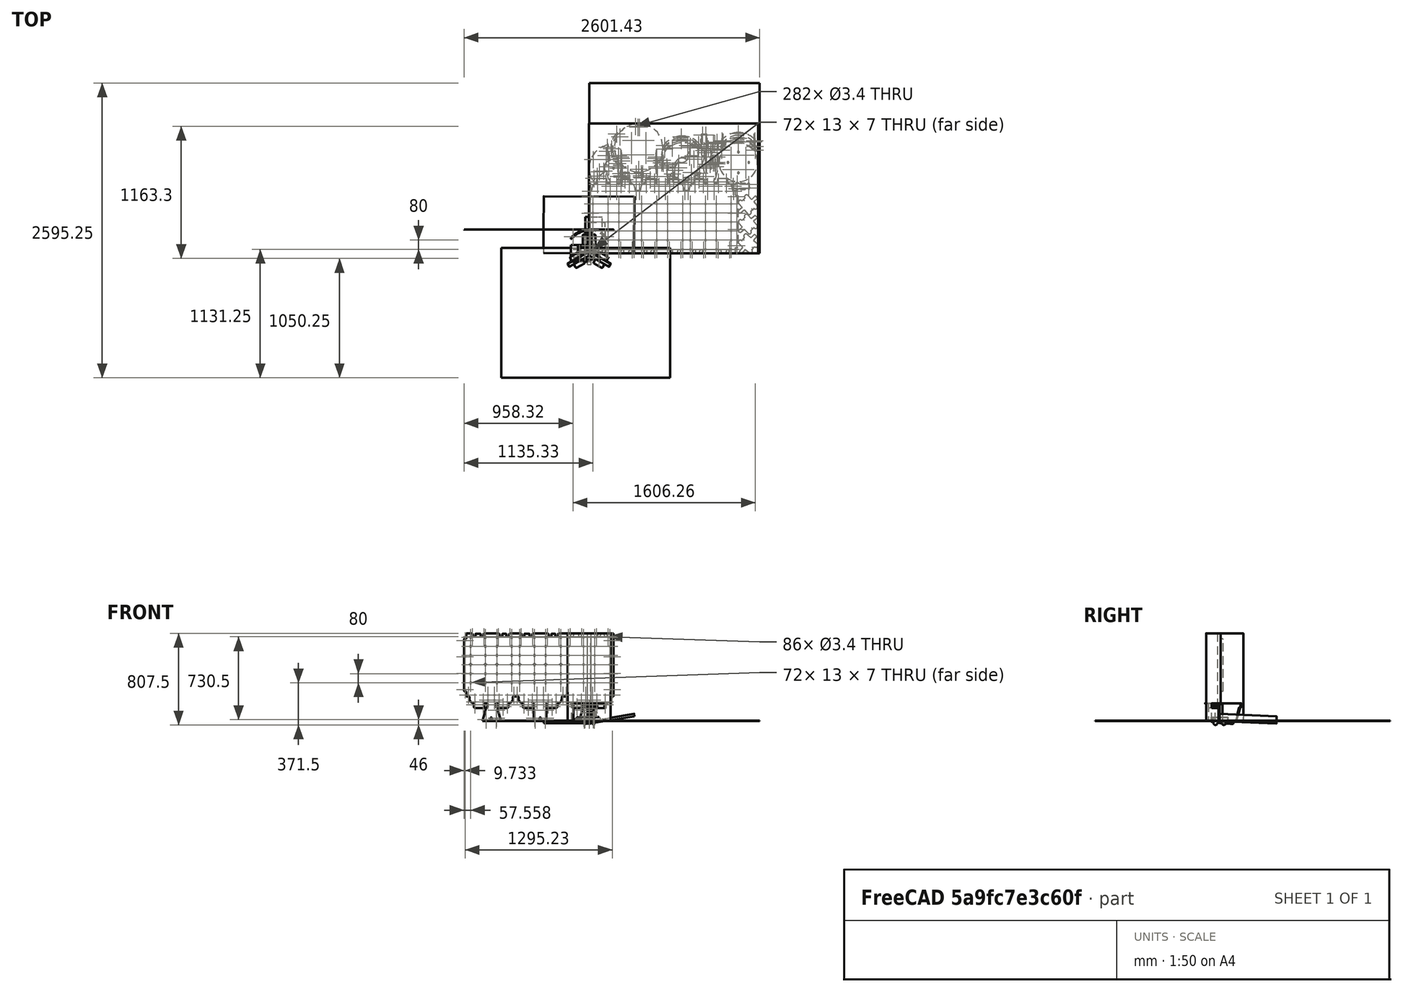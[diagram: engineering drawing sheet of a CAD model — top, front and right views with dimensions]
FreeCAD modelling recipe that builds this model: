
FCSTD DOCUMENT  (FreeCAD 0.21R31641 (Git))
Label: composit_stand_small_3_vertDroppers
License: All rights reserved
LicenseURL: http://en.wikipedia.org/wiki/All_rights_reserved
objects: Sketcher::SketchObject×99, Part::FeaturePython×74, PartDesign::Pocket×63, PartDesign::CoordinateSystem×53, PartDesign::Mirrored×27, App::DocumentObjectGroup×27, PartDesign::SubShapeBinder×27, PartDesign::Body×24, PartDesign::Plane×22, Path::FeaturePython×20, PartDesign::FeaturePython×17, PartDesign::Pad×15, Part::Part2DObjectPython×15, PartDesign::PolarPattern×13, PartDesign::MultiTransform×10, App::Link×9, Part::Feature×8, App::FeaturePython×6, Spreadsheet::Sheet×4, PartDesign::FeatureBase×3, +6 more types
note: 555 computed .brp shape members not serialized (recipe doc carries the construction recipe); baked Part::Feature solids carry a one-line shape summary decoded from their .brp

FEATURE [Spreadsheet::Sheet] Spreadsheet  label="module"
  cells = B2(module_width)==148mm; B3(module_height)==160mm; B4(module_fixture_distance_x)==132mm; C4(module_fixture_distance_y)==80mm; B5(module_hole_x)==13mm; B6(module_hole_y)==7mm
FEATURE [Spreadsheet::Sheet] Spreadsheet001  label="main"
  cells = B2(work_plane_width)==200mm; C2(top_cover_length)==108.4mm; D2(rivet_d)==3.4mm; B3(work_plane_height)==450mm; C3(work_plane_middle)==basin_height + work_plane_height / 2; D3(planes_fix_holes_distance)==130mm; B4(end_face_width)==32mm; C4(inner_width)==end_face_width - thickness * 2; D4(gutter_fix_holes_distance)==51mm; B5(basin_height)==157mm; B6(thickness)==3mm; C6(al_thickness)==0.3mm; D6(number_of_modules)=6; E6(modules_array_height)==<<module>>.module_height + (number_of_modules - 1) * <<module>>.module_fixture_distance_y; B7(total_length)==basin_height + distance_basin_cutout_modules_bottom + modules_array_height + distance_gutter_holes_modules_top + distance_gutter_holes_dropper_cutout + <<dropper>>.center_height_offset; D7(distance_basin_cutout_modules_bottom)==21mm; B8(bend_r)==0.01mm; D8(distance_gutter_holes_modules_top)==5mm; B9(cover_plane_bend)==0deg; D9(distance_gutter_holes_dropper_cutout)==12mm; B10(cover_bend_mid)==0deg
FEATURE [Sketcher::SketchObject] Sketch003  label="main_sketch"
  FullyConstrained = true
  MapMode = 5
  Support = -> [XY_Plane001]
  expr: Constraints[30] = <<main>>.end_face_width
  expr: Constraints[31] = <<main>>.work_plane_width
  expr: Constraints[44] = <<main>>.al_thickness
  sketch-geometry (17):
    g0: LineSegment StartX=-16 StartY=9.2376 StartZ=0 EndX=-16 EndY=209.238 EndZ=0
    g1: LineSegment StartX=-16 StartY=209.238 StartZ=0 EndX=16 EndY=209.238 EndZ=0
    g2: LineSegment StartX=16 StartY=209.238 StartZ=0 EndX=16 EndY=9.2376 EndZ=0
    g3: LineSegment StartX=16 StartY=9.2376 StartZ=0 EndX=189.205 EndY=-90.7624 EndZ=0
    g4: LineSegment StartX=189.205 StartY=-90.7624 StartZ=0 EndX=173.205 EndY=-118.475 EndZ=0
    g5: LineSegment StartX=173.205 StartY=-118.475 StartZ=0 EndX=0 EndY=-18.4752 EndZ=0
    g6: LineSegment StartX=0 StartY=-18.4752 StartZ=0 EndX=-173.205 EndY=-118.475 EndZ=0
    g7: LineSegment StartX=-173.205 StartY=-118.475 StartZ=0 EndX=-189.205 EndY=-90.7624 EndZ=0
    g8: LineSegment StartX=-189.205 StartY=-90.7624 StartZ=0 EndX=-16 EndY=9.2376 EndZ=0
    g9: LineSegment StartX=-16 StartY=9.2376 StartZ=0 EndX=0 EndY=0 EndZ=0
    g10: LineSegment StartX=0 StartY=0 StartZ=0 EndX=16 EndY=9.2376 EndZ=0
    g11: LineSegment StartX=0 StartY=0 StartZ=0 EndX=0 EndY=-18.4752 EndZ=0
    g12: LineSegment StartX=189.205 StartY=-90.7624 StartZ=0 EndX=13 EndY=10.9697 EndZ=0
    g13: LineSegment StartX=16 StartY=209.238 StartZ=0 EndX=16 EndY=9.42236 EndZ=0
    g14: LineSegment StartX=16 StartY=9.42236 StartZ=0 EndX=15.7 EndY=9.42236 EndZ=0
    g15: LineSegment StartX=13 StartY=10.9697 StartZ=0 EndX=13 EndY=30.9697 EndZ=0
    g16: LineSegment StartX=13 StartY=10.9697 StartZ=0 EndX=6.66667 EndY=0 EndZ=0
  constraints (56):
    c: Vertical(g0)
    c: Coincident(g0,g1)
    c: Horizontal(g1)
    c: Coincident(g1,g2)
    c: Vertical(g2)
    c: Coincident(g2,g3)
    c: Coincident(g3,g4)
    c: Coincident(g4,g5)
    c: PointOnObject(g5,g-2)
    c: Coincident(g5,g6)
    c: Coincident(g6,g7)
    c: Coincident(g8,g7)
    c: Equal(g2,g6)
    c: Equal(g6,g5)
    c: Equal(g5,g3)
    c: Equal(g4,g7)
    c: Equal(g7,g1)
    c: Perpendicular(g4,g5)
    c: Perpendicular(g4,g3)
    c: Perpendicular(g7,g6)
    c: Perpendicular(g8,g7)
    c: Angle(g6,g5) = 2.0944
    c: Angle(g3,g2) = 2.0944
    c: Coincident(g9,g0)
    c: Coincident(g9,g-1)
    c: Coincident(g10,g9)
    c: Coincident(g10,g2)
    c: Coincident(g11,g9)
    c: Coincident(g11,g5)
    c: Equal(g10,g11)
    c: DistanceX(g1,g1) = 32
    c: DistanceY(g2,g2) = 200
    c: DistanceY(g9,g2) = 9.2376  'petal_offset'
    c: DistanceY(g0) = 9.2376  'petal_conn_y'
    c: Coincident(g8,g0)
    c: DistanceX(g2) = 16  'petal_conn_x'
    c: Distance(g9,g1) = 209.848  'max_r'
    c: Distance(g10) = 18.4752  'planes_intersec_r'
    c: DistanceY(g9,g1) = 209.238  'total_petal_length'
    c: Coincident(g12,g4)
    c: Coincident(g13,g1)
    c: PointOnObject(g13,g2)
    c: Coincident(g14,g13)
    c: Horizontal(g14)
    c: DistanceX(g14,g14) = 0.3
    c: Distance(g14,g12) = 0.01
    c: PointOnObject(g2,g12)
    c: Distance(g12,g13) = 3
    c: Coincident(g15,g12)
    c: Vertical(g15)
    c: DistanceY(g15,g15) = 20
    c: DistanceY(g15) = 30.9697  'overlap_end_y'
    c: Coincident(g16,g12)
    c: Perpendicular(g16,g12)
    c: Distance(g9,g16) = 5.7735  'overlap_bend_offset'
    c: PointOnObject(g16,g-1)
FEATURE [PartDesign::FeaturePython] BaseBend001  # WARN: FeaturePython — macro-defined, semantics opaque (R4)
  BendSide = 0
  BendSketch = -> Sketch003
  MidPlane = false
  Reverse = false
  length = 774
  radius = 0.01
  thickness = 0.3
  expr: length = <<main>>.total_length
  expr: radius = <<main>>.bend_r
FEATURE [PartDesign::CoordinateSystem] Local_CS
  AttacherType = Attacher::AttachEngine3D
  AttachmentOffset = pos=(0,9.2376,0) rot=(0,0,1;0rad)
  MapMode = 5
  Placement = pos=(0,9.2376,0) rot=(0,0,1;0rad)
  Support = -> [XY_Plane001]
  expr: .AttachmentOffset.Base.y = Sketch003.Constraints.petal_offset
FEATURE [PartDesign::Plane] DatumPlane001
  AttachmentOffset = pos=(0,0,-100) rot=(0,0,1;0rad)
  Length = 488.253
  MapMode = 3
  Placement = pos=(0,109.238,-2.22e-14) rot=(1,0,0;1.5708rad)
  ResizeMode = 0
  Support = -> [Local_CS]
  Width = 908.956
  expr: .AttachmentOffset.Base.z = -<<main>>.work_plane_width / 2
FEATURE [Spreadsheet::Sheet] Spreadsheet002  label="dropper"
  cells = B2(d)==23.25mm; B3(fixture_d)=; B4(center_height_offset)==19mm; B5(distance_between_droppers1)==60mm; C5(distance_between_droppers2)==70mm
FEATURE [Sketcher::SketchObject] Sketch  label="gutter_side_sketch"
  FullyConstrained = true
  MapMode = 5
  Support = -> [XY_Plane]
  expr: .AttachmentOffset.Base.x = 0
  expr: .Constraints.little_distance = <<gutter>>.low_edge_length + (<<main>>.inner_width - <<main>>.thickness * 2) / 2 - 3mm
  expr: Constraints[12] = <<gutter>>.length
  expr: Constraints[27] = <<gutter>>.bend_angle + 90°
  sketch-geometry (15):
    g0: LineSegment StartX=0 StartY=150 StartZ=0 EndX=13.5 EndY=150 EndZ=0
    g1: LineSegment StartX=27 StartY=0 StartZ=0 EndX=0 EndY=0 EndZ=0
    g2: LineSegment StartX=15 StartY=148.5 StartZ=0 EndX=15 EndY=120 EndZ=0
    g3: LineSegment StartX=15 StartY=120 StartZ=0 EndX=31.2589 EndY=120 EndZ=0
    g4: GeomPoint X=27 Y=150 Z=0
    g5: ArcOfCircle CenterX=31.2589 CenterY=116.5 CenterZ=0 NormalX=0 NormalY=0 NormalZ=1 AngleXU=0 Radius=3.5 StartAngle=6.21662 EndAngle=7.85398
    g6: GeomPoint X=27 Y=0 Z=0
    g7: ArcOfCircle CenterX=13.5 CenterY=148.5 CenterZ=0 NormalX=0 NormalY=0 NormalZ=1 AngleXU=0 Radius=1.5 StartAngle=-3.6e-15 EndAngle=1.5708
    g8: GeomPoint X=15 Y=150 Z=0
    g9: LineSegment StartX=34.7511 StartY=116.267 StartZ=0 EndX=27.4178 EndY=6.26718 EndZ=0
    g10: LineSegment StartX=27.4178 StartY=6.26718 StartZ=0 EndX=27 EndY=0 EndZ=0
    g11: ArcOfCircle CenterX=23.9256 CenterY=6.5 CenterZ=0 NormalX=0 NormalY=0 NormalZ=1 AngleXU=0 Radius=3.5 StartAngle=4.71239 EndAngle=6.21662
    g12: LineSegment StartX=0 StartY=0 StartZ=0 EndX=0 EndY=3 EndZ=0
    g13: LineSegment StartX=0 StartY=3 StartZ=0 EndX=0 EndY=150 EndZ=0
    g14: LineSegment StartX=0 StartY=3 StartZ=0 EndX=23.9256 EndY=3 EndZ=0
  constraints (36):
    c: Coincident(g-1,g12)
    c: PointOnObject(g13,g-2)
    c: Coincident(g13,g0)
    c: Horizontal(g0)
    c: PointOnObject(g6,g-1)
    c: Coincident(g1,g12)
    c: Distance(g1,g6) = 27  'little_distance'
    c: Vertical(g2)
    c: Coincident(g3,g2)
    c: Horizontal(g3)
    c: DistanceY(g2,g8) = 30
    c: PointOnObject(g4,g0)
    c: Distance(g6,g4) = 150
    c: Distance(g0,g8) = 15
    c: Tangent(g3,g5) = 1.5708
    c: Diameter(g5) = 7
    c: PointOnObject(g8,g0)
    c: PointOnObject(g8,g2)
    c: Tangent(g0,g7) = 1.5708
    c: Tangent(g2,g7) = 1.5708
    c: Diameter(g7) = 3
    c: Tangent(g9,g5) = 1.5708
    c: Vertical(g4,g6)
    c: Coincident(g1,g6)
    c: Coincident(g10,g1)
    c: Coincident(g9,g10)
    c: Parallel(g9,g10)
    c: Angle(g10,g-1) = 1.63736
    c: Coincident(g12,g13)
    c: Vertical(g12)
    c: Coincident(g14,g12)
    c: Horizontal(g14)
    c: Tangent(g11,g9) = 1.5708
    c: Tangent(g14,g11) = -1.5708
    c: Equal(g11,g5)
    c: DistanceY(g12,g12) = 3
FEATURE [PartDesign::Pad] Pad  label="gutter_side_pad"
  Direction = (0,0,1)
  Length = 0.3
  Length2 = 10
  Profile = -> Sketch
  ReferenceAxis = -> Sketch [N_Axis]
  Type = 0
FEATURE [Sketcher::SketchObject] Sketch010
  FullyConstrained = true
  MapMode = 5
  Support = -> [XY_Plane]
  expr: Constraints[2] = -(<<main>>.inner_width / 2 - <<main>>.thickness - <<main>>.bend_r)
  expr: Constraints[3] = <<gutter>>.length
  sketch-geometry (1):
    g0: LineSegment StartX=-9.99 StartY=0 StartZ=0 EndX=-9.99 EndY=150 EndZ=0
  constraints (4):
    c: PointOnObject(g0,g-1)
    c: Vertical(g0)
    c: DistanceX(g0) = -9.99
    c: DistanceY(g0) = 150
FEATURE [PartDesign::Plane] DatumPlane002
  AttachmentOffset = pos=(0,0,407) rot=(0,0,1;0rad)
  Length = 449.761
  MapMode = 5
  Placement = pos=(0,0,407) rot=(0,0,1;0rad)
  ResizeMode = 0
  Support = -> [XY_Plane001]
  Width = 408.97
  expr: .AttachmentOffset.Base.z = <<main>>.work_plane_middle + 25mm
FEATURE [Sketcher::SketchObject] Sketch012
  FullyConstrained = true
  MapMode = 5
  Placement = pos=(0,0,0) rot=(0.57735,0.57735,0.57735;2.0944rad)
  Support = -> [YZ_Plane001]
  expr: Constraints[18] = <<main>>.total_length
  expr: Constraints[20] = <<main_sketch>>.Constraints.overlap_end_y
  sketch-geometry (10):
    g0: LineSegment StartX=0 StartY=0 StartZ=0 EndX=30.9697 EndY=0 EndZ=0
    g1: LineSegment StartX=30.9697 StartY=0 StartZ=0 EndX=30.9697 EndY=268 EndZ=0
    g2: LineSegment StartX=25.9697 StartY=263 StartZ=0 EndX=0 EndY=263 EndZ=0
    g3: LineSegment StartX=0 StartY=263 StartZ=0 EndX=0 EndY=0 EndZ=0
    g4: LineSegment StartX=0 StartY=774 StartZ=0 EndX=30.9697 EndY=774 EndZ=0
    g5: LineSegment StartX=30.9697 StartY=774 StartZ=0 EndX=30.9697 EndY=719 EndZ=0
    g6: LineSegment StartX=25.9697 StartY=724 StartZ=0 EndX=0 EndY=724 EndZ=0
    g7: LineSegment StartX=0 StartY=724 StartZ=0 EndX=0 EndY=774 EndZ=0
    g8: ArcOfCircle CenterX=25.9697 CenterY=268 CenterZ=0 NormalX=0 NormalY=0 NormalZ=1 AngleXU=0 Radius=5 StartAngle=4.71239 EndAngle=6.28319
    g9: ArcOfCircle CenterX=25.9697 CenterY=719 CenterZ=0 NormalX=0 NormalY=0 NormalZ=1 AngleXU=0 Radius=5 StartAngle=1.5481e-12 EndAngle=1.5708
  constraints (27):
    c: Coincident(g0,g1)
    c: Coincident(g2,g3)
    c: Coincident(g3,g0)
    c: Horizontal(g0)
    c: Horizontal(g2)
    c: Vertical(g1)
    c: Vertical(g3)
    c: Coincident(g0,g-1)
    c: DistanceY(g2) = 263  'bottom'
    c: Coincident(g4,g5)
    c: Coincident(g6,g7)
    c: Coincident(g7,g4)
    c: Horizontal(g4)
    c: Horizontal(g6)
    c: Vertical(g5)
    c: Vertical(g7)
    c: PointOnObject(g4,g-2)
    c: Vertical(g5,g1)
    c: DistanceY(g4) = 774
    c: DistanceY(g7,g7) = 50  'top'
    c: DistanceX(g0,g0) = 30.9697
    c: Tangent(g2,g8) = 1.5708
    c: Tangent(g1,g8) = -1.5708
    c: Tangent(g6,g9) = -1.5708
    c: Tangent(g9,g5) = 1.5708
    c: Equal(g9,g8)
    c: Diameter(g8) = 10
FEATURE [Sketcher::SketchObject] Sketch013
  AttachmentOffset = pos=(0,157,0) rot=(0,0,1;0rad)
  FullyConstrained = true
  MapMode = 5
  Placement = pos=(-3.49e-14,3.49e-14,157) rot=(0.57735,0.57735,0.57735;2.0944rad)
  Support = -> [YZ_Plane001]
  expr: .AttachmentOffset.Base.y = <<main>>.basin_height
  sketch-geometry (7):
    g0: LineSegment StartX=68 StartY=0 StartZ=0 EndX=0 EndY=0 EndZ=0
    g1: LineSegment StartX=0 StartY=0 StartZ=0 EndX=0 EndY=60 EndZ=0
    g2: LineSegment StartX=0 StartY=60 StartZ=0 EndX=31.9055 EndY=60 EndZ=0
    g3: LineSegment StartX=36.3804 StartY=57.2304 StartZ=0 EndX=63.525 EndY=2.76957 EndZ=0
    g4: ArcOfCircle CenterX=68 CenterY=5 CenterZ=0 NormalX=0 NormalY=0 NormalZ=1 AngleXU=0 Radius=5 StartAngle=3.60398 EndAngle=4.71239
    g5: ArcOfCircle CenterX=31.9055 CenterY=55 CenterZ=0 NormalX=0 NormalY=0 NormalZ=1 AngleXU=0 Radius=5 StartAngle=0.462386 EndAngle=1.5708
    g6: GeomPoint X=35 Y=60 Z=0
  constraints (17):
    c: PointOnObject(g0,g-1)
    c: Coincident(g0,g-1)
    c: Coincident(g0,g1)
    c: PointOnObject(g1,g-2)
    c: Coincident(g1,g2)
    c: Horizontal(g2)
    c: PointOnObject(g6,g2)
    c: PointOnObject(g6,g3)
    c: Tangent(g2,g5) = 1.5708
    c: Tangent(g3,g5) = 1.5708
    c: Tangent(g4,g3) = -1.5708
    c: Distance(g1) = 60
    c: Tangent(g4,g0) = 1.5708
    c: Diameter(g5) = 10
    c: Distance(g0) = 68
    c: DistanceX(g6) = 35
    c: Equal(g5,g4)
FEATURE [Spreadsheet::Sheet] Spreadsheet003  label="gutter"
  cells = B2(length)==150mm; C2(plane_middle)==60mm; B3(bend_angle)==atan((high_edge_length - low_edge_length) / length); B4(high_edge_length)==30mm; B5(low_edge_length)==20mm
FEATURE [PartDesign::Mirrored] Mirrored005
  BaseFeature = -> Pad
  MirrorPlane = -> YZ_Plane
  Originals = -> [Pad]
  Refine = true
FEATURE [PartDesign::CoordinateSystem] Local_CS001
  AttacherType = Attacher::AttachEngine3D
  AttachmentOffset = pos=(-30,0,0) rot=(0,0,1;0.066568rad)
  MapMode = 5
  Placement = pos=(-30,0,0) rot=(0,0,1;0.066568rad)
  Support = -> [XY_Plane]
  expr: .AttachmentOffset.Base.x = -(<<gutter>>.low_edge_length + (<<main>>.inner_width - <<main>>.thickness * 2) / 2)
  expr: .AttachmentOffset.Rotation.Angle = <<gutter>>.bend_angle
  expr: .AttachmentOffset.Rotation.Yaw = <<gutter>>.bend_angle
FEATURE [App::DocumentObjectGroup] Group  label="Tables"
  Group = -> [Spreadsheet,Spreadsheet001,Spreadsheet003,Spreadsheet002]
FEATURE [PartDesign::CoordinateSystem] Local_CS002
  AttacherType = Attacher::AttachEngine3D
  AttachmentOffset = pos=(30,0,0) rot=(0,0,1;-0.066568rad)
  MapMode = 5
  Placement = pos=(30,0,0) rot=(0,0,1;6.21662rad)
  Support = -> [XY_Plane]
  expr: .AttachmentOffset.Base.x = <<gutter>>.low_edge_length + (<<main>>.inner_width - <<main>>.thickness * 2) / 2
  expr: .AttachmentOffset.Rotation.Angle = -<<gutter>>.bend_angle
FEATURE [PartDesign::CoordinateSystem] Local_CS003
  AttacherType = Attacher::AttachEngine3D
  AttachmentOffset = pos=(0,60,0) rot=(0,0,1;1.5708rad)
  MapMode = 5
  Placement = pos=(33.9911,59.8671,0) rot=(0,0,1;1.50423rad)
  Support = -> [Local_CS002]
  expr: .AttachmentOffset.Base.y = <<gutter>>.plane_middle
FEATURE [PartDesign::CoordinateSystem] Local_CS004
  AttacherType = Attacher::AttachEngine3D
  AttachmentOffset = pos=(2,60,0) rot=(0,0,1;-1.5708rad)
  MapMode = 5
  Placement = pos=(-31.9956,60.0001,0) rot=(0,0,1;4.77896rad)
  Support = -> [Local_CS001]
  expr: .AttachmentOffset.Base.y = <<gutter>>.plane_middle
FEATURE [PartDesign::Plane] DatumPlane003
  Length = 91.4351
  MapMode = 4
  Placement = pos=(33.9911,59.8671,0) rot=(0.023538,0.706911,0.706911;3.09453rad)
  ResizeMode = 0
  Support = -> [Local_CS003]
  Width = 62.5599
FEATURE [PartDesign::Plane] DatumPlane004
  Length = 91.4351
  MapMode = 4
  Placement = pos=(-31.9956,60.0001,0) rot=(0.998893,0.03326,0.03326;1.5719rad)
  ResizeMode = 0
  Support = -> [Local_CS004]
  Width = 62.5599
FEATURE [PartDesign::Plane] DatumPlane005
  AttachmentOffset = pos=(0,-1,0) rot=(0,0,1;0rad)
  Length = 202.865
  MapMode = 5
  Placement = pos=(34.9889,59.8006,0) rot=(0,0,1;1.50423rad)
  ResizeMode = 0
  Support = -> [Local_CS003]
  Width = 102.646
FEATURE [PartDesign::Plane] DatumPlane006
  Length = 202.865
  MapMode = 5
  Placement = pos=(-31.9956,60.0001,0) rot=(0,0,-1;1.50423rad)
  ResizeMode = 0
  Support = -> [Local_CS004]
  Width = 102.646
FEATURE [Sketcher::SketchObject] Sketch037
  AttachmentOffset = pos=(30,2,0) rot=(0,0,1;0rad)
  FullyConstrained = true
  MapMode = 5
  Placement = pos=(33.9911,89.9337,0) rot=(0,0,1;1.50423rad)
  Support = -> [Local_CS003]
  expr: .AttachmentOffset.Base.x = <<dropper>>.distance_between_droppers1 / 2
  expr: Constraints[10] = <<dropper>>.d
  sketch-geometry (8):
    g0: LineSegment StartX=0 StartY=11.625 StartZ=0 EndX=1 EndY=11.625 EndZ=0
    g1: ArcOfCircle CenterX=1 CenterY=0 CenterZ=0 NormalX=0 NormalY=0 NormalZ=1 AngleXU=0 Radius=11.625 StartAngle=0.450911 EndAngle=1.5708
    g2: ArcOfCircle CenterX=17.127 CenterY=0 CenterZ=0 NormalX=0 NormalY=0 NormalZ=1 AngleXU=0 Radius=3 StartAngle=0.25268 EndAngle=1.29556
    g3: LineSegment StartX=12.0914 StartY=4.53943 StartZ=0 EndX=17.9423 EndY=2.88708 EndZ=0
    g4: LineSegment StartX=0 StartY=11.625 StartZ=0 EndX=0 EndY=0 EndZ=0
    g5: LineSegment StartX=0 StartY=0 StartZ=0 EndX=21 EndY=0 EndZ=0
    g6: ArcOfCircle CenterX=21 CenterY=1 CenterZ=0 NormalX=0 NormalY=0 NormalZ=1 AngleXU=0 Radius=1 StartAngle=3.39427 EndAngle=4.71239
    g7: ArcOfCircle CenterX=12.3631 CenterY=5.5018 CenterZ=0 NormalX=0 NormalY=0 NormalZ=1 AngleXU=0 Radius=1 StartAngle=3.5925 EndAngle=4.43715
  constraints (22):
    c: PointOnObject(g0,g-2)
    c: Horizontal(g0)
    c: PointOnObject(g2,g-1)
    c: Tangent(g3,g2) = 1.5708
    c: Tangent(g1,g0) = 1.5708
    c: Coincident(g4,g0)
    c: Coincident(g4,g-1)
    c: Coincident(g5,g4)
    c: Diameter(g2) = 6
    c: Angle(g3,g-1) = 0.275238
    c: Diameter(g1) = 23.25
    c: PointOnObject(g1,g-1)
    c: Distance(g0) = 1
    c: Horizontal(g5)
    c: Tangent(g6,g5) = -1.5708
    c: Tangent(g6,g2) = 1.5708
    c: Diameter(g6) = 2
    c: Distance(g5) = 21
    c: Tangent(g3,g7) = -1.5708
    c: Tangent(g1,g7) = 1.5708
    c: Diameter(g7) = 2
    c: DistanceY(g2) = 2.88708  'arc_height'
FEATURE [PartDesign::Pocket] Pocket008
  BaseFeature = -> Mirrored005
  Direction = (0,0,-1)
  Length = 5
  Length2 = 5
  Midplane = true
  Profile = -> Sketch037
  ReferenceAxis = -> Sketch037 [N_Axis]
  Type = 1
FEATURE [PartDesign::Mirrored] Mirrored006
  MirrorPlane = -> Sketch037 [V_Axis]
FEATURE [PartDesign::Mirrored] Mirrored007
  MirrorPlane = -> DatumPlane003
FEATURE [PartDesign::MultiTransform] MultiTransform002
  BaseFeature = -> Pocket008
  Originals = -> [Pocket008]
  Transformations = -> [Mirrored006,Mirrored007]
FEATURE [PartDesign::SubShapeBinder] Binder
  AttacherType = Attacher::AttachEngine3D
  AttachmentOffset = pos=(35,0,0) rot=(0,0,1;0rad)
  BindCopyOnChange = 0
  BindMode = 0
  ClaimChildren = true
  Context = -> Body [Binder.]
  Fuse = false
  MakeFace = true
  MapMode = 5
  OffsetFill = false
  OffsetIntersection = false
  OffsetJoinType = 0
  OffsetOpenResult = false
  PartialLoad = false
  Placement = pos=(-28.1674,25.0777,0) rot=(0,0,-1;1.50423rad)
  Relative = false
  _Version = 2
  expr: .AttachmentOffset.Base.x = <<dropper>>.distance_between_droppers2 / 2
FEATURE [PartDesign::Pocket] Pocket009
  BaseFeature = -> MultiTransform002
  Direction = (0,0,-1)
  Length = 5
  Length2 = 5
  Midplane = true
  Profile = -> Binder
  Type = 1
FEATURE [PartDesign::Plane] DatumPlane007
  Length = 91.4351
  MapMode = 4
  Placement = pos=(-28.1674,25.0777,0) rot=(0.998893,0.03326,0.03326;1.5719rad)
  ResizeMode = 0
  Support = -> [Binder]
  Width = 62.5599
FEATURE [PartDesign::Mirrored] Mirrored008
  MirrorPlane = -> DatumPlane007
FEATURE [PartDesign::Mirrored] Mirrored009
  MirrorPlane = -> DatumPlane004
FEATURE [PartDesign::MultiTransform] MultiTransform003
  BaseFeature = -> Pocket009
  Originals = -> [Pocket009]
  Transformations = -> [Mirrored008,Mirrored009]
FEATURE [Sketcher::SketchObject] Sketch038
  FullyConstrained = true
  MapMode = 5
  Support = -> [XY_Plane]
  expr: Constraints[2] = <<main>>.inner_width / 2 - <<main>>.thickness - <<main>>.bend_r
  expr: Constraints[3] = <<gutter>>.length
  sketch-geometry (1):
    g0: LineSegment StartX=9.99 StartY=0 StartZ=0 EndX=9.99 EndY=150 EndZ=0
  constraints (4):
    c: PointOnObject(g0,g-1)
    c: Vertical(g0)
    c: DistanceX(g0) = 9.99
    c: DistanceY(g0) = 150
FEATURE [Sketcher::SketchObject] Sketch039
  AttachmentOffset = pos=(51,14,0) rot=(0,0,1;0rad)
  FullyConstrained = true
  MapMode = 5
  Placement = pos=(24.4124,111.619,0) rot=(0,0,1;1.50423rad)
  Support = -> [DatumPlane005]
  expr: .AttachmentOffset.Base.x = <<main>>.gutter_fix_holes_distance
  expr: Constraints[1] = <<main>>.rivet_d
  sketch-geometry (1):
    g0: Circle CenterX=0 CenterY=0 CenterZ=0 NormalX=0 NormalY=0 NormalZ=1 AngleXU=0 Radius=1.7
  constraints (2):
    c: Coincident(g0,g-1)
    c: Diameter(g0) = 3.4
FEATURE [PartDesign::Pocket] Pocket010
  BaseFeature = -> MultiTransform003
  Direction = (0,0,-1)
  Length = 5
  Length2 = 5
  Midplane = true
  Profile = -> Sketch039
  ReferenceAxis = -> Sketch039 [N_Axis]
  Type = 1
FEATURE [PartDesign::Mirrored] Mirrored010
  MirrorPlane = -> DatumPlane003
FEATURE [PartDesign::Mirrored] Mirrored011
  MirrorPlane = -> YZ_Plane
FEATURE [PartDesign::MultiTransform] MultiTransform004
  BaseFeature = -> Pocket010
  Originals = -> [Pocket010]
  Transformations = -> [Mirrored010,Mirrored011]
FEATURE [PartDesign::FeaturePython] Fold  # WARN: FeaturePython — macro-defined, semantics opaque (R4)
  BaseFeature = -> MultiTransform004
  BendLine = -> Sketch038
  Position = 0
  angle = 90
  baseObject = -> MultiTransform004 [Face4]
  invert = false
  invertbend = true
  kfactor = 0.01
  radius = 0.01
  unfold = false
  expr: radius = <<main>>.bend_r
FEATURE [PartDesign::FeaturePython] Fold002  # WARN: FeaturePython — macro-defined, semantics opaque (R4)
  BaseFeature = -> Fold
  BendLine = -> Sketch010
  Position = 0
  angle = 90
  baseObject = -> Fold [Face2]
  invert = false
  invertbend = false
  kfactor = 0.01
  radius = 0.01
  unfold = false
  expr: radius = <<main>>.bend_r
FEATURE [PartDesign::CoordinateSystem] LCS_Origin
  AttacherType = Attacher::AttachEngine3D
  MapMode = 2
  Support = -> [X_Axis012]
FEATURE [App::DocumentObjectGroup] Constraints
FEATURE [App::FeaturePython] Variables  # WARN: FeaturePython — macro-defined, semantics opaque (R4)
  Type = App::PropertyContainer
FEATURE [App::DocumentObjectGroup] Configurations
FEATURE [PartDesign::CoordinateSystem] Local_CS008
  AttacherType = Attacher::AttachEngine3D
  MapMode = 5
  Support = -> [XY_Plane001]
FEATURE [App::Link] Body001001
  AssemblyType = Part::Link
  AttachedBy = #Local_CS008
  AttachedTo = Parent Assembly#LCS_Origin
  LinkedObject = -> Body001
  SolverId = Asm4EE
  expr: Placement = LCS_Origin.Placement * AttachmentOffset * Local_CS008.Placement ^ -1
FEATURE [App::Link] Body001003001
  AssemblyType = Part::Link
  AttachedBy = #Local_CS009
  AttachedTo = Body001001#Local_CS038
  AttachmentOffset = pos=(0,0,0) rot=(0.58,0.58,-0.58;2.0944rad)
  LinkPlacement = pos=(0,109.238,738) rot=(-0.707107,0,-0.707107;3.14159rad)
  LinkedObject = -> Body001003
  Placement = pos=(0,109.238,738) rot=(-0.707107,0,-0.707107;3.14159rad)
  SolverId = Asm4EE
  expr: Placement = Body001001.Placement * Local_CS038.Placement * AttachmentOffset * Local_CS009.Placement ^ -1
FEATURE [PartDesign::PolarPattern] PolarPattern002
  Angle = 240
  Axis = -> Z_Axis001
  Occurrences = 2
  Reversed = true
  expr: Angle = 120 * Occurrences
FEATURE [PartDesign::CoordinateSystem] Local_CS011
  AttacherType = Attacher::AttachEngine3D
  AttachmentOffset = pos=(0,100,0) rot=(0,0,1;0rad)
  MapMode = 5
  Placement = pos=(0,109.238,0) rot=(0,0,1;0rad)
  Support = -> [Local_CS]
  expr: .AttachmentOffset.Base.y = <<main>>.work_plane_width / 2
FEATURE [PartDesign::Plane] DatumPlane
  Length = 441.366
  MapMode = 4
  Placement = pos=(0,109.238,0) rot=(0.57735,0.57735,0.57735;2.0944rad)
  ResizeMode = 0
  Support = -> [Local_CS011]
  Width = 902.859
FEATURE [Sketcher::SketchObject] Sketch011
  AttachmentOffset = pos=(-88,277,0) rot=(0,0,1;0rad)
  FullyConstrained = true
  MapMode = 5
  Placement = pos=(0,21.2376,277) rot=(0.57735,0.57735,0.57735;2.0944rad)
  Support = -> [DatumPlane]
  expr: .AttachmentOffset.Base.x = -<<main>>.work_plane_width / 2 + 12mm
  expr: .AttachmentOffset.Base.y = <<main>>.work_plane_middle - <<main>>.planes_fix_holes_distance + 25mm
  expr: Constraints[1] = <<main>>.rivet_d
  sketch-geometry (1):
    g0: Circle CenterX=0 CenterY=0 CenterZ=0 NormalX=0 NormalY=0 NormalZ=1 AngleXU=0 Radius=1.7
  constraints (2):
    c: Coincident(g0,g-1)
    c: Diameter(g0) = 3.4
FEATURE [PartDesign::Plane] DatumPlane011
  AttachmentOffset = pos=(0,0,0) rot=(0,0,1;0.523599rad)
  Length = 594.137
  MapMode = 5
  Placement = pos=(0,0,0) rot=(0,0,1;0.523599rad)
  ResizeMode = 0
  Support = -> [XY_Plane001]
  Width = 579.207
FEATURE [PartDesign::Plane] DatumPlane013
  AttachmentOffset = pos=(0,0,0) rot=(0,-1,0;0.523599rad)
  Length = 622.32
  MapMode = 5
  Placement = pos=(0,0,0) rot=(0.935113,-0.250563,-0.250563;1.63783rad)
  ResizeMode = 0
  Support = -> [XZ_Plane001]
  Width = 924.952
FEATURE [PartDesign::Mirrored] Mirrored013
  MirrorPlane = -> DatumPlane013
FEATURE [PartDesign::Plane] DatumPlane014
  AttachmentOffset = pos=(0,0,0) rot=(0.447214,0.774597,-0.447214;1.82348rad)
  Length = 924.952
  MapMode = 5
  Placement = pos=(0,0,0) rot=(0.447214,0.774597,-0.447214;1.82348rad)
  ResizeMode = 0
  Support = -> [XY_Plane001]
  Width = 622.32
FEATURE [Sketcher::SketchObject] Sketch047
  FullyConstrained = true
  MapMode = 5
  Support = -> [XY_Plane015]
  expr: Constraints[16] = Sketch003.Constraints.max_r
  expr: Constraints[20] = <<main>>.work_plane_width
  sketch-geometry (8):
    g0: ArcOfCircle CenterX=0 CenterY=18.4752 CenterZ=0 NormalX=0 NormalY=0 NormalZ=1 AngleXU=0 Radius=60 StartAngle=0.539993 EndAngle=1.5708
    g1: ArcOfCircle CenterX=52.3205 CenterY=49.8371 CenterZ=0 NormalX=0 NormalY=0 NormalZ=1 AngleXU=0 Radius=1 StartAngle=3.68159 EndAngle=5.23599
    g2: LineSegment StartX=52.8205 StartY=48.9711 StartZ=0 EndX=172.268 EndY=117.934 EndZ=0
    g3: ArcOfCircle CenterX=171.768 CenterY=118.8 CenterZ=0 NormalX=0 NormalY=0 NormalZ=1 AngleXU=0 Radius=1 StartAngle=5.23599 EndAngle=6.88827
    g4: ArcOfCircle CenterX=0 CenterY=0 CenterZ=0 NormalX=0 NormalY=0 NormalZ=1 AngleXU=0 Radius=209.848 StartAngle=0.605088 EndAngle=1.5708
    g5: LineSegment StartX=3.7e-15 StartY=78.4752 StartZ=0 EndX=1.28e-14 EndY=209.848 EndZ=0
    g6: LineSegment StartX=52.8205 StartY=48.9711 StartZ=0 EndX=0 EndY=18.4752 EndZ=0
    g7: GeomPoint X=173.205 Y=118.475 Z=0
  constraints (22):
    c: PointOnObject(g0,g-2)
    c: PointOnObject(g4,g-2)
    c: Diameter(g1) = 2
    c: Diameter(g3) = 2
    c: Tangent(g1,g0) = 1.5708
    c: Tangent(g3,g2) = -1.5708
    c: Angle(g2,g-1) = 2.61799
    c: Coincident(g5,g0)
    c: Coincident(g5,g4)
    c: Tangent(g1,g2) = -1.5708
    c: Coincident(g6,g1)
    c: Tangent(g6,g2)
    c: Coincident(g6,g0)
    c: Diameter(g0) = 120
    c: PointOnObject(g7,g4)
    c: PointOnObject(g7,g2)
    c: DistanceY(g4) = 209.848
    c: Distance(g4,g0) = 18.4752  'major_r_offset'
    c: Coincident(g4,g-1)
    c: PointOnObject(g0,g-2)
    c: Distance(g0,g7) = 200
    c: Tangent(g3,g4) = -1.5708
FEATURE [PartDesign::Pad] Pad012
  Direction = (0,0,1)
  Length = 3
  Length2 = 10
  Profile = -> Sketch047
  ReferenceAxis = -> Sketch047 [N_Axis]
  Type = 0
FEATURE [PartDesign::CoordinateSystem] Local_CS013
  AttacherType = Attacher::AttachEngine3D
  MapMode = 5
  Support = -> [XY_Plane015]
FEATURE [PartDesign::CoordinateSystem] Local_CS015
  AttacherType = Attacher::AttachEngine3D
  AttachmentOffset = pos=(0,0,157) rot=(0,0,1;0rad)
  MapMode = 6
  Placement = pos=(189.205,-90.7624,157) rot=(0,0,1;3.14159rad)
  Support = -> [Sketch003,XY_Plane001]
  expr: .AttachmentOffset.Base.z = <<main>>.basin_height
FEATURE [App::Link] Body001003005002
  AssemblyType = Part::Link
  AttachedBy = #Local_CS013
  AttachedTo = Body001001#Local_CS025
  AttachmentOffset = pos=(0,0,0) rot=(0,0,1;3.14159rad)
  LinkPlacement = pos=(0,0,157) rot=(0,0,1;3.14159rad)
  LinkedObject = -> Body001003005
  Placement = pos=(0,0,157) rot=(0,0,1;3.14159rad)
  SolverId = Asm4EE
  expr: Placement = Body001001.Placement * Local_CS025.Placement * AttachmentOffset * Local_CS013.Placement ^ -1
FEATURE [PartDesign::CoordinateSystem] Local_CS016
  AttacherType = Attacher::AttachEngine3D
  AttachmentOffset = pos=(0,0,0) rot=(0,0,1;0.523599rad)
  MapMode = 5
  Placement = pos=(0,0,0) rot=(0,0,1;0.523599rad)
  Support = -> [XY_Plane015]
FEATURE [PartDesign::Plane] DatumPlane015
  Length = 495.835
  MapMode = 5
  Placement = pos=(0,0,0) rot=(0,0,1;0.523599rad)
  ResizeMode = 0
  Support = -> [Local_CS016]
  Width = 455.324
FEATURE [PartDesign::Plane] DatumPlane016
  Length = 79.989
  MapMode = 4
  Placement = pos=(86.82,84.1932,0) rot=(0.377964,0.654654,0.654654;2.41886rad)
  ResizeMode = 0
  Width = 61.6877
FEATURE [Sketcher::SketchObject] Sketch048
  FullyConstrained = true
  MapMode = 5
  Support = -> [XY_Plane016]
  expr: Constraints[1] = Sketch003.Constraints.max_r + 2.5mm
  sketch-geometry (1):
    g0: Circle CenterX=0 CenterY=0 CenterZ=0 NormalX=0 NormalY=0 NormalZ=1 AngleXU=0 Radius=212.348
  constraints (2):
    c: Coincident(g0,g-1)
    c: Radius(g0) = 212.348
FEATURE [PartDesign::Pad] Pad013
  Direction = (0,0,1)
  Length = 3
  Length2 = 10
  Profile = -> Sketch048
  ReferenceAxis = -> Sketch048 [N_Axis]
  Type = 0
  expr: Length = <<main>>.thickness
FEATURE [Sketcher::SketchObject] Sketch049
  AttachmentOffset = pos=(0,196.563,0) rot=(0,0,1;0rad)
  FullyConstrained = true
  MapMode = 5
  Placement = pos=(0,196.563,0) rot=(0,0,1;0rad)
  Support = -> [XY_Plane016]
  expr: .AttachmentOffset.Base.y = Sketch003.Constraints.total_petal_length - .Constraints.cut_width / 2 - 3.175mm - <<main>>.thickness
  expr: Constraints[10] = <<main>>.inner_width / 2
  expr: Constraints[14] = -<<main>>.inner_width / 2
  sketch-geometry (9):
    g0: ArcOfCircle CenterX=-13 CenterY=8.0875 CenterZ=0 NormalX=0 NormalY=0 NormalZ=1 AngleXU=0 Radius=1.5875 StartAngle=1.5708 EndAngle=4.71239
    g1: LineSegment StartX=-13 StartY=6.5 StartZ=0 EndX=9.825 EndY=6.5 EndZ=0
    g2: LineSegment StartX=9.825 StartY=6.5 StartZ=0 EndX=9.825 EndY=0 EndZ=0
    g3: LineSegment StartX=9.825 StartY=0 StartZ=0 EndX=13 EndY=0 EndZ=0
    g4: LineSegment StartX=13 StartY=0 StartZ=0 EndX=13 EndY=6.5 EndZ=0
    g5: LineSegment StartX=-13 StartY=9.675 StartZ=0 EndX=9.825 EndY=9.675 EndZ=0
    g6: ArcOfCircle CenterX=9.825 CenterY=6.5 CenterZ=0 NormalX=0 NormalY=0 NormalZ=1 AngleXU=0 Radius=3.175 StartAngle=1.117e-13 EndAngle=1.5708
    g7: GeomPoint X=9.825 Y=-6.5 Z=0
    g8: GeomPoint X=9.825 Y=-9.675 Z=0
  constraints (21):
    c: Horizontal(g1)
    c: PointOnObject(g2,g-1)
    c: Vertical(g2)
    c: Coincident(g3,g2)
    c: PointOnObject(g3,g-1)
    c: Coincident(g4,g3)
    c: Vertical(g4)
    c: Horizontal(g5)
    c: Tangent(g6,g4) = -1.5708
    c: Tangent(g6,g5) = 1.5708
    c: DistanceX(g3) = 13
    c: Tangent(g1,g0) = -1.5708
    c: Tangent(g5,g0) = 1.5708
    c: Diameter(g0) = 3.175
    c: DistanceX(g0) = -13
    c: Coincident(g6,g2)
    c: Coincident(g2,g1)
    c: Symmetric(g7,g1,g2)
    c: DistanceY(g7,g1) = 13  'cut_width'
    c: Symmetric(g8,g5,g2)
    c: DistanceY(g8,g5) = 19.35  'total_width'
FEATURE [Sketcher::SketchObject] Sketch050
  AttachmentOffset = pos=(0,196.563,0) rot=(0,0,1;0rad)
  FullyConstrained = true
  MapMode = 5
  Placement = pos=(0,196.563,0) rot=(0,0,1;0rad)
  Support = -> [XY_Plane016]
  expr: .AttachmentOffset.Base.y = Sketch049.AttachmentOffset.Base.y
  expr: .Constraints.cut_width = Sketch049.Constraints[18]
  expr: Constraints[10] = Sketch049.Constraints[10]
  expr: Constraints[13] = Sketch049.Constraints[13]
  expr: Constraints[14] = Sketch049.Constraints[14]
  expr: Constraints[29] = Sketch049.Constraints[10]
  expr: Constraints[32] = Sketch049.Constraints[13]
  expr: Constraints[33] = Sketch049.Constraints[14]
  sketch-geometry (17):
    g0: LineSegment StartX=-13 StartY=-8.0875 StartZ=0 EndX=-13 EndY=8.0875 EndZ=0
    g1: ArcOfCircle CenterX=-13 CenterY=8.0875 CenterZ=0 NormalX=0 NormalY=0 NormalZ=1 AngleXU=0 Radius=1.5875 StartAngle=1.5708 EndAngle=4.71239
    g2: LineSegment StartX=-13 StartY=6.5 StartZ=0 EndX=9.825 EndY=6.5 EndZ=0
    g3: LineSegment StartX=9.825 StartY=6.5 StartZ=0 EndX=9.825 EndY=0 EndZ=0
    g4: LineSegment StartX=9.825 StartY=0 StartZ=0 EndX=13 EndY=0 EndZ=0
    g5: LineSegment StartX=13 StartY=0 StartZ=0 EndX=13 EndY=6.5 EndZ=0
    g6: LineSegment StartX=-13 StartY=9.675 StartZ=0 EndX=9.825 EndY=9.675 EndZ=0
    g7: ArcOfCircle CenterX=9.825 CenterY=6.5 CenterZ=0 NormalX=0 NormalY=0 NormalZ=1 AngleXU=0 Radius=3.175 StartAngle=1.742e-13 EndAngle=1.5708
    g8: GeomPoint X=9.825 Y=-6.5 Z=0
    g9: ArcOfCircle CenterX=-11.5 CenterY=11.5875 CenterZ=0 NormalX=0 NormalY=0 NormalZ=1 AngleXU=0 Radius=1.5875 StartAngle=1.5708 EndAngle=4.71239
    g10: LineSegment StartX=-11.5 StartY=10 StartZ=0 EndX=9.825 EndY=10 EndZ=0
    g11: LineSegment StartX=9.825 StartY=10 StartZ=0 EndX=9.825 EndY=0 EndZ=0
    g12: LineSegment StartX=9.825 StartY=0 StartZ=0 EndX=13 EndY=0 EndZ=0
    g13: LineSegment StartX=13 StartY=0 StartZ=0 EndX=13 EndY=10 EndZ=0
    g14: LineSegment StartX=-11.5 StartY=13.175 StartZ=0 EndX=9.825 EndY=13.175 EndZ=0
    g15: ArcOfCircle CenterX=9.825 CenterY=10 CenterZ=0 NormalX=0 NormalY=0 NormalZ=1 AngleXU=0 Radius=3.175 StartAngle=1e-16 EndAngle=1.5708
    g16: GeomPoint X=9.825 Y=-10 Z=0
  constraints (40):
    c: Horizontal(g2)
    c: PointOnObject(g3,g-1)
    c: Vertical(g3)
    c: Coincident(g4,g3)
    c: PointOnObject(g4,g-1)
    c: Coincident(g5,g4)
    c: Vertical(g5)
    c: Horizontal(g6)
    c: Tangent(g7,g5) = -1.5708
    c: Tangent(g7,g6) = 1.5708
    c: DistanceX(g4) = 13
    c: Tangent(g2,g1) = -1.5708
    c: Tangent(g6,g1) = 1.5708
    c: Diameter(g1) = 3.175
    c: DistanceX(g1) = -13
    c: Coincident(g7,g3)
    c: Coincident(g3,g2)
    c: Symmetric(g8,g2,g3)
    c: DistanceY(g8,g2) = 13  'cut_width'
    c: Horizontal(g10)
    c: PointOnObject(g11,g-1)
    c: Vertical(g11)
    c: Coincident(g12,g11)
    c: PointOnObject(g12,g-1)
    c: Coincident(g13,g12)
    c: Vertical(g13)
    c: Horizontal(g14)
    c: Tangent(g15,g13) = -1.5708
    c: Tangent(g15,g14) = 1.5708
    c: DistanceX(g12) = 13
    c: Tangent(g10,g9) = -1.5708
    c: Tangent(g14,g9) = 1.5708
    c: Diameter(g9) = 3.175
    c: DistanceX(g9) = -11.5
    c: Coincident(g15,g11)
    c: Coincident(g11,g10)
    c: Symmetric(g16,g10,g11)
    c: DistanceY(g16,g10) = 20  'cut_width'
    c: Coincident(g0,g1)
    c: Symmetric(g0,g0,g-1)
FEATURE [PartDesign::CoordinateSystem] Local_CS017
  AttacherType = Attacher::AttachEngine3D
  AttachmentOffset = pos=(0,0,3) rot=(0,0,1;0rad)
  MapMode = 5
  Placement = pos=(0,0,3) rot=(0,0,1;0rad)
  Support = -> [XY_Plane016]
  expr: .AttachmentOffset.Base.z = <<main>>.thickness
FEATURE [App::Link] Body001003005003002
  AssemblyType = Part::Link
  AttachedBy = #Local_CS017
  AttachedTo = Parent Assembly#LCS_Origin
  AttachmentOffset = pos=(0,0,-3) rot=(0,1,0;3.14159rad)
  LinkPlacement = pos=(-4e-16,0,0) rot=(0,1,0;3.14159rad)
  LinkedObject = -> Body001003005003
  Placement = pos=(-4e-16,0,0) rot=(0,1,0;3.14159rad)
  SolverId = Asm4EE
  expr: Placement = LCS_Origin.Placement * AttachmentOffset * Local_CS017.Placement ^ -1
FEATURE [PartDesign::SubShapeBinder] Binder004
  AttacherType = Attacher::AttachEngine3D
  AttachmentOffset = pos=(0,196.563,0) rot=(0,0,1;3.14159rad)
  BindCopyOnChange = 0
  BindMode = 0
  ClaimChildren = false
  Context = -> Model [Body001003005003002.Binder004.]
  Fuse = false
  MakeFace = true
  MapMode = 5
  OffsetFill = false
  OffsetIntersection = false
  OffsetJoinType = 0
  OffsetOpenResult = false
  PartialLoad = false
  Placement = pos=(0,180.388,0) rot=(0,0,1;3.14159rad)
  Relative = false
  _Version = 2
  expr: .AttachmentOffset.Base.y = <<main>>.work_plane_width + Sketch003.Constraints.petal_offset - <<main>>.thickness - 3.175mm - Sketch049.Constraints.cut_width / 2
  expr: .Placement.Base.y = Sketch049.AttachmentOffset.Base.y - Sketch049.Constraints.cut_width - 3.175mm
FEATURE [PartDesign::Plane] DatumPlane017
  Length = 453.129
  MapMode = 3
  Placement = pos=(0,180.388,0) rot=(0,0.707107,0.707107;3.14159rad)
  ResizeMode = 0
  Support = -> [Binder004]
  Width = 79.1207
FEATURE [Sketcher::SketchObject] Sketch051
  AttachmentOffset = pos=(0,180.388,0) rot=(0,0,1;0rad)
  FullyConstrained = true
  MapMode = 5
  Placement = pos=(0,180.388,0) rot=(0,0,1;0rad)
  Support = -> [XY_Plane016]
  expr: .AttachmentOffset.Base.y = Binder004.Placement.Base.y
  expr: .Constraints.cut_width = Sketch049.Constraints[18]
  expr: Constraints[10] = Sketch049.Constraints[10]
  expr: Constraints[13] = Sketch049.Constraints[13]
  expr: Constraints[14] = Sketch049.Constraints[14]
  sketch-geometry (9):
    g0: ArcOfCircle CenterX=-11.5 CenterY=8.0875 CenterZ=0 NormalX=0 NormalY=0 NormalZ=1 AngleXU=0 Radius=1.5875 StartAngle=1.5708 EndAngle=4.71239
    g1: LineSegment StartX=-11.5 StartY=6.5 StartZ=0 EndX=9.825 EndY=6.5 EndZ=0
    g2: LineSegment StartX=9.825 StartY=6.5 StartZ=0 EndX=9.825 EndY=0 EndZ=0
    g3: LineSegment StartX=9.825 StartY=0 StartZ=0 EndX=13 EndY=0 EndZ=0
    g4: LineSegment StartX=13 StartY=0 StartZ=0 EndX=13 EndY=6.5 EndZ=0
    g5: LineSegment StartX=-11.5 StartY=9.675 StartZ=0 EndX=9.825 EndY=9.675 EndZ=0
    g6: ArcOfCircle CenterX=9.825 CenterY=6.5 CenterZ=0 NormalX=0 NormalY=0 NormalZ=1 AngleXU=0 Radius=3.175 StartAngle=0 EndAngle=1.5708
    g7: GeomPoint X=9.825 Y=-6.5 Z=0
    g8: LineSegment StartX=11.5 StartY=8.0875 StartZ=0 EndX=11.5 EndY=-8.0875 EndZ=0
  constraints (22):
    c: Horizontal(g1)
    c: PointOnObject(g2,g-1)
    c: Vertical(g2)
    c: Coincident(g3,g2)
    c: PointOnObject(g3,g-1)
    c: Coincident(g4,g3)
    c: Vertical(g4)
    c: Horizontal(g5)
    c: Tangent(g6,g4) = -1.5708
    c: Tangent(g6,g5) = 1.5708
    c: DistanceX(g3) = 13
    c: Tangent(g1,g0) = -1.5708
    c: Tangent(g5,g0) = 1.5708
    c: Diameter(g0) = 3.175
    c: DistanceX(g0) = -11.5
    c: Coincident(g6,g2)
    c: Coincident(g2,g1)
    c: Symmetric(g7,g1,g2)
    c: DistanceY(g7,g1) = 13  'cut_width'
    c: Vertical(g8)
    c: Symmetric(g0,g8,g-1)
    c: Horizontal(g8,g0)
FEATURE [Sketcher::SketchObject] Sketch052
  FullyConstrained = true
  MapMode = 5
  Support = -> [XY_Plane017]
  expr: .Constraints.r = Sketch003.Constraints.max_r
  expr: Constraints[13] = 15mm + <<main>>.end_face_width / 2
  sketch-geometry (6):
    g0: ArcOfCircle CenterX=0 CenterY=0 CenterZ=0 NormalX=0 NormalY=0 NormalZ=1 AngleXU=0 Radius=199.848 StartAngle=0.699923 EndAngle=1.5708
    g1: ArcOfCircle CenterX=0 CenterY=0 CenterZ=0 NormalX=0 NormalY=0 NormalZ=1 AngleXU=0 Radius=209.848 StartAngle=0.699923 EndAngle=1.5708
    g2: ArcOfCircle CenterX=156.687 CenterY=131.955 CenterZ=0 NormalX=0 NormalY=0 NormalZ=1 AngleXU=0 Radius=5 StartAngle=3.84152 EndAngle=6.98311
    g3: LineSegment StartX=1.22e-14 StartY=199.848 StartZ=0 EndX=1.28e-14 EndY=209.848 EndZ=0
    g4: ArcOfCircle CenterX=0 CenterY=0 CenterZ=0 NormalX=0 NormalY=0 NormalZ=1 AngleXU=0 Radius=204.848 StartAngle=0.675514 EndAngle=1.5708
    g5: LineSegment StartX=0 StartY=0 StartZ=0 EndX=177.404 EndY=102.424 EndZ=0
  constraints (18):
    c: Coincident(g0,g-1)
    c: PointOnObject(g0,g-2)
    c: Coincident(g1,g0)
    c: PointOnObject(g1,g-2)
    c: Coincident(g3,g1)
    c: DistanceY(g1) = 209.848  'r'
    c: DistanceY(g0,g1) = 10  'width'
    c: Tangent(g2,g0) = 1.5708
    c: Tangent(g2,g1) = -1.5708
    c: Coincident(g4,g0)
    c: PointOnObject(g4,g2)
    c: Coincident(g5,g0)
    c: Angle(g-1,g5) = 0.523599
    c: Distance(g4,g5) = 31
    c: Coincident(g3,g0)
    c: PointOnObject(g2,g4)
    c: PointOnObject(g4,g-2)
    c: PointOnObject(g5,g4)
FEATURE [PartDesign::Pad] Pad014
  Direction = (0,0,1)
  Length = 3
  Length2 = 10
  Profile = -> Sketch052
  ReferenceAxis = -> Sketch052 [N_Axis]
  Type = 0
FEATURE [PartDesign::CoordinateSystem] Local_CS018
  AttacherType = Attacher::AttachEngine3D
  MapMode = 5
  Support = -> [XY_Plane017]
FEATURE [PartDesign::CoordinateSystem] Local_CS019
  AttacherType = Attacher::AttachEngine3D
  MapMode = 5
  Support = -> [XY_Plane018]
FEATURE [Sketcher::SketchObject] Sketch055
  FullyConstrained = true
  MapMode = 5
  Support = -> [XY_Plane017]
  expr: .Constraints.r = Sketch052.Constraints[5]
  expr: .Constraints.width = Sketch052.Constraints[6]
  expr: Constraints[12] = Sketch052.Constraints[12]
  expr: Constraints[13] = Sketch052.Constraints[13]
  expr: Constraints[25] = <<main>>.rivet_d
  sketch-geometry (9):
    g0: ArcOfCircle CenterX=0 CenterY=0 CenterZ=0 NormalX=0 NormalY=0 NormalZ=1 AngleXU=0 Radius=199.848 StartAngle=0.699923 EndAngle=1.5708
    g1: ArcOfCircle CenterX=0 CenterY=0 CenterZ=0 NormalX=0 NormalY=0 NormalZ=1 AngleXU=0 Radius=209.848 StartAngle=0.699923 EndAngle=1.5708
    g2: ArcOfCircle CenterX=156.687 CenterY=131.955 CenterZ=0 NormalX=0 NormalY=0 NormalZ=1 AngleXU=0 Radius=5 StartAngle=3.84152 EndAngle=6.98311
    g3: LineSegment StartX=1.22e-14 StartY=199.848 StartZ=0 EndX=1.28e-14 EndY=209.848 EndZ=0
    g4: ArcOfCircle CenterX=0 CenterY=0 CenterZ=0 NormalX=0 NormalY=0 NormalZ=1 AngleXU=0 Radius=204.848 StartAngle=0.675514 EndAngle=1.5708
    g5: LineSegment StartX=0 StartY=0 StartZ=0 EndX=177.404 EndY=102.424 EndZ=0
    g6: LineSegment StartX=1.22e-14 StartY=203.148 StartZ=0 EndX=1.31e-14 EndY=206.548 EndZ=0
    g7: ArcOfCircle CenterX=1.25e-14 CenterY=204.848 CenterZ=0 NormalX=0 NormalY=0 NormalZ=1 AngleXU=0 Radius=1.7 StartAngle=4.71239 EndAngle=7.85398
    g8: Circle CenterX=143.11 CenterY=146.569 CenterZ=0 NormalX=0 NormalY=0 NormalZ=1 AngleXU=0 Radius=1.7
  constraints (27):
    c: Coincident(g0,g-1)
    c: PointOnObject(g0,g-2)
    c: Coincident(g1,g0)
    c: PointOnObject(g1,g-2)
    c: Coincident(g3,g1)
    c: DistanceY(g1) = 209.848  'r'
    c: DistanceY(g0,g1) = 10  'width'
    c: Tangent(g2,g0) = 1.5708
    c: Tangent(g2,g1) = -1.5708
    c: Coincident(g4,g0)
    c: PointOnObject(g4,g2)
    c: Coincident(g5,g0)
    c: Angle(g-1,g5) = 0.523599
    c: Distance(g4,g5) = 31
    c: Coincident(g3,g0)
    c: PointOnObject(g2,g4)
    c: PointOnObject(g4,g-2)
    c: PointOnObject(g5,g4)
    c: PointOnObject(g6,g3)
    c: PointOnObject(g6,g3)
    c: Coincident(g7,g4)
    c: Coincident(g7,g6)
    c: Coincident(g7,g6)
    c: PointOnObject(g8,g4)
    c: Equal(g8,g7)
    c: Diameter(g7) = 3.4
    c: DistanceX(g8) = 143.11
FEATURE [PartDesign::Pocket] Pocket019
  BaseFeature = -> Pad014
  Direction = (0,0,-1)
  Length = 5
  Length2 = 5
  Midplane = true
  Profile = -> Sketch055
  ReferenceAxis = -> Sketch055 [N_Axis]
  Type = 1
FEATURE [PartDesign::Mirrored] Mirrored019
  BaseFeature = -> Pocket019
  MirrorPlane = -> Sketch052 [V_Axis]
  Originals = -> [Pad014,Pocket019]
FEATURE [PartDesign::Body] Body001003005003003
  Group = -> [Sketch052,Pad014,Pocket019,Mirrored019,Local_CS018,Sketch055]
  Origin = -> Origin016
  Tip = -> Mirrored019
FEATURE [PartDesign::SubShapeBinder] Binder005
  AttacherType = Attacher::AttachEngine3D
  AttachmentOffset = pos=(0,0,0) rot=(0,0,1;1.0472rad)
  BindCopyOnChange = 0
  BindMode = 0
  ClaimChildren = false
  Context = -> Body001003005003 [Binder005.]
  Fuse = false
  MakeFace = true
  MapMode = 5
  OffsetFill = false
  OffsetIntersection = false
  OffsetJoinType = 0
  OffsetOpenResult = false
  PartialLoad = false
  Placement = pos=(0,0,0) rot=(0,0,1;1.0472rad)
  Relative = false
  _Version = 2
FEATURE [PartDesign::Plane] DatumPlane018
  Length = 613.419
  MapMode = 4
  Placement = pos=(0,0,0) rot=(0.186157,0.694747,0.694747;2.77349rad)
  ResizeMode = 0
  Support = -> [Binder005]
  Width = 84.0405
FEATURE [Sketcher::SketchObject] Sketch057
  AttachmentOffset = pos=(196.563,-11.5,0) rot=(0,0,1;0rad)
  FullyConstrained = true
  MapMode = 5
  Placement = pos=(4.62e-14,196.563,-11.5) rot=(0.57735,0.57735,0.57735;2.0944rad)
  Support = -> [YZ_Plane015]
  expr: .AttachmentOffset.Base.x = Sketch049.AttachmentOffset.Base.y
  expr: .AttachmentOffset.Base.y = -23mm / 2
  expr: Constraints[1] = <<main>>.rivet_d
  sketch-geometry (1):
    g0: Circle CenterX=0 CenterY=0 CenterZ=0 NormalX=0 NormalY=0 NormalZ=1 AngleXU=0 Radius=1.7
  constraints (2):
    c: Coincident(g0,g-1)
    c: Diameter(g0) = 3.4
FEATURE [Sketcher::SketchObject] Sketch058
  AttachmentOffset = pos=(180.388,-11.5,0) rot=(0,0,1;0rad)
  FullyConstrained = true
  MapMode = 5
  Placement = pos=(4.26e-14,180.388,-11.5) rot=(0.57735,0.57735,0.57735;2.0944rad)
  Support = -> [YZ_Plane015]
  expr: .AttachmentOffset.Base.x = Binder004.Placement.Base.y
  expr: .AttachmentOffset.Base.y = Sketch057.AttachmentOffset.Base.y
  expr: Constraints[1] = <<main>>.rivet_d
  sketch-geometry (1):
    g0: Circle CenterX=0 CenterY=0 CenterZ=0 NormalX=0 NormalY=0 NormalZ=1 AngleXU=0 Radius=1.7
  constraints (2):
    c: Coincident(g0,g-1)
    c: Diameter(g0) = 3.4
FEATURE [PartDesign::Pocket] Pocket027
  BaseFeature = -> Pad013
  Direction = (-1,2e-16,-3e-16)
  Length = 5
  Length2 = 5
  Midplane = true
  Profile = -> Sketch058
  ReferenceAxis = -> Sketch058 [N_Axis]
  Type = 1
FEATURE [Sketcher::SketchObject] Sketch059
  AttachmentOffset = pos=(196.563,11.5,0) rot=(0,0,1;0rad)
  FullyConstrained = true
  MapMode = 5
  Placement = pos=(4.11e-14,196.563,11.5) rot=(0.57735,0.57735,0.57735;2.0944rad)
  Support = -> [YZ_Plane001]
  expr: .AttachmentOffset.Base.x = Sketch057.AttachmentOffset.Base.x
  expr: .AttachmentOffset.Base.y = -Sketch057.AttachmentOffset.Base.y
  expr: Constraints[1] = <<main>>.rivet_d
  sketch-geometry (1):
    g0: Circle CenterX=0 CenterY=0 CenterZ=0 NormalX=0 NormalY=0 NormalZ=1 AngleXU=0 Radius=1.7
  constraints (2):
    c: Coincident(g0,g-1)
    c: Diameter(g0) = 3.4
FEATURE [Sketcher::SketchObject] Sketch060
  AttachmentOffset = pos=(180.388,11.5,0) rot=(0,0,1;0rad)
  FullyConstrained = true
  MapMode = 5
  Placement = pos=(3.75e-14,180.388,11.5) rot=(0.57735,0.57735,0.57735;2.0944rad)
  Support = -> [YZ_Plane001]
  expr: .AttachmentOffset.Base.x = Sketch058.AttachmentOffset.Base.x
  expr: .AttachmentOffset.Base.y = -Sketch058.AttachmentOffset.Base.y
  expr: Constraints[1] = <<main>>.rivet_d
  sketch-geometry (1):
    g0: Circle CenterX=0 CenterY=0 CenterZ=0 NormalX=0 NormalY=0 NormalZ=1 AngleXU=0 Radius=1.7
  constraints (2):
    c: Coincident(g0,g-1)
    c: Diameter(g0) = 3.4
FEATURE [PartDesign::CoordinateSystem] Local_CS021
  AttacherType = Attacher::AttachEngine3D
  AttachmentOffset = pos=(0,0,0) rot=(0,0,1;2.0944rad)
  MapMode = 5
  Placement = pos=(0,0,0) rot=(0,0,1;2.0944rad)
  Support = -> [XY_Plane016]
FEATURE [PartDesign::CoordinateSystem] Local_CS022
  AttacherType = Attacher::AttachEngine3D
  AttachmentOffset = pos=(0,0,0) rot=(0,0,-1;2.0944rad)
  MapMode = 5
  Placement = pos=(0,0,0) rot=(0,0,-1;2.0944rad)
  Support = -> [XY_Plane016]
FEATURE [PartDesign::Plane] DatumPlane019
  Length = 695.392
  MapMode = 5
  Placement = pos=(0,0,0) rot=(0,0,1;2.0944rad)
  ResizeMode = 0
  Support = -> [Local_CS021]
  Width = 695.266
FEATURE [PartDesign::Plane] DatumPlane020
  Length = 695.392
  MapMode = 5
  Placement = pos=(0,0,0) rot=(0,0,-1;2.0944rad)
  ResizeMode = 0
  Support = -> [Local_CS022]
  Width = 695.266
FEATURE [Sketcher::SketchObject] Sketch061
  AttachmentOffset = pos=(0,196.563,0) rot=(0,0,1;0rad)
  FullyConstrained = true
  MapMode = 5
  Placement = pos=(-170.228,-98.2813,0) rot=(0,0,1;2.0944rad)
  Support = -> [DatumPlane019]
  expr: .AttachmentOffset.Base.y = Sketch050.Placement.Base.y
  expr: .Constraints.cut_width = 13
  expr: Constraints[10] = Sketch050.Constraints[10]
  expr: Constraints[13] = Sketch050.Constraints[13]
  expr: Constraints[14] = Sketch050.Constraints[14]
  expr: Constraints[29] = Sketch050.Constraints[29]
  expr: Constraints[32] = Sketch050.Constraints[32]
  expr: Constraints[33] = Sketch050.Constraints[33]
  sketch-geometry (17):
    g0: LineSegment StartX=-13 StartY=-8.0875 StartZ=0 EndX=-13 EndY=8.0875 EndZ=0
    g1: ArcOfCircle CenterX=-13 CenterY=8.0875 CenterZ=0 NormalX=0 NormalY=0 NormalZ=1 AngleXU=0 Radius=1.5875 StartAngle=1.5708 EndAngle=4.71239
    g2: LineSegment StartX=-13 StartY=6.5 StartZ=0 EndX=9.825 EndY=6.5 EndZ=0
    g3: LineSegment StartX=9.825 StartY=6.5 StartZ=0 EndX=9.825 EndY=0 EndZ=0
    g4: LineSegment StartX=9.825 StartY=0 StartZ=0 EndX=13 EndY=0 EndZ=0
    g5: LineSegment StartX=13 StartY=0 StartZ=0 EndX=13 EndY=6.5 EndZ=0
    g6: LineSegment StartX=-13 StartY=9.675 StartZ=0 EndX=9.825 EndY=9.675 EndZ=0
    g7: ArcOfCircle CenterX=9.825 CenterY=6.5 CenterZ=0 NormalX=0 NormalY=0 NormalZ=1 AngleXU=0 Radius=3.175 StartAngle=1.743e-13 EndAngle=1.5708
    g8: GeomPoint X=9.825 Y=-6.5 Z=0
    g9: ArcOfCircle CenterX=-11.5 CenterY=11.5875 CenterZ=0 NormalX=0 NormalY=0 NormalZ=1 AngleXU=0 Radius=1.5875 StartAngle=1.5708 EndAngle=4.71239
    g10: LineSegment StartX=-11.5 StartY=10 StartZ=0 EndX=9.825 EndY=10 EndZ=0
    g11: LineSegment StartX=9.825 StartY=10 StartZ=0 EndX=9.825 EndY=0 EndZ=0
    g12: LineSegment StartX=9.825 StartY=0 StartZ=0 EndX=13 EndY=0 EndZ=0
    g13: LineSegment StartX=13 StartY=0 StartZ=0 EndX=13 EndY=10 EndZ=0
    g14: LineSegment StartX=-11.5 StartY=13.175 StartZ=0 EndX=9.825 EndY=13.175 EndZ=0
    g15: ArcOfCircle CenterX=9.825 CenterY=10 CenterZ=0 NormalX=0 NormalY=0 NormalZ=1 AngleXU=0 Radius=3.175 StartAngle=1e-16 EndAngle=1.5708
    g16: GeomPoint X=9.825 Y=-10 Z=0
  constraints (40):
    c: Horizontal(g2)
    c: PointOnObject(g3,g-1)
    c: Vertical(g3)
    c: Coincident(g4,g3)
    c: PointOnObject(g4,g-1)
    c: Coincident(g5,g4)
    c: Vertical(g5)
    c: Horizontal(g6)
    c: Tangent(g7,g5) = -1.5708
    c: Tangent(g7,g6) = 1.5708
    c: DistanceX(g4) = 13
    c: Tangent(g2,g1) = -1.5708
    c: Tangent(g6,g1) = 1.5708
    c: Diameter(g1) = 3.175
    c: DistanceX(g1) = -13
    c: Coincident(g7,g3)
    c: Coincident(g3,g2)
    c: Symmetric(g8,g2,g3)
    c: DistanceY(g8,g2) = 13  'cut_width'
    c: Horizontal(g10)
    c: PointOnObject(g11,g-1)
    c: Vertical(g11)
    c: Coincident(g12,g11)
    c: PointOnObject(g12,g-1)
    c: Coincident(g13,g12)
    c: Vertical(g13)
    c: Horizontal(g14)
    c: Tangent(g15,g13) = -1.5708
    c: Tangent(g15,g14) = 1.5708
    c: DistanceX(g12) = 13
    c: Tangent(g10,g9) = -1.5708
    c: Tangent(g14,g9) = 1.5708
    c: Diameter(g9) = 3.175
    c: DistanceX(g9) = -11.5
    c: Coincident(g15,g11)
    c: Coincident(g11,g10)
    c: Symmetric(g16,g10,g11)
    c: DistanceY(g16,g10) = 20  'cut_width'
    c: Coincident(g0,g1)
    c: Symmetric(g0,g0,g-1)
FEATURE [Sketcher::SketchObject] Sketch062
  AttachmentOffset = pos=(0,196.563,0) rot=(0,0,1;0rad)
  FullyConstrained = true
  MapMode = 5
  Placement = pos=(170.228,-98.2813,0) rot=(0,0,-1;2.0944rad)
  Support = -> [DatumPlane020]
  expr: .Constraints.cut_width = 13
  expr: AttachmentOffset = Sketch050.AttachmentOffset
  expr: Constraints[10] = Sketch050.Constraints[10]
  expr: Constraints[13] = Sketch050.Constraints[13]
  expr: Constraints[14] = Sketch050.Constraints[14]
  expr: Constraints[29] = Sketch050.Constraints[29]
  expr: Constraints[32] = Sketch050.Constraints[32]
  expr: Constraints[33] = Sketch050.Constraints[33]
  sketch-geometry (17):
    g0: LineSegment StartX=-13 StartY=-8.0875 StartZ=0 EndX=-13 EndY=8.0875 EndZ=0
    g1: ArcOfCircle CenterX=-13 CenterY=8.0875 CenterZ=0 NormalX=0 NormalY=0 NormalZ=1 AngleXU=0 Radius=1.5875 StartAngle=1.5708 EndAngle=4.71239
    g2: LineSegment StartX=-13 StartY=6.5 StartZ=0 EndX=9.825 EndY=6.5 EndZ=0
    g3: LineSegment StartX=9.825 StartY=6.5 StartZ=0 EndX=9.825 EndY=0 EndZ=0
    g4: LineSegment StartX=9.825 StartY=0 StartZ=0 EndX=13 EndY=0 EndZ=0
    g5: LineSegment StartX=13 StartY=0 StartZ=0 EndX=13 EndY=6.5 EndZ=0
    g6: LineSegment StartX=-13 StartY=9.675 StartZ=0 EndX=9.825 EndY=9.675 EndZ=0
    g7: ArcOfCircle CenterX=9.825 CenterY=6.5 CenterZ=0 NormalX=0 NormalY=0 NormalZ=1 AngleXU=0 Radius=3.175 StartAngle=1.743e-13 EndAngle=1.5708
    g8: GeomPoint X=9.825 Y=-6.5 Z=0
    g9: ArcOfCircle CenterX=-11.5 CenterY=11.5875 CenterZ=0 NormalX=0 NormalY=0 NormalZ=1 AngleXU=0 Radius=1.5875 StartAngle=1.5708 EndAngle=4.71239
    g10: LineSegment StartX=-11.5 StartY=10 StartZ=0 EndX=9.825 EndY=10 EndZ=0
    g11: LineSegment StartX=9.825 StartY=10 StartZ=0 EndX=9.825 EndY=0 EndZ=0
    g12: LineSegment StartX=9.825 StartY=0 StartZ=0 EndX=13 EndY=0 EndZ=0
    g13: LineSegment StartX=13 StartY=0 StartZ=0 EndX=13 EndY=10 EndZ=0
    g14: LineSegment StartX=-11.5 StartY=13.175 StartZ=0 EndX=9.825 EndY=13.175 EndZ=0
    g15: ArcOfCircle CenterX=9.825 CenterY=10 CenterZ=0 NormalX=0 NormalY=0 NormalZ=1 AngleXU=0 Radius=3.175 StartAngle=1e-16 EndAngle=1.5708
    g16: GeomPoint X=9.825 Y=-10 Z=0
  constraints (40):
    c: Horizontal(g2)
    c: PointOnObject(g3,g-1)
    c: Vertical(g3)
    c: Coincident(g4,g3)
    c: PointOnObject(g4,g-1)
    c: Coincident(g5,g4)
    c: Vertical(g5)
    c: Horizontal(g6)
    c: Tangent(g7,g5) = -1.5708
    c: Tangent(g7,g6) = 1.5708
    c: DistanceX(g4) = 13
    c: Tangent(g2,g1) = -1.5708
    c: Tangent(g6,g1) = 1.5708
    c: Diameter(g1) = 3.175
    c: DistanceX(g1) = -13
    c: Coincident(g7,g3)
    c: Coincident(g3,g2)
    c: Symmetric(g8,g2,g3)
    c: DistanceY(g8,g2) = 13  'cut_width'
    c: Horizontal(g10)
    c: PointOnObject(g11,g-1)
    c: Vertical(g11)
    c: Coincident(g12,g11)
    c: PointOnObject(g12,g-1)
    c: Coincident(g13,g12)
    c: Vertical(g13)
    c: Horizontal(g14)
    c: Tangent(g15,g13) = -1.5708
    c: Tangent(g15,g14) = 1.5708
    c: DistanceX(g12) = 13
    c: Tangent(g10,g9) = -1.5708
    c: Tangent(g14,g9) = 1.5708
    c: Diameter(g9) = 3.175
    c: DistanceX(g9) = -11.5
    c: Coincident(g15,g11)
    c: Coincident(g11,g10)
    c: Symmetric(g16,g10,g11)
    c: DistanceY(g16,g10) = 20  'cut_width'
    c: Coincident(g0,g1)
    c: Symmetric(g0,g0,g-1)
FEATURE [Sketcher::SketchObject] Sketch063
  AttachmentOffset = pos=(0,180.388,0) rot=(0,0,1;0rad)
  FullyConstrained = true
  MapMode = 5
  Placement = pos=(-156.22,-90.1938,0) rot=(0,0,1;2.0944rad)
  Support = -> [DatumPlane019]
  expr: .Constraints.cut_width = Sketch051.Constraints[18]
  expr: AttachmentOffset = Sketch051.AttachmentOffset
  expr: Constraints[10] = Sketch051.Constraints[10]
  expr: Constraints[13] = Sketch051.Constraints[13]
  expr: Constraints[14] = Sketch051.Constraints[14]
  sketch-geometry (9):
    g0: ArcOfCircle CenterX=-11.5 CenterY=8.0875 CenterZ=0 NormalX=0 NormalY=0 NormalZ=1 AngleXU=0 Radius=1.5875 StartAngle=1.5708 EndAngle=4.71239
    g1: LineSegment StartX=-11.5 StartY=6.5 StartZ=0 EndX=9.825 EndY=6.5 EndZ=0
    g2: LineSegment StartX=9.825 StartY=6.5 StartZ=0 EndX=9.825 EndY=0 EndZ=0
    g3: LineSegment StartX=9.825 StartY=0 StartZ=0 EndX=13 EndY=0 EndZ=0
    g4: LineSegment StartX=13 StartY=0 StartZ=0 EndX=13 EndY=6.5 EndZ=0
    g5: LineSegment StartX=-11.5 StartY=9.675 StartZ=0 EndX=9.825 EndY=9.675 EndZ=0
    g6: ArcOfCircle CenterX=9.825 CenterY=6.5 CenterZ=0 NormalX=0 NormalY=0 NormalZ=1 AngleXU=0 Radius=3.175 StartAngle=0 EndAngle=1.5708
    g7: GeomPoint X=9.825 Y=-6.5 Z=0
    g8: LineSegment StartX=11.5 StartY=8.0875 StartZ=0 EndX=11.5 EndY=-8.0875 EndZ=0
  constraints (22):
    c: Horizontal(g1)
    c: PointOnObject(g2,g-1)
    c: Vertical(g2)
    c: Coincident(g3,g2)
    c: PointOnObject(g3,g-1)
    c: Coincident(g4,g3)
    c: Vertical(g4)
    c: Horizontal(g5)
    c: Tangent(g6,g4) = -1.5708
    c: Tangent(g6,g5) = 1.5708
    c: DistanceX(g3) = 13
    c: Tangent(g1,g0) = -1.5708
    c: Tangent(g5,g0) = 1.5708
    c: Diameter(g0) = 3.175
    c: DistanceX(g0) = -11.5
    c: Coincident(g6,g2)
    c: Coincident(g2,g1)
    c: Symmetric(g7,g1,g2)
    c: DistanceY(g7,g1) = 13  'cut_width'
    c: Vertical(g8)
    c: Symmetric(g0,g8,g-1)
    c: Horizontal(g8,g0)
FEATURE [Sketcher::SketchObject] Sketch064
  AttachmentOffset = pos=(0,180.388,0) rot=(0,0,1;0rad)
  FullyConstrained = true
  MapMode = 5
  Placement = pos=(156.22,-90.1938,0) rot=(0,0,-1;2.0944rad)
  Support = -> [DatumPlane020]
  expr: .Constraints.cut_width = Sketch051.Constraints[18]
  expr: AttachmentOffset = Sketch051.AttachmentOffset
  expr: Constraints[10] = Sketch051.Constraints[10]
  expr: Constraints[13] = Sketch051.Constraints[13]
  expr: Constraints[14] = Sketch051.Constraints[14]
  sketch-geometry (9):
    g0: ArcOfCircle CenterX=-11.5 CenterY=8.0875 CenterZ=0 NormalX=0 NormalY=0 NormalZ=1 AngleXU=0 Radius=1.5875 StartAngle=1.5708 EndAngle=4.71239
    g1: LineSegment StartX=-11.5 StartY=6.5 StartZ=0 EndX=9.825 EndY=6.5 EndZ=0
    g2: LineSegment StartX=9.825 StartY=6.5 StartZ=0 EndX=9.825 EndY=0 EndZ=0
    g3: LineSegment StartX=9.825 StartY=0 StartZ=0 EndX=13 EndY=0 EndZ=0
    g4: LineSegment StartX=13 StartY=0 StartZ=0 EndX=13 EndY=6.5 EndZ=0
    g5: LineSegment StartX=-11.5 StartY=9.675 StartZ=0 EndX=9.825 EndY=9.675 EndZ=0
    g6: ArcOfCircle CenterX=9.825 CenterY=6.5 CenterZ=0 NormalX=0 NormalY=0 NormalZ=1 AngleXU=0 Radius=3.175 StartAngle=0 EndAngle=1.5708
    g7: GeomPoint X=9.825 Y=-6.5 Z=0
    g8: LineSegment StartX=11.5 StartY=8.0875 StartZ=0 EndX=11.5 EndY=-8.0875 EndZ=0
  constraints (22):
    c: Horizontal(g1)
    c: PointOnObject(g2,g-1)
    c: Vertical(g2)
    c: Coincident(g3,g2)
    c: PointOnObject(g3,g-1)
    c: Coincident(g4,g3)
    c: Vertical(g4)
    c: Horizontal(g5)
    c: Tangent(g6,g4) = -1.5708
    c: Tangent(g6,g5) = 1.5708
    c: DistanceX(g3) = 13
    c: Tangent(g1,g0) = -1.5708
    c: Tangent(g5,g0) = 1.5708
    c: Diameter(g0) = 3.175
    c: DistanceX(g0) = -11.5
    c: Coincident(g6,g2)
    c: Coincident(g2,g1)
    c: Symmetric(g7,g1,g2)
    c: DistanceY(g7,g1) = 13  'cut_width'
    c: Vertical(g8)
    c: Symmetric(g0,g8,g-1)
    c: Horizontal(g8,g0)
FEATURE [PartDesign::CoordinateSystem] Local_CS023
  AttacherType = Attacher::AttachEngine3D
  AttachmentOffset = pos=(0,0,157) rot=(0,0,1;0rad)
  MapMode = 5
  Placement = pos=(0,109.238,157) rot=(0,0,1;0rad)
  Support = -> [Local_CS011]
  expr: .AttachmentOffset.Base.z = <<main>>.basin_height
FEATURE [Sketcher::SketchObject] Sketch070
  AttachmentOffset = pos=(0,770,0) rot=(0,0,1;0rad)
  FullyConstrained = true
  MapMode = 5
  Placement = pos=(0,109.238,770) rot=(0.57735,0.57735,0.57735;2.0944rad)
  Support = -> [DatumPlane]
  expr: .AttachmentOffset.Base.y = <<main>>.total_length - Constraints[5]
  expr: Constraints[9] = <<main>>.top_cover_length
  sketch-geometry (4):
    g0: LineSegment StartX=54.2 StartY=4 StartZ=0 EndX=-54.2 EndY=4 EndZ=0
    g1: LineSegment StartX=-54.2 StartY=4 StartZ=0 EndX=-54.2 EndY=0 EndZ=0
    g2: LineSegment StartX=-54.2 StartY=0 StartZ=0 EndX=54.2 EndY=0 EndZ=0
    g3: LineSegment StartX=54.2 StartY=0 StartZ=0 EndX=54.2 EndY=4 EndZ=0
  constraints (11):
    c: Coincident(g2,g3)
    c: Coincident(g3,g0)
    c: Horizontal(g2)
    c: Vertical(g1)
    c: Vertical(g3)
    c: DistanceY(g0) = 4
    c: Coincident(g1,g2)
    c: Coincident(g1,g0)
    c: PointOnObject(g1,g-1)
    c: DistanceX(g0,g0) = 108.4
    c: Symmetric(g0,g0,g-2)
FEATURE [PartDesign::Plane] DatumPlane021
  AttachmentOffset = pos=(0,0,0) rot=(0,-1,0;1.0472rad)
  Length = 622.32
  MapMode = 5
  Placement = pos=(0,0,0) rot=(0.935113,0.250563,0.250563;1.63783rad)
  ResizeMode = 0
  Support = -> [YZ_Plane001]
  Width = 924.952
FEATURE [PartDesign::Plane] DatumPlane022
  AttachmentOffset = pos=(0,0,16) rot=(0,0,1;0rad)
  Length = 441.366
  MapMode = 4
  Placement = pos=(16,109.238,157) rot=(0.57735,0.57735,0.57735;2.0944rad)
  ResizeMode = 0
  Support = -> [Local_CS023]
  Width = 902.859
  expr: .AttachmentOffset.Base.z = <<main>>.end_face_width / 2
FEATURE [PartDesign::Mirrored] Mirrored027
  MirrorPlane = -> YZ_Plane001
FEATURE [PartDesign::CoordinateSystem] Local_CS024
  AttacherType = Attacher::AttachEngine3D
  AttachmentOffset = pos=(0,60,-10.3215) rot=(-1,0,0;0.066568rad)
  MapMode = 5
  Placement = pos=(0,60,-10.3215) rot=(-1,0,0;0.066568rad)
  Support = -> [XY_Plane]
  expr: .AttachmentOffset.Base.y = <<gutter>>.plane_middle
  expr: .AttachmentOffset.Base.z = (-6.929mm - 13.714mm) / 2
  expr: .AttachmentOffset.Rotation.Roll = -<<gutter>>.bend_angle
FEATURE [App::Link] gutter001  label="gutter002"
  AssemblyType = Part::Link
  AttachedBy = #Local_CS024
  AttachedTo = Body001001#Local_CS037
  AttachmentOffset = pos=(0,1,0) rot=(-1,0,0;3.14159rad)
  LinkPlacement = pos=(0,170.791,736.693) rot=(-1,0,0;3.07502rad)
  LinkedObject = -> Body
  Placement = pos=(0,170.791,736.693) rot=(-1,0,0;3.07502rad)
  SolverId = Asm4EE
  expr: Placement = Body001001.Placement * Local_CS037.Placement * AttachmentOffset * Local_CS024.Placement ^ -1
FEATURE [Sketcher::SketchObject] Sketch075
  AttachmentOffset = pos=(0,0,0) rot=(0,0,1;3.14159rad)
  FullyConstrained = true
  MapMode = 5
  Placement = pos=(0,0,0) rot=(0,0,1;3.14159rad)
  Support = -> [XY_Plane016]
  expr: Constraints[12] = 186.5mm - 3.175mm
  expr: Constraints[6] = <<main>>.rivet_d
  sketch-geometry (6):
    g0: Circle CenterX=64.8152 CenterY=64.8152 CenterZ=0 NormalX=0 NormalY=0 NormalZ=1 AngleXU=0 Radius=1.7
    g1: Circle CenterX=64.8152 CenterY=-64.8152 CenterZ=0 NormalX=0 NormalY=0 NormalZ=1 AngleXU=0 Radius=1.7
    g2: Circle CenterX=-64.8152 CenterY=-64.8152 CenterZ=0 NormalX=0 NormalY=0 NormalZ=1 AngleXU=0 Radius=1.7
    g3: Circle CenterX=-64.8152 CenterY=64.8152 CenterZ=0 NormalX=0 NormalY=0 NormalZ=1 AngleXU=0 Radius=1.7
    g4: LineSegment StartX=-64.8152 StartY=64.8152 StartZ=0 EndX=64.8152 EndY=64.8152 EndZ=0
    g5: LineSegment StartX=64.8152 StartY=64.8152 StartZ=0 EndX=64.8152 EndY=-64.8152 EndZ=0
  constraints (13):
    c: Symmetric(g3,g0,g-2)
    c: Symmetric(g0,g1,g-1)
    c: Symmetric(g0,g2,g-1)
    c: Equal(g0,g3)
    c: Equal(g0,g2)
    c: Equal(g0,g1)
    c: Diameter(g0) = 3.4
    c: Coincident(g4,g3)
    c: Coincident(g4,g0)
    c: Coincident(g5,g0)
    c: Coincident(g5,g1)
    c: Equal(g5,g4)
    c: Distance(g2,g0) = 183.325
FEATURE [PartDesign::Pocket] Pocket036
  BaseFeature = -> Pocket027
  Direction = (0,0,-1)
  Length = 5
  Length2 = 5
  Midplane = true
  Profile = -> Sketch075
  ReferenceAxis = -> Sketch075 [N_Axis]
  Type = 1
FEATURE [Sketcher::SketchObject] Sketch076
  FullyConstrained = true
  MapMode = 5
  Support = -> [XY_Plane025]
  expr: Constraints[1] = (180mm - 11.5mm) * 2
  sketch-geometry (1):
    g0: Circle CenterX=0 CenterY=0 CenterZ=0 NormalX=0 NormalY=0 NormalZ=1 AngleXU=0 Radius=168.5
  constraints (2):
    c: Coincident(g0,g-1)
    c: Diameter(g0) = 337
FEATURE [PartDesign::Pad] Pad020
  Direction = (0,0,1)
  Length = 3
  Length2 = 10
  Profile = -> Sketch076
  ReferenceAxis = -> Sketch076 [N_Axis]
  Type = 0
FEATURE [Sketcher::SketchObject] Sketch078
  FullyConstrained = true
  MapMode = 5
  Placement = pos=(0,0,0) rot=(1,0,0;1.5708rad)
  Support = -> [XZ_Plane025]
FEATURE [Sketcher::SketchObject] Sketch079
  FullyConstrained = true
  MapMode = 5
  Placement = pos=(0,0,0) rot=(0.57735,0.57735,0.57735;2.0944rad)
  Support = -> [YZ_Plane025]
  expr: Constraints[8] = <<main>>.basin_height
  sketch-geometry (3):
    g0: LineSegment StartX=15 StartY=0 StartZ=0 EndX=0 EndY=0 EndZ=0
    g1: LineSegment StartX=0 StartY=0 StartZ=0 EndX=0 EndY=157 EndZ=0
    g2: LineSegment StartX=0 StartY=157 StartZ=0 EndX=15 EndY=157 EndZ=0
  constraints (9):
    c: PointOnObject(g0,g-1)
    c: Coincident(g0,g-1)
    c: Coincident(g1,g0)
    c: PointOnObject(g1,g-2)
    c: Coincident(g2,g1)
    c: Horizontal(g2)
    c: DistanceX(g0,g0) = 15
    c: Vertical(g0,g2)
    c: DistanceY(g1) = 157
FEATURE [PartDesign::FeaturePython] BaseBend  # WARN: FeaturePython — macro-defined, semantics opaque (R4)
  BendSide = 0
  BendSketch = -> Sketch079
  MidPlane = true
  Reverse = false
  length = 15
  radius = 2
  thickness = 1
FEATURE [Sketcher::SketchObject] Sketch080
  AttachmentOffset = pos=(0,7.5,0) rot=(0,0,1;0rad)
  FullyConstrained = true
  MapMode = 5
  Placement = pos=(0,7.5,0) rot=(0,0,1;0rad)
  Support = -> [XY_Plane026]
  sketch-geometry (1):
    g0: Circle CenterX=0 CenterY=0 CenterZ=0 NormalX=0 NormalY=0 NormalZ=1 AngleXU=0 Radius=1.65
  constraints (3):
    c: PointOnObject(g0,g-2)
    c: Diameter(g0) = 3.3
    c: DistanceY(g0) = 0
FEATURE [PartDesign::Pocket] Pocket039
  BaseFeature = -> BaseBend
  Direction = (0,0,-1)
  Length = 5
  Length2 = 5
  Profile = -> Sketch080
  ReferenceAxis = -> Sketch080 [N_Axis]
  Reversed = true
  Type = 1
FEATURE [Sketcher::SketchObject] Sketch081
  FullyConstrained = true
  MapMode = 5
  Support = -> [XY_Plane026]
  sketch-geometry (3):
    g0: ArcOfCircle CenterX=4.5 CenterY=12 CenterZ=0 NormalX=0 NormalY=0 NormalZ=1 AngleXU=0 Radius=3 StartAngle=1e-16 EndAngle=1.57079
    g1: LineSegment StartX=4.50001 StartY=15 StartZ=0 EndX=7.5 EndY=15 EndZ=0
    g2: LineSegment StartX=7.5 StartY=12 StartZ=0 EndX=7.5 EndY=15 EndZ=0
  constraints (9):
    c: Diameter(g0) = 6
    c: Coincident(g1,g0)
    c: Tangent(g1,g0)
    c: Coincident(g2,g1)
    c: Vertical(g2)
    c: Horizontal(g1)
    c: DistanceX(g1) = 7.5
    c: DistanceY(g1) = 15
    c: Tangent(g2,g0) = -1.5708
FEATURE [PartDesign::Pocket] Pocket040
  BaseFeature = -> Pocket039
  Direction = (0,0,-1)
  Length = 5
  Length2 = 5
  Midplane = true
  Profile = -> Sketch081
  ReferenceAxis = -> Sketch081 [N_Axis]
  Type = 1
FEATURE [PartDesign::Mirrored] Mirrored028
  BaseFeature = -> Pocket040
  MirrorPlane = -> Sketch081 [V_Axis]
  Originals = -> [Pocket040]
FEATURE [PartDesign::Body] Body001003005003012
  Group = -> [Sketch078,Sketch079,BaseBend,Sketch080,Pocket039,Sketch081,Pocket040,Mirrored028]
  Origin = -> Origin025
  Tip = -> Mirrored028
FEATURE [PartDesign::SubShapeBinder] Binder018
  BindCopyOnChange = 0
  BindMode = 0
  ClaimChildren = true
  Context = -> Body001003005003 [Binder018.]
  Fuse = false
  MakeFace = true
  OffsetFill = false
  OffsetIntersection = false
  OffsetJoinType = 0
  OffsetOpenResult = false
  PartialLoad = false
  Relative = false
  Support = -> [Body001003005003012[Pocket039.Sketch080.]]
  _Version = 2
FEATURE [PartDesign::CoordinateSystem] Local_CS025
  AttacherType = Attacher::AttachEngine3D
  AttachmentOffset = pos=(0,0,157) rot=(0,0,1;0rad)
  MapMode = 5
  Placement = pos=(0,0,157) rot=(0,0,1;0rad)
  Support = -> [XY_Plane001]
  expr: .AttachmentOffset.Base.z = <<main>>.basin_height
FEATURE [PartDesign::CoordinateSystem] Local_CS026
  AttacherType = Attacher::AttachEngine3D
  AttachmentOffset = pos=(0,18.4752,0) rot=(0,0,1;0.523599rad)
  MapMode = 5
  Placement = pos=(0,18.4752,0) rot=(0,0,1;0.523599rad)
  Support = -> [XY_Plane015]
  expr: .AttachmentOffset.Base.y = Sketch047.Constraints.major_r_offset
FEATURE [Sketcher::SketchObject] Sketch082
  FullyConstrained = false
  MapMode = 5
  Support = -> [XY_Plane027]
  expr: Constraints[20] = <<main>>.end_face_width / 2 + 2mm
  expr: Constraints[2] = Sketch052.Constraints.r - Sketch052.Constraints.width - 2mm
  expr: Constraints[41] = <<main>>.end_face_width / 2
  sketch-geometry (19):
    g0: ArcOfCircle CenterX=0 CenterY=1.42e-14 CenterZ=0 NormalX=0 NormalY=0 NormalZ=1 AngleXU=0 Radius=197.848 StartAngle=0.657286 EndAngle=1.5708
    g1: LineSegment StartX=1.21e-14 StartY=197.848 StartZ=0 EndX=1.12e-14 EndY=182.848 EndZ=0
    g2: ArcOfCircle CenterX=0 CenterY=1.42e-14 CenterZ=0 NormalX=0 NormalY=0 NormalZ=1 AngleXU=0 Radius=182.848 StartAngle=0.657286 EndAngle=1.5708
    g3: ArcOfCircle CenterX=150.69 CenterY=116.297 CenterZ=0 NormalX=0 NormalY=0 NormalZ=1 AngleXU=0 Radius=7.5 StartAngle=3.79888 EndAngle=6.94047
    g4: LineSegment StartX=0 StartY=1.42e-14 StartZ=0 EndX=165.582 EndY=95.5988 EndZ=0
    g5: GeomPoint X=155.154 Y=110.271 Z=0
    g6: LineSegment StartX=165.582 StartY=95.5988 StartZ=0 EndX=155.154 EndY=110.271 EndZ=0
    g7: ArcOfCircle CenterX=0 CenterY=1.42e-14 CenterZ=0 NormalX=0 NormalY=0 NormalZ=1 AngleXU=0 Radius=190.348 StartAngle=0.617882 EndAngle=1.5708
    g8: ArcOfCircle CenterX=0 CenterY=1.42e-14 CenterZ=0 NormalX=0 NormalY=0 NormalZ=1 AngleXU=0 Radius=190.348 StartAngle=0.641212 EndAngle=1.5708
    g9: ArcOfCircle CenterX=0 CenterY=1.42e-14 CenterZ=0 NormalX=0 NormalY=0 NormalZ=1 AngleXU=0 Radius=197.848 StartAngle=0.619862 EndAngle=0.657286
    g10: LineSegment StartX=155.154 StartY=110.271 StartZ=0 EndX=160.726 EndY=113.488 EndZ=0
    g11: ArcOfCircle CenterX=160.226 CenterY=114.354 CenterZ=0 NormalX=0 NormalY=0 NormalZ=1 AngleXU=0 Radius=1 StartAngle=5.23599 EndAngle=6.90305
    g12: ArcOfCircle CenterX=0 CenterY=1.42e-14 CenterZ=0 NormalX=0 NormalY=0 NormalZ=1 AngleXU=0 Radius=182.848 StartAngle=0.626692 EndAngle=0.657286
    g13: LineSegment StartX=155.154 StartY=110.271 StartZ=0 EndX=149.412 EndY=106.955 EndZ=0
    g14: ArcOfCircle CenterX=148.912 CenterY=107.821 CenterZ=0 NormalX=0 NormalY=0 NormalZ=1 AngleXU=0 Radius=1 StartAngle=3.76829 EndAngle=5.23599
    g15: ArcOfCircle CenterX=0 CenterY=1.42e-14 CenterZ=0 NormalX=0 NormalY=0 NormalZ=1 AngleXU=0 Radius=197.848 StartAngle=0.604557 EndAngle=1.5708
    g16: LineSegment StartX=162.781 StartY=112.457 StartZ=0 EndX=0 EndY=1.42e-14 EndZ=0
    g17: LineSegment StartX=162.781 StartY=112.457 StartZ=0 EndX=0 EndY=112.457 EndZ=0
    g18: LineSegment StartX=0 StartY=1.42e-14 StartZ=0 EndX=162.781 EndY=112.457 EndZ=0
  constraints (52):
    c: Coincident(g0,g-1)
    c: PointOnObject(g0,g-2)
    c: DistanceY(g0) = 197.848
    c: Coincident(g1,g0)
    c: PointOnObject(g1,g-2)
    c: Coincident(g2,g0)
    c: Coincident(g2,g1)
    c: Tangent(g3,g0) = -1.5708
    c: Tangent(g3,g2) = 1.5708
    c: DistanceY(g1,g1) = 15
    c: Coincident(g4,g0)
    c: Angle(g-1,g4) = 0.523599
    c: PointOnObject(g5,g3)
    c: Coincident(g6,g4)
    c: Coincident(g6,g5)
    c: Coincident(g7,g0)
    c: Coincident(g7,g5)
    c: PointOnObject(g7,g1)
    c: PointOnObject(g3,g7)
    c: Tangent(g6,g7)
    c: Distance(g6) = 18
    c: Coincident(g8,g0)
    c: PointOnObject(g8,g-2)
    c: DistanceY(g8,g0) = 7.5
    c: Coincident(g9,g0)
    c: Coincident(g9,g0)
    c: Coincident(g10,g5)
    c: Parallel(g10,g4)
    c: Tangent(g9,g11) = -1.5708
    c: Tangent(g10,g11) = -1.5708
    c: Diameter(g11) = 2
    c: Coincident(g12,g0)
    c: Coincident(g12,g2)
    c: Coincident(g13,g10)
    c: Parallel(g13,g10)
    c: Tangent(g12,g14) = 1.5708
    c: Tangent(g13,g14) = 1.5708
    c: Equal(g14,g11)
    c: Coincident(g15,g0)
    c: PointOnObject(g15,g-2)
    c: Equal(g15,g9)
    c: Distance(g15,g4) = 16
    c: Coincident(g16,g15)
    c: Coincident(g16,g0)
    c: Angle(g16,g-2) = 0.966239
    c: Coincident(g17,g15)
    c: PointOnObject(g17,g-2)
    c: Horizontal(g17)
    c: DistanceX(g17,g17) = 162.781
    c: Coincident(g18,g0)
    c: Coincident(g18,g15)
    c: Angle(g16,g-2) = 0.966239
FEATURE [PartDesign::Pad] Pad021
  Direction = (0,0,1)
  Length = 3
  Length2 = 10
  Profile = -> Sketch082
  ReferenceAxis = -> Sketch082 [N_Axis]
  Type = 0
FEATURE [Sketcher::SketchObject] Sketch083
  FullyConstrained = true
  MapMode = 5
  Support = -> [XY_Plane027]
  expr: Constraints[11] = Sketch082.Constraints[11]
  expr: Constraints[20] = Sketch082.Constraints[20]
  expr: Constraints[23] = Sketch082.Constraints[23]
  expr: Constraints[25] = <<main>>.rivet_d
  expr: Constraints[2] = Sketch082.Constraints[2]
  expr: Constraints[9] = Sketch082.Constraints[9]
  sketch-geometry (11):
    g0: ArcOfCircle CenterX=0 CenterY=0 CenterZ=0 NormalX=0 NormalY=0 NormalZ=1 AngleXU=0 Radius=197.848 StartAngle=0.657286 EndAngle=1.5708
    g1: LineSegment StartX=1.21e-14 StartY=197.848 StartZ=0 EndX=1.12e-14 EndY=182.848 EndZ=0
    g2: ArcOfCircle CenterX=0 CenterY=0 CenterZ=0 NormalX=0 NormalY=0 NormalZ=1 AngleXU=0 Radius=182.848 StartAngle=0.657286 EndAngle=1.5708
    g3: ArcOfCircle CenterX=150.69 CenterY=116.297 CenterZ=0 NormalX=0 NormalY=0 NormalZ=1 AngleXU=0 Radius=7.5 StartAngle=3.79888 EndAngle=6.94047
    g4: LineSegment StartX=0 StartY=0 StartZ=0 EndX=165.582 EndY=95.5988 EndZ=0
    g5: GeomPoint X=155.154 Y=110.271 Z=0
    g6: LineSegment StartX=165.582 StartY=95.5988 StartZ=0 EndX=155.154 EndY=110.271 EndZ=0
    g7: ArcOfCircle CenterX=0 CenterY=0 CenterZ=0 NormalX=0 NormalY=0 NormalZ=1 AngleXU=0 Radius=190.348 StartAngle=0.617882 EndAngle=1.5708
    g8: ArcOfCircle CenterX=0 CenterY=0 CenterZ=0 NormalX=0 NormalY=0 NormalZ=1 AngleXU=0 Radius=190.348 StartAngle=0.670423 EndAngle=1.5708
    g9: Circle CenterX=149.149 CenterY=118.267 CenterZ=0 NormalX=0 NormalY=0 NormalZ=1 AngleXU=0 Radius=1.7
    g10: Circle CenterX=-149.149 CenterY=118.267 CenterZ=0 NormalX=0 NormalY=0 NormalZ=1 AngleXU=0 Radius=1.7
  constraints (29):
    c: Coincident(g0,g-1)
    c: PointOnObject(g0,g-2)
    c: DistanceY(g0) = 197.848
    c: Coincident(g1,g0)
    c: PointOnObject(g1,g-2)
    c: Coincident(g2,g0)
    c: Coincident(g2,g1)
    c: Tangent(g3,g0) = -1.5708
    c: Tangent(g3,g2) = 1.5708
    c: DistanceY(g1,g1) = 15
    c: Coincident(g4,g0)
    c: Angle(g-1,g4) = 0.523599
    c: PointOnObject(g5,g3)
    c: Coincident(g6,g4)
    c: Coincident(g6,g5)
    c: Coincident(g7,g0)
    c: Coincident(g7,g5)
    c: PointOnObject(g7,g1)
    c: PointOnObject(g3,g7)
    c: Tangent(g6,g7)
    c: Distance(g6) = 18
    c: Coincident(g8,g0)
    c: PointOnObject(g8,g-2)
    c: DistanceY(g8,g0) = 7.5
    c: Coincident(g9,g8)
    c: Diameter(g9) = 3.4
    c: Symmetric(g10,g9,g-2)
    c: Equal(g10,g9)
    c: Distance(g5,g9) = 10
FEATURE [PartDesign::Mirrored] Mirrored029
  BaseFeature = -> Pad021
  MirrorPlane = -> Sketch082 [V_Axis]
  Originals = -> [Pad021]
  Refine = true
FEATURE [PartDesign::Pocket] Pocket041
  BaseFeature = -> Mirrored029
  Direction = (0,0,-1)
  Length = 5
  Length2 = 5
  Midplane = true
  Profile = -> Sketch083
  ReferenceAxis = -> Sketch083 [N_Axis]
  Type = 1
FEATURE [Sketcher::SketchObject] Sketch084
  FullyConstrained = true
  MapMode = 5
  Support = -> [XY_Plane027]
  expr: Constraints[11] = Sketch082.Constraints[11]
  expr: Constraints[20] = Sketch082.Constraints[20]
  expr: Constraints[27] = Sketch082.Constraints[30]
  expr: Constraints[2] = Sketch082.Constraints[2]
  expr: Constraints[36] = <<main>>.rivet_d
  expr: Constraints[9] = Sketch082.Constraints[9]
  sketch-geometry (15):
    g0: ArcOfCircle CenterX=0 CenterY=0 CenterZ=0 NormalX=0 NormalY=0 NormalZ=1 AngleXU=0 Radius=197.848 StartAngle=0.657286 EndAngle=1.5708
    g1: LineSegment StartX=1.21e-14 StartY=197.848 StartZ=0 EndX=1.12e-14 EndY=182.848 EndZ=0
    g2: ArcOfCircle CenterX=0 CenterY=0 CenterZ=0 NormalX=0 NormalY=0 NormalZ=1 AngleXU=0 Radius=182.848 StartAngle=0.657286 EndAngle=1.5708
    g3: ArcOfCircle CenterX=150.69 CenterY=116.297 CenterZ=0 NormalX=0 NormalY=0 NormalZ=1 AngleXU=0 Radius=7.5 StartAngle=3.79888 EndAngle=6.94047
    g4: LineSegment StartX=0 StartY=0 StartZ=0 EndX=165.582 EndY=95.5988 EndZ=0
    g5: GeomPoint X=155.154 Y=110.271 Z=0
    g6: LineSegment StartX=165.582 StartY=95.5988 StartZ=0 EndX=155.154 EndY=110.271 EndZ=0
    g7: ArcOfCircle CenterX=0 CenterY=0 CenterZ=0 NormalX=0 NormalY=0 NormalZ=1 AngleXU=0 Radius=190.348 StartAngle=0.617882 EndAngle=1.5708
    g8: ArcOfCircle CenterX=0 CenterY=0 CenterZ=0 NormalX=0 NormalY=0 NormalZ=1 AngleXU=0 Radius=197.848 StartAngle=0.619862 EndAngle=0.657286
    g9: LineSegment StartX=155.154 StartY=110.271 StartZ=0 EndX=160.726 EndY=113.488 EndZ=0
    g10: ArcOfCircle CenterX=160.226 CenterY=114.354 CenterZ=0 NormalX=0 NormalY=0 NormalZ=1 AngleXU=0 Radius=1 StartAngle=5.23599 EndAngle=6.90305
    g11: ArcOfCircle CenterX=0 CenterY=0 CenterZ=0 NormalX=0 NormalY=0 NormalZ=1 AngleXU=0 Radius=182.848 StartAngle=0.626692 EndAngle=0.657286
    g12: LineSegment StartX=155.154 StartY=110.271 StartZ=0 EndX=149.412 EndY=106.955 EndZ=0
    g13: ArcOfCircle CenterX=148.912 CenterY=107.821 CenterZ=0 NormalX=0 NormalY=0 NormalZ=1 AngleXU=0 Radius=1 StartAngle=3.76829 EndAngle=5.23599
    g14: Circle CenterX=1.17e-14 CenterY=190.348 CenterZ=0 NormalX=0 NormalY=0 NormalZ=1 AngleXU=0 Radius=1.7
  constraints (37):
    c: Coincident(g0,g-1)
    c: PointOnObject(g0,g-2)
    c: DistanceY(g0) = 197.848
    c: Coincident(g1,g0)
    c: PointOnObject(g1,g-2)
    c: Coincident(g2,g0)
    c: Coincident(g2,g1)
    c: Tangent(g3,g0) = -1.5708
    c: Tangent(g3,g2) = 1.5708
    c: DistanceY(g1,g1) = 15
    c: Coincident(g4,g0)
    c: Angle(g-1,g4) = 0.523599
    c: PointOnObject(g5,g3)
    c: Coincident(g6,g4)
    c: Coincident(g6,g5)
    c: Coincident(g7,g0)
    c: Coincident(g7,g5)
    c: PointOnObject(g7,g1)
    c: PointOnObject(g3,g7)
    c: Tangent(g6,g7)
    c: Distance(g6) = 18
    c: Coincident(g8,g0)
    c: Coincident(g8,g0)
    c: Coincident(g9,g5)
    c: Parallel(g9,g4)
    c: Tangent(g8,g10) = -1.5708
    c: Tangent(g9,g10) = -1.5708
    c: Diameter(g10) = 2
    c: Coincident(g11,g0)
    c: Coincident(g11,g2)
    c: Coincident(g12,g9)
    c: Parallel(g12,g9)
    c: Tangent(g11,g13) = 1.5708
    c: Tangent(g12,g13) = 1.5708
    c: Equal(g13,g10)
    c: Coincident(g14,g7)
    c: Diameter(g14) = 3.4
FEATURE [PartDesign::Pocket] Pocket042
  BaseFeature = -> Pocket041
  Direction = (0,0,-1)
  Length = 5
  Length2 = 5
  Midplane = true
  Profile = -> Sketch084
  ReferenceAxis = -> Sketch084 [N_Axis]
  Type = 1
FEATURE [PartDesign::Body] Body001003005003013  label="plexiglass_holder_top"
  Group = -> [Sketch082,Pad021,Sketch083,Mirrored029,Pocket041,Sketch084,Pocket042]
  Origin = -> Origin026
  Placement = pos=(0,0,0) rot=(0,0,1;1.0472rad)
  Tip = -> Pocket042
FEATURE [PartDesign::SubShapeBinder] Binder020
  BindCopyOnChange = 0
  BindMode = 0
  ClaimChildren = false
  Context = -> Body001003005003014 [Binder020.]
  Fuse = false
  MakeFace = true
  OffsetFill = false
  OffsetIntersection = false
  OffsetJoinType = 0
  OffsetOpenResult = false
  PartialLoad = false
  Relative = false
  Support = -> [Body001003005003003[Pocket019.Sketch055.]]
  _Version = 2
FEATURE [PartDesign::SubShapeBinder] Binder021
  BindCopyOnChange = 0
  BindMode = 0
  ClaimChildren = false
  Context = -> Body001003005003014 [Binder021.]
  Fuse = false
  MakeFace = true
  OffsetFill = false
  OffsetIntersection = false
  OffsetJoinType = 0
  OffsetOpenResult = false
  PartialLoad = false
  Relative = false
  Support = -> [Body001003005003004[Pocket018.Sketch054.]]
  _Version = 2
FEATURE [PartDesign::CoordinateSystem] Local_CS027
  AttacherType = Attacher::AttachEngine3D
  MapMode = 5
  Support = -> [XY_Plane028]
FEATURE [PartDesign::CoordinateSystem] Local_CS028
  AttacherType = Attacher::AttachEngine3D
  AttachmentOffset = pos=(0,0,0) rot=(0,0,1;0.523599rad)
  MapMode = 5
  Placement = pos=(0,0,0) rot=(0,0,1;0.523599rad)
  Support = -> [XY_Plane028]
FEATURE [PartDesign::Plane] DatumPlane023
  Length = 495.835
  MapMode = 5
  Placement = pos=(0,0,0) rot=(0,0,1;0.523599rad)
  ResizeMode = 0
  Support = -> [Local_CS028]
  Width = 455.324
FEATURE [PartDesign::CoordinateSystem] Local_CS029
  AttacherType = Attacher::AttachEngine3D
  AttachmentOffset = pos=(0,18.4752,0) rot=(0,0,1;0.523599rad)
  MapMode = 5
  Placement = pos=(0,18.4752,0) rot=(0,0,1;0.523599rad)
  Support = -> [XY_Plane028]
  expr: .AttachmentOffset.Base.y = Sketch047.Constraints.major_r_offset
FEATURE [PartDesign::Pad] Pad022
  Direction = (0,0,1)
  Length = 3
  Length2 = 10
  Profile = -> Sketch047
  ReferenceAxis = -> Sketch047 [N_Axis]
  Type = 0
FEATURE [PartDesign::Pocket] Pocket045
  BaseFeature = -> Pad022
  Direction = (0,0,-1)
  Length = 5
  Length2 = 5
  Midplane = true
  Profile = -> Binder021
  Type = 1
FEATURE [PartDesign::SubShapeBinder] Binder023
  BindCopyOnChange = 0
  BindMode = 0
  ClaimChildren = false
  Context = -> Body001003005003 [Binder023.]
  Fuse = false
  MakeFace = true
  OffsetFill = false
  OffsetIntersection = false
  OffsetJoinType = 0
  OffsetOpenResult = false
  PartialLoad = false
  Relative = true
  Support = -> [Body001003005003013[Pocket042.Sketch084.,Pocket041.Sketch083.]]
  _Version = 2
FEATURE [Part::Feature] Part__Feature  label="module002"
  shape: bbox 170 x 148 x 41.12 mm, 715 faces (baked)
FEATURE [PartDesign::FeatureBase] BaseFeature
  BaseFeature = -> Part__Feature
FEATURE [PartDesign::CoordinateSystem] Local_CS009
  AttacherType = Attacher::AttachEngine3D
  MapMode = 45
  Placement = pos=(0,0,0) rot=(0,0.707107,0.707107;3.14159rad)
  Support = -> [BaseFeature]
FEATURE [PartDesign::Body] Body001003  label="module001"
  BaseFeature = -> Part__Feature
  Group = -> [BaseFeature,Local_CS009]
  Origin = -> Origin013
  Tip = -> BaseFeature
FEATURE [Sketcher::SketchObject] Sketch085
  FullyConstrained = true
  MapMode = 5
  Placement = pos=(0,0,0) rot=(0.57735,0.57735,0.57735;2.0944rad)
  Support = -> [YZ_Plane028]
  sketch-geometry (2):
    g0: LineSegment StartX=0 StartY=23 StartZ=0 EndX=0 EndY=0 EndZ=0
    g1: LineSegment StartX=0 StartY=0 StartZ=0 EndX=23 EndY=0 EndZ=0
  constraints (6):
    c: PointOnObject(g0,g-2)
    c: Coincident(g0,g-1)
    c: Coincident(g1,g0)
    c: PointOnObject(g1,g-1)
    c: Equal(g1,g0)
    c: DistanceX(g1,g1) = 23  'length'
FEATURE [PartDesign::FeaturePython] BaseBend002  # WARN: FeaturePython — macro-defined, semantics opaque (R4)
  BendSide = 0
  BendSketch = -> Sketch085
  MidPlane = true
  Reverse = false
  length = 86
  radius = 2
  thickness = 0.5
FEATURE [Sketcher::SketchObject] Sketch086
  AttachmentOffset = pos=(43,23,0) rot=(0,0,1;0rad)
  FullyConstrained = true
  MapMode = 5
  Placement = pos=(43,23,0) rot=(0,0,1;0rad)
  Support = -> [XY_Plane029]
  expr: .AttachmentOffset.Base.x = BaseBend002.length / 2
  expr: .AttachmentOffset.Base.y = Sketch085.Constraints.length
  sketch-geometry (3):
    g0: ArcOfCircle CenterX=-7.5 CenterY=-7.5 CenterZ=0 NormalX=0 NormalY=0 NormalZ=1 AngleXU=0 Radius=7.5 StartAngle=0 EndAngle=1.5708
    g1: LineSegment StartX=0 StartY=-7.5 StartZ=0 EndX=0 EndY=0 EndZ=0
    g2: LineSegment StartX=0 StartY=0 StartZ=0 EndX=-7.50003 EndY=-6.21876e-11 EndZ=0
  constraints (8):
    c: PointOnObject(g0,g-2)
    c: PointOnObject(g0,g-1)
    c: Coincident(g1,g-1)
    c: Coincident(g2,g1)
    c: Coincident(g2,g0)
    c: Tangent(g2,g0)
    c: Tangent(g1,g0) = -1.5708
    c: Diameter(g0) = 15
FEATURE [PartDesign::Pocket] Pocket047
  BaseFeature = -> BaseBend002
  Direction = (0,0,-1)
  Length = 5
  Length2 = 5
  Midplane = true
  Profile = -> Sketch086
  ReferenceAxis = -> Sketch086 [N_Axis]
  Type = 1
FEATURE [PartDesign::Mirrored] Mirrored032
  MirrorPlane = -> YZ_Plane028
FEATURE [PartDesign::PolarPattern] PolarPattern010
  Angle = 90
  Axis = -> X_Axis028
  Occurrences = 2
FEATURE [PartDesign::MultiTransform] MultiTransform011
  BaseFeature = -> Pocket047
  Originals = -> [Pocket047]
  Transformations = -> [Mirrored032,PolarPattern010]
FEATURE [Sketcher::SketchObject] Sketch087
  AttachmentOffset = pos=(0,14.5,0) rot=(0,0,1;0rad)
  FullyConstrained = true
  MapMode = 5
  Placement = pos=(0,14.5,0) rot=(0,0,1;0rad)
  Support = -> [XY_Plane029]
  expr: .AttachmentOffset.Base.y = 14.5mm
  expr: Constraints[3] = <<main>>.rivet_d
  sketch-geometry (2):
    g0: Circle CenterX=36 CenterY=0 CenterZ=0 NormalX=0 NormalY=0 NormalZ=1 AngleXU=0 Radius=1.7
    g1: Circle CenterX=-36 CenterY=0 CenterZ=0 NormalX=0 NormalY=0 NormalZ=1 AngleXU=0 Radius=1.7
  constraints (5):
    c: PointOnObject(g0,g-1)
    c: Symmetric(g1,g0,g-1)
    c: Equal(g0,g1)
    c: Diameter(g0) = 3.4
    c: DistanceX(g1,g0) = 72
FEATURE [PartDesign::Pocket] Pocket048
  BaseFeature = -> MultiTransform011
  Direction = (0,0,-1)
  Length = 5
  Length2 = 5
  Midplane = true
  Profile = -> Sketch087
  ReferenceAxis = -> Sketch087 [N_Axis]
  Type = 1
FEATURE [PartDesign::PolarPattern] PolarPattern011
  Angle = 90
  Axis = -> X_Axis028
  BaseFeature = -> Pocket048
  Occurrences = 2
  Originals = -> [Pocket048]
FEATURE [Sketcher::SketchObject] Sketch088
  AttachmentOffset = pos=(178.2,61.7,0) rot=(0,0,1;0rad)
  FullyConstrained = true
  MapMode = 5
  Placement = pos=(2.59e-14,178.2,61.7) rot=(0.57735,0.57735,0.57735;2.0944rad)
  Support = -> [YZ_Plane001]
  expr: Constraints[9] = <<main>>.rivet_d
  sketch-geometry (4):
    g0: Circle CenterX=0 CenterY=-36 CenterZ=0 NormalX=0 NormalY=0 NormalZ=1 AngleXU=0 Radius=1.7
    g1: Circle CenterX=0 CenterY=36 CenterZ=0 NormalX=0 NormalY=0 NormalZ=1 AngleXU=0 Radius=1.7
    g2: LineSegment StartX=0 StartY=0 StartZ=0 EndX=0 EndY=-36 EndZ=0
    g3: LineSegment StartX=0 StartY=0 StartZ=0 EndX=0 EndY=36 EndZ=0
  constraints (10):
    c: PointOnObject(g0,g-2)
    c: PointOnObject(g1,g-2)
    c: Equal(g0,g1)
    c: Coincident(g2,g-1)
    c: Coincident(g2,g0)
    c: Coincident(g3,g2)
    c: Coincident(g3,g1)
    c: Equal(g2,g3)
    c: DistanceY(g0,g1) = 72
    c: Diameter(g1) = 3.4
FEATURE [PartDesign::PolarPattern] PolarPattern012
  Angle = 120
  Axis = -> Z_Axis001
  Occurrences = 2
FEATURE [PartDesign::Mirrored] Mirrored033
  MirrorPlane = -> DatumPlane021
FEATURE [App::Link] Body001003005003004001
  AssemblyType = Part::Link
  AttachedBy = #Local_CS019
  AttachedTo = Body001001#Local_CS025
  AttachmentOffset = pos=(0,0,-3) rot=(0,0,1;3.14159rad)
  LinkPlacement = pos=(0,0,154) rot=(0,0,1;3.14159rad)
  LinkedObject = -> Body001003005003004
  Placement = pos=(0,0,154) rot=(0,0,1;3.14159rad)
  SolverId = Asm4EE
  expr: Placement = Body001001.Placement * Local_CS025.Placement * AttachmentOffset * Local_CS019.Placement ^ -1
FEATURE [PartDesign::CoordinateSystem] Local_CS030
  AttacherType = Attacher::AttachEngine3D
  AttachmentOffset = pos=(0,0,-16) rot=(0,1,0;3.14159rad)
  MapMode = 2
  Placement = pos=(-16,178.2,61.7) rot=(-0.57735,0.57735,0.57735;4.18879rad)
  Support = -> [Sketch088]
  expr: .AttachmentOffset.Base.z = -<<main>>.end_face_width / 2
FEATURE [PartDesign::CoordinateSystem] Local_CS031
  AttacherType = Attacher::AttachEngine3D
  MapMode = 2
  Placement = pos=(0,14.5,0) rot=(0,0,1;0rad)
  Support = -> [Sketch087]
FEATURE [PartDesign::Body] Body001003005003015  label="corner_72x15_material_0.30ansi"
  Group = -> [Sketch085,BaseBend002,Sketch086,Pocket047,MultiTransform011,Mirrored032,PolarPattern010,Sketch087,Pocket048,PolarPattern011,Local_CS031]
  Origin = -> Origin028
  Tip = -> PolarPattern011
FEATURE [App::Link] Body001003005003015001
  AssemblyType = Part::Link
  AttachedBy = #Local_CS031
  AttachedTo = Body001001#Local_CS030
  AttachmentOffset = pos=(0,0,0.5) rot=(0,0,1;4.71239rad)
  LinkPlacement = pos=(-16.5,192.7,61.7) rot=(0.707107,0,-0.707107;3.14159rad)
  LinkedObject = -> Body001003005003015
  Placement = pos=(-16.5,192.7,61.7) rot=(0.707107,0,-0.707107;3.14159rad)
  SolverId = Asm4EE
  expr: Placement = Body001001.Placement * Local_CS030.Placement * AttachmentOffset * Local_CS031.Placement ^ -1
FEATURE [Part::FeaturePython] Circular_Body001003005002  # Draft array (typed FeaturePython)
  ArrayType = Circular Array
  Axis = -> Z_Axis012
  AxisXYZ = 0
  Count = 2
  ElementPlacement = pos=(0,0,0) rot=(0,0,1;4.18879rad)
  Index = 1
  IntervalAngle = 240
  PlacementList = 2 placements: [(1.26218e-29,-1.26218e-29,157),(-1.37995e-13,6.82312e-14,157)]
  ScaleList = (2) [(1,1,1),(1,1,1)]
  ShowElement = false
  SourceObject = -> Body001003005002
  expr: .ElementPlacement.Rotation.Angle = IntervalAngle * Index
  expr: IntervalAngle = 240
FEATURE [PartDesign::CoordinateSystem] LCS_0
  AttacherType = Attacher::AttachEngine3D
  MapMode = 2
  Support = -> [X_Axis029]
FEATURE [Sketcher::SketchObject] Sketch089
  FullyConstrained = true
  MapMode = 5
  Placement = pos=(0,0,0) rot=(1,0,0;1.5708rad)
  Support = -> [XZ_Plane029]
  sketch-geometry (5):
    g0: LineSegment StartX=-41.5 StartY=-36.5 StartZ=0 EndX=-41.5 EndY=0 EndZ=0
    g1: LineSegment StartX=-41.5 StartY=0 StartZ=0 EndX=41.5 EndY=0 EndZ=0
    g2: LineSegment StartX=41.5 StartY=0 StartZ=0 EndX=41.5 EndY=-36.5 EndZ=0
    g3: LineSegment StartX=41.5 StartY=-36.5 StartZ=0 EndX=-41.5 EndY=-36.5 EndZ=0
    g4: GeomPoint X=0 Y=-18.25 Z=0
  constraints (13):
    c: Coincident(g0,g1)
    c: Coincident(g1,g2)
    c: Coincident(g2,g3)
    c: Coincident(g3,g0)
    c: Horizontal(g1)
    c: Horizontal(g3)
    c: Vertical(g0)
    c: Vertical(g2)
    c: Symmetric(g1,g0,g4)
    c: PointOnObject(g4,g-2)
    c: PointOnObject(g1,g-1)
    c: DistanceX(g1,g1) = 83  'width'
    c: DistanceY(g2,g2) = 36.5
FEATURE [PartDesign::FeaturePython] BaseBend003  # WARN: FeaturePython — macro-defined, semantics opaque (R4)
  BendSide = 0
  BendSketch = -> Sketch089
  MidPlane = true
  Reverse = false
  length = 108.4
  radius = 0.01
  thickness = 0.3
  expr: radius = <<main>>.bend_r
FEATURE [Sketcher::SketchObject] Sketch090
  FullyConstrained = true
  MapMode = 5
  Support = -> [XY_Plane030]
  expr: Constraints[6] = <<main>>.end_face_width / 2
  sketch-geometry (6):
    g0: LineSegment StartX=0 StartY=-100 StartZ=0 EndX=14.5 EndY=-100 EndZ=0
    g1: LineSegment StartX=16 StartY=-98.5 StartZ=0 EndX=16 EndY=100 EndZ=0
    g2: LineSegment StartX=16 StartY=100 StartZ=0 EndX=0 EndY=109.238 EndZ=0
    g3: LineSegment StartX=0 StartY=109.238 StartZ=0 EndX=0 EndY=-100 EndZ=0
    g4: ArcOfCircle CenterX=14.5 CenterY=-98.5 CenterZ=0 NormalX=0 NormalY=0 NormalZ=1 AngleXU=0 Radius=1.5 StartAngle=4.71239 EndAngle=6.28319
    g5: GeomPoint X=16 Y=-100 Z=0
  constraints (15):
    c: Coincident(g1,g2)
    c: Coincident(g2,g3)
    c: Coincident(g3,g0)
    c: Horizontal(g0)
    c: Vertical(g3)
    c: PointOnObject(g0,g-2)
    c: DistanceX(g5) = 16
    c: Angle(g-2,g2) = 1.0472
    c: Symmetric(g1,g5,g-1)
    c: DistanceY(g5,g1) = 200
    c: PointOnObject(g5,g0)
    c: PointOnObject(g5,g1)
    c: Tangent(g0,g4) = -1.5708
    c: Tangent(g1,g4) = -1.5708
    c: Diameter(g4) = 3
FEATURE [PartDesign::Pad] Pad023
  BaseFeature = -> BaseBend003
  Direction = (0,0,1)
  Length = 0.3
  Length2 = 10
  Profile = -> Sketch090
  ReferenceAxis = -> Sketch090 [N_Axis]
  Reversed = true
  Type = 0
FEATURE [PartDesign::Mirrored] Mirrored034
  BaseFeature = -> Pad023
  MirrorPlane = -> Sketch090 [V_Axis]
  Originals = -> [Pad023]
  Refine = true
FEATURE [Sketcher::SketchObject] Sketch091
  FullyConstrained = true
  MapMode = 5
  Placement = pos=(0,0,0) rot=(0.57735,0.57735,0.57735;2.0944rad)
  Support = -> [YZ_Plane029]
  sketch-geometry (8):
    g0: LineSegment StartX=0 StartY=-36.5 StartZ=0 EndX=0 EndY=-18.63 EndZ=0
    g1: LineSegment StartX=0 StartY=-18.63 StartZ=0 EndX=17.4865 EndY=-18.63 EndZ=0
    g2: LineSegment StartX=54.2 StartY=-36.5 StartZ=0 EndX=54.2 EndY=-18.63 EndZ=0
    g3: ArcOfCircle CenterX=36.33 CenterY=-18.63 CenterZ=0 NormalX=0 NormalY=0 NormalZ=1 AngleXU=0 Radius=17.87 StartAngle=4.71239 EndAngle=6.28319
    g4: LineSegment StartX=54.2 StartY=-36.5 StartZ=0 EndX=36.33 EndY=-36.5 EndZ=0
    g5: ArcOfCircle CenterX=36.33 CenterY=-18.63 CenterZ=0 NormalX=0 NormalY=0 NormalZ=1 AngleXU=0 Radius=17.87 StartAngle=3.19461 EndAngle=4.71239
    g6: ArcOfCircle CenterX=17.4865 CenterY=-19.63 CenterZ=0 NormalX=0 NormalY=0 NormalZ=1 AngleXU=0 Radius=1 StartAngle=0.053019 EndAngle=1.5708
    g7: LineSegment StartX=0 StartY=-36.5 StartZ=0 EndX=36.33 EndY=-36.5 EndZ=0
  constraints (22):
    c: PointOnObject(g0,g-2)
    c: PointOnObject(g0,g-2)
    c: Coincident(g0,g1)
    c: Horizontal(g1)
    c: Vertical(g2)
    c: Coincident(g4,g2)
    c: Horizontal(g4)
    c: Tangent(g3,g2) = -1.5708
    c: Coincident(g5,g3)
    c: Coincident(g5,g3)
    c: Tangent(g1,g6) = 1.5708
    c: Tangent(g6,g5) = 1.5708
    c: Coincident(g7,g0)
    c: Coincident(g7,g3)
    c: Horizontal(g7)
    c: Coincident(g3,g4)
    c: Tangent(g5,g7)
    c: DistanceY(g0) = -36.5
    c: DistanceX(g2) = 54.2
    c: Diameter(g6) = 2
    c: Diameter(g5) = 35.74
    c: Horizontal(g0,g2)
FEATURE [PartDesign::Pocket] Pocket050
  BaseFeature = -> Mirrored034
  Direction = (-1,2e-16,-3e-16)
  Length = 5
  Length2 = 5
  Midplane = true
  Profile = -> Sketch091
  ReferenceAxis = -> Sketch091 [N_Axis]
  Refine = true
  Type = 1
FEATURE [PartDesign::Mirrored] Mirrored035
  BaseFeature = -> Pocket050
  MirrorPlane = -> Sketch091 [V_Axis]
  Originals = -> [Pocket050]
FEATURE [Sketcher::SketchObject] Sketch092
  FullyConstrained = true
  MapMode = 5
  Placement = pos=(0,0,0) rot=(0.57735,0.57735,0.57735;2.0944rad)
  Support = -> [YZ_Plane029]
  sketch-geometry (1):
    g0: Circle CenterX=0 CenterY=-9.63 CenterZ=0 NormalX=0 NormalY=0 NormalZ=1 AngleXU=0 Radius=1.65
  constraints (3):
    c: PointOnObject(g0,g-2)
    c: Diameter(g0) = 3.3
    c: DistanceY(g0) = -9.63
FEATURE [PartDesign::Pocket] Pocket051
  BaseFeature = -> Mirrored035
  Direction = (-1,2e-16,-3e-16)
  Length = 5
  Length2 = 5
  Midplane = true
  Profile = -> Sketch092
  ReferenceAxis = -> Sketch092 [N_Axis]
  Type = 1
FEATURE [PartDesign::Body] Body_2  label="top_material_0.50ansi"
  Group = -> [LCS_0,Sketch089,BaseBend003,Sketch090,Pad023,Mirrored034,Sketch091,Pocket050,Mirrored035,Sketch092,Pocket051]
  Origin = -> Origin029
  Placement = pos=(0,0,3) rot=(0,0,1;0rad)
  Tip = -> Pocket051
FEATURE [PartDesign::CoordinateSystem] LCS_0001
  AttacherType = Attacher::AttachEngine3D
  MapMode = 2
  Support = -> [X_Axis030]
FEATURE [Sketcher::SketchObject] Sketch093  label="Stainless_top_Sketch"
  FullyConstrained = true
  MapMode = 5
  Placement = pos=(0,0,0) rot=(1,0,0;1.5708rad)
  Support = -> [XZ_Plane030]
  sketch-geometry (5):
    g0: LineSegment StartX=-38 StartY=-33.5 StartZ=0 EndX=-38 EndY=0 EndZ=0
    g1: LineSegment StartX=-38 StartY=0 StartZ=0 EndX=38 EndY=0 EndZ=0
    g2: LineSegment StartX=38 StartY=0 StartZ=0 EndX=38 EndY=-33.5 EndZ=0
    g3: LineSegment StartX=38 StartY=-33.5 StartZ=0 EndX=-38 EndY=-33.5 EndZ=0
    g4: GeomPoint X=0 Y=-16.75 Z=0
  constraints (13):
    c: Coincident(g0,g1)
    c: Coincident(g1,g2)
    c: Coincident(g2,g3)
    c: Coincident(g3,g0)
    c: Horizontal(g1)
    c: Horizontal(g3)
    c: Vertical(g0)
    c: Vertical(g2)
    c: Symmetric(g1,g0,g4)
    c: PointOnObject(g4,g-2)
    c: PointOnObject(g1,g-1)
    c: DistanceX(g1,g1) = 76  'width'
    c: DistanceY(g2,g1) = 33.5  'height'
FEATURE [PartDesign::FeaturePython] BaseBend004  # WARN: FeaturePython — macro-defined, semantics opaque (R4)
  BendSide = 0
  BendSketch = -> Sketch093
  MidPlane = true
  Reverse = false
  length = 108.4
  radius = 2
  thickness = 0.5
  expr: length = BaseBend003.length
FEATURE [PartDesign::SubShapeBinder] Binder024
  BindCopyOnChange = 0
  BindMode = 0
  ClaimChildren = false
  Context = -> Body_3 [Binder024.]
  Fuse = false
  MakeFace = true
  OffsetFill = true
  OffsetIntersection = false
  OffsetJoinType = 0
  OffsetOpenResult = true
  PartialLoad = false
  Relative = true
  Support = -> [Body_2[Pocket050.Sketch091.]]
  _Version = 2
FEATURE [PartDesign::Pocket] Pocket052
  BaseFeature = -> BaseBend004
  Direction = (-1,2e-16,-2e-16)
  Length = 5
  Length2 = 5
  Midplane = true
  Profile = -> Binder024 [Face1]
  Type = 1
FEATURE [PartDesign::Mirrored] Mirrored036
  BaseFeature = -> Pocket052
  MirrorPlane = -> XZ_Plane030
  Originals = -> [Pocket052]
FEATURE [PartDesign::SubShapeBinder] Binder025
  BindCopyOnChange = 0
  BindMode = 0
  ClaimChildren = false
  Context = -> Body_3 [Binder025.]
  Fuse = false
  MakeFace = true
  OffsetFill = false
  OffsetIntersection = false
  OffsetJoinType = 0
  OffsetOpenResult = false
  PartialLoad = false
  Relative = true
  Support = -> [Body_2[Pocket051.Sketch092.]]
  _Version = 2
FEATURE [PartDesign::Pocket] Pocket053
  BaseFeature = -> Mirrored036
  Direction = (-1,2e-16,-2e-16)
  Length = 5
  Length2 = 5
  Midplane = true
  Profile = -> Binder025
  Type = 1
FEATURE [PartDesign::CoordinateSystem] LCS_0002
  AttacherType = Attacher::AttachEngine3D
  MapMode = 2
  Support = -> [X_Axis032]
FEATURE [Sketcher::SketchObject] Sketch094
  FullyConstrained = true
  MapMode = 5
  Support = -> [XY_Plane033]
  expr: Constraints[5] = <<main>>.rivet_d
  expr: Constraints[6] = <<module>>.module_width + 24mm
  sketch-geometry (3):
    g0: Circle CenterX=-86 CenterY=2e-16 CenterZ=0 NormalX=0 NormalY=0 NormalZ=1 AngleXU=0 Radius=1.7
    g1: Circle CenterX=86 CenterY=0 CenterZ=0 NormalX=0 NormalY=0 NormalZ=1 AngleXU=0 Radius=1.7
    g2: Circle CenterX=86 CenterY=-45 CenterZ=0 NormalX=0 NormalY=0 NormalZ=1 AngleXU=0 Radius=1.7
  constraints (8):
    c: PointOnObject(g1,g-1)
    c: Vertical(g2,g1)
    c: Symmetric(g0,g1,g-2)
    c: Equal(g0,g1)
    c: Equal(g1,g2)
    c: Diameter(g1) = 3.4
    c: DistanceX(g0,g1) = 172
    c: DistanceY(g2,g1) = 45
FEATURE [Sketcher::SketchObject] Sketch095
  FullyConstrained = true
  MapMode = 5
  Support = -> [XY_Plane033]
  expr: Constraints[31] = 10
  expr: Constraints[43] = <<module>>.module_width + 24mm
  expr: Constraints[44] = <<module>>.module_width
  sketch-geometry (31):
    g0: LineSegment StartX=96 StartY=-87.0059 StartZ=0 EndX=96 EndY=5 EndZ=0
    g1: LineSegment StartX=91 StartY=10 StartZ=0 EndX=-91 EndY=10 EndZ=0
    g2: LineSegment StartX=-96 StartY=5 StartZ=0 EndX=-96 EndY=-5 EndZ=0
    g3: LineSegment StartX=-91 StartY=-10 StartZ=0 EndX=-77 EndY=-10 EndZ=0
    g4: LineSegment StartX=-72 StartY=-15 StartZ=0 EndX=-72 EndY=-59.848 EndZ=0
    g5: LineSegment StartX=-48.163 StartY=-99.1271 StartZ=0 EndX=88.7532 EndY=-94.5016 EndZ=0
    g6: ArcOfCircle CenterX=91 CenterY=5 CenterZ=0 NormalX=0 NormalY=0 NormalZ=1 AngleXU=0 Radius=5 StartAngle=0 EndAngle=1.5708
    g7: GeomPoint X=96 Y=10 Z=0
    g8: ArcOfCircle CenterX=-91 CenterY=-5 CenterZ=0 NormalX=0 NormalY=0 NormalZ=1 AngleXU=0 Radius=5 StartAngle=3.14159 EndAngle=4.71239
    g9: GeomPoint X=-96 Y=-10 Z=0
    g10: ArcOfCircle CenterX=-91 CenterY=5 CenterZ=0 NormalX=0 NormalY=0 NormalZ=1 AngleXU=0 Radius=5 StartAngle=1.5708 EndAngle=3.14159
    g11: GeomPoint X=-96 Y=10 Z=0
    g12: ArcOfCircle CenterX=-77 CenterY=-15 CenterZ=0 NormalX=0 NormalY=0 NormalZ=1 AngleXU=0 Radius=5 StartAngle=0 EndAngle=1.5708
    g13: GeomPoint X=-72 Y=-10 Z=0
    g14: GeomPoint X=-72 Y=-99.9324 Z=0
    g15: ArcOfCircle CenterX=88.5 CenterY=-87.0059 CenterZ=0 NormalX=0 NormalY=0 NormalZ=1 AngleXU=0 Radius=7.5 StartAngle=4.74616 EndAngle=6.28319
    g16: GeomPoint X=96 Y=-94.2568 Z=0
    g17: LineSegment StartX=-72 StartY=-59.9324 StartZ=0 EndX=96 EndY=-54.2568 EndZ=0
    g18: LineSegment StartX=-91 StartY=5 StartZ=0 EndX=-91 EndY=0 EndZ=0
    g19: LineSegment StartX=-91 StartY=0 StartZ=0 EndX=-91 EndY=-5 EndZ=0
    g20: GeomPoint X=86 Y=0 Z=0
    g21: GeomPoint X=-86 Y=0 Z=0
    g22: GeomPoint X=74 Y=0 Z=0
    g23: GeomPoint X=-74 Y=0 Z=0
    g24: LineSegment StartX=-91 StartY=-5 StartZ=0 EndX=-86 EndY=0 EndZ=0
    g25: GeomPoint X=-74 Y=-60 Z=0
    g26: GeomPoint X=74 Y=-55 Z=0
    g27: LineSegment StartX=-71.9971 StartY=-60.0168 StartZ=0 EndX=-71.4099 EndY=-77.3997 EndZ=0
    g28: ArcOfCircle CenterX=-48.9227 CenterY=-76.64 CenterZ=0 NormalX=0 NormalY=0 NormalZ=1 AngleXU=0 Radius=22.5 StartAngle=3.17536 EndAngle=4.74616
    g29: ArcOfCircle CenterX=-67 CenterY=-59.848 CenterZ=0 NormalX=0 NormalY=0 NormalZ=1 AngleXU=0 Radius=5 StartAngle=3.14159 EndAngle=3.17536
    g30: GeomPoint X=-72 Y=-59.9324 Z=0
  constraints (70):
    c: Vertical(g0)
    c: Horizontal(g1)
    c: Vertical(g2)
    c: Horizontal(g3)
    c: Vertical(g4)
    c: PointOnObject(g7,g1)
    c: PointOnObject(g7,g0)
    c: Tangent(g1,g6) = -1.5708
    c: Tangent(g0,g6) = -1.5708
    c: PointOnObject(g9,g3)
    c: PointOnObject(g9,g2)
    c: Tangent(g3,g8) = -1.5708
    c: Tangent(g2,g8) = -1.5708
    c: PointOnObject(g11,g2)
    c: PointOnObject(g11,g1)
    c: Tangent(g2,g10) = -1.5708
    c: Tangent(g1,g10) = -1.5708
    c: PointOnObject(g13,g3)
    c: PointOnObject(g13,g4)
    c: Tangent(g3,g12) = 1.5708
    c: Tangent(g4,g12) = 1.5708
    c: PointOnObject(g14,g4)
    c: PointOnObject(g14,g5)
    c: PointOnObject(g16,g5)
    c: PointOnObject(g16,g0)
    c: Tangent(g5,g15) = -1.5708
    c: Tangent(g0,g15) = -1.5708
    c: Parallel(g17,g5)
    c: Equal(g12,g8)
    c: Equal(g8,g10)
    c: Equal(g10,g6)
    c: Diameter(g10) = 10
    c: Diameter(g15) = 15
    c: Coincident(g18,g10)
    c: PointOnObject(g18,g-1)
    c: Vertical(g18)
    c: Coincident(g18,g19)
    c: Coincident(g19,g8)
    c: Equal(g19,g18)
    c: PointOnObject(g20,g-1)
    c: PointOnObject(g22,g-1)
    c: Symmetric(g21,g20,g-2)
    c: Symmetric(g23,g22,g-2)
    c: DistanceX(g21,g20) = 172
    c: DistanceX(g23,g22) = 148
    c: DistanceY(g9,g11) = 20
    c: Coincident(g24,g8)
    c: Coincident(g24,g21)
    c: Angle(g24,g-1) = 2.35619
    c: DistanceY(g16,g17) = 40
    c: DistanceX(g22,g0) = 22
    c: Vertical(g22,g26)
    c: Vertical(g25,g23)
    c: DistanceY(g25,g26) = 5
    c: PointOnObject(g26,g17)
    c: PointOnObject(g25,g17)
    c: DistanceY(g26,g22) = 55
    c: Coincident(g30,g17)
    c: Perpendicular(g27,g17)
    c: Tangent(g28,g5) = -1.5708
    c: Tangent(g28,g27) = -1.5708
    c: PointOnObject(g17,g0)
    c: Diameter(g28) = 45
    c: DistanceX(g23,g13) = 2
    c: PointOnObject(g30,g27)
    c: PointOnObject(g30,g4)
    c: Tangent(g27,g29) = -1.5708
    c: Tangent(g4,g29) = -1.5708
    c: Diameter(g29) = 10
    c: Angle(g-1,g17) = 0.0337709
FEATURE [PartDesign::Pad] Pad025
  Direction = (0,0,1)
  Length = 0.5
  Length2 = 10
  Profile = -> Sketch095
  ReferenceAxis = -> Sketch095 [N_Axis]
  Type = 0
FEATURE [Sketcher::SketchObject] Sketch096
  AttachmentOffset = pos=(0,0,0.5) rot=(0,0,1;0rad)
  FullyConstrained = false
  MapMode = 5
  Placement = pos=(0,0,0.5) rot=(0,0,1;0rad)
  Support = -> [XY_Plane033]
  expr: .AttachmentOffset.Base.z = Pad025.Length
  expr: Constraints[4] = <<module>>.module_width
  sketch-geometry (5):
    g0: GeomPoint X=-74 Y=0 Z=0
    g1: GeomPoint X=74 Y=0 Z=0
    g2: GeomPoint X=74 Y=-58 Z=0
    g3: GeomPoint X=-74 Y=-63 Z=0
    g4: LineSegment StartX=-105.813 StartY=-64.0748 StartZ=0 EndX=129.863 EndY=-56.1127 EndZ=0
  constraints (9):
    c: PointOnObject(g1,g-1)
    c: DistanceY(g3,g2) = 5
    c: DistanceY(g2,g1) = 58
    c: Symmetric(g0,g1,g-1)
    c: DistanceX(g0,g1) = 148
    c: Vertical(g2,g1)
    c: Vertical(g3,g0)
    c: PointOnObject(g2,g4)
    c: PointOnObject(g3,g4)
FEATURE [Sketcher::SketchObject] Sketch097
  FullyConstrained = false
  MapMode = 5
  Support = -> [XY_Plane033]
  sketch-geometry (1):
    g0: Circle CenterX=-66 CenterY=-66.2266 CenterZ=0 NormalX=0 NormalY=0 NormalZ=1 AngleXU=0 Radius=2.5
  constraints (2):
    c: Diameter(g0) = 5
    c: DistanceX(g0) = -66
FEATURE [PartDesign::Pocket] Pocket054
  BaseFeature = -> Pad025
  Direction = (0,0,-1)
  Length = 5
  Length2 = 5
  Midplane = true
  Profile = -> Sketch097
  ReferenceAxis = -> Sketch097 [N_Axis]
  Type = 1
FEATURE [PartDesign::Pocket] Pocket055
  BaseFeature = -> Pocket054
  Direction = (0,0,-1)
  Length = 5
  Length2 = 5
  Midplane = true
  Profile = -> Sketch094
  ReferenceAxis = -> Sketch094 [N_Axis]
  Type = 1
FEATURE [PartDesign::FeaturePython] Fold009  # WARN: FeaturePython — macro-defined, semantics opaque (R4)
  BaseFeature = -> Pocket055
  BendLine = -> Sketch096
  Position = 0
  angle = 105
  baseObject = -> Pocket055 [Face5]
  invert = false
  invertbend = false
  kfactor = 0.5
  radius = 2
  unfold = false
FEATURE [PartDesign::Body] Body_4  label="vodostok_s_material_0.30ansi"
  Group = -> [LCS_0002,Sketch094,Sketch095,Pad025,Sketch096,Sketch097,Pocket054,Pocket055,Fold009]
  Origin = -> Origin032
  Tip = -> Fold009
FEATURE [PartDesign::CoordinateSystem] Local_CS032
  AttacherType = Attacher::AttachEngine3D
  AttachmentOffset = pos=(0,0,72) rot=(0.58,0.58,0.58;2.0944rad)
  MapMode = 5
  Placement = pos=(0,109.238,229) rot=(0.57735,0.57735,0.57735;2.0944rad)
  Support = -> [Local_CS023]
FEATURE [PartDesign::CoordinateSystem] LCS_0004
  AttacherType = Attacher::AttachEngine3D
  MapMode = 2
  Support = -> [X_Axis034]
FEATURE [Part::FeaturePython] Linear_Body001003001  # Draft array (typed FeaturePython)
  ArrayType = Linear Array
  Axis = -> Z_Axis012
  AxisXYZ = 0
  Count = 6
  ElementPlacement = pos=(0,0,-80) rot=(0,0,1;0rad)
  Index = 1
  LinearStep = -80
  Placement = pos=(14.5,0,0) rot=(0,0,1;0rad)
  PlacementList = 6 placements: arithmetic series from (1e-17,109.238,738) step (2.51215e-14,-4.26326e-14,-80) to (1.25617e-13,109.238,338)
  ScaleList = (6) [(1,1,1),(1,1,1),(1,1,1),(1,1,1),(1,1,1),(1,1,1)]
  ShowElement = false
  SourceObject = -> Body001003001
  expr: .ElementPlacement.Base.z = LinearStep * Index
  expr: Count = <<main>>.number_of_modules
FEATURE [PartDesign::SubShapeBinder] Binder027
  BindCopyOnChange = 0
  BindMode = 0
  ClaimChildren = false
  Context = -> Model [Body001001.Binder027.Edge3]
  Fuse = false
  MakeFace = true
  OffsetFill = false
  OffsetIntersection = false
  OffsetJoinType = 0
  OffsetOpenResult = false
  PartialLoad = false
  Placement = pos=(0,109.238,229) rot=(0.57735,0.57735,0.57735;2.0944rad)
  Relative = true
  Support = -> [Body_4[Pocket055.Sketch094.]]
  _Version = 2
  expr: Placement = Local_CS032.Placement
FEATURE [App::Link] Body_007
  AssemblyType = Part::Link
  AttachedBy = #LCS_0002
  AttachedTo = Body001001#Local_CS032
  AttachmentOffset = pos=(0,0,15.5) rot=(0,0,1;0rad)
  LinkPlacement = pos=(15.5,109.238,229) rot=(0.57735,0.57735,0.57735;2.0944rad)
  LinkedObject = -> Body_4
  Placement = pos=(15.5,109.238,229) rot=(0.57735,0.57735,0.57735;2.0944rad)
  SolverId = Asm4EE
  expr: Placement = Body001001.Placement * Local_CS032.Placement * AttachmentOffset * LCS_0002.Placement ^ -1
FEATURE [PartDesign::SubShapeBinder] Binder031
  BindCopyOnChange = 0
  BindMode = 0
  ClaimChildren = false
  Context = -> Body_3 [Binder031.]
  Fuse = false
  MakeFace = true
  OffsetFill = false
  OffsetIntersection = false
  OffsetJoinType = 0
  OffsetOpenResult = false
  PartialLoad = false
  Relative = true
  _Version = 2
FEATURE [PartDesign::Pocket] Pocket060
  BaseFeature = -> Pocket053
  Direction = (0,0,-1)
  Length = 5
  Length2 = 5
  Midplane = true
  Profile = -> Binder031
  Type = 1
FEATURE [PartDesign::Body] Body_3  label="top_small_material_0.50ansi"
  Group = -> [LCS_0001,Sketch093,BaseBend004,Binder024,Pocket052,Mirrored036,Binder025,Pocket053,Pocket060,Binder031]
  Origin = -> Origin030
  Tip = -> Pocket060
FEATURE [PartDesign::CoordinateSystem] LCS_0005
  AttacherType = Attacher::AttachEngine3D
  MapMode = 2
  Support = -> [X_Axis035]
FEATURE [Sketcher::SketchObject] Sketch104
  FullyConstrained = false
  MapMode = 5
  Placement = pos=(0,0,0) rot=(0.57735,0.57735,0.57735;2.0944rad)
  Support = -> [YZ_Plane035]
  expr: Constraints[6] = 2mm + 0.5mm + 3.4mm + 2mm + 3mm
  sketch-geometry (3):
    g0: LineSegment StartX=10.9 StartY=0 StartZ=0 EndX=0 EndY=0 EndZ=0
    g1: LineSegment StartX=0 StartY=0 StartZ=0 EndX=0 EndY=17.2 EndZ=0
    g2: GeomPoint X=12.5 Y=0 Z=0
  constraints (7):
    c: PointOnObject(g0,g-1)
    c: Coincident(g0,g-1)
    c: Coincident(g0,g1)
    c: PointOnObject(g1,g-2)
    c: PointOnObject(g2,g-1)
    c: DistanceY(g1) = 17.2
    c: DistanceX(g0,g0) = 10.9
FEATURE [PartDesign::FeaturePython] BaseBend006  # WARN: FeaturePython — macro-defined, semantics opaque (R4)
  BendSide = 0
  BendSketch = -> Sketch104
  MidPlane = true
  Reverse = false
  length = 9.4
  radius = 2
  thickness = 0.5
  expr: length = <<main>>.rivet_d + 6mm
FEATURE [Sketcher::SketchObject] Sketch105
  AttachmentOffset = pos=(0,5.9,0) rot=(0,0,1;0rad)
  FullyConstrained = true
  MapMode = 5
  Placement = pos=(0,5.9,0) rot=(0,0,1;0rad)
  Support = -> [XY_Plane036]
  expr: .AttachmentOffset.Base.y = 2mm + 0.5mm + 2mm + 1.4mm
  expr: Constraints[1] = <<main>>.rivet_d
  sketch-geometry (1):
    g0: Circle CenterX=0 CenterY=0 CenterZ=0 NormalX=0 NormalY=0 NormalZ=1 AngleXU=0 Radius=1.7
  constraints (2):
    c: Coincident(g0,g-1)
    c: Diameter(g0) = 3.4
FEATURE [PartDesign::Plane] DatumPlane024
  AttachmentOffset = pos=(0,0,0) rot=(1,0,0;0.785398rad)
  Length = 61.8921
  MapMode = 5
  Placement = pos=(0,0,0) rot=(1,0,0;0.785398rad)
  ResizeMode = 0
  Support = -> [XY_Plane036]
  Width = 82.6027
FEATURE [PartDesign::Fillet] Fillet002
  Base = -> BaseBend006 [Edge25,Edge8]
  BaseFeature = -> BaseBend006
  Radius = 2
  SupportTransform = false
  UseAllEdges = false
FEATURE [PartDesign::Mirrored] Mirrored038
  BaseFeature = -> Fillet002
  MirrorPlane = -> YZ_Plane035
  Originals = -> [Fillet002]
FEATURE [PartDesign::Pocket] Pocket061
  BaseFeature = -> Mirrored038
  Direction = (0,0,-1)
  Length = 5
  Length2 = 5
  Midplane = true
  Profile = -> Sketch105
  ReferenceAxis = -> Sketch105 [N_Axis]
  Type = 1
FEATURE [Sketcher::SketchObject] Sketch106
  AttachmentOffset = pos=(0,12.5,0) rot=(0,0,1;0rad)
  FullyConstrained = true
  MapMode = 5
  Placement = pos=(0,-2.8e-15,12.5) rot=(1,0,0;1.5708rad)
  Support = -> [XZ_Plane035]
  expr: .AttachmentOffset.Base.y = 12.5mm
  expr: Constraints[1] = <<main>>.rivet_d
  sketch-geometry (1):
    g0: Circle CenterX=0 CenterY=0 CenterZ=0 NormalX=0 NormalY=0 NormalZ=1 AngleXU=0 Radius=1.7
  constraints (2):
    c: Coincident(g0,g-1)
    c: Diameter(g0) = 3.4
FEATURE [PartDesign::Pocket] Pocket062
  BaseFeature = -> Pocket061
  Direction = (0,1,2e-16)
  Length = 5
  Length2 = 5
  Midplane = true
  Profile = -> Sketch106
  ReferenceAxis = -> Sketch106 [N_Axis]
  Type = 1
FEATURE [PartDesign::Body] Body_7  label="ugol_mini_material_0.30ansi"
  Group = -> [LCS_0005,Sketch104,BaseBend006,Sketch105,DatumPlane024,Fillet002,Mirrored038,Pocket061,Sketch106,Pocket062]
  Origin = -> Origin035
  Tip = -> Pocket062
FEATURE [PartDesign::Mirrored] Mirrored039
  MirrorPlane = -> YZ_Plane036
FEATURE [PartDesign::PolarPattern] PolarPattern014
  Angle = 90
  Axis = -> X_Axis036
  Occurrences = 2
FEATURE [Sketcher::SketchObject] Sketch108
  FullyConstrained = true
  MapMode = 5
  Placement = pos=(0,0,0) rot=(0.57735,0.57735,0.57735;2.0944rad)
  Support = -> [YZ_Plane036]
  sketch-geometry (2):
    g0: LineSegment StartX=0 StartY=23 StartZ=0 EndX=0 EndY=0 EndZ=0
    g1: LineSegment StartX=0 StartY=0 StartZ=0 EndX=23 EndY=0 EndZ=0
  constraints (6):
    c: PointOnObject(g0,g-2)
    c: Coincident(g0,g-1)
    c: Coincident(g1,g0)
    c: PointOnObject(g1,g-1)
    c: Equal(g1,g0)
    c: DistanceX(g1,g1) = 23  'length'
FEATURE [PartDesign::FeaturePython] BaseBend007  # WARN: FeaturePython — macro-defined, semantics opaque (R4)
  BendSide = 0
  BendSketch = -> Sketch108
  MidPlane = true
  Reverse = false
  length = 86
  radius = 2
  thickness = 0.5
FEATURE [Sketcher::SketchObject] Sketch109
  AttachmentOffset = pos=(43,23,0) rot=(0,0,1;0rad)
  FullyConstrained = true
  MapMode = 5
  Placement = pos=(43,23,0) rot=(0,0,1;0rad)
  Support = -> [XY_Plane037]
  expr: .AttachmentOffset.Base.x = BaseBend007.length / 2
  expr: .AttachmentOffset.Base.y = Sketch108.Constraints.length
  sketch-geometry (3):
    g0: ArcOfCircle CenterX=-7.5 CenterY=-7.5 CenterZ=0 NormalX=0 NormalY=0 NormalZ=1 AngleXU=0 Radius=7.5 StartAngle=0 EndAngle=1.5708
    g1: LineSegment StartX=0 StartY=-7.5 StartZ=0 EndX=0 EndY=0 EndZ=0
    g2: LineSegment StartX=0 StartY=0 StartZ=0 EndX=-7.50003 EndY=-6.21876e-11 EndZ=0
  constraints (8):
    c: PointOnObject(g0,g-2)
    c: PointOnObject(g0,g-1)
    c: Coincident(g1,g-1)
    c: Coincident(g2,g1)
    c: Coincident(g2,g0)
    c: Tangent(g2,g0)
    c: Tangent(g1,g0) = -1.5708
    c: Diameter(g0) = 15
FEATURE [PartDesign::Pocket] Pocket063
  BaseFeature = -> BaseBend007
  Direction = (0,0,-1)
  Length = 5
  Length2 = 5
  Midplane = true
  Profile = -> Sketch109
  ReferenceAxis = -> Sketch109 [N_Axis]
  Type = 1
FEATURE [PartDesign::MultiTransform] MultiTransform013
  BaseFeature = -> Pocket063
  Originals = -> [Pocket063]
  Transformations = -> [Mirrored039,PolarPattern014]
FEATURE [Sketcher::SketchObject] Sketch110
  AttachmentOffset = pos=(0,14.5,0) rot=(0,0,1;0rad)
  FullyConstrained = true
  MapMode = 5
  Placement = pos=(0,-3.2e-15,14.5) rot=(1,0,0;1.5708rad)
  Support = -> [XZ_Plane036]
  expr: .AttachmentOffset.Base.y = 14.5mm
  expr: Constraints[3] = <<main>>.rivet_d
  sketch-geometry (2):
    g0: Circle CenterX=36 CenterY=0 CenterZ=0 NormalX=0 NormalY=0 NormalZ=1 AngleXU=0 Radius=1.7
    g1: Circle CenterX=-36 CenterY=0 CenterZ=0 NormalX=0 NormalY=0 NormalZ=1 AngleXU=0 Radius=1.7
  constraints (5):
    c: PointOnObject(g0,g-1)
    c: Symmetric(g1,g0,g-1)
    c: Equal(g0,g1)
    c: Diameter(g0) = 3.4
    c: DistanceX(g1,g0) = 72
FEATURE [PartDesign::CoordinateSystem] Local_CS034
  AttacherType = Attacher::AttachEngine3D
  MapMode = 2
  Placement = pos=(0,-3.2e-15,14.5) rot=(1,0,0;1.5708rad)
  Support = -> [Sketch110]
FEATURE [PartDesign::Pocket] Pocket064
  BaseFeature = -> MultiTransform013
  Direction = (0,1,2e-16)
  Length = 5
  Length2 = 5
  Midplane = true
  Profile = -> Sketch110
  ReferenceAxis = -> Sketch110 [N_Axis]
  Type = 1
FEATURE [Sketcher::SketchObject] Sketch111
  AttachmentOffset = pos=(0,14.5,0) rot=(0,0,1;0rad)
  FullyConstrained = true
  MapMode = 5
  Placement = pos=(0,14.5,0) rot=(0,0,1;0rad)
  Support = -> [XY_Plane037]
  expr: .AttachmentOffset.Base.y = Sketch110.AttachmentOffset.Base.y
  expr: Constraints[3] = 5.5
  expr: Constraints[4] = Sketch110.Constraints[4]
  sketch-geometry (2):
    g0: Circle CenterX=36 CenterY=0 CenterZ=0 NormalX=0 NormalY=0 NormalZ=1 AngleXU=0 Radius=2.75
    g1: Circle CenterX=-36 CenterY=0 CenterZ=0 NormalX=0 NormalY=0 NormalZ=1 AngleXU=0 Radius=2.75
  constraints (5):
    c: PointOnObject(g0,g-1)
    c: Symmetric(g1,g0,g-1)
    c: Equal(g0,g1)
    c: Diameter(g0) = 5.5
    c: DistanceX(g1,g0) = 72
FEATURE [PartDesign::Pocket] Pocket065
  BaseFeature = -> Pocket064
  Direction = (0,0,-1)
  Length = 5
  Length2 = 5
  Midplane = true
  Profile = -> Sketch111
  ReferenceAxis = -> Sketch111 [N_Axis]
  Type = 1
FEATURE [PartDesign::Body] Body001003005003015002  label="corner_5.5_material_0.30ansi"
  Group = -> [Sketch108,BaseBend007,Sketch109,Pocket063,MultiTransform013,Mirrored039,PolarPattern014,Sketch110,Pocket064,Local_CS034,Sketch111,Pocket065]
  Origin = -> Origin036
  Tip = -> Pocket065
FEATURE [PartDesign::CoordinateSystem] Local_CS035
  AttacherType = Attacher::AttachEngine3D
  AttachmentOffset = pos=(0,0,774) rot=(0,0,1;0rad)
  MapMode = 5
  Placement = pos=(0,109.238,774) rot=(0,0,1;0rad)
  Support = -> [Local_CS011]
  expr: .AttachmentOffset.Base.z = <<main>>.total_length
FEATURE [PartDesign::CoordinateSystem] Local_CS036  label="droppers_center"
  AttacherType = Attacher::AttachEngine3D
  AttachmentOffset = pos=(0,0,-19) rot=(0,0,1;0rad)
  MapMode = 5
  Placement = pos=(0,109.238,755) rot=(0,0,1;0rad)
  Support = -> [Local_CS035]
FEATURE [PartDesign::CoordinateSystem] Local_CS037  label="gutter_fixture_center"
  AttacherType = Attacher::AttachEngine3D
  AttachmentOffset = pos=(0,0,-12) rot=(0,0,1;0rad)
  MapMode = 5
  Placement = pos=(0,109.238,743) rot=(0,0,1;0rad)
  Support = -> [Local_CS036]
FEATURE [PartDesign::CoordinateSystem] Local_CS038  label="modules_top_center"
  AttacherType = Attacher::AttachEngine3D
  AttachmentOffset = pos=(0,0,-5) rot=(0,0,1;0rad)
  MapMode = 5
  Placement = pos=(0,109.238,738) rot=(0,0,1;0rad)
  Support = -> [Local_CS037]
FEATURE [Sketcher::SketchObject] Sketch112
  FullyConstrained = true
  MapMode = 5
  Placement = pos=(0,0,0) rot=(0.57735,0.57735,0.57735;2.0944rad)
  Support = -> [YZ_Plane001]
  expr: Constraints[10] = <<module>>.module_hole_x
  expr: Constraints[11] = <<module>>.module_hole_y
  sketch-geometry (5):
    g0: LineSegment StartX=-6.5 StartY=-3.5 StartZ=0 EndX=-6.5 EndY=3.5 EndZ=0
    g1: LineSegment StartX=-6.5 StartY=3.5 StartZ=0 EndX=6.5 EndY=3.5 EndZ=0
    g2: LineSegment StartX=6.5 StartY=3.5 StartZ=0 EndX=6.5 EndY=-3.5 EndZ=0
    g3: LineSegment StartX=6.5 StartY=-3.5 StartZ=0 EndX=-6.5 EndY=-3.5 EndZ=0
    g4: GeomPoint X=0 Y=0 Z=0
  constraints (12):
    c: Coincident(g0,g1)
    c: Coincident(g1,g2)
    c: Coincident(g2,g3)
    c: Coincident(g3,g0)
    c: Horizontal(g1)
    c: Horizontal(g3)
    c: Vertical(g0)
    c: Vertical(g2)
    c: Symmetric(g1,g0,g4)
    c: Coincident(g4,g-1)
    c: DistanceX(g1,g1) = 13
    c: DistanceY(g2,g2) = 7
FEATURE [Part::FeaturePython] Array  # Draft array (typed FeaturePython)
  AlwaysSyncPlacement = false
  Angle = 360
  ArrayType = 0
  Axis = (0,0,1)
  Base = -> Sketch112
  Center = (0,0,0)
  Count = 12
  ExpandArray = false
  Fuse = false
  IntervalAxis = (0,0,0)
  IntervalX = (100,0,0)
  IntervalY = (0,132,0)
  IntervalZ = (0,0,-80)
  NumberCircles = 3
  NumberPolar = 5
  NumberX = 1
  NumberY = 2
  NumberZ = 6
  Placement = pos=(0,-66,0) rot=(0,0,1;0rad)
  PlacementList = 12 placements: [(0,0,0),(0,0,-80),(0,0,-160),(0,0,-240),(0,0,-320),(0,0,-400),(0,132,0),(0,132,-80),(0,132,-160),(0,132,-240),(0,132,-320),(0,132,-400)]
  RadialDistance = 50
  ScaleList = (12) [(1,1,1),(1,1,1),(1,1,1),(1,1,1),(1,1,1),(1,1,1),(1,1,1),(1,1,1),(1,1,1),(1,1,1),(1,1,1),(1,1,1)]
  Symmetry = 1
  TangentialDistance = 25
  expr: .IntervalY.y = <<module>>.module_fixture_distance_x
  expr: .IntervalZ.z = -<<module>>.module_fixture_distance_y
  expr: .Placement.Base.y = -<<module>>.module_fixture_distance_x / 2
  expr: NumberZ = <<main>>.number_of_modules
FEATURE [Sketcher::SketchObject] Sketch113
  FullyConstrained = true
  MapMode = 5
  Placement = pos=(0,0,0) rot=(0.57735,0.57735,0.57735;2.0944rad)
  Support = -> [YZ_Plane001]
  expr: Constraints[18] = <<dropper>>.d + 2mm
  expr: Constraints[19] = <<dropper>>.center_height_offset
  sketch-geometry (8):
    g0: ArcOfCircle CenterX=0 CenterY=0 CenterZ=0 NormalX=0 NormalY=0 NormalZ=1 AngleXU=0 Radius=12.625 StartAngle=3.14159 EndAngle=6.28319
    g1: LineSegment StartX=12.625 StartY=-3.1e-15 StartZ=0 EndX=12.625 EndY=12.5 EndZ=0
    g2: LineSegment StartX=-12.625 StartY=1.5e-15 StartZ=0 EndX=-12.625 EndY=12.5 EndZ=0
    g3: ArcOfCircle CenterX=15.125 CenterY=12.5 CenterZ=0 NormalX=0 NormalY=0 NormalZ=1 AngleXU=0 Radius=2.5 StartAngle=1.5708 EndAngle=3.14159
    g4: ArcOfCircle CenterX=-15.125 CenterY=12.5 CenterZ=0 NormalX=0 NormalY=0 NormalZ=1 AngleXU=0 Radius=2.5 StartAngle=0 EndAngle=1.5708
    g5: LineSegment StartX=-15.125 StartY=15 StartZ=0 EndX=-15.125 EndY=19 EndZ=0
    g6: LineSegment StartX=-15.125 StartY=19 StartZ=0 EndX=15.125 EndY=19 EndZ=0
    g7: LineSegment StartX=15.125 StartY=19 StartZ=0 EndX=15.125 EndY=15 EndZ=0
  constraints (24):
    c: Coincident(g0,g-1)
    c: PointOnObject(g0,g-1)
    c: PointOnObject(g0,g-1)
    c: Coincident(g1,g0)
    c: Vertical(g1)
    c: Coincident(g2,g0)
    c: Vertical(g2)
    c: Coincident(g5,g4)
    c: Vertical(g5)
    c: Coincident(g6,g5)
    c: Horizontal(g6)
    c: Coincident(g7,g6)
    c: Coincident(g7,g3)
    c: Vertical(g7)
    c: Perpendicular(g3,g7)
    c: Tangent(g3,g1) = 1.5708
    c: Tangent(g4,g2) = -1.5708
    c: Perpendicular(g4,g5)
    c: Diameter(g0) = 25.25
    c: Distance(g0,g6) = 19
    c: Equal(g4,g3)
    c: Diameter(g4) = 5
    c: DistanceY(g7,g7) = 4
    c: Equal(g5,g7)
FEATURE [Part::FeaturePython] Array001  # Draft array (typed FeaturePython)
  AlwaysSyncPlacement = false
  Angle = 360
  ArrayType = 0
  Axis = (0,0,1)
  Base = -> Sketch113
  Center = (0,0,0)
  Count = 2
  ExpandArray = false
  Fuse = false
  IntervalAxis = (0,0,0)
  IntervalX = (100,0,0)
  IntervalY = (0,60,0)
  IntervalZ = (0,0,100)
  NumberCircles = 3
  NumberPolar = 5
  NumberX = 1
  NumberY = 2
  NumberZ = 1
  Placement = pos=(0,-30,0) rot=(0,0,1;0rad)
  PlacementList = 2 placements: [(0,0,0),(0,60,0)]
  RadialDistance = 50
  ScaleList = (2) [(1,1,1),(1,1,1)]
  Symmetry = 1
  TangentialDistance = 25
  expr: .IntervalY.y = <<dropper>>.distance_between_droppers1
  expr: .Placement.Base.y = -<<dropper>>.distance_between_droppers1 / 2
FEATURE [Part::FeaturePython] Array002  # Draft array (typed FeaturePython)
  AlwaysSyncPlacement = false
  Angle = 360
  ArrayType = 0
  Axis = (0,0,1)
  Base = -> Sketch113
  Center = (0,0,0)
  Count = 2
  ExpandArray = false
  Fuse = false
  IntervalAxis = (0,0,0)
  IntervalX = (100,0,0)
  IntervalY = (0,70,0)
  IntervalZ = (0,0,100)
  NumberCircles = 3
  NumberPolar = 5
  NumberX = 1
  NumberY = 2
  NumberZ = 1
  Placement = pos=(0,-35,0) rot=(0,0,1;0rad)
  PlacementList = 2 placements: [(0,0,0),(0,70,0)]
  RadialDistance = 50
  ScaleList = (2) [(1,1,1),(1,1,1)]
  Symmetry = 1
  TangentialDistance = 25
  expr: .IntervalY.y = <<dropper>>.distance_between_droppers2
  expr: .Placement.Base.y = -<<dropper>>.distance_between_droppers2 / 2
FEATURE [PartDesign::SubShapeBinder] Binder032
  BindCopyOnChange = 0
  BindMode = 0
  ClaimChildren = false
  Context = -> Body001 [Binder032.]
  Fuse = false
  MakeFace = true
  OffsetFill = false
  OffsetIntersection = false
  OffsetJoinType = 0
  OffsetOpenResult = false
  PartialLoad = false
  Placement = pos=(0,109.238,755) rot=(0,0,1;0rad)
  Relative = true
  Support = -> [Array001]
  _Version = 2
  expr: Placement = <<droppers_center>>.Placement
FEATURE [PartDesign::SubShapeBinder] Binder033
  BindCopyOnChange = 0
  BindMode = 0
  ClaimChildren = false
  Context = -> Body001 [Binder033.]
  Fuse = false
  MakeFace = true
  OffsetFill = false
  OffsetIntersection = false
  OffsetJoinType = 0
  OffsetOpenResult = false
  PartialLoad = false
  Placement = pos=(0,109.238,755) rot=(0,0,1;0rad)
  Relative = true
  Support = -> [Array002]
  _Version = 2
  expr: Placement = <<droppers_center>>.Placement
FEATURE [PartDesign::SubShapeBinder] Binder034
  BindCopyOnChange = 0
  BindMode = 0
  ClaimChildren = false
  Context = -> Body001 [Binder034.]
  Fuse = false
  MakeFace = true
  OffsetFill = false
  OffsetIntersection = false
  OffsetJoinType = 0
  OffsetOpenResult = false
  PartialLoad = false
  Placement = pos=(0,109.238,738) rot=(0,0,1;0rad)
  Relative = true
  Support = -> [Array]
  _Version = 2
  expr: Placement = <<modules_top_center>>.Placement
FEATURE [Sketcher::SketchObject] Sketch114
  FullyConstrained = true
  MapMode = 5
  Placement = pos=(0,0,0) rot=(0.57735,0.57735,0.57735;2.0944rad)
  Support = -> [YZ_Plane001]
  expr: Constraints[1] = <<main>>.rivet_d
  sketch-geometry (1):
    g0: Circle CenterX=0 CenterY=0 CenterZ=0 NormalX=0 NormalY=0 NormalZ=1 AngleXU=0 Radius=1.7
  constraints (2):
    c: Coincident(g0,g-1)
    c: Diameter(g0) = 3.4
FEATURE [Part::FeaturePython] Array003  # Draft array (typed FeaturePython)
  AlwaysSyncPlacement = false
  Angle = 360
  ArrayType = 0
  Axis = (0,0,1)
  Base = -> Sketch114
  Center = (0,0,0)
  Count = 2
  ExpandArray = false
  Fuse = false
  IntervalAxis = (0,0,0)
  IntervalX = (100,0,0)
  IntervalY = (0,102,0)
  IntervalZ = (0,0,100)
  NumberCircles = 3
  NumberPolar = 5
  NumberX = 1
  NumberY = 2
  NumberZ = 1
  Placement = pos=(0,-51,0) rot=(0,0,1;0rad)
  PlacementList = 2 placements: [(0,0,0),(0,102,0)]
  RadialDistance = 50
  ScaleList = (2) [(1,1,1),(1,1,1)]
  Symmetry = 1
  TangentialDistance = 25
  expr: .IntervalY.y = <<main>>.gutter_fix_holes_distance * 2
  expr: .Placement.Base.y = -.IntervalY.y / 2
FEATURE [PartDesign::SubShapeBinder] Binder035
  BindCopyOnChange = 0
  BindMode = 0
  ClaimChildren = false
  Context = -> Body001 [Binder035.]
  Fuse = false
  MakeFace = true
  OffsetFill = false
  OffsetIntersection = false
  OffsetJoinType = 0
  OffsetOpenResult = false
  PartialLoad = false
  Placement = pos=(0,109.238,743) rot=(0,0,1;0rad)
  Relative = true
  Support = -> [Array003]
  _Version = 2
  expr: Placement = <<gutter_fixture_center>>.Placement
FEATURE [Sketcher::SketchObject] Sketch115
  FullyConstrained = true
  MapMode = 5
  Support = -> [XY_Plane]
  expr: Constraints[1] = <<main>>.rivet_d
  sketch-geometry (1):
    g0: Circle CenterX=0 CenterY=145 CenterZ=0 NormalX=0 NormalY=0 NormalZ=1 AngleXU=0 Radius=1.7
  constraints (3):
    c: PointOnObject(g0,g-2)
    c: Diameter(g0) = 3.4
    c: DistanceY(g0) = 145
FEATURE [PartDesign::Pocket] Pocket070
  BaseFeature = -> Fold002
  Direction = (0,0,-1)
  Length = 5
  Length2 = 5
  Midplane = true
  Profile = -> Sketch115
  ReferenceAxis = -> Sketch115 [N_Axis]
  Type = 1
FEATURE [PartDesign::Body] Body  label="gutter001_material_0.50ansi"
  Group = -> [Sketch,Pad,Mirrored005,Local_CS001,Local_CS002,Local_CS003,Local_CS004,DatumPlane003,DatumPlane004,DatumPlane005,DatumPlane006,Sketch037,Pocket008,MultiTransform002,Mirrored006,Mirrored007,Binder,Pocket009,MultiTransform003,Mirrored008,DatumPlane007,Mirrored009,Sketch010,Sketch038,Sketch039,Pocket010,MultiTransform004,Mirrored010,Mirrored011,Fold,Fold002,Local_CS024,Sketch115,Pocket070]
  Origin = -> Origin
  Tip = -> Pocket070
FEATURE [PartDesign::CoordinateSystem] LCS_0006
  AttacherType = Attacher::AttachEngine3D
  MapMode = 2
  Support = -> [X_Axis037]
FEATURE [Sketcher::SketchObject] Sketch116
  FullyConstrained = true
  MapMode = 5
  Placement = pos=(0,0,0) rot=(0.57735,0.57735,0.57735;2.0944rad)
  Support = -> [YZ_Plane037]
  expr: .Constraints.height = <<main>>.basin_height - <<main>>.thickness
  sketch-geometry (4):
    g0: LineSegment StartX=0 StartY=0 StartZ=0 EndX=25 EndY=0 EndZ=0
    g1: LineSegment StartX=25 StartY=0 StartZ=0 EndX=25 EndY=154 EndZ=0
    g2: LineSegment StartX=25 StartY=154 StartZ=0 EndX=0 EndY=154 EndZ=0
    g3: LineSegment StartX=0 StartY=154 StartZ=0 EndX=0 EndY=0 EndZ=0
  constraints (11):
    c: Coincident(g0,g1)
    c: Coincident(g1,g2)
    c: Coincident(g2,g3)
    c: Coincident(g3,g0)
    c: Horizontal(g0)
    c: Horizontal(g2)
    c: Vertical(g1)
    c: Vertical(g3)
    c: Coincident(g0,g-1)
    c: Distance(g3) = 154  'height'
    c: DistanceX(g0) = 25  'length'
FEATURE [PartDesign::FeaturePython] BaseBend008  # WARN: FeaturePython — macro-defined, semantics opaque (R4)
  BendSide = 1
  BendSketch = -> Sketch116
  MidPlane = true
  Reverse = false
  length = 25
  radius = 0.01
  thickness = 0.3
  expr: radius = <<main>>.bend_r
FEATURE [PartDesign::FeaturePython] Bend015  # WARN: FeaturePython — macro-defined, semantics opaque (R4)
  AutoMiter = true
  BaseFeature = -> BaseBend008
  BendType = 0
  LengthList = [25]
  LengthSpec = 1
  ReliefFactor = 0.7
  UseReliefFactor = false
  angle = 90
  baseObject = -> BaseBend008 [Edge26]
  bendAList = [90]
  extend1 = 0
  extend2 = 0
  gap1 = 3
  gap2 = 3
  invert = false
  kfactor = 0.5
  length = 25
  maxExtendDist = 5
  minGap = 0.1
  minReliefGap = 1
  miterangle1 = 0
  miterangle2 = 0
  offset = 0
  radius = 0.01
  reliefType = 0
  reliefd = 0.1
  reliefw = 0.1
  sketchflip = false
  sketchinvert = false
  unfold = false
  expr: length = Sketch116.Constraints.length
  expr: radius = <<main>>.bend_r
FEATURE [PartDesign::FeaturePython] Bend016  # WARN: FeaturePython — macro-defined, semantics opaque (R4)
  AutoMiter = true
  BaseFeature = -> Bend015
  BendType = 0
  LengthList = [25]
  LengthSpec = 0
  ReliefFactor = 0.7
  UseReliefFactor = false
  angle = 90
  baseObject = -> Bend015 [Edge3]
  bendAList = [90]
  extend1 = 0
  extend2 = 0
  gap1 = 3
  gap2 = 0
  invert = false
  kfactor = 0.5
  length = 25
  maxExtendDist = 5
  minGap = 0.1
  minReliefGap = 1
  miterangle1 = 0
  miterangle2 = 0
  offset = 0
  radius = 0.01
  reliefType = 0
  reliefd = 0.1
  reliefw = 0.1
  sketchflip = false
  sketchinvert = false
  unfold = false
  expr: length = BaseBend008.length
  expr: radius = <<main>>.bend_r
FEATURE [PartDesign::FeaturePython] Bend017  # WARN: FeaturePython — macro-defined, semantics opaque (R4)
  AutoMiter = true
  BaseFeature = -> Bend016
  BendType = 0
  LengthList = [25]
  LengthSpec = 0
  ReliefFactor = 0.7
  UseReliefFactor = false
  angle = 90
  baseObject = -> Bend016 [Edge24]
  bendAList = [90]
  extend1 = 0
  extend2 = 0
  gap1 = 0
  gap2 = 3
  invert = false
  kfactor = 0.5
  length = 25
  maxExtendDist = 5
  minGap = 0.1
  minReliefGap = 1
  miterangle1 = 0
  miterangle2 = 0
  offset = 0
  radius = 0.01
  reliefType = 0
  reliefd = 0.1
  reliefw = 0.1
  sketchflip = false
  sketchinvert = false
  unfold = false
  expr: length = BaseBend008.length
  expr: radius = <<main>>.bend_r
FEATURE [Sketcher::SketchObject] Sketch117
  FullyConstrained = true
  MapMode = 5
  Support = -> [XY_Plane038]
  expr: Constraints[12] = <<main>>.rivet_d
  expr: Constraints[8] = Sketch116.Constraints.length
  sketch-geometry (5):
    g0: Circle CenterX=0 CenterY=6 CenterZ=0 NormalX=0 NormalY=0 NormalZ=1 AngleXU=0 Radius=1.7
    g1: Circle CenterX=0 CenterY=19 CenterZ=0 NormalX=0 NormalY=0 NormalZ=1 AngleXU=0 Radius=1.7
    g2: LineSegment StartX=0 StartY=0 StartZ=0 EndX=0 EndY=6 EndZ=0
    g3: LineSegment StartX=0 StartY=6 StartZ=0 EndX=0 EndY=19 EndZ=0
    g4: LineSegment StartX=0 StartY=19 StartZ=0 EndX=0 EndY=25 EndZ=0
  constraints (13):
    c: PointOnObject(g0,g-2)
    c: PointOnObject(g1,g-2)
    c: Coincident(g2,g-1)
    c: Coincident(g2,g0)
    c: Coincident(g3,g0)
    c: Coincident(g3,g1)
    c: Coincident(g4,g1)
    c: PointOnObject(g4,g-2)
    c: DistanceY(g4) = 25
    c: Equal(g2,g4)
    c: Distance(g2) = 6
    c: Equal(g0,g1)
    c: Diameter(g0) = 3.4
FEATURE [PartDesign::Pocket] Pocket071
  BaseFeature = -> Bend017
  Direction = (0,0,-1)
  Length = 5
  Length2 = 5
  Midplane = true
  Profile = -> Sketch117
  ReferenceAxis = -> Sketch117 [N_Axis]
  Type = 1
FEATURE [Sketcher::SketchObject] Sketch118
  FullyConstrained = true
  MapMode = 5
  Placement = pos=(0,0,0) rot=(0.57735,0.57735,0.57735;2.0944rad)
  Support = -> [YZ_Plane037]
  sketch-geometry (4):
    g0: LineSegment StartX=60 StartY=130 StartZ=0 EndX=160 EndY=130 EndZ=0
    g1: LineSegment StartX=160 StartY=130 StartZ=0 EndX=160 EndY=180 EndZ=0
    g2: LineSegment StartX=160 StartY=180 StartZ=0 EndX=60 EndY=180 EndZ=0
    g3: LineSegment StartX=60 StartY=180 StartZ=0 EndX=60 EndY=130 EndZ=0
  constraints (12):
    c: Coincident(g0,g1)
    c: Coincident(g1,g2)
    c: Coincident(g2,g3)
    c: Coincident(g3,g0)
    c: Horizontal(g0)
    c: Horizontal(g2)
    c: Vertical(g1)
    c: Vertical(g3)
    c: DistanceY(g3,g3) = 50  'height'
    c: DistanceX(g0,g0) = 100  'length'
    c: DistanceX(g0) = 60
    c: DistanceY(g0) = 130
FEATURE [Sketcher::SketchObject] Sketch119
  AttachmentOffset = pos=(180,12.5,0) rot=(0,0,1;0rad)
  FullyConstrained = true
  MapMode = 5
  Placement = pos=(3.72e-14,180,12.5) rot=(0.57735,0.57735,0.57735;2.0944rad)
  Support = -> [YZ_Plane001]
  expr: .AttachmentOffset.Base.y = Sketch106.AttachmentOffset.Base.y
  expr: Constraints[1] = <<main>>.rivet_d
  sketch-geometry (1):
    g0: Circle CenterX=0 CenterY=0 CenterZ=0 NormalX=0 NormalY=0 NormalZ=1 AngleXU=0 Radius=1.7
  constraints (2):
    c: Coincident(g0,g-1)
    c: Diameter(g0) = 3.4
FEATURE [PartDesign::SubShapeBinder] Binder036
  BindCopyOnChange = 0
  BindMode = 0
  ClaimChildren = false
  Context = -> Body001003005003 [Binder036.]
  Fuse = false
  MakeFace = true
  OffsetFill = false
  OffsetIntersection = false
  OffsetJoinType = 0
  OffsetOpenResult = false
  PartialLoad = false
  Placement = pos=(13,180,0) rot=(0,0,1;1.5708rad)
  Relative = true
  Support = -> [Body_7[Pocket061.Sketch105.]]
  _Version = 2
  expr: .Placement.Base.x = <<main>>.end_face_width / 2 - <<main>>.thickness
  expr: .Placement.Base.y = Sketch119.AttachmentOffset.Base.x
FEATURE [PartDesign::Pocket] Pocket074
  BaseFeature = -> Pocket036
  Direction = (0,0,-1)
  Length = 5
  Length2 = 5
  Midplane = true
  Profile = -> Binder036
  Type = 1
FEATURE [PartDesign::Mirrored] Mirrored
  MirrorPlane = -> YZ_Plane015
FEATURE [PartDesign::PolarPattern] PolarPattern015
  Angle = 360
  Axis = -> Z_Axis015
  Occurrences = 3
FEATURE [PartDesign::MultiTransform] MultiTransform
  BaseFeature = -> Pocket074
  Originals = -> [Pocket074]
  Transformations = -> [Mirrored,PolarPattern015]
FEATURE [Sketcher::SketchObject] Sketch120
  AttachmentOffset = pos=(0,-70,0) rot=(0,0,1;0rad)
  FullyConstrained = true
  MapMode = 5
  Placement = pos=(0,-70,0) rot=(0,0,1;0rad)
  Support = -> [XY_Plane016]
  sketch-geometry (1):
    g0: Circle CenterX=0 CenterY=0 CenterZ=0 NormalX=0 NormalY=0 NormalZ=1 AngleXU=0 Radius=4.25
  constraints (2):
    c: Coincident(g0,g-1)
    c: Diameter(g0) = 8.5
FEATURE [Sketcher::SketchObject] Sketch121
  FullyConstrained = true
  MapMode = 5
  Support = -> [XY_Plane018]
  expr: Constraints[14] = <<main>>.end_face_width / 2 + 2mm
  expr: Constraints[7] = Sketch052.Constraints.r - 12mm
  sketch-geometry (7):
    g0: ArcOfCircle CenterX=0 CenterY=0 CenterZ=0 NormalX=0 NormalY=0 NormalZ=1 AngleXU=0 Radius=196.875 StartAngle=0.771863 EndAngle=1.5708
    g1: LineSegment StartX=141.083 StartY=137.315 StartZ=0 EndX=149.802 EndY=128.357 EndZ=0
    g2: LineSegment StartX=149.802 StartY=128.357 StartZ=0 EndX=158.52 EndY=119.4 EndZ=0
    g3: LineSegment StartX=158.52 StartY=119.4 StartZ=0 EndX=140.605 EndY=101.963 EndZ=0
    g4: LineSegment StartX=0 StartY=0 StartZ=0 EndX=175.892 EndY=101.551 EndZ=0
    g5: LineSegment StartX=140.605 StartY=101.963 StartZ=0 EndX=123.168 EndY=119.878 EndZ=0
    g6: LineSegment StartX=123.168 StartY=119.878 StartZ=0 EndX=141.083 EndY=137.315 EndZ=0
  constraints (21):
    c: Coincident(g0,g-1)
    c: PointOnObject(g0,g-2)
    c: Coincident(g2,g1)
    c: Parallel(g1,g2)
    c: Equal(g2,g1)
    c: Distance(g2,g0) = 25
    c: Tangent(g1,g0) = 1.5708
    c: DistanceY(g0) = 196.875
    c: Coincident(g3,g2)
    c: Distance(g3) = 25
    c: Coincident(g4,g0)
    c: PointOnObject(g4,g2)
    c: Perpendicular(g2,g3)
    c: Angle(g-1,g4) = 0.523599
    c: Distance(g3,g4) = 18
    c: Distance(g2,g4) = 24.143
    c: Coincident(g5,g3)
    c: Perpendicular(g5,g3)
    c: Coincident(g6,g5)
    c: Coincident(g6,g0)
    c: Perpendicular(g5,g6)
FEATURE [Sketcher::SketchObject] Sketch053
  ExternalGeometry = -> [Sketch121]
  FullyConstrained = true
  MapMode = 5
  Support = -> [XY_Plane018]
  expr: Constraints[2] = Sketch052.Constraints.r - Sketch052.Constraints.width - 2mm
  sketch-geometry (7):
    g0: LineSegment StartX=1.12e-14 StartY=182.848 StartZ=0 EndX=1.21e-14 EndY=197.848 EndZ=0
    g1: ArcOfCircle CenterX=0 CenterY=0 CenterZ=0 NormalX=0 NormalY=0 NormalZ=1 AngleXU=0 Radius=182.848 StartAngle=0.777302 EndAngle=1.5708
    g2: ArcOfCircle CenterX=0 CenterY=0 CenterZ=0 NormalX=0 NormalY=0 NormalZ=1 AngleXU=0 Radius=197.848 StartAngle=0.776943 EndAngle=1.5708
    g3: LineSegment StartX=131.746 StartY=128.227 StartZ=0 EndX=141.062 EndY=137.294 EndZ=0
    g4: ArcOfCircle CenterX=140.365 CenterY=138.011 CenterZ=0 NormalX=0 NormalY=0 NormalZ=1 AngleXU=0 Radius=1 StartAngle=5.48425 EndAngle=7.06013
    g5: ArcOfCircle CenterX=131.049 CenterY=128.944 CenterZ=0 NormalX=0 NormalY=0 NormalZ=1 AngleXU=0 Radius=1 StartAngle=3.91889 EndAngle=5.48425
    g6: GeomPoint X=131.032 Y=127.532 Z=0
  constraints (18):
    c: PointOnObject(g0,g-2)
    c: PointOnObject(g0,g-2)
    c: DistanceY(g0) = 197.848
    c: Tangent(g3,g4) = -1.5708
    c: Tangent(g2,g4) = -1.5708
    c: Tangent(g3,g5) = -1.5708
    c: Tangent(g1,g5) = 1.5708
    c: Equal(g5,g4)
    c: Diameter(g5) = 2
    c: Perpendicular(g-3,g3)
    c: PointOnObject(g-3,g3)
    c: Coincident(g2,g0)
    c: Coincident(g1,g0)
    c: PointOnObject(g6,g3)
    c: PointOnObject(g6,g1)
    c: Coincident(g1,g2)
    c: DistanceY(g0,g0) = 15
    c: Coincident(g1,g-1)
FEATURE [PartDesign::Pad] Pad015
  Direction = (0,0,1)
  Length = 3
  Length2 = 10
  Profile = -> Sketch053
  ReferenceAxis = -> Sketch053 [N_Axis]
  Type = 0
FEATURE [PartDesign::Mirrored] Mirrored020
  BaseFeature = -> Pad015
  MirrorPlane = -> Sketch053 [V_Axis]
  Originals = -> [Pad015]
  Refine = true
FEATURE [Sketcher::SketchObject] Sketch054
  ExternalGeometry = -> [Sketch053]
  FullyConstrained = true
  MapMode = 5
  Support = -> [XY_Plane018]
  expr: Constraints[1] = <<main>>.rivet_d
  sketch-geometry (6):
    g0: ArcOfCircle CenterX=0 CenterY=0 CenterZ=0 NormalX=0 NormalY=0 NormalZ=1 AngleXU=0 Radius=190.346 StartAngle=0.771863 EndAngle=1.5708
    g1: Circle CenterX=129.244 CenterY=139.741 CenterZ=0 NormalX=0 NormalY=0 NormalZ=1 AngleXU=0 Radius=1.7
    g2: Circle CenterX=1.17e-14 CenterY=190.346 CenterZ=0 NormalX=0 NormalY=0 NormalZ=1 AngleXU=0 Radius=1.7
    g3: Circle CenterX=-129.244 CenterY=139.741 CenterZ=0 NormalX=0 NormalY=0 NormalZ=1 AngleXU=0 Radius=1.7
    g4: LineSegment StartX=131.746 StartY=128.227 StartZ=0 EndX=136.404 EndY=132.761 EndZ=0
    g5: LineSegment StartX=136.404 StartY=132.761 StartZ=0 EndX=141.062 EndY=137.294 EndZ=0
  constraints (15):
    c: PointOnObject(g1,g0)
    c: Diameter(g1) = 3.4
    c: Coincident(g2,g0)
    c: Equal(g2,g1)
    c: Equal(g3,g1)
    c: Symmetric(g1,g3,g-2)
    c: Coincident(g5,g4)
    c: Equal(g4,g5)
    c: Parallel(g4,g5)
    c: Coincident(g0,g4)
    c: Coincident(g0,g-1)
    c: Distance(g1,g0) = 10
    c: PointOnObject(g2,g-2)
    c: Coincident(g4,g-3)
    c: Coincident(g5,g-3)
FEATURE [PartDesign::Pocket] Pocket018
  BaseFeature = -> Mirrored020
  Direction = (0,0,-1)
  Length = 5
  Length2 = 5
  Midplane = true
  Profile = -> Sketch054
  ReferenceAxis = -> Sketch054 [N_Axis]
  Type = 1
FEATURE [PartDesign::Body] Body001003005003004  label="plexiglass_holder_tech_top"
  Group = -> [Sketch053,Pad015,Mirrored020,Pocket018,Local_CS019,Sketch054,Sketch121]
  Origin = -> Origin017
  Placement = pos=(0,0,0) rot=(0,0,1;1.0472rad)
  Tip = -> Pocket018
FEATURE [PartDesign::SubShapeBinder] Binder037
  BindCopyOnChange = 0
  BindMode = 0
  ClaimChildren = false
  Context = -> Body001003005003014 [Binder037.]
  Fuse = false
  MakeFace = true
  OffsetFill = false
  OffsetIntersection = false
  OffsetJoinType = 0
  OffsetOpenResult = false
  PartialLoad = false
  Relative = false
  Support = -> [Body001003005003004[Sketch121.Edge2]]
  _Version = 2
FEATURE [PartDesign::CoordinateSystem] Local_CS040
  AttacherType = Attacher::AttachEngine3D
  AttachmentOffset = pos=(0,0,0) rot=(-0.57735,-0.57735,-0.57735;2.0944rad)
  MapMode = 7
  Placement = pos=(149.802,128.357,0) rot=(0,0,1;2.34266rad)
  Support = -> [Binder037]
FEATURE [PartDesign::SubShapeBinder] Binder038
  BindCopyOnChange = 0
  BindMode = 0
  ClaimChildren = false
  Context = -> tech_sector [Body001003005003014.Binder038.]
  Fuse = false
  MakeFace = true
  OffsetFill = false
  OffsetIntersection = false
  OffsetJoinType = 0
  OffsetOpenResult = false
  PartialLoad = false
  Placement = pos=(149.802,128.357,0) rot=(0,0,1;2.34266rad)
  Relative = true
  Support = -> [tech_pillar[Pocket071.Sketch117.]]
  _Version = 2
  expr: Placement = Local_CS040.Placement
FEATURE [PartDesign::Pocket] Pocket059
  BaseFeature = -> Pocket045
  Direction = (-4e-16,0,-1)
  Length = 5
  Length2 = 5
  Midplane = true
  Profile = -> Binder038
  Type = 1
FEATURE [PartDesign::CoordinateSystem] LCS_0007
  AttacherType = Attacher::AttachEngine3D
  MapMode = 2
  Support = -> [X_Axis038]
FEATURE [Sketcher::SketchObject] Sketch122
  FullyConstrained = true
  MapMode = 5
  Placement = pos=(0,0,0) rot=(0.57735,0.57735,0.57735;2.0944rad)
  Support = -> [YZ_Plane038]
  expr: .Constraints.height = <<main>>.basin_height - <<main>>.thickness * 2
  sketch-geometry (4):
    g0: LineSegment StartX=0 StartY=0 StartZ=0 EndX=15 EndY=0 EndZ=0
    g1: LineSegment StartX=15 StartY=0 StartZ=0 EndX=15 EndY=151 EndZ=0
    g2: LineSegment StartX=15 StartY=151 StartZ=0 EndX=0 EndY=151 EndZ=0
    g3: LineSegment StartX=0 StartY=151 StartZ=0 EndX=0 EndY=0 EndZ=0
  constraints (11):
    c: Coincident(g0,g1)
    c: Coincident(g1,g2)
    c: Coincident(g2,g3)
    c: Coincident(g3,g0)
    c: Horizontal(g0)
    c: Horizontal(g2)
    c: Vertical(g1)
    c: Vertical(g3)
    c: Coincident(g0,g-1)
    c: DistanceY(g2) = 151  'height'
    c: DistanceX(g0,g0) = 15  'length'
FEATURE [PartDesign::FeaturePython] BaseBend009  # WARN: FeaturePython — macro-defined, semantics opaque (R4)
  BendSide = 1
  BendSketch = -> Sketch122
  MidPlane = true
  Reverse = false
  length = 10
  radius = 0.1
  thickness = 0.3
FEATURE [Sketcher::SketchObject] Sketch123
  FullyConstrained = true
  MapMode = 5
  Support = -> [XY_Plane039]
  expr: Constraints[1] = <<main>>.rivet_d
  expr: Constraints[7] = Sketch122.Constraints.length
  sketch-geometry (3):
    g0: Circle CenterX=0 CenterY=7.5 CenterZ=0 NormalX=0 NormalY=0 NormalZ=1 AngleXU=0 Radius=1.7
    g1: LineSegment StartX=0 StartY=0 StartZ=0 EndX=0 EndY=7.5 EndZ=0
    g2: LineSegment StartX=0 StartY=7.5 StartZ=0 EndX=0 EndY=15 EndZ=0
  constraints (8):
    c: PointOnObject(g0,g-2)
    c: Diameter(g0) = 3.4
    c: Coincident(g1,g-1)
    c: Coincident(g1,g0)
    c: Coincident(g2,g0)
    c: PointOnObject(g2,g-2)
    c: Equal(g2,g1)
    c: DistanceY(g2) = 15
FEATURE [PartDesign::Pocket] Pocket076
  BaseFeature = -> BaseBend009
  Direction = (0,0,-1)
  Length = 5
  Length2 = 5
  Midplane = true
  Profile = -> Sketch123
  ReferenceAxis = -> Sketch123 [N_Axis]
  Type = 1
FEATURE [Sketcher::SketchObject] Sketch124
  FullyConstrained = true
  MapMode = 5
  Placement = pos=(0,0,0) rot=(1,0,0;1.5708rad)
  Support = -> [XZ_Plane038]
  expr: Constraints[1] = Sketch122.Constraints.height
  expr: Constraints[3] = <<main>>.rivet_d
  sketch-geometry (2):
    g0: Circle CenterX=0 CenterY=75.5 CenterZ=0 NormalX=0 NormalY=0 NormalZ=1 AngleXU=0 Radius=1.7
    g1: GeomPoint X=0 Y=151 Z=0
  constraints (4):
    c: PointOnObject(g0,g-2)
    c: DistanceY(g1) = 151
    c: Symmetric(g1,g-1,g0)
    c: Diameter(g0) = 3.4
FEATURE [PartDesign::Pocket] Pocket077
  BaseFeature = -> Pocket076
  Direction = (0,1,2e-16)
  Length = 5
  Length2 = 5
  Midplane = true
  Profile = -> Sketch124
  ReferenceAxis = -> Sketch124 [N_Axis]
  Type = 1
FEATURE [PartDesign::Body] tech_mid  label="tech_mid_material_0.50ansi"
  Group = -> [LCS_0007,Sketch122,BaseBend009,Sketch123,Pocket076,Sketch124,Pocket077]
  Origin = -> Origin038
  Tip = -> Pocket077
FEATURE [PartDesign::SubShapeBinder] Binder039
  BindCopyOnChange = 0
  BindMode = 0
  ClaimChildren = false
  Context = -> tech_sector [Body_6.Binder039.]
  Fuse = false
  MakeFace = true
  OffsetFill = false
  OffsetIntersection = false
  OffsetJoinType = 0
  OffsetOpenResult = false
  PartialLoad = false
  Relative = true
  Support = -> [Body001003005003014[Binder038.]]
  _Version = 2
FEATURE [Sketcher::SketchObject] Sketch101
  ExternalGeometry = -> [Binder039]
  FullyConstrained = false
  MapMode = 5
  Support = -> [XY_Plane035]
  expr: .Constraints.r = Sketch052.Constraints.r - Sketch052.Constraints.width - 2mm
  sketch-geometry (12):
    g0: LineSegment StartX=0 StartY=174.647 StartZ=0 EndX=0 EndY=197.848 EndZ=0
    g1: LineSegment StartX=0 StartY=0 StartZ=0 EndX=170.499 EndY=98.4377 EndZ=0
    g2: ArcOfCircle CenterX=0 CenterY=0 CenterZ=0 NormalX=0 NormalY=0 NormalZ=1 AngleXU=0 Radius=174.647 StartAngle=0.634796 EndAngle=1.5708
    g3: ArcOfCircle CenterX=0 CenterY=0 CenterZ=0 NormalX=0 NormalY=0 NormalZ=1 AngleXU=0 Radius=197.848 StartAngle=0.771863 EndAngle=1.5708
    g4: LineSegment StartX=141.781 StartY=137.994 StartZ=0 EndX=150.499 EndY=129.036 EndZ=0
    g5: LineSegment StartX=150.499 StartY=129.036 StartZ=0 EndX=159.217 EndY=120.078 EndZ=0
    g6: LineSegment StartX=145.502 StartY=124.173 StartZ=0 EndX=150.499 EndY=129.036 EndZ=0
    g7: LineSegment StartX=150.499 StartY=129.036 StartZ=0 EndX=158.52 EndY=120.795 EndZ=0
    g8: ArcOfCircle CenterX=157.803 CenterY=120.097 CenterZ=0 NormalX=0 NormalY=0 NormalZ=1 AngleXU=0 Radius=1 StartAngle=5.48425 EndAngle=7.05505
    g9: LineSegment StartX=158.501 StartY=119.381 StartZ=0 EndX=142.127 EndY=103.444 EndZ=0
    g10: ArcOfCircle CenterX=141.43 CenterY=104.161 CenterZ=0 NormalX=0 NormalY=0 NormalZ=1 AngleXU=0 Radius=1 StartAngle=3.77639 EndAngle=5.48425
    g11: GeomPoint X=141.302 Y=102.642 Z=0
  constraints (32):
    c: PointOnObject(g0,g-2)
    c: PointOnObject(g0,g-2)
    c: Coincident(g2,g0)
    c: Coincident(g3,g0)
    c: Angle(g-1,g1) = 0.523599
    c: DistanceY(g0) = 197.848  'r'
    c: Coincident(g2,g-1)
    c: Coincident(g2,g1)
    c: Coincident(g5,g4)
    c: Parallel(g4,g5)
    c: Equal(g4,g5)
    c: Tangent(g4,g3) = 1.5708
    c: Coincident(g6,g-3)
    c: Coincident(g6,g4)
    c: Perpendicular(g6,g4)
    c: Distance(g5,g3) = 25
    c: Coincident(g3,g2)
    c: Coincident(g7,g4)
    c: PointOnObject(g7,g5)
    c: PointOnObject(g5,g9)
    c: Tangent(g9,g8) = 1.5708
    c: Perpendicular(g5,g9)
    c: Tangent(g10,g9) = 1.5708
    c: Tangent(g10,g2) = 1.5708
    c: Equal(g10,g8)
    c: Diameter(g10) = 2
    c: Tangent(g8,g7) = 1.5708
    c: PointOnObject(g11,g9)
    c: PointOnObject(g11,g2)
    c: Distance(g11,g5) = 25
    c: DistanceY(g0,g0) = 23.2014
    c: Distance(g6) = 6.97298
FEATURE [PartDesign::Pad] Pad026
  Direction = (0,0,1)
  Length = 3
  Length2 = 10
  Profile = -> Sketch101
  ReferenceAxis = -> Sketch101 [N_Axis]
  Type = 0
FEATURE [PartDesign::Pocket] Pocket058
  BaseFeature = -> Pad026
  Direction = (-4e-16,0,-1)
  Length = 5
  Length2 = 5
  Midplane = true
  Profile = -> Binder039
  Type = 1
FEATURE [PartDesign::Mirrored] Mirrored037
  BaseFeature = -> Pocket058
  MirrorPlane = -> Sketch101 [V_Axis]
  Originals = -> [Pad026,Pocket058]
  Refine = true
FEATURE [PartDesign::SubShapeBinder] Binder040
  BindCopyOnChange = 0
  BindMode = 0
  ClaimChildren = false
  Context = -> tech_sector [Body_6.Binder040.]
  Fuse = false
  MakeFace = true
  OffsetFill = false
  OffsetIntersection = false
  OffsetJoinType = 0
  OffsetOpenResult = false
  PartialLoad = false
  Placement = pos=(0,197.848,0) rot=(0,0,1;3.14159rad)
  Relative = true
  Support = -> [tech_mid[Pocket076.Sketch123.]]
  _Version = 2
  expr: .Placement.Base.y = Sketch101.Constraints.r
FEATURE [PartDesign::Pocket] Pocket078
  BaseFeature = -> Mirrored037
  Direction = (0,0,-1)
  Length = 5
  Length2 = 5
  Midplane = true
  Profile = -> Binder040
  Type = 1
FEATURE [PartDesign::Body] Body_6  label="plexiglass_holder_bottom_tech"
  Group = -> [LCS_0004,Sketch101,Pad026,Pocket058,Mirrored037,Binder039,Binder040,Pocket078]
  Origin = -> Origin034
  Tip = -> Pocket078
FEATURE [Sketcher::SketchObject] Sketch125
  AttachmentOffset = pos=(0,25,0) rot=(0,0,1;0rad)
  FullyConstrained = true
  MapMode = 5
  Placement = pos=(0,-5.6e-15,25) rot=(1,0,0;1.5708rad)
  Support = -> [XZ_Plane001]
  sketch-geometry (1):
    g0: Circle CenterX=0 CenterY=0 CenterZ=0 NormalX=0 NormalY=0 NormalZ=1 AngleXU=0 Radius=7
  constraints (2):
    c: Coincident(g0,g-1)
    c: Diameter(g0) = 14
FEATURE [Sketcher::SketchObject] Sketch126
  FullyConstrained = true
  MapMode = 5
  Support = -> [XY_Plane038]
  sketch-geometry (3):
    g0: LineSegment StartX=12.5 StartY=25 StartZ=0 EndX=12.5 EndY=17.5 EndZ=0
    g1: LineSegment StartX=12.5 StartY=25 StartZ=0 EndX=5 EndY=25 EndZ=0
    g2: ArcOfCircle CenterX=5 CenterY=17.5 CenterZ=0 NormalX=0 NormalY=0 NormalZ=1 AngleXU=0 Radius=7.5 StartAngle=0 EndAngle=1.5708
  constraints (8):
    c: Vertical(g0)
    c: DistanceX(g0) = 12.5
    c: DistanceY(g0) = 25
    c: Coincident(g1,g0)
    c: Horizontal(g1)
    c: Tangent(g2,g0) = 1.5708
    c: Tangent(g2,g1) = -1.5708
    c: Diameter(g2) = 15
FEATURE [PartDesign::Pocket] Pocket080
  BaseFeature = -> Pocket071
  Direction = (0,0,-1)
  Length = 5
  Length2 = 5
  Midplane = true
  Profile = -> Sketch126
  ReferenceAxis = -> Sketch126 [N_Axis]
  Type = 1
FEATURE [Sketcher::SketchObject] Sketch127
  FullyConstrained = true
  MapMode = 5
  Placement = pos=(0,0,0) rot=(0.57735,0.57735,0.57735;2.0944rad)
  Support = -> [YZ_Plane037]
  sketch-geometry (4):
    g0: LineSegment StartX=71.78 StartY=114.36 StartZ=0 EndX=143.27 EndY=114.36 EndZ=0
    g1: LineSegment StartX=143.27 StartY=114.36 StartZ=0 EndX=143.27 EndY=159.55 EndZ=0
    g2: LineSegment StartX=143.27 StartY=159.55 StartZ=0 EndX=71.78 EndY=159.55 EndZ=0
    g3: LineSegment StartX=71.78 StartY=159.55 StartZ=0 EndX=71.78 EndY=114.36 EndZ=0
  constraints (12):
    c: Coincident(g0,g1)
    c: Coincident(g1,g2)
    c: Coincident(g2,g3)
    c: Coincident(g3,g0)
    c: Horizontal(g0)
    c: Horizontal(g2)
    c: Vertical(g1)
    c: Vertical(g3)
    c: DistanceX(g0) = 71.78  'offset_x'
    c: DistanceY(g0) = 114.36  'offset_y'
    c: DistanceY(g3,g3) = 45.19  'height'
    c: DistanceX(g0,g0) = 71.49  'width'
FEATURE [Sketcher::SketchObject] Sketch128
  FullyConstrained = true
  MapMode = 5
  Placement = pos=(0,0,0) rot=(0.57735,0.57735,0.57735;2.0944rad)
  Support = -> [YZ_Plane001]
  expr: Constraints[5] = <<main>>.basin_height
  sketch-geometry (5):
    g0: LineSegment StartX=73 StartY=116.5 StartZ=0 EndX=166 EndY=116.5 EndZ=0
    g1: LineSegment StartX=166 StartY=116.5 StartZ=0 EndX=166 EndY=157 EndZ=0
    g2: LineSegment StartX=166 StartY=157 StartZ=0 EndX=73 EndY=157 EndZ=0
    g3: LineSegment StartX=73 StartY=157 StartZ=0 EndX=73 EndY=116.5 EndZ=0
    g4: GeomPoint X=119.5 Y=157 Z=0
  constraints (15):
    c: Coincident(g0,g1)
    c: Coincident(g1,g2)
    c: Coincident(g2,g3)
    c: Coincident(g3,g0)
    c: DistanceX(g0) = 73  'offset_x'
    c: DistanceY(g2) = 157
    c: Distance(g3) = 40.5  'height'
    c: Distance(g0) = 93  'length'
    c: Parallel(g1,g3)
    c: Parallel(g0,g2)
    c: Perpendicular(g0,g3)
    c: Angle(g-1,g0) = 0
    c: Symmetric(g2,g1,g4)
    c: DistanceX(g4) = 119.5  'top_center_x'
    c: DistanceY(g4) = 157  'top_center_y'
FEATURE [PartDesign::Pocket] Pocket081
  BaseFeature = -> BaseBend001
  Direction = (-1,2e-16,-3e-16)
  Length = 5
  Length2 = 5
  Midplane = true
  Profile = -> Sketch128
  ReferenceAxis = -> Sketch128 [N_Axis]
  Type = 1
FEATURE [PartDesign::PolarPattern] PolarPattern016
  Angle = 360
  Axis = -> Z_Axis001
  BaseFeature = -> Pocket081
  Occurrences = 3
  Originals = -> [Pocket081]
FEATURE [PartDesign::FeaturePython] Bend  # WARN: FeaturePython — macro-defined, semantics opaque (R4)
  AutoMiter = true
  BaseFeature = -> PolarPattern016
  BendType = 0
  LengthList = [40]
  LengthSpec = 2
  ReliefFactor = 0.7
  UseReliefFactor = false
  angle = 90
  baseObject = -> PolarPattern016 [Edge67,Edge25,Edge211,Edge168,Edge96,Edge140]
  bendAList = [90]
  extend1 = 0
  extend2 = 0
  gap1 = 0.1
  gap2 = 0.1
  invert = false
  kfactor = 0.5
  length = 40
  maxExtendDist = 5
  minGap = 0.1
  minReliefGap = 1
  miterangle1 = 0
  miterangle2 = 0
  offset = 0
  radius = 0.1
  reliefType = 0
  reliefd = 1
  reliefw = 0.8
  sketchflip = false
  sketchinvert = false
  unfold = false
  expr: angle = 90deg - <<main>>.cover_bend_mid
FEATURE [PartDesign::Pocket] Pocket007
  BaseFeature = -> Bend
  Direction = (-1,2e-16,-3e-16)
  Length = 13.01
  Length2 = 5
  Profile = -> Sketch012
  ReferenceAxis = -> Sketch012 [N_Axis]
  Reversed = true
  Type = 0
  expr: Length = <<main>>.end_face_width / 2 - <<main>>.thickness + <<main>>.bend_r
FEATURE [Sketcher::SketchObject] Sketch129
  AttachmentOffset = pos=(0,0,0) rot=(0,1,0;3.66519rad)
  FullyConstrained = true
  MapMode = 5
  Placement = pos=(0,0,0) rot=(-0.186157,0.694747,0.694747;3.50969rad)
  Support = -> [XZ_Plane001]
  expr: .Constraints.height = Sketch128.Constraints.height
  expr: .Constraints.length = Sketch128.Constraints.length
  expr: Constraints[20] = <<main>>.cover_plane_bend
  expr: Constraints[24] = Sketch128.Constraints.top_center_x
  expr: Constraints[25] = Sketch128.Constraints.top_center_y
  expr: Constraints[8] = <<main>>.basin_height
  sketch-geometry (10):
    g0: LineSegment StartX=0 StartY=0 StartZ=0 EndX=169.18 EndY=0 EndZ=0
    g1: LineSegment StartX=169.18 StartY=0 StartZ=0 EndX=169.18 EndY=157 EndZ=0
    g2: LineSegment StartX=0 StartY=157 StartZ=0 EndX=0 EndY=0 EndZ=0
    g3: LineSegment StartX=73 StartY=116.5 StartZ=0 EndX=166 EndY=116.5 EndZ=0
    g4: LineSegment StartX=166 StartY=116.5 StartZ=0 EndX=166 EndY=157 EndZ=0
    g5: LineSegment StartX=166 StartY=157 StartZ=0 EndX=73 EndY=157 EndZ=0
    g6: LineSegment StartX=73 StartY=157 StartZ=0 EndX=73 EndY=116.5 EndZ=0
    g7: LineSegment StartX=169.18 StartY=157 StartZ=0 EndX=166 EndY=157 EndZ=0
    g8: LineSegment StartX=73 StartY=157 StartZ=0 EndX=0 EndY=157 EndZ=0
    g9: GeomPoint X=119.5 Y=157 Z=0
  constraints (26):
    c: Coincident(g0,g1)
    c: Coincident(g1,g7)
    c: Coincident(g8,g2)
    c: Coincident(g2,g0)
    c: Horizontal(g0)
    c: Vertical(g1)
    c: Vertical(g2)
    c: Coincident(g0,g-1)
    c: DistanceY(g8) = 157
    c: Coincident(g3,g4)
    c: Coincident(g4,g5)
    c: Coincident(g5,g6)
    c: Coincident(g6,g3)
    c: Horizontal(g7)
    c: Coincident(g8,g5)
    c: Coincident(g7,g4)
    c: Perpendicular(g4,g3)
    c: Perpendicular(g5,g4)
    c: Perpendicular(g5,g6)
    c: Distance(g3,g1) = 3.18
    c: Angle(g-1,g5) = 0
    c: Distance(g6) = 40.5  'height'
    c: Distance(g3) = 93  'length'
    c: Symmetric(g6,g4,g9)
    c: DistanceX(g9) = 119.5
    c: DistanceY(g9) = 157
FEATURE [PartDesign::CoordinateSystem] Local_CS041
  AttacherType = Attacher::AttachEngine3D
  AttachmentOffset = pos=(119.5,157,16) rot=(0,-0.707107,-0.707107;3.14159rad)
  MapMode = 5
  Placement = pos=(16,119.5,157) rot=(0,0,-1;1.5708rad)
  Support = -> [YZ_Plane001]
  expr: .AttachmentOffset.Base.x = Sketch128.Constraints.top_center_x
  expr: .AttachmentOffset.Base.y = Sketch128.Constraints.top_center_y
  expr: .AttachmentOffset.Base.z = <<main>>.end_face_width / 2
FEATURE [PartDesign::CoordinateSystem] Local_CS039
  AttacherType = Attacher::AttachEngine3D
  AttachmentOffset = pos=(0,-3,-3) rot=(0,1,0.71;0rad)
  MapMode = 5
  Placement = pos=(13,119.5,154) rot=(0,0,-1;1.5708rad)
  Support = -> [Local_CS041]
  expr: .AttachmentOffset.Base.y = -<<main>>.thickness
  expr: .AttachmentOffset.Base.z = -<<main>>.thickness
FEATURE [Sketcher::SketchObject] Sketch073
  FullyConstrained = true
  MapMode = 5
  Placement = pos=(13,119.5,154) rot=(0,0,-1;1.5708rad)
  Support = -> [Local_CS039]
  expr: Constraints[0] = <<main>>.rivet_d
  sketch-geometry (2):
    g0: Circle CenterX=36 CenterY=14.5 CenterZ=0 NormalX=0 NormalY=0 NormalZ=1 AngleXU=0 Radius=1.7
    g1: Circle CenterX=-36 CenterY=14.5 CenterZ=0 NormalX=0 NormalY=0 NormalZ=1 AngleXU=0 Radius=1.7
  constraints (5):
    c: Diameter(g0) = 3.4
    c: DistanceY(g0) = 14.5
    c: Equal(g0,g1)
    c: Symmetric(g1,g0,g-2)
    c: DistanceX(g1,g0) = 72
FEATURE [PartDesign::PolarPattern] PolarPattern009
  Angle = 95
  Axis = -> Sketch073 [H_Axis]
  Occurrences = 2
FEATURE [Sketcher::SketchObject] Sketch130
  AttachmentOffset = pos=(0,40.5,0) rot=(0,0,1;0rad)
  FullyConstrained = true
  MapMode = 5
  Placement = pos=(56.5,119.5,157) rot=(0,0,-1;1.5708rad)
  Support = -> [Local_CS041]
  expr: .AttachmentOffset.Base.y = Bend.length + 0.5mm
  expr: Constraints[14] = Sketch128.Constraints.length
  sketch-geometry (6):
    g0: ArcOfCircle CenterX=36.5 CenterY=-10 CenterZ=0 NormalX=0 NormalY=0 NormalZ=1 AngleXU=0 Radius=10 StartAngle=6.28318 EndAngle=7.85398
    g1: ArcOfCircle CenterX=-36.5 CenterY=-10 CenterZ=0 NormalX=0 NormalY=0 NormalZ=1 AngleXU=0 Radius=10 StartAngle=1.5708 EndAngle=3.14159
    g2: LineSegment StartX=-46.5 StartY=-10 StartZ=0 EndX=-46.5 EndY=0 EndZ=0
    g3: LineSegment StartX=-36.5 StartY=0 StartZ=0 EndX=-46.5 EndY=0 EndZ=0
    g4: LineSegment StartX=46.5 StartY=-10 StartZ=0 EndX=46.5 EndY=0 EndZ=0
    g5: LineSegment StartX=36.5 StartY=0 StartZ=0 EndX=46.5 EndY=0 EndZ=0
  constraints (17):
    c: PointOnObject(g0,g-1)
    c: PointOnObject(g1,g-1)
    c: Coincident(g2,g1)
    c: PointOnObject(g2,g-1)
    c: Vertical(g2)
    c: Tangent(g2,g1)
    c: Coincident(g3,g2)
    c: Coincident(g4,g0)
    c: PointOnObject(g4,g-1)
    c: Vertical(g4)
    c: Tangent(g4,g0)
    c: Coincident(g5,g4)
    c: Tangent(g5,g0) = 1.5708
    c: Tangent(g3,g1) = -1.5708
    c: DistanceX(g2,g4) = 93
    c: Symmetric(g1,g0,g-2)
    c: Diameter(g0) = 20
FEATURE [PartDesign::Mirrored] Mirrored040
  MirrorPlane = -> YZ_Plane001
FEATURE [PartDesign::PolarPattern] PolarPattern017
  Angle = 360
  Axis = -> Z_Axis001
  Occurrences = 3
FEATURE [PartDesign::CoordinateSystem] Local_CS042
  AttacherType = Attacher::AttachEngine3D
  AttachmentOffset = pos=(0,0,0) rot=(0,0,1;2.0944rad)
  MapMode = 5
  Placement = pos=(0,0,0) rot=(0,0,1;2.0944rad)
  Support = -> [XY_Plane001]
FEATURE [Sketcher::SketchObject] Sketch009
  AttachmentOffset = pos=(0,-18.4752,0) rot=(0.935113,-0.250563,-0.250563;1.63783rad)
  ExternalGeometry = -> [Sketch128]
  FullyConstrained = true
  MapMode = 5
  Placement = pos=(16,9.2376,0) rot=(0.57735,0.57735,0.57735;2.0944rad)
  Support = -> [Local_CS042]
  expr: .AttachmentOffset.Base.y = -<<main>>.end_face_width / 2 / cos(30)
  expr: Constraints[7] = <<main>>.basin_height
  sketch-geometry (18):
    g0: LineSegment StartX=0 StartY=0 StartZ=0 EndX=0 EndY=157 EndZ=0
    g1: LineSegment StartX=184 StartY=152 StartZ=0 EndX=184 EndY=127 EndZ=0
    g2: LineSegment StartX=179 StartY=122 StartZ=0 EndX=174.888 EndY=122 EndZ=0
    g3: LineSegment StartX=170.042 StartY=118.231 StartZ=0 EndX=140 EndY=0 EndZ=0
    g4: LineSegment StartX=140 StartY=0 StartZ=0 EndX=0 EndY=0 EndZ=0
    g5: ArcOfCircle CenterX=179 CenterY=152 CenterZ=0 NormalX=0 NormalY=0 NormalZ=1 AngleXU=0 Radius=5 StartAngle=-1.8e-15 EndAngle=1.5708
    g6: GeomPoint X=184 Y=157 Z=0
    g7: ArcOfCircle CenterX=179 CenterY=127 CenterZ=0 NormalX=0 NormalY=0 NormalZ=1 AngleXU=0 Radius=5 StartAngle=4.71239 EndAngle=6.28319
    g8: GeomPoint X=184 Y=122 Z=0
    g9: ArcOfCircle CenterX=174.888 CenterY=117 CenterZ=0 NormalX=0 NormalY=0 NormalZ=1 AngleXU=0 Radius=5 StartAngle=1.5708 EndAngle=2.89276
    g10: GeomPoint X=171 Y=122 Z=0
    g11: LineSegment StartX=63.7624 StartY=116.5 StartZ=0 EndX=156.762 EndY=116.5 EndZ=0
    g12: LineSegment StartX=156.762 StartY=116.5 StartZ=0 EndX=156.762 EndY=157 EndZ=0
    g13: LineSegment StartX=156.762 StartY=157 StartZ=0 EndX=63.7624 EndY=157 EndZ=0
    g14: LineSegment StartX=63.7624 StartY=157 StartZ=0 EndX=63.7624 EndY=116.5 EndZ=0
    g15: LineSegment StartX=0 StartY=157 StartZ=0 EndX=63.7624 EndY=157 EndZ=0
    g16: LineSegment StartX=156.762 StartY=157 StartZ=0 EndX=179 EndY=157 EndZ=0
    g17: LineSegment StartX=208.395 StartY=149.752 StartZ=0 EndX=184 EndY=149.752 EndZ=0
  constraints (44):
    c: Coincident(g-1,g0)
    c: Vertical(g0)
    c: Vertical(g1)
    c: Horizontal(g2)
    c: PointOnObject(g3,g-1)
    c: Coincident(g3,g4)
    c: Coincident(g4,g0)
    c: DistanceY(g0,g0) = 157
    c: PointOnObject(g6,g1)
    c: Tangent(g1,g5) = 1.5708
    c: PointOnObject(g8,g2)
    c: PointOnObject(g8,g1)
    c: Tangent(g2,g7) = 1.5708
    c: Tangent(g1,g7) = 1.5708
    c: PointOnObject(g10,g3)
    c: PointOnObject(g10,g2)
    c: Tangent(g3,g9) = -1.5708
    c: Tangent(g2,g9) = -1.5708
    c: Equal(g9,g7)
    c: Equal(g7,g5)
    c: Diameter(g7) = 10
    c: Distance(g8,g10) = 13
    c: Coincident(g11,g12)
    c: Coincident(g12,g13)
    c: Coincident(g13,g14)
    c: Coincident(g14,g11)
    c: Coincident(g15,g0)
    c: Coincident(g15,g13)
    c: Coincident(g16,g12)
    c: Horizontal(g16)
    c: Tangent(g16,g5) = 1.5708
    c: PointOnObject(g6,g16)
    c: PointOnObject(g17,g1)
    c: Horizontal(g17)
    c: DistanceX(g17) = 208.395
    c: DistanceY(g17) = 149.752
    c: Coincident(g11,g-3)
    c: DistanceX(g8) = 184
    c: DistanceX(g3) = 140
    c: Coincident(g11,g-4)
    c: Perpendicular(g11,g14)
    c: Perpendicular(g12,g13)
    c: Coincident(g12,g-5)
    c: DistanceY(g8,g14) = 35
FEATURE [PartDesign::CoordinateSystem] Local_CS012
  AttacherType = Attacher::AttachEngine3D
  AttachmentOffset = pos=(16,119.5,157) rot=(0,0,-1;1.5708rad)
  MapMode = 5
  Placement = pos=(-111.49,-45.8936,157) rot=(0,0,1;0.523599rad)
  Support = -> [Local_CS042]
  expr: AttachmentOffset = Local_CS041.Placement
FEATURE [Sketcher::SketchObject] Sketch043
  AttachmentOffset = pos=(0,14,0) rot=(0,0,1;0rad)
  FullyConstrained = true
  MapMode = 5
  Placement = pos=(-118.49,-33.7692,157) rot=(0,0,1;0.523599rad)
  Support = -> [Local_CS012]
  expr: Constraints[0] = <<main>>.rivet_d
  sketch-geometry (1):
    g0: Circle CenterX=0 CenterY=16 CenterZ=0 NormalX=0 NormalY=0 NormalZ=1 AngleXU=0 Radius=1.7
  constraints (3):
    c: Diameter(g0) = 3.4
    c: DistanceY(g0) = 16
    c: PointOnObject(g0,g-2)
FEATURE [PartDesign::Plane] DatumPlane012
  Length = 594.137
  MapMode = 5
  Placement = pos=(-111.49,-45.8936,157) rot=(0,0,1;0.523599rad)
  ResizeMode = 0
  Support = -> [Local_CS012]
  Width = 579.207
FEATURE [PartDesign::SubShapeBinder] Binder041
  BindCopyOnChange = 0
  BindMode = 0
  ClaimChildren = false
  Context = -> Model [Body001003005002.Binder041.]
  Fuse = false
  MakeFace = true
  OffsetFill = false
  OffsetIntersection = false
  OffsetJoinType = 0
  OffsetOpenResult = false
  PartialLoad = false
  Relative = false
  Support = -> [Body001003005003013[Pocket041.Sketch083.]]
  _Version = 2
FEATURE [PartDesign::SubShapeBinder] Binder042
  BindCopyOnChange = 0
  BindMode = 0
  ClaimChildren = false
  Context = -> Model [Body001003005002.Binder042.]
  Fuse = false
  MakeFace = true
  OffsetFill = false
  OffsetIntersection = false
  OffsetJoinType = 0
  OffsetOpenResult = false
  PartialLoad = false
  Relative = false
  Support = -> [Body001003005003013[Pocket042.Sketch084.]]
  _Version = 2
FEATURE [PartDesign::SubShapeBinder] Binder043
  BindCopyOnChange = 0
  BindMode = 0
  ClaimChildren = false
  Context = -> Model [Body001003005002.Binder043.]
  Fuse = false
  MakeFace = true
  OffsetFill = false
  OffsetIntersection = false
  OffsetJoinType = 0
  OffsetOpenResult = false
  PartialLoad = false
  Placement = pos=(88.49,85.7308,0) rot=(0,0,1;0.523599rad)
  Relative = false
  Support = -> [Body001[Sketch043.]]
  _Version = 2
  expr: Placement = Local_CS043.Placement
FEATURE [PartDesign::CoordinateSystem] Local_CS043
  AttacherType = Attacher::AttachEngine3D
  AttachmentOffset = pos=(119.5,30,0) rot=(0,0,1;0rad)
  MapMode = 5
  Placement = pos=(88.49,85.7308,0) rot=(0,0,1;0.523599rad)
  Support = -> [Local_CS016]
  expr: .AttachmentOffset.Base.x = Local_CS012.AttachmentOffset.Base.y
FEATURE [PartDesign::Pocket] Pocket086
  BaseFeature = -> Pad012
  Direction = (0,0,-1)
  Length = 5
  Length2 = 5
  Midplane = true
  Profile = -> Binder043
  Type = 1
FEATURE [PartDesign::Pocket] Pocket087
  BaseFeature = -> MultiTransform
  Direction = (0,0,-1)
  Length = 5
  Length2 = 5
  Midplane = true
  Profile = -> Binder023
  Type = 1
FEATURE [PartDesign::PolarPattern] PolarPattern018
  Angle = 120
  Axis = -> Z_Axis015
  BaseFeature = -> Pocket087
  Occurrences = 2
  Originals = -> [Pocket087]
FEATURE [PartDesign::SubShapeBinder] Binder044
  BindCopyOnChange = 0
  BindMode = 0
  ClaimChildren = false
  Context = -> Body001003005003011 [Binder044.]
  Fuse = false
  MakeFace = true
  OffsetFill = false
  OffsetIntersection = false
  OffsetJoinType = 0
  OffsetOpenResult = false
  PartialLoad = false
  Relative = true
  Support = -> [Body001003005003[Pocket036.Sketch075.]]
  _Version = 2
FEATURE [PartDesign::SubShapeBinder] Binder045
  BindCopyOnChange = 0
  BindMode = 0
  ClaimChildren = false
  Context = -> Body001003005003011 [Binder045.]
  Fuse = false
  MakeFace = true
  OffsetFill = false
  OffsetIntersection = false
  OffsetJoinType = 0
  OffsetOpenResult = false
  PartialLoad = false
  Placement = pos=(0,0,0) rot=(0,0,1;0.785398rad)
  Relative = true
  Support = -> [Body001003005003[Pocket036.Sketch075.]]
  _Version = 2
FEATURE [PartDesign::Pocket] Pocket088
  BaseFeature = -> Pad020
  Direction = (0,0,-1)
  Length = 5
  Length2 = 5
  Midplane = true
  Profile = -> Binder044
  Type = 1
FEATURE [PartDesign::Hole] Hole
  BaseFeature = -> Pocket088
  CustomThreadClearance = 0
  Depth = 25
  DepthType = 0
  Diameter = 15.5
  DrillForDepth = false
  DrillPoint = 1
  DrillPointAngle = 118
  HoleCutCountersinkAngle = 90
  HoleCutCustomValues = false
  HoleCutDepth = 0
  HoleCutDiameter = 6.1
  HoleCutType = 0
  ModelThread = false
  Profile = -> Binder045
  Reversed = true
  Tapered = false
  TaperedAngle = 90
  ThreadClass = 0
  ThreadDepth = 25
  ThreadDepthType = 0
  ThreadDirection = 0
  ThreadFit = 0
  ThreadSize = 0
  ThreadType = 0
  Threaded = false
  UseCustomThreadClearance = false
FEATURE [PartDesign::Body] Body001003005003011  label="basement2"
  Group = -> [Sketch076,Pad020,Binder044,Binder045,Pocket088,Hole]
  Origin = -> Origin024
  Tip = -> Hole
FEATURE [PartDesign::CoordinateSystem] Local_CS044
  AttacherType = Attacher::AttachEngine3D
  AttachmentOffset = pos=(119.5,13,0) rot=(0,0,1;0rad)
  MapMode = 5
  Placement = pos=(96.99,71.0083,0) rot=(0,0,1;0.523599rad)
  Support = -> [Local_CS016]
  expr: .AttachmentOffset.Base.x = Local_CS043.AttachmentOffset.Base.x
  expr: .AttachmentOffset.Base.y = <<main>>.end_face_width / 2 - <<main>>.thickness
FEATURE [PartDesign::SubShapeBinder] Binder046
  BindCopyOnChange = 0
  BindMode = 0
  ClaimChildren = false
  Context = -> Model [Body001003005002.Binder046.]
  Fuse = false
  MakeFace = true
  OffsetFill = false
  OffsetIntersection = false
  OffsetJoinType = 0
  OffsetOpenResult = false
  PartialLoad = false
  Placement = pos=(96.99,71.0083,0) rot=(0,0,1;0.523599rad)
  Relative = false
  Support = -> [Body001[Pocket073.Sketch073.]]
  _Version = 2
  expr: Placement = Local_CS044.Placement
FEATURE [PartDesign::Pocket] Pocket089
  BaseFeature = -> Pocket086
  Direction = (0,0,-1)
  Length = 5
  Length2 = 5
  Midplane = true
  Profile = -> Binder046
  Type = 1
FEATURE [PartDesign::Mirrored] Mirrored014
  BaseFeature = -> Pocket089
  MirrorPlane = -> Sketch047 [V_Axis]
  Originals = -> [Pad012,Pocket086,Pocket089]
  Refine = true
FEATURE [PartDesign::Pocket] Pocket084
  BaseFeature = -> Mirrored014
  Direction = (0,0,-1)
  Length = 5
  Length2 = 5
  Midplane = true
  Profile = -> Binder041
  Type = 1
FEATURE [PartDesign::Pocket] Pocket085
  BaseFeature = -> Pocket084
  Direction = (0,0,-1)
  Length = 5
  Length2 = 5
  Midplane = true
  Profile = -> Binder042
  Type = 1
FEATURE [PartDesign::Body] Body001003005  label="basin_cover"
  Group = -> [Sketch047,Pad012,Pocket086,Pocket089,Mirrored014,Local_CS013,Local_CS016,DatumPlane015,DatumPlane016,Local_CS026,Binder041,Binder042,Pocket084,Pocket085,Binder043,Local_CS043,Local_CS044,Binder046]
  Origin = -> Origin014
  Placement = pos=(0,0,0) rot=(0,0,1;1.0472rad)
  Tip = -> Pocket085
FEATURE [PartDesign::PolarPattern] PolarPattern019
  Angle = 360
  Axis = -> Z_Axis001
  Occurrences = 3
FEATURE [Part::FeaturePython] Circular_Body001003005003015001  # Draft array (typed FeaturePython)
  ArrayType = Circular Array
  Axis = -> Z_Axis012
  AxisXYZ = 0
  Count = 3
  ElementPlacement = pos=(0,0,0) rot=(0,0,1;2.0944rad)
  Index = 1
  IntervalAngle = 120
  PlacementList = 3 placements: [(-16.5,192.7,61.7),(-158.633,-110.639,61.7),(175.133,-82.0606,61.7)]
  ScaleList = (3) [(1,1,1),(1,1,1),(1,1,1)]
  ShowElement = false
  SourceObject = -> Body001003005003015001
  expr: .ElementPlacement.Rotation.Angle = IntervalAngle * Index
  expr: IntervalAngle = 360 / Count
FEATURE [Sketcher::SketchObject] Sketch131
  FullyConstrained = true
  MapMode = 5
  Support = -> [XY_Plane042]
  sketch-geometry (5):
    g0: LineSegment StartX=-20 StartY=20 StartZ=0 EndX=-20 EndY=0 EndZ=0
    g1: LineSegment StartX=-20 StartY=0 StartZ=0 EndX=20 EndY=0 EndZ=0
    g2: LineSegment StartX=20 StartY=0 StartZ=0 EndX=20 EndY=20 EndZ=0
    g3: LineSegment StartX=20 StartY=20 StartZ=0 EndX=-20 EndY=20 EndZ=0
    g4: GeomPoint X=0 Y=10 Z=0
  constraints (13):
    c: Coincident(g0,g1)
    c: Coincident(g1,g2)
    c: Coincident(g2,g3)
    c: Coincident(g3,g0)
    c: Horizontal(g1)
    c: Horizontal(g3)
    c: Vertical(g0)
    c: Vertical(g2)
    c: Symmetric(g1,g0,g4)
    c: PointOnObject(g4,g-2)
    c: PointOnObject(g1,g-1)
    c: DistanceX(g1,g1) = 40
    c: DistanceY(g2) = 20
FEATURE [PartDesign::Pad] Pad029
  Direction = (0,0,1)
  Length = 1.5
  Length2 = 10
  Profile = -> Sketch131
  ReferenceAxis = -> Sketch131 [N_Axis]
  Type = 0
FEATURE [PartDesign::Body] Body001003005003015005
  Group = -> [Sketch131,Pad029]
  Origin = -> Origin041
  Tip = -> Pad029
FEATURE [Part::FeaturePython] Array004  # Draft array (typed FeaturePython)
  AlwaysSyncPlacement = false
  Angle = 360
  ArrayType = 0
  Axis = (0,0,1)
  Base = -> Body001003005003015005
  Center = (0,0,0)
  Count = 2
  ExpandArray = false
  Fuse = false
  IntervalAxis = (0,0,0)
  IntervalX = (70,0,0)
  IntervalY = (0,100,0)
  IntervalZ = (0,0,100)
  NumberCircles = 3
  NumberPolar = 5
  NumberX = 2
  NumberY = 1
  NumberZ = 1
  Placement = pos=(293,0,0) rot=(0,0,1;0rad)
  PlacementList = 2 placements: [(0,0,0),(70,0,0)]
  RadialDistance = 50
  ScaleList = (2) [(1,1,1),(1,1,1)]
  Symmetry = 1
  TangentialDistance = 25
FEATURE [Part::FeaturePython] Array005  # Draft array (typed FeaturePython)
  AlwaysSyncPlacement = false
  Angle = 360
  ArrayType = 0
  Axis = (0,0,1)
  Base = -> Body001003005003015005
  Center = (0,0,0)
  Count = 2
  ExpandArray = false
  Fuse = false
  IntervalAxis = (0,0,0)
  IntervalX = (60,0,0)
  IntervalY = (0,100,0)
  IntervalZ = (0,0,100)
  NumberCircles = 3
  NumberPolar = 5
  NumberX = 2
  NumberY = 1
  NumberZ = 1
  Placement = pos=(70,0,0) rot=(0,0,1;0rad)
  PlacementList = 2 placements: [(0,0,0),(60,0,0)]
  RadialDistance = 50
  ScaleList = (2) [(1,1,1),(1,1,1)]
  Symmetry = 1
  TangentialDistance = 25
FEATURE [Part::FeaturePython] Array006  # Draft array (typed FeaturePython)
  AlwaysSyncPlacement = false
  Angle = 360
  ArrayType = 0
  Axis = (0,0,1)
  Base = -> Array004
  Center = (0,0,0)
  Count = 3
  ExpandArray = false
  Fuse = false
  IntervalAxis = (0,0,0)
  IntervalX = (428.17,0,0)
  IntervalY = (0,100,0)
  IntervalZ = (0,0,100)
  NumberCircles = 3
  NumberPolar = 5
  NumberX = 3
  NumberY = 1
  NumberZ = 1
  PlacementList = 3 placements: arithmetic series from (293,0,0) step (428.17,0,0) to (1149.34,0,0)
  RadialDistance = 50
  ScaleList = (3) [(1,1,1),(1,1,1),(1,1,1)]
  Symmetry = 1
  TangentialDistance = 25
FEATURE [Part::FeaturePython] Array007  # Draft array (typed FeaturePython)
  AlwaysSyncPlacement = false
  Angle = 360
  ArrayType = 0
  Axis = (0,0,1)
  Base = -> Array005
  Center = (0,0,0)
  Count = 3
  ExpandArray = false
  Fuse = false
  IntervalAxis = (0,0,0)
  IntervalX = (428.17,0,0)
  IntervalY = (0,100,0)
  IntervalZ = (0,0,100)
  NumberCircles = 3
  NumberPolar = 5
  NumberX = 3
  NumberY = 1
  NumberZ = 1
  PlacementList = 3 placements: arithmetic series from (70,0,0) step (428.17,0,0) to (926.34,0,0)
  RadialDistance = 50
  ScaleList = (3) [(1,1,1),(1,1,1),(1,1,1)]
  Symmetry = 1
  TangentialDistance = 25
FEATURE [Sketcher::SketchObject] Sketch132
  FullyConstrained = true
  MapMode = 5
  Support = -> [XY_Plane016]
  expr: Constraints[1] = Sketch048.Constraints[1]
  sketch-geometry (3):
    g0: Circle CenterX=0 CenterY=0 CenterZ=0 NormalX=0 NormalY=0 NormalZ=1 AngleXU=0 Radius=212.348
    g1: Circle CenterX=0 CenterY=0 CenterZ=0 NormalX=0 NormalY=0 NormalZ=1 AngleXU=0 Radius=202.348
    g2: LineSegment StartX=202.348 StartY=0 StartZ=0 EndX=212.348 EndY=0 EndZ=0
  constraints (8):
    c: Coincident(g0,g-1)
    c: Radius(g0) = 212.348
    c: Coincident(g1,g0)
    c: PointOnObject(g2,g1)
    c: PointOnObject(g2,g0)
    c: Horizontal(g2)
    c: PointOnObject(g0,g2)
    c: DistanceX(g2,g2) = 10
FEATURE [PartDesign::Pad] Pad030
  BaseFeature = -> PolarPattern018
  Direction = (0,0,1)
  Length = 3
  Length2 = 10
  Profile = -> Sketch132
  ReferenceAxis = -> Sketch132 [N_Axis]
  Type = 0
  expr: Length = Pad013.Length
FEATURE [PartDesign::Body] Body001003005003  label="basement"
  Group = -> [Sketch048,Pad013,Sketch049,Binder004,DatumPlane017,Sketch050,Local_CS017,Sketch051,Binder005,DatumPlane018,Sketch057,Sketch058,Pocket027,Local_CS021,Local_CS022,DatumPlane019,DatumPlane020,Sketch061,Sketch062,Sketch063,Sketch064,Sketch075,Pocket036,Binder018,Binder023,Binder036,Pocket074,MultiTransform,Mirrored,PolarPattern015,Sketch120,Pocket087,PolarPattern018,Sketch132,Pad030]
  Origin = -> Origin015
  Tip = -> Pad030
FEATURE [Sketcher::SketchObject] Sketch133
  FullyConstrained = true
  MapMode = 5
  Placement = pos=(0,0,0) rot=(1,0,0;1.5708rad)
  Support = -> [XZ_Plane037]
  expr: Constraints[2] = Sketch116.Constraints.height
  expr: Constraints[7] = <<main>>.rivet_d
  sketch-geometry (4):
    g0: Circle CenterX=0 CenterY=41 CenterZ=0 NormalX=0 NormalY=0 NormalZ=1 AngleXU=0 Radius=1.7
    g1: Circle CenterX=0 CenterY=113 CenterZ=0 NormalX=0 NormalY=0 NormalZ=1 AngleXU=0 Radius=1.7
    g2: GeomPoint X=0 Y=77 Z=0
    g3: GeomPoint X=0 Y=154 Z=0
  constraints (8):
    c: PointOnObject(g0,g-2)
    c: PointOnObject(g1,g-2)
    c: DistanceY(g3) = 154
    c: Symmetric(g3,g-1,g2)
    c: Symmetric(g0,g1,g2)
    c: DistanceY(g0,g1) = 72
    c: Equal(g0,g1)
    c: Diameter(g0) = 3.4
FEATURE [PartDesign::Pocket] Pocket090
  BaseFeature = -> Pocket080
  Direction = (0,1,2e-16)
  Length = 5
  Length2 = 5
  Midplane = true
  Profile = -> Sketch133
  ReferenceAxis = -> Sketch133 [N_Axis]
  Type = 1
FEATURE [PartDesign::Body] tech_pillar  label="tech_pillar_material_0.50ansi"
  Group = -> [LCS_0006,Sketch116,BaseBend008,Bend015,Bend016,Bend017,Sketch117,Pocket071,Sketch118,Sketch126,Pocket080,Sketch127,Sketch133,Pocket090]
  Origin = -> Origin037
  Tip = -> Pocket090
FEATURE [PartDesign::SubShapeBinder] Binder047
  BindCopyOnChange = 0
  BindMode = 0
  ClaimChildren = false
  Context = -> Body001003005003014 [Binder047.]
  Fuse = false
  MakeFace = true
  OffsetFill = false
  OffsetIntersection = false
  OffsetJoinType = 0
  OffsetOpenResult = false
  PartialLoad = false
  Placement = pos=(104.99,75.6271,1.5) rot=(0,0,1;0.523599rad)
  Relative = false
  Support = -> [Body001[Sketch073.]]
  _Version = 2
  expr: Placement = Local_CS045.Placement
FEATURE [PartDesign::CoordinateSystem] Local_CS045
  AttacherType = Attacher::AttachEngine3D
  AttachmentOffset = pos=(119.5,-3,1.5) rot=(0,0,1;0rad)
  MapMode = 5
  Placement = pos=(104.99,75.6271,1.5) rot=(0,0,1;0.523599rad)
  Support = -> [Local_CS029]
  expr: .AttachmentOffset.Base.x = Local_CS041.Placement.Base.y
FEATURE [PartDesign::Hole] Hole001
  BaseFeature = -> Pocket059
  CustomThreadClearance = 0
  Depth = 25
  DepthType = 0
  Diameter = 6.5
  DrillForDepth = false
  DrillPoint = 1
  DrillPointAngle = 118
  HoleCutCountersinkAngle = 90
  HoleCutCustomValues = false
  HoleCutDepth = 0
  HoleCutDiameter = 6.1
  HoleCutType = 0
  ModelThread = false
  Profile = -> Binder047
  Reversed = true
  Tapered = false
  TaperedAngle = 90
  ThreadClass = 0
  ThreadDepth = 25
  ThreadDepthType = 0
  ThreadDirection = 0
  ThreadFit = 0
  ThreadSize = 0
  ThreadType = 0
  Threaded = false
  UseCustomThreadClearance = false
FEATURE [PartDesign::Mirrored] Mirrored031
  BaseFeature = -> Hole001
  MirrorPlane = -> Sketch047 [V_Axis]
  Originals = -> [Pad022,Pocket045,Pocket059,Hole001]
  Refine = true
FEATURE [PartDesign::Body] Body001003005003014  label="basin_cover_back"
  Group = -> [Pad022,Binder021,Binder020,Pocket045,Pocket059,Hole001,Mirrored031,Local_CS027,Local_CS028,DatumPlane023,Local_CS029,Binder037,Local_CS040,Binder038,Binder047,Local_CS045]
  Origin = -> Origin027
  Tip = -> Mirrored031
FEATURE [Part::Feature] Unfold011  label="Unfold"
  Placement = pos=(0,0,208.372) rot=(0.57735,0.57735,-0.57735;4.18879rad)
  shape: bbox 774 x 1308 x 0.302 mm, 572 faces (baked)
FEATURE [Sketcher::SketchObject] Unfold_Sketch_bends012  label="Bend_main"
  FullyConstrained = false
  sketch-geometry (15):
    g0: LineSegment StartX=-156.851 StartY=-56.5087 StartZ=0 EndX=-156.851 EndY=-149.309 EndZ=0
    g1: LineSegment StartX=-156.851 StartY=-484.676 StartZ=0 EndX=-156.851 EndY=-577.476 EndZ=0
    g2: LineSegment StartX=-263 StartY=-1074.2 StartZ=0 EndX=-724 EndY=-1074.2 EndZ=0
    g3: LineSegment StartX=-156.851 StartY=-912.843 StartZ=0 EndX=-156.851 EndY=-1005.64 EndZ=0
    g4: LineSegment StartX=0 StartY=-870.603 StartZ=0 EndX=-774 EndY=-870.603 EndZ=0
    g5: LineSegment StartX=-774 StartY=-842.066 StartZ=0 EndX=0 EndY=-842.066 EndZ=0
    g6: LineSegment StartX=-156.851 StartY=-707.026 StartZ=0 EndX=-156.851 EndY=-799.826 EndZ=0
    g7: LineSegment StartX=-774 StartY=-642.251 StartZ=0 EndX=-217 EndY=-642.251 EndZ=0
    g8: LineSegment StartX=-774 StartY=-442.436 StartZ=0 EndX=0 EndY=-442.436 EndZ=0
    g9: LineSegment StartX=-774 StartY=-413.899 StartZ=0 EndX=0 EndY=-413.899 EndZ=0
    g10: LineSegment StartX=-156.851 StartY=-278.859 StartZ=0 EndX=-156.851 EndY=-371.659 EndZ=0
    g11: LineSegment StartX=-774 StartY=-214.084 StartZ=0 EndX=-217 EndY=-214.084 EndZ=0
    g12: LineSegment StartX=-774 StartY=-14.2685 StartZ=0 EndX=0 EndY=-14.2685 EndZ=0
    g13: LineSegment StartX=-156.851 StartY=149.309 StartZ=0 EndX=-156.851 EndY=56.5087 EndZ=0
    g14: LineSegment StartX=-774 StartY=14.2685 StartZ=0 EndX=0 EndY=14.2685 EndZ=0
FEATURE [Part::Fuse] Fusion
  Base = -> Array006
  Tool = -> Array007
FEATURE [App::DocumentObjectGroup] Group001  label="Arrays"
  Group = -> [Array,Array001,Array002,Array003]
FEATURE [PartDesign::FeatureBase] BaseFeature001
  BaseFeature = -> Unfold011
  Placement = pos=(0,0,208.372) rot=(0.57735,0.57735,-0.57735;4.18879rad)
  expr: Placement = <<Unfold>>.Placement
FEATURE [PartDesign::Pad] Pad031
  BaseFeature = -> BaseFeature001
  Direction = (-3e-16,5e-16,1)
  Length = 2.7
  Length2 = 10
  Placement = pos=(0,0,208.372) rot=(0.57735,0.57735,-0.57735;4.18879rad)
  Profile = -> BaseFeature001 [Face543]
  Type = 0
FEATURE [PartDesign::Body] Body001003005003015006  label="Unfold_main"
  BaseFeature = -> Unfold011
  Group = -> [BaseFeature001,Pad031]
  Origin = -> Origin042
  Tip = -> Pad031
FEATURE [App::DocumentObjectGroup] Group003  label="main001"
  Group = -> [Unfold_Sketch_bends012,Body001003005003015006,Unfold011]
FEATURE [Part::Feature] Unfold  label="Unfold_tech_mid"
  shape: bbox 10 x 180.2 x 0.3 mm, 9 faces (baked)
FEATURE [Sketcher::SketchObject] Unfold_Sketch_bends  label="bends_tech_mid"
  FullyConstrained = false
  sketch-geometry (2):
    g0: LineSegment StartX=5 StartY=-150.389 StartZ=0 EndX=-5 EndY=-150.389 EndZ=0
    g1: LineSegment StartX=5 StartY=0.20365 StartZ=0 EndX=-5 EndY=0.20365 EndZ=0
FEATURE [App::DocumentObjectGroup] Group004  label="tech_mid"
  Group = -> [Unfold,Unfold_Sketch_bends]
FEATURE [Part::Feature] Unfold012  label="Unfold_tech_pillar"
  shape: bbox 49.94 x 203.3 x 0.302 mm, 36 faces (baked)
FEATURE [Sketcher::SketchObject] Unfold_Sketch_bends013  label="bends_tech_pillar"
  FullyConstrained = false
  sketch-geometry (5):
    g0: LineSegment StartX=12.5 StartY=-153.447 StartZ=0 EndX=-12.5 EndY=-153.447 EndZ=0
    g1: LineSegment StartX=-37.4413 StartY=-2.81566 StartZ=0 EndX=-15.7513 EndY=-2.81566 EndZ=0
    g2: LineSegment StartX=-15.7513 StartY=-150.447 StartZ=0 EndX=-37.4413 EndY=-150.447 EndZ=0
    g3: LineSegment StartX=-12.6257 StartY=-150.321 StartZ=0 EndX=-12.6257 EndY=-2.94133 EndZ=0
    g4: LineSegment StartX=12.5 StartY=0.184336 StartZ=0 EndX=-12.5 EndY=0.184336 EndZ=0
FEATURE [App::DocumentObjectGroup] Group005  label="tech_pillar"
  Group = -> [Unfold012,Unfold_Sketch_bends013]
FEATURE [Part::Feature] Unfold013  label="Unfold_gutter"
  shape: bbox 66.98 x 147 x 0.3 mm, 53 faces (baked)
FEATURE [Sketcher::SketchObject] Unfold_Sketch_bends014  label="bends_gutter"
  FullyConstrained = false
  sketch-geometry (2):
    g0: LineSegment StartX=8.61566 StartY=3 StartZ=0 EndX=8.61566 EndY=150 EndZ=0
    g1: LineSegment StartX=-8.61566 StartY=150 StartZ=0 EndX=-8.61566 EndY=3 EndZ=0
FEATURE [App::DocumentObjectGroup] Group006  label="gutter003"
  Group = -> [Unfold013,Unfold_Sketch_bends014]
FEATURE [Part::Feature] Unfold014
  Placement = pos=(0,0,0) rot=(0.707107,0.707107,0;3.14159rad)
  shape: bbox 208.4 x 155.3 x 0.302 mm, 27 faces (baked)
FEATURE [Sketcher::SketchObject] Unfold_Sketch_bends015  label="Unfold_Sketch_bends"
  FullyConstrained = false
  sketch-geometry (2):
    g0: LineSegment StartX=-54.2 StartY=-41.3157 StartZ=0 EndX=54.2 EndY=-41.3157 EndZ=0
    g1: LineSegment StartX=-54.2 StartY=41.3157 StartZ=0 EndX=54.2 EndY=41.3157 EndZ=0
FEATURE [PartDesign::FeatureBase] BaseFeature002
  BaseFeature = -> Unfold014
  Placement = pos=(0,0,0) rot=(0.707107,0.707107,0;3.14159rad)
  expr: Placement = Unfold014.Placement
FEATURE [PartDesign::Pad] Pad032
  BaseFeature = -> BaseFeature002
  Direction = (0,2e-16,1)
  Length = 2.7
  Length2 = 10
  Placement = pos=(0,0,0) rot=(0.707107,0.707107,0;3.14159rad)
  Profile = -> BaseFeature002 [Face2]
  Type = 0
FEATURE [PartDesign::Body] Body001003005003015007  label="Unfold_top"
  BaseFeature = -> Unfold014
  Group = -> [BaseFeature002,Pad032]
  Origin = -> Origin043
  Tip = -> Pad032
FEATURE [App::DocumentObjectGroup] Group007  label="top"
  Group = -> [Unfold014,Unfold_Sketch_bends015,Body001003005003015007]
FEATURE [App::FeaturePython] SetupSheet  # Path/CAM operation (typed FeaturePython)
  ClearanceHeightExpression = OpStockZMax+SetupSheet.ClearanceHeightOffset
  ClearanceHeightOffset = 5
  CoolantMode = 0
  CoolantModes = None | Flood | Mist
  FinalDepthExpression = -0.1 mm
  HorizRapid = 0
  ProfileDirection = 1
  ProfileSide = 0
  ProfileUseComp = true
  ProfileprocessCircles = true
  ProfileprocessHoles = true
  ProfileprocessPerimeter = true
  SafeHeightExpression = OpStockZMax+SetupSheet.SafeHeightOffset
  SafeHeightOffset = 3
  StartDepthExpression = 3 mm
  StepDownExpression = 4 mm
  VertRapid = 0
FEATURE [Part::FeaturePython] Clone  label="Model-Unfold_gutter"  # Draft clone (typed FeaturePython)
  AttacherType = Attacher::AttachEngine3D
  Fuse = false
  Objects = -> [Unfold013]
  PathResource = Model
  Placement = pos=(1049,775,0) rot=(0,0,1;0rad)
  Scale = (1,1,1)
FEATURE [Part::FeaturePython] Clone001  label="Model-Unfold_gutter001"  # Draft clone (typed FeaturePython)
  AttacherType = Attacher::AttachEngine3D
  Fuse = false
  Objects = -> [Unfold013]
  PathResource = Model
  Placement = pos=(1012,1050,0) rot=(0,0,1;3.14159rad)
  Scale = (1,1,1)
FEATURE [Part::FeaturePython] Clone002  label="Model-Unfold_gutter002"  # Draft clone (typed FeaturePython)
  AttacherType = Attacher::AttachEngine3D
  Fuse = false
  Objects = -> [Unfold013]
  PathResource = Model
  Placement = pos=(1414,591,0) rot=(0,0,1;1.5708rad)
  Scale = (1,1,1)
FEATURE [Part::FeaturePython] Clone004  label="Model-Unfold_tech_mid"  # Draft clone (typed FeaturePython)
  AttacherType = Attacher::AttachEngine3D
  Fuse = false
  Objects = -> [Unfold]
  PathResource = Model
  Placement = pos=(966,700,0) rot=(0,0,-1;1.06465rad)
  Scale = (1,1,1)
FEATURE [Part::FeaturePython] Clone005  label="Model-Unfold_tech_pillar"  # Draft clone (typed FeaturePython)
  AttacherType = Attacher::AttachEngine3D
  Fuse = false
  Objects = -> [Unfold012]
  PathResource = Model
  Placement = pos=(300,700,0) rot=(0,0,1;1.5708rad)
  Scale = (1,1,1)
FEATURE [Part::FeaturePython] Clone006  label="Model-Unfold_tech_pillar001"  # Draft clone (typed FeaturePython)
  AttacherType = Attacher::AttachEngine3D
  Fuse = false
  Objects = -> [Unfold012]
  PathResource = Model
  Placement = pos=(1126,959,0) rot=(0,0,1;0rad)
  Scale = (1,1,1)
FEATURE [Part::FeaturePython] Clone007  label="Model-Unfold_top"  # Draft clone (typed FeaturePython)
  AttacherType = Attacher::AttachEngine3D
  Fuse = false
  Objects = -> [Body001003005003015007]
  PathResource = Model
  Placement = pos=(1399,85,0) rot=(0,0,1;3.97935rad)
  Scale = (1,1,1)
FEATURE [Part::FeaturePython] Clone008  label="Model-Unfold_top001"  # Draft clone (typed FeaturePython)
  AttacherType = Attacher::AttachEngine3D
  Fuse = false
  Objects = -> [Body001003005003015007]
  PathResource = Model
  Placement = pos=(1397,257,0) rot=(0,0,1;3.87463rad)
  Scale = (1,1,1)
FEATURE [Part::FeaturePython] Clone009  label="Model-Unfold_top002"  # Draft clone (typed FeaturePython)
  AttacherType = Attacher::AttachEngine3D
  Fuse = false
  Objects = -> [Body001003005003015007]
  PathResource = Model
  Placement = pos=(1397,428,0) rot=(0,0,1;3.85718rad)
  Scale = (1,1,1)
FEATURE [Part::FeaturePython] Clone010  label="Model-basement"  # Draft clone (typed FeaturePython)
  AttacherType = Attacher::AttachEngine3D
  Fuse = false
  Objects = -> [Body001003005003]
  PathResource = Model
  Placement = pos=(436,930,0) rot=(0,0,1;0rad)
  Scale = (1,1,1)
FEATURE [Part::FeaturePython] Clone011  label="Model-basement2"  # Draft clone (typed FeaturePython)
  AttacherType = Attacher::AttachEngine3D
  Fuse = false
  Objects = -> [Body001003005003011]
  PathResource = Model
  Placement = pos=(1313,800,0) rot=(0,0,1;0rad)
  Scale = (1,1,1)
FEATURE [Part::FeaturePython] Clone012  label="Model-basin_cover"  # Draft clone (typed FeaturePython)
  AttacherType = Attacher::AttachEngine3D
  Fuse = false
  Objects = -> [Body001003005]
  PathResource = Model
  Placement = pos=(210,750,0) rot=(0,0,1;1.16937rad)
  Scale = (1,1,1)
FEATURE [Part::FeaturePython] Clone013  label="Model-basin_cover001"  # Draft clone (typed FeaturePython)
  AttacherType = Attacher::AttachEngine3D
  Fuse = false
  Objects = -> [Body001003005]
  PathResource = Model
  Placement = pos=(805,876,0) rot=(0,0,1;3.66519rad)
  Scale = (1,1,1)
FEATURE [Part::FeaturePython] Clone014  label="Model-basin_cover_back"  # Draft clone (typed FeaturePython)
  AttacherType = Attacher::AttachEngine3D
  Fuse = false
  Objects = -> [Body001003005003014]
  PathResource = Model
  Placement = pos=(826,763,0) rot=(0,0,1;0.523599rad)
  Scale = (1,1,1)
FEATURE [Part::FeaturePython] ToolBit  label="3.175mm Endmill"  # Path/CAM toolbit (typed FeaturePython)
  BitPropertyNames = Chipload | CuttingEdgeHeight | Diameter | Flutes | Length | Material | ShankDiameter | SpindleDirection
  BitShape = <path>
  Chipload = 0
  CuttingEdgeHeight = 30
  Diameter = 3.17
  Flutes = 0
  Length = 10
  Material = 0
  ShankDiameter = 3
  ShapeName = endmill
  SpindleDirection = 0
FEATURE [Path::FeaturePython] __175mm_Endmill  label="3.175mm Endmill001"  # Path/CAM operation (typed FeaturePython)
  HorizFeed = 33.3333
  HorizRapid = 0
  SpindleDir = 0
  SpindleSpeed = 18000
  Tool = -> ToolBit
  ToolNumber = 1
  VertFeed = 8.33333
  VertRapid = 0
  expr: HorizRapid = SetupSheet.HorizRapid
  expr: VertRapid = SetupSheet.VertRapid
FEATURE [App::DocumentObjectGroup] Tools
  Group = -> [__175mm_Endmill]
FEATURE [Part::FeaturePython] Clone016  label="Model-Unfold_main"  # Draft clone (typed FeaturePython)
  AttacherType = Attacher::AttachEngine3D
  Fuse = false
  Objects = -> [Body001003005003015006]
  PathResource = Model
  Placement = pos=(213.937,774,7.67e-13) rot=(0,0,1;1.5708rad)
  Scale = (1,1,1)
FEATURE [Part::FeaturePython] Stock  # WARN: FeaturePython — macro-defined, semantics opaque (R4)
  Height = 3
  Length = 1500
  StockType = CreateBox
  Width = 1500
FEATURE [Part::FeaturePython] Clone017  label="Model-plexiglass_holder_top"  # Draft clone (typed FeaturePython)
  AttacherType = Attacher::AttachEngine3D
  Fuse = false
  Objects = -> [Body001003005003013]
  PathResource = Model
  Placement = pos=(817,805,0) rot=(0,0,1;0.034907rad)
  Scale = (1,1,1)
FEATURE [Part::FeaturePython] Clone018  label="Model-plexiglass_holder_top001"  # Draft clone (typed FeaturePython)
  AttacherType = Attacher::AttachEngine3D
  Fuse = false
  Objects = -> [Body001003005003013]
  PathResource = Model
  Placement = pos=(817,835,0) rot=(0,0,1;0.034907rad)
  Scale = (1,1,1)
FEATURE [Part::FeaturePython] Clone019  label="Model-plexiglass_holder_top002"  # Draft clone (typed FeaturePython)
  AttacherType = Attacher::AttachEngine3D
  Fuse = false
  Objects = -> [Body001003005003013]
  PathResource = Model
  Placement = pos=(1314,791,0) rot=(0,0,1;0rad)
  Scale = (1,1,1)
FEATURE [Part::FeaturePython] Clone020  label="Model-plexiglass_holder_top003"  # Draft clone (typed FeaturePython)
  AttacherType = Attacher::AttachEngine3D
  Fuse = false
  Objects = -> [Body001003005003013]
  PathResource = Model
  Placement = pos=(1314,822,0) rot=(0,0,1;0rad)
  Scale = (1,1,1)
FEATURE [Part::FeaturePython] Clone021  label="Model-plexiglass_holder_bottom_tech"  # Draft clone (typed FeaturePython)
  AttacherType = Attacher::AttachEngine3D
  Fuse = false
  Objects = -> [Body_6]
  PathResource = Model
  Placement = pos=(1314,865,0) rot=(0,0,1;0rad)
  Scale = (1,1,1)
FEATURE [Part::FeaturePython] Clone022  label="Model-plexiglass_holder_tech_top"  # Draft clone (typed FeaturePython)
  AttacherType = Attacher::AttachEngine3D
  Fuse = false
  Objects = -> [Body001003005003004]
  PathResource = Model
  Placement = pos=(388,926,0) rot=(0,0,1;1.6057rad)
  Scale = (1,1,1)
FEATURE [Path::FeaturePython] Profile  # Path/CAM operation (typed FeaturePython)
  Active = true
  AreaParams:
    Tolerance = 1e-07
    FitArcs = True
    Simplify = False
    CleanDistance = 0.0
    Accuracy = 0.01
    Unit = 1.0
    MinArcPoints = 4
    MaxArcPoints = 100
    ClipperScale = 10000000.0
    Fill = 0
    Coplanar = 0
    Reorient = True
    Outline = False
    Explode = False
    OpenMode = 0
    Deflection = 0.01
    SubjectFill = 0
    ClipFill = 0
    Offset = -1.585
    ExtraPass = 0
    Stepover = 0.0
    LastStepover = 0.0
    JoinType = 0
    EndType = 0
    MiterLimit = 2.0
    RoundPrecision = 0.0
    PocketMode = 0
    ToolRadius = 1.0
    PocketExtraOffset = 0.0
    PocketStepover = 0.0
    PocketLastStepover = 0.0
    FromCenter = False
    Angle = 45.0
    AngleShift = 0.0
    Shift = 0.0
    Thicken = False
    SectionCount = -1
    Stepdown = 1.0
    SectionOffset = 0.0
    SectionTolerance = 1e-07
    SectionMode = 2
    Project = False
  Base = -> [Clone016,Clone007,Clone008,Clone009,Clone011,Clone002,Clone021,Clone006,Clone,Clone001,Clone014,Clone013,Clone004,Clone010,Clone005,Clone022,Clone012,Clone018,Clone017,Clone020,Clone019]
  ClearanceHeight = 8
  CoolantMode = 0
  CycleTime = 00:18:13
  Direction = 1
  FinalDepth = -0.1
  HandleMultipleFeatures = 0
  JoinType = 0
  MiterLimit = 0.1
  OffsetExtra = 0
  OpFinalDepth = 3
  OpStartDepth = 7
  OpStockZMax = 3
  OpStockZMin = 0
  OpToolDiameter = 3.17
  PathParams = {'orientation': 1, 'feedrate': 33.333333333333336, 'feedrate_v': 8.333333333333334, 'verbose': True, 'resume_height': 6.0, 'retraction': 8.0, 'return_end': True, 'preamble': False, 'start': Vector (1314.0003638412036, 1012.2421887313131, 8.0)}
  SafeHeight = 6
  Side = 0
  SplitArcs = false
  StartDepth = 3
  StartPoint = (0,0,0)
  StepDown = 4
  ToolController = -> __175mm_Endmill
  UseComp = true
  UseStartPoint = false
  processCircles = true
  processHoles = true
  processPerimeter = false
  expr: ClearanceHeight = OpStockZMax + SetupSheet.ClearanceHeightOffset
  expr: FinalDepth = -0.1mm
  expr: SafeHeight = OpStockZMax + SetupSheet.SafeHeightOffset
  expr: StartDepth = 3mm
  expr: StepDown = 4mm
FEATURE [App::FeaturePython] SetupSheet001  # Path/CAM operation (typed FeaturePython)
  ClearanceHeightExpression = OpStockZMax+SetupSheet001.ClearanceHeightOffset
  ClearanceHeightOffset = 5
  CoolantMode = 0
  CoolantModes = None | Flood | Mist
  DeburrExtraDepth = 0
  DeburrWidth = 2.7
  FinalDepthExpression = 0.6 mm
  HorizRapid = 0
  ProfileDirection = 1
  ProfileprocessCircles = true
  ProfileprocessHoles = true
  ProfileprocessPerimeter = true
  SafeHeightExpression = OpStockZMax+SetupSheet001.SafeHeightOffset
  SafeHeightOffset = 3
  StartDepthExpression = 3 mm
  StepDownExpression = OpToolDiameter
  VertRapid = 0
FEATURE [Part::FeaturePython] Clone023  label="Model-Unfold_main001"  # Draft clone (typed FeaturePython)
  AttacherType = Attacher::AttachEngine3D
  Fuse = false
  Objects = -> [Body001003005003015006]
  PathResource = Model
  Placement = pos=(213.937,774,7.67e-13) rot=(0,0,1;1.5708rad)
  Scale = (1,1,1)
  expr: Placement = <<Model-Unfold_main>>.Placement
FEATURE [Part::FeaturePython] Clone024  label="Model-Unfold_top003"  # Draft clone (typed FeaturePython)
  AttacherType = Attacher::AttachEngine3D
  Fuse = false
  Objects = -> [Body001003005003015007]
  PathResource = Model
  Placement = pos=(1399,85,0) rot=(0,0,1;3.97935rad)
  Scale = (1,1,1)
  expr: Placement = <<Model-Unfold_top>>.Placement
FEATURE [Part::FeaturePython] Clone025  label="Model-Unfold_top004"  # Draft clone (typed FeaturePython)
  AttacherType = Attacher::AttachEngine3D
  Fuse = false
  Objects = -> [Body001003005003015007]
  PathResource = Model
  Placement = pos=(1397,257,0) rot=(0,0,1;3.87463rad)
  Scale = (1,1,1)
  expr: Placement = <<Model-Unfold_top001>>.Placement
FEATURE [Part::FeaturePython] Clone026  label="Model-Unfold_top005"  # Draft clone (typed FeaturePython)
  AttacherType = Attacher::AttachEngine3D
  Fuse = false
  Objects = -> [Body001003005003015007]
  PathResource = Model
  Placement = pos=(1397,428,0) rot=(0,0,1;3.85718rad)
  Scale = (1,1,1)
  expr: Placement = <<Model-Unfold_top002>>.Placement
FEATURE [Part::Part2DObjectPython] Clone2D  label="Model-Bend_main"  # Draft 2D object (typed FeaturePython)
  Fuse = false
  Objects = -> [Unfold_Sketch_bends012]
  PathResource = Model
  Placement = pos=(213.937,774,7.67e-13) rot=(0,0,1;1.5708rad)
  Scale = (1,1,1)
  expr: Placement = <<Model-Unfold_main001>>.Placement
FEATURE [Part::Part2DObjectPython] Clone2D001  label="Model-Unfold_Sketch_bends"  # Draft 2D object (typed FeaturePython)
  Fuse = false
  Objects = -> [Unfold_Sketch_bends015]
  PathResource = Model
  Placement = pos=(1399,85,0) rot=(0,0,1;3.97935rad)
  Scale = (1,1,1)
  expr: Placement = <<Model-Unfold_top003>>.Placement
FEATURE [Part::Part2DObjectPython] Clone2D002  label="Model-Unfold_Sketch_bends001"  # Draft 2D object (typed FeaturePython)
  Fuse = false
  Objects = -> [Unfold_Sketch_bends015]
  PathResource = Model
  Placement = pos=(1397,257,0) rot=(0,0,1;3.87463rad)
  Scale = (1,1,1)
  expr: Placement = <<Model-Unfold_top004>>.Placement
FEATURE [Part::Part2DObjectPython] Clone2D003  label="Model-Unfold_Sketch_bends002"  # Draft 2D object (typed FeaturePython)
  Fuse = false
  Objects = -> [Unfold_Sketch_bends015]
  PathResource = Model
  Placement = pos=(1397,428,0) rot=(0,0,1;3.85718rad)
  Scale = (1,1,1)
  expr: Placement = <<Model-Unfold_top005>>.Placement
FEATURE [Part::Part2DObjectPython] Clone2D004  label="Model-bends_gutter"  # Draft 2D object (typed FeaturePython)
  Fuse = false
  Objects = -> [Unfold_Sketch_bends014]
  PathResource = Model
  Placement = pos=(1049,775,0) rot=(0,0,1;0rad)
  Scale = (1,1,1)
  expr: Placement = <<Model-Unfold_gutter>>.Placement
FEATURE [Part::Part2DObjectPython] Clone2D005  label="Model-bends_gutter001"  # Draft 2D object (typed FeaturePython)
  Fuse = false
  Objects = -> [Unfold_Sketch_bends014]
  PathResource = Model
  Placement = pos=(1012,1050,0) rot=(0,0,1;3.14159rad)
  Scale = (1,1,1)
  expr: Placement = <<Model-Unfold_gutter001>>.Placement
FEATURE [Part::Part2DObjectPython] Clone2D006  label="Model-bends_gutter002"  # Draft 2D object (typed FeaturePython)
  Fuse = false
  Objects = -> [Unfold_Sketch_bends014]
  PathResource = Model
  Placement = pos=(1414,591,0) rot=(0,0,1;1.5708rad)
  Scale = (1,1,1)
  expr: Placement = <<Model-Unfold_gutter002>>.Placement
FEATURE [Part::Part2DObjectPython] Clone2D007  label="Model-bends_tech_mid"  # Draft 2D object (typed FeaturePython)
  Fuse = false
  Objects = -> [Unfold_Sketch_bends]
  PathResource = Model
  Placement = pos=(966,700,0) rot=(0,0,-1;1.06465rad)
  Scale = (1,1,1)
  expr: Placement = <<Model-Unfold_tech_mid>>.Placement
FEATURE [Part::Part2DObjectPython] Clone2D008  label="Model-bends_tech_pillar"  # Draft 2D object (typed FeaturePython)
  Fuse = false
  Objects = -> [Unfold_Sketch_bends013]
  PathResource = Model
  Placement = pos=(300,700,0) rot=(0,0,1;1.5708rad)
  Scale = (1,1,1)
  expr: Placement = <<Model-Unfold_tech_pillar>>.Placement
FEATURE [Part::FeaturePython] ToolBit001  label="NZV6109015"  # Path/CAM toolbit (typed FeaturePython)
  BitPropertyNames = Chipload | CuttingEdgeAngle | CuttingEdgeHeight | Diameter | Flutes | Length | Material | ShankDiameter | TipDiameter
  BitShape = <path>
  Chipload = 0
  CuttingEdgeAngle = 90
  CuttingEdgeHeight = 4
  Diameter = 10
  Flutes = 0
  Length = 50
  Material = 0
  ShankDiameter = 6
  ShapeName = chamfer
  TipDiameter = 1
FEATURE [Path::FeaturePython] NZV6109015  label="NZV6109016"  # Path/CAM operation (typed FeaturePython)
  HorizFeed = 51.6667
  HorizRapid = 0
  SpindleDir = 0
  SpindleSpeed = 18000
  Tool = -> ToolBit001
  ToolNumber = 2
  VertFeed = 16.6667
  VertRapid = 0
  expr: HorizRapid = SetupSheet001.HorizRapid
  expr: VertRapid = SetupSheet001.VertRapid
FEATURE [App::DocumentObjectGroup] Tools001
  Group = -> [NZV6109015]
FEATURE [Part::Part2DObjectPython] Clone2D009  label="Model-bends_tech_pillar001"  # Draft 2D object (typed FeaturePython)
  Fuse = false
  Objects = -> [Unfold_Sketch_bends013]
  PathResource = Model
  Placement = pos=(1126,959,0) rot=(0,0,1;0rad)
  Scale = (1,1,1)
  expr: Placement = <<Model-Unfold_tech_pillar001>>.Placement
FEATURE [Path::FeaturePython] Engrave  # Path/CAM operation (typed FeaturePython)
  Active = true
  ClearanceHeight = 9
  CoolantMode = 0
  CycleTime = 00:07:50
  FinalDepth = 0.6
  OpFinalDepth = -7
  OpStartDepth = 3
  OpStockZMax = 4
  OpStockZMin = -7.674e-13
  OpToolDiameter = 10
  SafeHeight = 7
  StartDepth = 3
  StartVertex = 0
  StepDown = 10
  ToolController = -> NZV6109015
  expr: ClearanceHeight = OpStockZMax + SetupSheet001.ClearanceHeightOffset
  expr: FinalDepth = 0.6mm
  expr: SafeHeight = OpStockZMax + SetupSheet001.SafeHeightOffset
  expr: StartDepth = 3mm
  expr: StepDown = OpToolDiameter
FEATURE [Path::FeaturePython] Deburr  # Path/CAM operation (typed FeaturePython)
  Active = true
  Base = -> [Clone023,Clone024,Clone025,Clone026]
  ClearanceHeight = 9
  CoolantMode = 0
  CycleTime = 00:03:04
  Direction = 0
  EntryPoint = 0
  ExtraDepth = 0
  Join = 0
  OpStockZMax = 4
  OpStockZMin = -7.674e-13
  OpToolDiameter = 10
  SafeHeight = 7
  Side = 0
  StartDepth = 4
  StepDown = 0
  ToolController = -> NZV6109015
  Width = 2.7
  expr: ClearanceHeight = OpStockZMax + SetupSheet001.ClearanceHeightOffset
  expr: SafeHeight = OpStockZMax + SetupSheet001.SafeHeightOffset
  expr: StepDown = 0mm
FEATURE [Part::FeaturePython] Clone027  label="Model-basement003"  # Draft clone (typed FeaturePython)
  AttacherType = Attacher::AttachEngine3D
  Fuse = false
  Objects = -> [Body001003005003]
  PathResource = Model
  Placement = pos=(436,930,0) rot=(0,0,1;0rad)
  Scale = (1,1,1)
  expr: Placement = <<Model-basement>>.Placement
FEATURE [App::DocumentObjectGroup] Model002
  Group = -> [Clone023,Clone024,Clone025,Clone026,Clone2D,Clone2D001,Clone2D002,Clone2D003,Clone2D004,Clone2D005,Clone2D006,Clone2D007,Clone2D008,Clone2D009,Clone027]
FEATURE [Part::FeaturePython] Stock001  # WARN: FeaturePython — macro-defined, semantics opaque (R4)
  Base = -> Model002
  ExtXneg = 1
  ExtXpos = 1
  ExtYneg = 1
  ExtYpos = 1
  ExtZneg = 0
  ExtZpos = 1
  Placement = pos=(-774,-1094.25,-7.67e-13) rot=(0,0,1;0rad)
  StockType = FromBase
FEATURE [Path::FeaturePython] Engrave001  # Path/CAM operation (typed FeaturePython)
  Active = true
  Base = -> [Clone027]
  ClearanceHeight = 9
  CoolantMode = 0
  CycleTime = 00:00:23
  FinalDepth = 2
  OpFinalDepth = -7
  OpStartDepth = 3
  OpStockZMax = 4
  OpStockZMin = -7.67e-13
  OpToolDiameter = 10
  SafeHeight = 7
  StartDepth = 3
  StartVertex = 0
  StepDown = 10
  ToolController = -> NZV6109015
  expr: ClearanceHeight = OpStockZMax + SetupSheet001.ClearanceHeightOffset
  expr: FinalDepth = 2
  expr: SafeHeight = OpStockZMax + SetupSheet001.SafeHeightOffset
  expr: StartDepth = 3mm
  expr: StepDown = OpToolDiameter
FEATURE [App::DocumentObjectGroup] Operations001
  Group = -> [Engrave,Deburr,Engrave001]
FEATURE [Path::FeaturePython] Job001  # Path/CAM operation (typed FeaturePython)
  CycleTime = 00:11:17
  Fixtures = G54
  GeometryTolerance = 0.01
  JobType = 0
  LastPostProcessDate = 2023-02-01 09:50:10.298629
  LastPostProcessOutput = <userpath>/2411-26D9/Job1.tap
  Model = -> Model002
  Operations = -> Operations001
  OrderOutputBy = 0
  PostProcessor = 1
  PostProcessorOutputFile = %d.%j.tap
  SetupSheet = -> SetupSheet001
  SplitOutput = false
  Stock = -> Stock001
  Tools = -> Tools001
FEATURE [App::FeaturePython] SetupSheet002  # Path/CAM operation (typed FeaturePython)
  ClearanceHeightExpression = OpStockZMax+SetupSheet002.ClearanceHeightOffset
  ClearanceHeightOffset = 5
  CoolantMode = 0
  CoolantModes = None | Flood | Mist
  FinalDepthExpression = -0.1 mm
  HorizRapid = 0
  ProfileDirection = 1
  ProfileSide = 0
  ProfileUseComp = true
  ProfileprocessCircles = true
  ProfileprocessHoles = true
  ProfileprocessPerimeter = true
  SafeHeightExpression = OpStockZMax+SetupSheet002.SafeHeightOffset
  SafeHeightOffset = 3
  StartDepthExpression = 3 mm
  StepDownExpression = 4 mm
  VertRapid = 0
FEATURE [Part::FeaturePython] Clone028  label="Model-Model-Unfold_gutter"  # Draft clone (typed FeaturePython)
  AttacherType = Attacher::AttachEngine3D
  Fuse = false
  Objects = -> [Clone]
  PathResource = Model
  Placement = pos=(1049,775,0) rot=(0,0,1;0rad)
  Scale = (1,1,1)
FEATURE [Part::FeaturePython] Clone029  label="Model-Model-Unfold_gutter001"  # Draft clone (typed FeaturePython)
  AttacherType = Attacher::AttachEngine3D
  Fuse = false
  Objects = -> [Clone001]
  PathResource = Model
  Placement = pos=(1012,1050,0) rot=(0,0,1;3.14159rad)
  Scale = (1,1,1)
FEATURE [Part::FeaturePython] Clone030  label="Model-Model-Unfold_gutter002"  # Draft clone (typed FeaturePython)
  AttacherType = Attacher::AttachEngine3D
  Fuse = false
  Objects = -> [Clone002]
  PathResource = Model
  Placement = pos=(1414,591,0) rot=(0,0,1;1.5708rad)
  Scale = (1,1,1)
FEATURE [Part::FeaturePython] Clone031  label="Model-Model-Unfold_tech_mid"  # Draft clone (typed FeaturePython)
  AttacherType = Attacher::AttachEngine3D
  Fuse = false
  Objects = -> [Clone004]
  PathResource = Model
  Placement = pos=(966,700,0) rot=(0,0,-1;1.06465rad)
  Scale = (1,1,1)
FEATURE [Part::FeaturePython] Clone032  label="Model-Model-Unfold_tech_pillar"  # Draft clone (typed FeaturePython)
  AttacherType = Attacher::AttachEngine3D
  Fuse = false
  Objects = -> [Clone005]
  PathResource = Model
  Placement = pos=(300,700,0) rot=(0,0,1;1.5708rad)
  Scale = (1,1,1)
FEATURE [Part::FeaturePython] Clone033  label="Model-Model-Unfold_tech_pillar001"  # Draft clone (typed FeaturePython)
  AttacherType = Attacher::AttachEngine3D
  Fuse = false
  Objects = -> [Clone006]
  PathResource = Model
  Placement = pos=(1126,959,0) rot=(0,0,1;0rad)
  Scale = (1,1,1)
FEATURE [Part::FeaturePython] Clone034  label="Model-Model-Unfold_top"  # Draft clone (typed FeaturePython)
  AttacherType = Attacher::AttachEngine3D
  Fuse = false
  Objects = -> [Clone007]
  PathResource = Model
  Placement = pos=(1399,85,0) rot=(0,0,1;3.97935rad)
  Scale = (1,1,1)
FEATURE [Part::FeaturePython] Clone035  label="Model-Model-Unfold_top001"  # Draft clone (typed FeaturePython)
  AttacherType = Attacher::AttachEngine3D
  Fuse = false
  Objects = -> [Clone008]
  PathResource = Model
  Placement = pos=(1397,257,0) rot=(0,0,1;3.87463rad)
  Scale = (1,1,1)
FEATURE [Part::FeaturePython] Clone036  label="Model-Model-Unfold_top002"  # Draft clone (typed FeaturePython)
  AttacherType = Attacher::AttachEngine3D
  Fuse = false
  Objects = -> [Clone009]
  PathResource = Model
  Placement = pos=(1397,428,0) rot=(0,0,1;3.85718rad)
  Scale = (1,1,1)
FEATURE [Part::FeaturePython] Clone037  label="Model-Model-basement"  # Draft clone (typed FeaturePython)
  AttacherType = Attacher::AttachEngine3D
  Fuse = false
  Objects = -> [Clone010]
  PathResource = Model
  Placement = pos=(436,930,0) rot=(0,0,1;0rad)
  Scale = (1,1,1)
FEATURE [Part::FeaturePython] Clone038  label="Model-Model-basement2"  # Draft clone (typed FeaturePython)
  AttacherType = Attacher::AttachEngine3D
  Fuse = false
  Objects = -> [Clone011]
  PathResource = Model
  Placement = pos=(1313,800,0) rot=(0,0,1;0rad)
  Scale = (1,1,1)
FEATURE [Part::FeaturePython] Clone039  label="Model-Model-basin_cover"  # Draft clone (typed FeaturePython)
  AttacherType = Attacher::AttachEngine3D
  Fuse = false
  Objects = -> [Clone012]
  PathResource = Model
  Placement = pos=(210,750,0) rot=(0,0,1;1.16937rad)
  Scale = (1,1,1)
FEATURE [Part::FeaturePython] Clone040  label="Model-Model-basin_cover001"  # Draft clone (typed FeaturePython)
  AttacherType = Attacher::AttachEngine3D
  Fuse = false
  Objects = -> [Clone013]
  PathResource = Model
  Placement = pos=(805,876,0) rot=(0,0,1;3.66519rad)
  Scale = (1,1,1)
FEATURE [Part::FeaturePython] Clone041  label="Model-Model-basin_cover_back"  # Draft clone (typed FeaturePython)
  AttacherType = Attacher::AttachEngine3D
  Fuse = false
  Objects = -> [Clone014]
  PathResource = Model
  Placement = pos=(826,763,0) rot=(0,0,1;0.523599rad)
  Scale = (1,1,1)
FEATURE [Part::FeaturePython] Clone042  label="Model-Model-Unfold_main"  # Draft clone (typed FeaturePython)
  AttacherType = Attacher::AttachEngine3D
  Fuse = false
  Objects = -> [Clone016]
  PathResource = Model
  Placement = pos=(213.937,774,7.67e-13) rot=(0,0,1;1.5708rad)
  Scale = (1,1,1)
FEATURE [Part::FeaturePython] Clone043  label="Model-Model-plexiglass_holder_top"  # Draft clone (typed FeaturePython)
  AttacherType = Attacher::AttachEngine3D
  Fuse = false
  Objects = -> [Clone017]
  PathResource = Model
  Placement = pos=(817,805,0) rot=(0,0,1;0.034907rad)
  Scale = (1,1,1)
FEATURE [Part::FeaturePython] Clone044  label="Model-Model-plexiglass_holder_top001"  # Draft clone (typed FeaturePython)
  AttacherType = Attacher::AttachEngine3D
  Fuse = false
  Objects = -> [Clone018]
  PathResource = Model
  Placement = pos=(817,835,0) rot=(0,0,1;0.034907rad)
  Scale = (1,1,1)
FEATURE [Part::FeaturePython] Clone045  label="Model-Model-plexiglass_holder_top002"  # Draft clone (typed FeaturePython)
  AttacherType = Attacher::AttachEngine3D
  Fuse = false
  Objects = -> [Clone019]
  PathResource = Model
  Placement = pos=(1314,791,0) rot=(0,0,1;0rad)
  Scale = (1,1,1)
FEATURE [Part::FeaturePython] Clone046  label="Model-Model-plexiglass_holder_top003"  # Draft clone (typed FeaturePython)
  AttacherType = Attacher::AttachEngine3D
  Fuse = false
  Objects = -> [Clone020]
  PathResource = Model
  Placement = pos=(1314,822,0) rot=(0,0,1;0rad)
  Scale = (1,1,1)
FEATURE [Part::FeaturePython] Clone047  label="Model-Model-plexiglass_holder_bottom_tech"  # Draft clone (typed FeaturePython)
  AttacherType = Attacher::AttachEngine3D
  Fuse = false
  Objects = -> [Clone021]
  PathResource = Model
  Placement = pos=(1314,865,0) rot=(0,0,1;0rad)
  Scale = (1,1,1)
FEATURE [Part::FeaturePython] Clone048  label="Model-Model-plexiglass_holder_tech_top"  # Draft clone (typed FeaturePython)
  AttacherType = Attacher::AttachEngine3D
  Fuse = false
  Objects = -> [Clone022]
  PathResource = Model
  Placement = pos=(388,926,0) rot=(0,0,1;1.6057rad)
  Scale = (1,1,1)
FEATURE [App::DocumentObjectGroup] Model003
  Group = -> [Clone028,Clone029,Clone030,Clone031,Clone032,Clone033,Clone034,Clone035,Clone036,Clone037,Clone038,Clone039,Clone040,Clone041,Clone042,Clone043,Clone044,Clone045,Clone046,Clone047,Clone048]
FEATURE [Part::FeaturePython] ToolBit002  label="3.175mm Endmill003"  # Path/CAM toolbit (typed FeaturePython)
  BitPropertyNames = Chipload | CuttingEdgeHeight | Diameter | Flutes | Length | Material | ShankDiameter | SpindleDirection
  BitShape = <path>
  Chipload = 0
  CuttingEdgeHeight = 30
  Diameter = 3.17
  Flutes = 0
  Length = 10
  Material = 0
  ShankDiameter = 3
  ShapeName = endmill
  SpindleDirection = 0
FEATURE [Path::FeaturePython] __175mm_Endmill001  label="3.175mm Endmill002"  # Path/CAM operation (typed FeaturePython)
  HorizFeed = 33.3333
  HorizRapid = 0
  SpindleDir = 0
  SpindleSpeed = 18000
  Tool = -> ToolBit002
  ToolNumber = 1
  VertFeed = 8.33333
  VertRapid = 0
  expr: HorizRapid = SetupSheet002.HorizRapid
  expr: VertRapid = SetupSheet002.VertRapid
FEATURE [App::DocumentObjectGroup] Tools002
  Group = -> [__175mm_Endmill001]
FEATURE [Part::FeaturePython] Stock002  # WARN: FeaturePython — macro-defined, semantics opaque (R4)
  Base = -> Model003
  ExtXneg = 1
  ExtXpos = 1
  ExtYneg = 1
  ExtYpos = 1
  ExtZneg = 0
  ExtZpos = 1
  Placement = pos=(-1.14e-13,0,-3.6e-14) rot=(0,0,1;0rad)
  StockType = FromBase
FEATURE [Path::FeaturePython] Profile001  # Path/CAM operation (typed FeaturePython)
  Active = true
  AreaParams:
    Tolerance = 1e-07
    FitArcs = True
    Simplify = False
    CleanDistance = 0.0
    Accuracy = 0.01
    Unit = 1.0
    MinArcPoints = 4
    MaxArcPoints = 100
    ClipperScale = 10000000.0
    Fill = 0
    Coplanar = 0
    Reorient = True
    Outline = False
    Explode = False
    OpenMode = 0
    Deflection = 0.01
    SubjectFill = 0
    ClipFill = 0
    Offset = 1.585
    ExtraPass = 0
    Stepover = 0.0
    LastStepover = 0.0
    JoinType = 0
    EndType = 0
    MiterLimit = 2.0
    RoundPrecision = 0.0
    PocketMode = 0
    ToolRadius = 1.0
    PocketExtraOffset = 0.0
    PocketStepover = 0.0
    PocketLastStepover = 0.0
    FromCenter = False
    Angle = 45.0
    AngleShift = 0.0
    Shift = 0.0
    Thicken = False
    SectionCount = -1
    Stepdown = 1.0
    SectionOffset = 0.0
    SectionTolerance = 1e-07
    SectionMode = 2
    Project = False
  ClearanceHeight = 9
  CoolantMode = 0
  CycleTime = 00:10:24
  Direction = 1
  FinalDepth = -0.1
  HandleMultipleFeatures = 0
  JoinType = 0
  MiterLimit = 0.1
  OffsetExtra = 0
  OpFinalDepth = -3.6e-14
  OpStartDepth = 4
  OpStockZMax = 4
  OpStockZMin = -3.6e-14
  OpToolDiameter = 3.17
  PathParams = {'orientation': 0, 'feedrate': 33.333333333333336, 'feedrate_v': 8.333333333333334, 'verbose': True, 'resume_height': 7.000000000001101, 'retraction': 9.000000000001101, 'return_end': True, 'preamble': False, 'start': Vector (1462.8455949284446, 925.5437755750755, 9.000000000001101)}
  SafeHeight = 7
  Side = 0
  SplitArcs = false
  StartDepth = 3
  StartPoint = (0,0,0)
  StepDown = 4
  ToolController = -> __175mm_Endmill001
  UseComp = true
  UseStartPoint = false
  processCircles = true
  processHoles = true
  processPerimeter = true
  expr: ClearanceHeight = OpStockZMax + SetupSheet002.ClearanceHeightOffset
  expr: FinalDepth = -0.1mm
  expr: SafeHeight = OpStockZMax + SetupSheet002.SafeHeightOffset
  expr: StartDepth = 3mm
  expr: StepDown = 4mm
FEATURE [App::DocumentObjectGroup] Operations002
  Group = -> [Profile001]
FEATURE [Path::FeaturePython] Job002  # Path/CAM operation (typed FeaturePython)
  CycleTime = 00:10:24
  Fixtures = G54
  GeometryTolerance = 0.01
  JobType = 0
  LastPostProcessDate = 2023-02-01 09:50:30.562625
  LastPostProcessOutput = <userpath>/2411-26D9/Job2.tap
  Model = -> Model003
  Operations = -> Operations002
  OrderOutputBy = 0
  PostProcessor = 1
  PostProcessorOutputFile = %d.%j.tap
  SetupSheet = -> SetupSheet002
  SplitOutput = false
  Stock = -> Stock002
  Tools = -> Tools002
FEATURE [Part::FeaturePython] Clone049  label="Model-Fusion"  # Draft clone (typed FeaturePython)
  AttacherType = Attacher::AttachEngine3D
  Fuse = false
  Objects = -> [Fusion]
  PathResource = Model
  Scale = (1,1,1)
FEATURE [App::DocumentObjectGroup] Model001
  Group = -> [Clone,Clone001,Clone002,Clone004,Clone005,Clone006,Clone007,Clone008,Clone009,Clone010,Clone011,Clone012,Clone013,Clone014,Clone016,Clone017,Clone018,Clone019,Clone020,Clone021,Clone022,Clone049]
FEATURE [Path::FeaturePython] MillFace  # Path/CAM operation (typed FeaturePython)
  Active = true
  AreaParams:
    Tolerance = 1e-07
    FitArcs = True
    Simplify = False
    CleanDistance = 0.0
    Accuracy = 0.01
    Unit = 1.0
    MinArcPoints = 4
    MaxArcPoints = 100
    ClipperScale = 10000000.0
    Fill = 0
    Coplanar = 0
    Reorient = True
    Outline = False
    Explode = False
    OpenMode = 0
    Deflection = 0.01
    SubjectFill = 0
    ClipFill = 0
    Offset = 0.0
    ExtraPass = 0
    Stepover = 0.0
    LastStepover = 0.0
    JoinType = 0
    EndType = 0
    MiterLimit = 2.0
    RoundPrecision = 0.0
    PocketMode = 2
    ToolRadius = 1.585
    PocketExtraOffset = 0.0
    PocketStepover = 1.585
    PocketLastStepover = 0.0
    FromCenter = True
    Angle = 45.0
    AngleShift = 0.0
    Shift = 0.0
    Thicken = False
    SectionCount = -1
    Stepdown = 1.0
    SectionOffset = 0.0
    SectionTolerance = 1e-07
    SectionMode = 2
    Project = False
  Base = -> [Clone049]
  BoundaryShape = 1
  ClearEdges = false
  ClearanceHeight = 8
  CoolantMode = 0
  CutMode = 0
  CycleTime = 00:03:39
  ExcludeRaisedAreas = false
  ExtraOffset = 0
  FinalDepth = 1.5
  FinishDepth = 0
  KeepToolDown = false
  MinTravel = true
  OffsetPattern = 1
  OpFinalDepth = 1.5
  OpStartDepth = 3
  OpStockZMax = 3
  OpStockZMin = 0
  OpToolDiameter = 3.17
  PathParams = {'orientation': 1, 'sort_mode': 3, 'threshold': 3.17, 'feedrate': 33.333333333333336, 'feedrate_v': 8.333333333333334, 'verbose': True, 'resume_height': 6.0, 'retraction': 8.0, 'return_end': True, 'preamble': False, 'start': Vector (0.0, 0.0, 0.0)}
  PocketLastStepOver = 0
  SafeHeight = 6
  SplitArcs = false
  StartAt = 0
  StartDepth = 3
  StartPoint = (0,0,0)
  StepDown = 4
  StepOver = 50
  ToolController = -> __175mm_Endmill
  UseStartPoint = true
  ZigZagAngle = 45
  expr: ClearanceHeight = OpStockZMax + SetupSheet.ClearanceHeightOffset
  expr: FinalDepth = 1.5
  expr: SafeHeight = OpStockZMax + SetupSheet.SafeHeightOffset
  expr: StartDepth = 3mm
  expr: StepDown = 4mm
FEATURE [Path::FeaturePython] Pocket_Shape  # Path/CAM operation (typed FeaturePython)
  Active = true
  AreaParams:
    Tolerance = 1e-07
    FitArcs = True
    Simplify = False
    CleanDistance = 0.0
    Accuracy = 0.01
    Unit = 1.0
    MinArcPoints = 4
    MaxArcPoints = 100
    ClipperScale = 10000000.0
    Fill = 0
    Coplanar = 0
    Reorient = True
    Outline = False
    Explode = False
    OpenMode = 0
    Deflection = 0.01
    SubjectFill = 0
    ClipFill = 0
    Offset = 0.0
    ExtraPass = 0
    Stepover = 0.0
    LastStepover = 0.0
    JoinType = 0
    EndType = 0
    MiterLimit = 2.0
    RoundPrecision = 0.0
    PocketMode = 2
    ToolRadius = 1.585
    PocketExtraOffset = 0.0
    PocketStepover = 3.17
    PocketLastStepover = 0.0
    FromCenter = True
    Angle = 45.0
    AngleShift = 0.0
    Shift = 0.0
    Thicken = False
    SectionCount = -1
    Stepdown = 1.0
    SectionOffset = 0.0
    SectionTolerance = 1e-07
    SectionMode = 2
    Project = False
  Base = -> [Clone014]
  ClearanceHeight = 8
  CoolantMode = 0
  CutMode = 0
  CycleTime = 00:00:46
  ExtensionCorners = true
  ExtensionLengthDefault = 1.585
  ExtraOffset = 0
  FinalDepth = 2
  FinishDepth = 0
  KeepToolDown = false
  MinTravel = true
  OffsetPattern = 1
  OpFinalDepth = 1.5
  OpStartDepth = 3
  OpStockZMax = 3
  OpStockZMin = 0
  OpToolDiameter = 3.17
  PathParams = {'orientation': 1, 'sort_mode': 3, 'threshold': 3.17, 'feedrate': 33.333333333333336, 'feedrate_v': 8.333333333333334, 'verbose': True, 'resume_height': 6.0, 'retraction': 8.0, 'return_end': True, 'preamble': False, 'start': Vector (846.6381325149291, 853.8174396719498, 8.0)}
  PocketLastStepOver = 0
  SafeHeight = 6
  SplitArcs = false
  StartAt = 0
  StartDepth = 3
  StartPoint = (0,0,0)
  StepDown = 4
  StepOver = 100
  ToolController = -> __175mm_Endmill
  UseOutline = false
  UseStartPoint = true
  ZigZagAngle = 45
  expr: ClearanceHeight = OpStockZMax + SetupSheet.ClearanceHeightOffset
  expr: ExtensionLengthDefault = OpToolDiameter / 2
  expr: FinalDepth = 2
  expr: SafeHeight = OpStockZMax + SetupSheet.SafeHeightOffset
  expr: StartDepth = 3mm
  expr: StepDown = 4mm
FEATURE [App::DocumentObjectGroup] Operations
  Group = -> [Profile,MillFace,Pocket_Shape]
FEATURE [Path::FeaturePython] Job  # Path/CAM operation (typed FeaturePython)
  CycleTime = 00:22:38
  Fixtures = G54
  GeometryTolerance = 0.01
  JobType = 0
  LastPostProcessDate = 2023-02-01 09:58:23.222482
  LastPostProcessOutput = <userpath>/2411-26D9/Job.tap
  Model = -> Model001
  Operations = -> Operations
  OrderOutputBy = 0
  PostProcessor = 1
  PostProcessorOutputFile = %d.%j.tap
  SetupSheet = -> SetupSheet
  SplitOutput = false
  Stock = -> Stock
  Tools = -> Tools
FEATURE [Part::Feature] Unfold015
  shape: bbox 66.98 x 147 x 0.3 mm, 60 faces (baked)
FEATURE [Sketcher::SketchObject] Unfold_Sketch_bends016
  FullyConstrained = false
  sketch-geometry (2):
    g0: LineSegment StartX=8.61566 StartY=3 StartZ=0 EndX=8.61566 EndY=150 EndZ=0
    g1: LineSegment StartX=-8.61566 StartY=150 StartZ=0 EndX=-8.61566 EndY=3 EndZ=0
FEATURE [App::FeaturePython] SetupSheet003  # Path/CAM operation (typed FeaturePython)
  ClearanceHeightExpression = OpStockZMax+SetupSheet003.ClearanceHeightOffset
  ClearanceHeightOffset = 5
  CoolantMode = 0
  CoolantModes = None | Flood | Mist
  FinalDepthExpression = -0.1 mm
  HorizRapid = 0
  ProfileDirection = 1
  ProfileSide = 0
  ProfileUseComp = true
  ProfileprocessCircles = true
  ProfileprocessHoles = true
  ProfileprocessPerimeter = true
  SafeHeightExpression = OpStockZMax+SetupSheet003.SafeHeightOffset
  SafeHeightOffset = 3
  StartDepthExpression = 3 mm
  StepDownExpression = 4 mm
  VertRapid = 0
FEATURE [Part::FeaturePython] Clone050  label="Model-Unfold015"  # Draft clone (typed FeaturePython)
  AttacherType = Attacher::AttachEngine3D
  Fuse = false
  Objects = -> [Unfold015]
  PathResource = Model
  Placement = pos=(-3,159,0) rot=(0,0,-1;1.5708rad)
  Scale = (1,1,1)
FEATURE [Part::FeaturePython] ToolBit003  label="3.175mm Endmill005"  # Path/CAM toolbit (typed FeaturePython)
  BitPropertyNames = Chipload | CuttingEdgeHeight | Diameter | Flutes | Length | Material | ShankDiameter | SpindleDirection
  BitShape = <path>
  Chipload = 0
  CuttingEdgeHeight = 30
  Diameter = 3.17
  Flutes = 0
  Length = 10
  Material = 0
  ShankDiameter = 3
  ShapeName = endmill
  SpindleDirection = 0
FEATURE [Path::FeaturePython] __175mm_Endmill002  label="3.175mm Endmill004"  # Path/CAM operation (typed FeaturePython)
  HorizFeed = 33.3333
  HorizRapid = 0
  SpindleDir = 0
  SpindleSpeed = 18000
  Tool = -> ToolBit003
  ToolNumber = 1
  VertFeed = 8.33333
  VertRapid = 0
  expr: HorizRapid = SetupSheet003.HorizRapid
  expr: VertRapid = SetupSheet003.VertRapid
FEATURE [App::DocumentObjectGroup] Tools003
  Group = -> [__175mm_Endmill002]
FEATURE [App::FeaturePython] SetupSheet004  # Path/CAM operation (typed FeaturePython)
  ClearanceHeightExpression = OpStockZMax+SetupSheet004.ClearanceHeightOffset
  ClearanceHeightOffset = 5
  CoolantMode = 0
  CoolantModes = None | Flood | Mist
  DeburrExtraDepth = 0
  DeburrWidth = 2.7
  FinalDepthExpression = 0.6 mm
  HorizRapid = 0
  ProfileDirection = 1
  ProfileprocessCircles = true
  ProfileprocessHoles = true
  ProfileprocessPerimeter = true
  SafeHeightExpression = OpStockZMax+SetupSheet004.SafeHeightOffset
  SafeHeightOffset = 3
  StartDepthExpression = 3 mm
  StepDownExpression = OpToolDiameter
  VertRapid = 0
FEATURE [Part::Part2DObjectPython] Clone2D010  label="Model-Unfold_Sketch_bends016"  # Draft 2D object (typed FeaturePython)
  Fuse = false
  Objects = -> [Unfold_Sketch_bends016]
  PathResource = Model
  Placement = pos=(-3,159,0) rot=(0,0,-1;1.5708rad)
  Scale = (1,1,1)
  expr: Placement = <<Model-Unfold015>>.Placement
FEATURE [Part::FeaturePython] ToolBit004  label="NZV6109018"  # Path/CAM toolbit (typed FeaturePython)
  BitPropertyNames = Chipload | CuttingEdgeAngle | CuttingEdgeHeight | Diameter | Flutes | Length | Material | ShankDiameter | TipDiameter
  BitShape = <path>
  Chipload = 0
  CuttingEdgeAngle = 90
  CuttingEdgeHeight = 4
  Diameter = 10
  Flutes = 0
  Length = 50
  Material = 0
  ShankDiameter = 6
  ShapeName = chamfer
  TipDiameter = 1
FEATURE [Path::FeaturePython] NZV6109016  label="NZV6109017"  # Path/CAM operation (typed FeaturePython)
  HorizFeed = 51.6667
  HorizRapid = 0
  SpindleDir = 0
  SpindleSpeed = 18000
  Tool = -> ToolBit004
  ToolNumber = 2
  VertFeed = 16.6667
  VertRapid = 0
  expr: HorizRapid = SetupSheet004.HorizRapid
  expr: VertRapid = SetupSheet004.VertRapid
FEATURE [App::DocumentObjectGroup] Tools004
  Group = -> [NZV6109016]
FEATURE [Path::FeaturePython] Profile003  # Path/CAM operation (typed FeaturePython)
  Active = true
  AreaParams:
    Tolerance = 1e-07
    FitArcs = True
    Simplify = False
    CleanDistance = 0.0
    Accuracy = 0.01
    Unit = 1.0
    MinArcPoints = 4
    MaxArcPoints = 100
    ClipperScale = 10000000.0
    Fill = 0
    Coplanar = 0
    Reorient = True
    Outline = False
    Explode = False
    OpenMode = 0
    Deflection = 0.01
    SubjectFill = 0
    ClipFill = 0
    Offset = 1.585
    ExtraPass = 0
    Stepover = 0.0
    LastStepover = 0.0
    JoinType = 0
    EndType = 0
    MiterLimit = 2.0
    RoundPrecision = 0.0
    PocketMode = 0
    ToolRadius = 1.0
    PocketExtraOffset = 0.0
    PocketStepover = 0.0
    PocketLastStepover = 0.0
    FromCenter = False
    Angle = 45.0
    AngleShift = 0.0
    Shift = 0.0
    Thicken = False
    SectionCount = -1
    Stepdown = 1.0
    SectionOffset = 0.0
    SectionTolerance = 1e-07
    SectionMode = 2
    Project = False
  ClearanceHeight = 6.3
  CoolantMode = 0
  CycleTime = 00:01:16
  Direction = 1
  FinalDepth = -0.1
  HandleMultipleFeatures = 0
  JoinType = 0
  MiterLimit = 0.1
  OffsetExtra = 0
  OpFinalDepth = -7.1e-15
  OpStartDepth = 1.3
  OpStockZMax = 1.3
  OpStockZMin = -7.1e-15
  OpToolDiameter = 3.17
  PathParams = {'orientation': 0, 'feedrate': 33.333333333333336, 'feedrate_v': 8.333333333333334, 'verbose': True, 'resume_height': 4.300000000000017, 'retraction': 6.300000000000017, 'return_end': True, 'preamble': False, 'start': Vector (105.19136020688296, 191.69990215656196, 6.300000000000017)}
  SafeHeight = 4.3
  Side = 0
  SplitArcs = false
  StartDepth = 3
  StartPoint = (0,0,0)
  StepDown = 4
  ToolController = -> __175mm_Endmill002
  UseComp = true
  UseStartPoint = false
  processCircles = true
  processHoles = true
  processPerimeter = true
  expr: ClearanceHeight = OpStockZMax + SetupSheet003.ClearanceHeightOffset
  expr: FinalDepth = -0.1mm
  expr: SafeHeight = OpStockZMax + SetupSheet003.SafeHeightOffset
  expr: StartDepth = 3mm
  expr: StepDown = 4mm
FEATURE [Path::FeaturePython] Engrave002  # Path/CAM operation (typed FeaturePython)
  Active = true
  ClearanceHeight = 6
  CoolantMode = 0
  CycleTime = 00:00:53
  FinalDepth = 0.6
  OpFinalDepth = -10
  OpStartDepth = 0
  OpStockZMax = 1
  OpStockZMin = 0
  OpToolDiameter = 10
  SafeHeight = 4
  StartDepth = 3
  StartVertex = 0
  StepDown = 10
  ToolController = -> NZV6109016
  expr: ClearanceHeight = OpStockZMax + SetupSheet004.ClearanceHeightOffset
  expr: FinalDepth = 0.6mm
  expr: SafeHeight = OpStockZMax + SetupSheet004.SafeHeightOffset
  expr: StartDepth = 3mm
  expr: StepDown = OpToolDiameter
FEATURE [App::DocumentObjectGroup] Operations004
  Group = -> [Engrave002]
FEATURE [Part::FeaturePython] Clone051  label="Model-Unfold016"  # Draft clone (typed FeaturePython)
  AttacherType = Attacher::AttachEngine3D
  Fuse = false
  Objects = -> [Unfold015]
  PathResource = Model
  Placement = pos=(150,97,0) rot=(0,0,1;1.5708rad)
  Scale = (1,1,1)
FEATURE [Part::FeaturePython] Clone052  label="Model-Unfold017"  # Draft clone (typed FeaturePython)
  AttacherType = Attacher::AttachEngine3D
  Fuse = false
  Objects = -> [Unfold015]
  PathResource = Model
  Placement = pos=(150,222,0) rot=(0,0,1;1.5708rad)
  Scale = (1,1,1)
FEATURE [Part::FeaturePython] Clone053  label="Model-Unfold018"  # Draft clone (typed FeaturePython)
  AttacherType = Attacher::AttachEngine3D
  Fuse = false
  Objects = -> [Unfold015]
  PathResource = Model
  Placement = pos=(-3,284,0) rot=(0,0,-1;1.5708rad)
  Scale = (1,1,1)
FEATURE [Part::FeaturePython] Clone054  label="Model-Unfold019"  # Draft clone (typed FeaturePython)
  AttacherType = Attacher::AttachEngine3D
  Fuse = false
  Objects = -> [Unfold015]
  PathResource = Model
  Placement = pos=(-3,33.4821,0) rot=(0,0,-1;1.5708rad)
  Scale = (1,1,1)
FEATURE [App::DocumentObjectGroup] Model004
  Group = -> [Clone050,Clone051,Clone052,Clone053,Clone054]
FEATURE [Part::FeaturePython] Stock003  # WARN: FeaturePython — macro-defined, semantics opaque (R4)
  Base = -> Model004
  ExtXneg = 1
  ExtXpos = 1
  ExtYneg = 1
  ExtYpos = 0
  ExtZneg = 0
  ExtZpos = 1
  Placement = pos=(-33.4821,3,-7.1e-15) rot=(0,0,1;0rad)
  StockType = FromBase
FEATURE [Path::FeaturePython] Profile002  # Path/CAM operation (typed FeaturePython)
  Active = true
  AreaParams:
    Tolerance = 1e-07
    FitArcs = True
    Simplify = False
    CleanDistance = 0.0
    Accuracy = 0.01
    Unit = 1.0
    MinArcPoints = 4
    MaxArcPoints = 100
    ClipperScale = 10000000.0
    Fill = 0
    Coplanar = 0
    Reorient = True
    Outline = False
    Explode = False
    OpenMode = 0
    Deflection = 0.01
    SubjectFill = 0
    ClipFill = 0
    Offset = -1.585
    ExtraPass = 0
    Stepover = 0.0
    LastStepover = 0.0
    JoinType = 0
    EndType = 0
    MiterLimit = 2.0
    RoundPrecision = 0.0
    PocketMode = 0
    ToolRadius = 1.0
    PocketExtraOffset = 0.0
    PocketStepover = 0.0
    PocketLastStepover = 0.0
    FromCenter = False
    Angle = 45.0
    AngleShift = 0.0
    Shift = 0.0
    Thicken = False
    SectionCount = -1
    Stepdown = 1.0
    SectionOffset = 0.0
    SectionTolerance = 1e-07
    SectionMode = 2
    Project = False
  Base = -> [Clone054,Clone051,Clone050,Clone052,Clone053]
  ClearanceHeight = 6.3
  CoolantMode = 0
  CycleTime = 00:01:09
  Direction = 1
  FinalDepth = -0.1
  HandleMultipleFeatures = 0
  JoinType = 0
  MiterLimit = 0.1
  OffsetExtra = 0
  OpFinalDepth = -7.1e-15
  OpStartDepth = 1.3
  OpStockZMax = 1.3
  OpStockZMin = -7.1e-15
  OpToolDiameter = 3.17
  PathParams = {'orientation': 1, 'feedrate': 33.333333333333336, 'feedrate_v': 8.333333333333334, 'verbose': True, 'resume_height': 4.300000000000017, 'retraction': 6.300000000000017, 'return_end': True, 'preamble': False, 'start': Vector (141.91281824339632, 33.54281853869163, 6.300000000000017)}
  SafeHeight = 4.3
  Side = 0
  SplitArcs = false
  StartDepth = 3
  StartPoint = (0,0,0)
  StepDown = 4
  ToolController = -> __175mm_Endmill002
  UseComp = true
  UseStartPoint = false
  processCircles = true
  processHoles = true
  processPerimeter = false
  expr: ClearanceHeight = OpStockZMax + SetupSheet003.ClearanceHeightOffset
  expr: FinalDepth = -0.1mm
  expr: SafeHeight = OpStockZMax + SetupSheet003.SafeHeightOffset
  expr: StartDepth = 3mm
  expr: StepDown = 4mm
FEATURE [App::DocumentObjectGroup] Operations003
  Group = -> [Profile002,Profile003]
FEATURE [Path::FeaturePython] Job003  # Path/CAM operation (typed FeaturePython)
  CycleTime = 00:02:25
  Fixtures = G54
  GeometryTolerance = 0.01
  JobType = 0
  LastPostProcessDate = 2023-02-01 13:39:08.442867
  LastPostProcessOutput = <userpath>/2411-26D9/Job003-0.tap \n<userpath>/2411-26D9/Job003-1.tap
  Model = -> Model004
  Operations = -> Operations003
  OrderOutputBy = 2
  PostProcessor = 1
  PostProcessorOutputFile = %d.%j.tap
  SetupSheet = -> SetupSheet003
  SplitOutput = true
  Stock = -> Stock003
  Tools = -> Tools003
FEATURE [Part::Part2DObjectPython] Clone2D011  label="Model-Unfold_Sketch_bends017"  # Draft 2D object (typed FeaturePython)
  Fuse = false
  Objects = -> [Unfold_Sketch_bends016]
  PathResource = Model
  Placement = pos=(150,97,0) rot=(0,0,1;1.5708rad)
  Scale = (1,1,1)
  expr: Placement = <<Model-Unfold016>>.Placement
FEATURE [Part::Part2DObjectPython] Clone2D012  label="Model-Unfold_Sketch_bends018"  # Draft 2D object (typed FeaturePython)
  Fuse = false
  Objects = -> [Unfold_Sketch_bends016]
  PathResource = Model
  Placement = pos=(150,222,0) rot=(0,0,1;1.5708rad)
  Scale = (1,1,1)
  expr: Placement = <<Model-Unfold017>>.Placement
FEATURE [Part::Part2DObjectPython] Clone2D013  label="Model-Unfold_Sketch_bends019"  # Draft 2D object (typed FeaturePython)
  Fuse = false
  Objects = -> [Unfold_Sketch_bends016]
  PathResource = Model
  Placement = pos=(-3,284,0) rot=(0,0,-1;1.5708rad)
  Scale = (1,1,1)
  expr: Placement = <<Model-Unfold018>>.Placement
FEATURE [Part::Part2DObjectPython] Clone2D014  label="Model-Unfold_Sketch_bends020"  # Draft 2D object (typed FeaturePython)
  Fuse = false
  Objects = -> [Unfold_Sketch_bends016]
  PathResource = Model
  Placement = pos=(-3,33.4821,0) rot=(0,0,-1;1.5708rad)
  Scale = (1,1,1)
  expr: Placement = <<Model-Unfold019>>.Placement
FEATURE [App::DocumentObjectGroup] Model005
  Group = -> [Clone2D010,Clone2D011,Clone2D012,Clone2D013,Clone2D014]
FEATURE [Part::FeaturePython] Stock004  # WARN: FeaturePython — macro-defined, semantics opaque (R4)
  Base = -> Model005
  ExtXneg = 1
  ExtXpos = 1
  ExtYneg = 1
  ExtYpos = 1
  ExtZneg = 0
  ExtZpos = 1
  Placement = pos=(-8.61566,3,0) rot=(0,0,1;0rad)
  StockType = FromBase
FEATURE [Path::FeaturePython] Job004  # Path/CAM operation (typed FeaturePython)
  CycleTime = 00:00:53
  Fixtures = G54
  GeometryTolerance = 0.01
  JobType = 0
  LastPostProcessDate = 2023-02-01 13:39:18.134572
  LastPostProcessOutput = <userpath>/2411-26D9/Job004.tap
  Model = -> Model005
  Operations = -> Operations004
  OrderOutputBy = 0
  PostProcessor = 1
  PostProcessorOutputFile = %d.%j.tap
  SetupSheet = -> SetupSheet004
  SplitOutput = false
  Stock = -> Stock004
  Tools = -> Tools004
FEATURE [Sketcher::SketchObject] Sketch134
  AttachmentOffset = pos=(0,0,0) rot=(0,1,0;1.0472rad)
  FullyConstrained = true
  MapMode = 5
  Placement = pos=(0,0,0) rot=(0.186157,0.694747,0.694747;2.77349rad)
  Support = -> [YZ_Plane001]
  expr: Constraints[18] = <<main>>.total_length
  expr: Constraints[19] = Sketch012.Constraints.top
  expr: Constraints[20] = Sketch012.Constraints.bottom
  expr: Constraints[21] = <<main_sketch>>.Constraints.overlap_bend_offset + 1mm
  sketch-geometry (8):
    g0: LineSegment StartX=0 StartY=0 StartZ=0 EndX=-6.7735 EndY=0 EndZ=0
    g1: LineSegment StartX=-6.7735 StartY=0 StartZ=0 EndX=-6.7735 EndY=263 EndZ=0
    g2: LineSegment StartX=-6.7735 StartY=263 StartZ=0 EndX=0 EndY=263 EndZ=0
    g3: LineSegment StartX=0 StartY=263 StartZ=0 EndX=0 EndY=0 EndZ=0
    g4: LineSegment StartX=0 StartY=774 StartZ=0 EndX=-6.7735 EndY=774 EndZ=0
    g5: LineSegment StartX=-6.7735 StartY=774 StartZ=0 EndX=-6.7735 EndY=724 EndZ=0
    g6: LineSegment StartX=-6.7735 StartY=724 StartZ=0 EndX=0 EndY=724 EndZ=0
    g7: LineSegment StartX=0 StartY=724 StartZ=0 EndX=0 EndY=774 EndZ=0
  constraints (23):
    c: Coincident(g0,g1)
    c: Coincident(g1,g2)
    c: Coincident(g2,g3)
    c: Coincident(g3,g0)
    c: Horizontal(g0)
    c: Horizontal(g2)
    c: Vertical(g1)
    c: Vertical(g3)
    c: Coincident(g0,g-1)
    c: Coincident(g4,g5)
    c: Coincident(g5,g6)
    c: Coincident(g6,g7)
    c: Coincident(g7,g4)
    c: Horizontal(g4)
    c: Horizontal(g6)
    c: Vertical(g5)
    c: Vertical(g7)
    c: PointOnObject(g4,g-2)
    c: DistanceY(g4) = 774
    c: DistanceY(g5,g5) = 50
    c: DistanceY(g1) = 263
    c: DistanceX(g0,g0) = 6.7735
    c: Vertical(g5,g1)
FEATURE [PartDesign::Pocket] Pocket091
  BaseFeature = -> Pocket007
  Direction = (-0.5,-0.866025,-1e-16)
  Length = 16
  Length2 = 5
  Profile = -> Sketch134
  ReferenceAxis = -> Sketch134 [N_Axis]
  Refine = true
  Reversed = true
  Type = 0
  expr: Length = <<main>>.end_face_width / 2
FEATURE [PartDesign::CoordinateSystem] Local_CS046
  AttacherType = Attacher::AttachEngine3D
  AttachmentOffset = pos=(0,0,0) rot=(0,0,1;1.0472rad)
  MapMode = 5
  Placement = pos=(0,0,0) rot=(0,0,1;1.0472rad)
  Support = -> [XY_Plane001]
FEATURE [Sketcher::SketchObject] Sketch135
  AttachmentOffset = pos=(0,-5.7735,774) rot=(0,1,0;-1.5708rad)
  FullyConstrained = true
  MapMode = 5
  Placement = pos=(5,-2.88675,774) rot=(-0.447214,0.774597,-0.447214;4.45971rad)
  Support = -> [Local_CS046]
  expr: .AttachmentOffset.Base.y = -<<main_sketch>>.Constraints.overlap_bend_offset
  expr: .AttachmentOffset.Base.z = <<main>>.total_length
  expr: Constraints[7] = <<main>>.thickness
  sketch-geometry (3):
    g0: LineSegment StartX=-3 StartY=0 StartZ=0 EndX=0 EndY=-3 EndZ=0
    g1: LineSegment StartX=0 StartY=-3 StartZ=0 EndX=0 EndY=0 EndZ=0
    g2: LineSegment StartX=0 StartY=0 StartZ=0 EndX=-3 EndY=0 EndZ=0
  constraints (8):
    c: PointOnObject(g0,g-1)
    c: PointOnObject(g0,g-2)
    c: Coincident(g0,g1)
    c: Coincident(g1,g-1)
    c: Coincident(g1,g2)
    c: Coincident(g2,g0)
    c: Equal(g2,g1)
    c: DistanceY(g1,g1) = 3
FEATURE [Sketcher::SketchObject] Sketch136
  FullyConstrained = true
  MapMode = 5
  Support = -> [XY_Plane001]
  sketch-geometry (6):
    g0: LineSegment StartX=0 StartY=-100 StartZ=0 EndX=-86.6025 EndY=50 EndZ=0
    g1: LineSegment StartX=-86.6025 StartY=50 StartZ=0 EndX=86.6025 EndY=50 EndZ=0
    g2: LineSegment StartX=86.6025 StartY=50 StartZ=0 EndX=0 EndY=-100 EndZ=0
    g3: LineSegment StartX=-86.6025 StartY=50 StartZ=0 EndX=0 EndY=7.1e-15 EndZ=0
    g4: LineSegment StartX=0 StartY=7.1e-15 StartZ=0 EndX=86.6025 EndY=50 EndZ=0
    g5: LineSegment StartX=0 StartY=7.1e-15 StartZ=0 EndX=0 EndY=-100 EndZ=0
  constraints (15):
    c: PointOnObject(g0,g-2)
    c: Coincident(g1,g0)
    c: Horizontal(g1)
    c: Coincident(g2,g1)
    c: Coincident(g2,g0)
    c: Coincident(g3,g0)
    c: Coincident(g3,g-1)
    c: Coincident(g4,g3)
    c: Coincident(g4,g1)
    c: Coincident(g5,g3)
    c: Coincident(g5,g0)
    c: Equal(g3,g4)
    c: Equal(g4,g5)
    c: Equal(g0,g1)
    c: DistanceY(g1) = 50
FEATURE [PartDesign::Pocket] Pocket093
  BaseFeature = -> Pocket091
  Direction = (0,0,-1)
  Length = 157
  Length2 = 5
  Profile = -> Sketch136
  ReferenceAxis = -> Sketch136 [N_Axis]
  Reversed = true
  Type = 0
  expr: Length = <<main>>.basin_height
FEATURE [PartDesign::Pocket] Pocket083
  BaseFeature = -> Pocket093
  Direction = (0,0,-1)
  Length = 5
  Length2 = 5
  Midplane = true
  Profile = -> Sketch130
  ReferenceAxis = -> Sketch130 [N_Axis]
  Type = 1
FEATURE [PartDesign::MultiTransform] MultiTransform014
  BaseFeature = -> Pocket083
  Originals = -> [Pocket083]
  Transformations = -> [Mirrored040,PolarPattern017]
FEATURE [PartDesign::Pocket] Pocket082
  BaseFeature = -> MultiTransform014
  Direction = (0.5,-0.866025,-1e-16)
  Length = 33
  Length2 = 5
  Midplane = true
  Profile = -> Sketch129
  ReferenceAxis = -> Sketch129 [N_Axis]
  Type = 0
  expr: Length = <<main>>.end_face_width + 1mm
FEATURE [PartDesign::Pocket] Pocket006
  BaseFeature = -> Pocket082
  Direction = (-1,2e-16,-2e-16)
  Length = 33
  Length2 = 160
  Midplane = true
  Profile = -> Sketch009
  ReferenceAxis = -> Sketch009 [N_Axis]
  Type = 0
  expr: Length = <<main>>.end_face_width + 1mm
FEATURE [Sketcher::SketchObject] Sketch137
  AttachmentOffset = pos=(0,18.4752,0) rot=(0.935113,-0.250563,-0.250563;1.63783rad)
  ExternalGeometry = -> [Sketch128]
  FullyConstrained = true
  MapMode = 5
  Placement = pos=(-16,-9.2376,0) rot=(0.57735,0.57735,0.57735;2.0944rad)
  Support = -> [Local_CS042]
  expr: .AttachmentOffset.Base.y = -Sketch009.AttachmentOffset.Base.y
  expr: .AttachmentOffset.Rotation.Angle = Sketch009.AttachmentOffset.Rotation.Angle
  expr: .AttachmentOffset.Rotation.Axis = Sketch009.AttachmentOffset.Rotation.Axis
  expr: Constraints[20] = Sketch009.Constraints[20]
  expr: Constraints[21] = Sketch009.Constraints[21]
  expr: Constraints[34] = Sketch009.Constraints[34]
  expr: Constraints[35] = Sketch009.Constraints[35]
  expr: Constraints[7] = Sketch009.Constraints[7]
  sketch-geometry (18):
    g0: LineSegment StartX=0 StartY=0 StartZ=0 EndX=0 EndY=157 EndZ=0
    g1: LineSegment StartX=192.937 StartY=152 StartZ=0 EndX=192.937 EndY=127 EndZ=0
    g2: LineSegment StartX=187.937 StartY=122 StartZ=0 EndX=183.825 EndY=122 EndZ=0
    g3: LineSegment StartX=178.979 StartY=118.232 StartZ=0 EndX=148.93 EndY=0 EndZ=0
    g4: LineSegment StartX=148.93 StartY=0 StartZ=0 EndX=0 EndY=0 EndZ=0
    g5: ArcOfCircle CenterX=187.937 CenterY=152 CenterZ=0 NormalX=0 NormalY=0 NormalZ=1 AngleXU=0 Radius=5 StartAngle=2.5e-15 EndAngle=1.5708
    g6: GeomPoint X=192.937 Y=157 Z=0
    g7: ArcOfCircle CenterX=187.937 CenterY=127 CenterZ=0 NormalX=0 NormalY=0 NormalZ=1 AngleXU=0 Radius=5 StartAngle=4.71239 EndAngle=6.28319
    g8: GeomPoint X=192.937 Y=122 Z=0
    g9: ArcOfCircle CenterX=183.825 CenterY=117 CenterZ=0 NormalX=0 NormalY=0 NormalZ=1 AngleXU=0 Radius=5 StartAngle=1.5708 EndAngle=2.89271
    g10: GeomPoint X=179.937 Y=122 Z=0
    g11: LineSegment StartX=82.2376 StartY=116.5 StartZ=0 EndX=175.238 EndY=116.5 EndZ=0
    g12: LineSegment StartX=175.238 StartY=116.5 StartZ=0 EndX=175.238 EndY=157 EndZ=0
    g13: LineSegment StartX=175.238 StartY=157 StartZ=0 EndX=82.2376 EndY=157 EndZ=0
    g14: LineSegment StartX=82.2376 StartY=157 StartZ=0 EndX=82.2376 EndY=116.5 EndZ=0
    g15: LineSegment StartX=0 StartY=157 StartZ=0 EndX=82.2376 EndY=157 EndZ=0
    g16: LineSegment StartX=175.238 StartY=157 StartZ=0 EndX=187.937 EndY=157 EndZ=0
    g17: LineSegment StartX=208.395 StartY=149.752 StartZ=0 EndX=192.937 EndY=149.752 EndZ=0
  constraints (44):
    c: Coincident(g-1,g0)
    c: Vertical(g0)
    c: Vertical(g1)
    c: Horizontal(g2)
    c: PointOnObject(g3,g-1)
    c: Coincident(g3,g4)
    c: Coincident(g4,g0)
    c: DistanceY(g0,g0) = 157
    c: PointOnObject(g6,g1)
    c: Tangent(g1,g5) = 1.5708
    c: PointOnObject(g8,g2)
    c: PointOnObject(g8,g1)
    c: Tangent(g2,g7) = 1.5708
    c: Tangent(g1,g7) = 1.5708
    c: PointOnObject(g10,g3)
    c: PointOnObject(g10,g2)
    c: Tangent(g3,g9) = -1.5708
    c: Tangent(g2,g9) = -1.5708
    c: Equal(g9,g7)
    c: Equal(g7,g5)
    c: Diameter(g7) = 10
    c: Distance(g8,g10) = 13
    c: Coincident(g11,g12)
    c: Coincident(g12,g13)
    c: Coincident(g13,g14)
    c: Coincident(g14,g11)
    c: Coincident(g15,g0)
    c: Coincident(g15,g13)
    c: Coincident(g16,g12)
    c: Horizontal(g16)
    c: Tangent(g16,g5) = 1.5708
    c: PointOnObject(g6,g16)
    c: PointOnObject(g17,g1)
    c: Horizontal(g17)
    c: DistanceX(g17) = 208.395
    c: DistanceY(g17) = 149.752
    c: Coincident(g11,g-3)
    c: Angle(g3,g-1) = 1.81968
    c: Distance(g11,g3) = 3.2
    c: DistanceY(g8,g14) = 35
    c: Coincident(g11,g-4)
    c: Perpendicular(g12,g13)
    c: Perpendicular(g14,g11)
    c: Coincident(g12,g-5)
FEATURE [PartDesign::Pocket] Pocket094
  BaseFeature = -> Pocket006
  Direction = (-1,1e-16,-4e-16)
  Length = 5
  Length2 = 5
  Profile = -> Sketch137
  ReferenceAxis = -> Sketch137 [N_Axis]
  Reversed = true
  Type = 0
FEATURE [PartDesign::Mirrored] Mirrored002
  BaseFeature = -> Pocket094
  MirrorPlane = -> DatumPlane014
  Originals = -> [Pocket006,Pocket094]
FEATURE [PartDesign::Pocket] Pocket014
  BaseFeature = -> Mirrored002
  Direction = (-1,2e-16,-3e-16)
  Length = 34
  Length2 = 5
  Midplane = true
  Profile = -> Sketch013
  ReferenceAxis = -> Sketch013 [N_Axis]
  Type = 0
  expr: Length = <<main>>.end_face_width + 2mm
FEATURE [PartDesign::PolarPattern] PolarPattern003
  Angle = 360
  Axis = -> Z_Axis001
  BaseFeature = -> Pocket014
  Occurrences = 3
  Originals = -> [Pocket014]
  Refine = true
FEATURE [PartDesign::Pocket] Pocket092
  BaseFeature = -> PolarPattern003
  Direction = (0.5,0.866025,1e-16)
  Length = 16
  Length2 = 5
  Profile = -> Sketch135
  ReferenceAxis = -> Sketch135 [N_Axis]
  Type = 0
  expr: Length = <<main>>.end_face_width / 2
FEATURE [PartDesign::Pocket] Pocket013
  BaseFeature = -> Pocket092
  Direction = (0,0,-1)
  Length = 5
  Length2 = 5
  Midplane = true
  Profile = -> Sketch043
  ReferenceAxis = -> Sketch043 [N_Axis]
  Type = 1
FEATURE [PartDesign::MultiTransform] MultiTransform005
  BaseFeature = -> Pocket013
  Originals = -> [Pocket013]
  Transformations = -> [Mirrored013,PolarPattern002]
FEATURE [PartDesign::Pocket] Pocket068
  BaseFeature = -> MultiTransform005
  Direction = (-1,0,0)
  Length = 5
  Length2 = 5
  Midplane = true
  Profile = -> Binder034
  Type = 1
FEATURE [PartDesign::Pocket] Pocket069
  BaseFeature = -> Pocket068
  Direction = (-1,0,-4e-16)
  Length = 5
  Length2 = 5
  Midplane = true
  Profile = -> Binder035
  Type = 1
FEATURE [PartDesign::Pocket] Pocket025
  BaseFeature = -> Pocket069
  Direction = (-1,0,-2e-16)
  Length = 5
  Length2 = 5
  Midplane = true
  Profile = -> Binder027
  Type = 1
FEATURE [PartDesign::Pocket] Pocket072
  BaseFeature = -> Pocket025
  Direction = (-1,2e-16,-3e-16)
  Length = 5
  Length2 = 5
  Midplane = true
  Profile = -> Sketch119
  ReferenceAxis = -> Sketch119 [N_Axis]
  Type = 1
FEATURE [PartDesign::Pocket] Pocket079
  BaseFeature = -> Pocket072
  Direction = (0,1,2e-16)
  Length = 5
  Length2 = 5
  Profile = -> Sketch125
  ReferenceAxis = -> Sketch125 [N_Axis]
  Type = 1
FEATURE [PartDesign::PolarPattern] PolarPattern
  Angle = 360
  Axis = -> Z_Axis001
  BaseFeature = -> Pocket079
  Occurrences = 3
  Originals = -> [Pocket068,Pocket069,Pocket025,Pocket072,Pocket079]
FEATURE [PartDesign::Pocket] Pocket
  BaseFeature = -> PolarPattern
  Direction = (-1,0,0)
  Length = 5
  Length2 = 5
  Profile = -> Sketch011
  ReferenceAxis = -> Sketch011 [N_Axis]
  Reversed = true
  Type = 1
FEATURE [PartDesign::LinearPattern] LinearPattern001
  BaseFeature = -> Pocket
  Direction = -> Sketch011 [V_Axis]
  Length = 576
  Occurrences = 5
  Originals = -> [Pocket]
  expr: Length = 144mm * (Occurrences - 1)
FEATURE [PartDesign::Pocket] Pocket073
  BaseFeature = -> LinearPattern001
  Direction = (0,0,-1)
  Length = 7
  Length2 = 5
  Midplane = true
  Profile = -> Sketch073
  ReferenceAxis = -> Sketch073 [N_Axis]
  Type = 0
FEATURE [PartDesign::MultiTransform] MultiTransform010
  BaseFeature = -> Pocket073
  Originals = -> [Pocket073]
  Transformations = -> [PolarPattern009,Mirrored027,PolarPattern019]
FEATURE [PartDesign::Pocket] Pocket049
  BaseFeature = -> MultiTransform010
  Direction = (-1,2e-16,-3e-16)
  Length = 5
  Length2 = 5
  Profile = -> Sketch088
  ReferenceAxis = -> Sketch088 [N_Axis]
  Type = 1
FEATURE [PartDesign::MultiTransform] MultiTransform012
  BaseFeature = -> Pocket049
  Originals = -> [Pocket049]
  Transformations = -> [PolarPattern012,Mirrored033]
FEATURE [PartDesign::Body] Body001  label="Body001_material_0.30ansi"
  Group = -> [Local_CS,Local_CS011,Sketch003,BaseBend001,Local_CS012,DatumPlane011,DatumPlane012,Local_CS035,Local_CS036,Local_CS037,Local_CS038,Sketch112,Sketch113,Sketch128,Pocket081,Local_CS039,PolarPattern016,Bend,Pocket007,Pocket091,Sketch129,Local_CS041,Sketch130,Sketch136,Pocket093,Pocket083,MultiTransform014,Mirrored040,PolarPattern017,Local_CS042,Pocket082,Pocket006,Sketch137,Pocket094,Mirrored002,+58 more]
  Origin = -> Origin001
  Tip = -> Pocket094
FEATURE [Part::Feature] Unfold016
  shape: bbox 1317 x 0.302 x 774 mm, 572 faces (baked)
FEATURE [Sketcher::SketchObject] Unfold_Sketch
  FullyConstrained = false
  sketch-geometry (570):
    g0: LineSegment StartX=-157 StartY=-151.675 StartZ=0 EndX=-157 EndY=-149.775 EndZ=0
    g1: ArcOfCircle CenterX=-197 CenterY=-149.775 CenterZ=0 NormalX=0 NormalY=0 NormalZ=1 AngleXU=1.5708 Radius=40 StartAngle=3.14159 EndAngle=4.71239
    g2: LineSegment StartX=-197 StartY=-189.775 StartZ=0 EndX=-212 EndY=-189.775 EndZ=0
    g3: ArcOfCircle CenterX=-212 CenterY=-194.775 CenterZ=0 NormalX=0 NormalY=0 NormalZ=1 AngleXU=1.5708 Radius=5 StartAngle=2e-16 EndAngle=1.5708
    g4: LineSegment StartX=-157 StartY=-281.393 StartZ=0 EndX=-157 EndY=-279.493 EndZ=0
    g5: ArcOfCircle CenterX=-197 CenterY=-281.393 CenterZ=0 NormalX=0 NormalY=0 NormalZ=1 AngleXU=-1.5708 Radius=40 StartAngle=1.5708 EndAngle=3.14159
    g6: LineSegment StartX=-212 StartY=-241.393 StartZ=0 EndX=-197 EndY=-241.393 EndZ=0
    g7: ArcOfCircle CenterX=-212 CenterY=-236.393 CenterZ=0 NormalX=0 NormalY=0 NormalZ=1 AngleXU=-1.5708 Radius=5 StartAngle=4.71239 EndAngle=6.28319
    g8: ArcOfCircle CenterX=-126.802 CenterY=-289.393 CenterZ=0 NormalX=0 NormalY=0 NormalZ=1 AngleXU=1.5708 Radius=10 StartAngle=4.71239 EndAngle=6.14165
    g9: LineSegment StartX=-116.802 StartY=-362.393 StartZ=0 EndX=-116.802 EndY=-289.393 EndZ=0
    g10: ArcOfCircle CenterX=-126.802 CenterY=-362.393 CenterZ=0 NormalX=0 NormalY=0 NormalZ=1 AngleXU=1.5708 Radius=10 StartAngle=3.28313 EndAngle=4.71239
    g11: LineSegment StartX=0 StartY=-375.573 StartZ=0 EndX=-157 EndY=-375.573 EndZ=0
    g12: LineSegment StartX=-157 StartY=-375.573 StartZ=0 EndX=-157 EndY=-372.293 EndZ=0
    g13: LineSegment StartX=-157 StartY=-490.042 StartZ=0 EndX=-157 EndY=-486.762 EndZ=0
    g14: LineSegment StartX=-157 StartY=-486.762 StartZ=0 EndX=0 EndY=-486.762 EndZ=0
    g15: ArcOfCircle CenterX=-126.802 CenterY=-499.942 CenterZ=0 NormalX=0 NormalY=0 NormalZ=1 AngleXU=-1.5708 Radius=10 StartAngle=1.5708 EndAngle=3.00005
    g16: LineSegment StartX=-116.802 StartY=-572.942 StartZ=0 EndX=-116.802 EndY=-499.942 EndZ=0
    g17: ArcOfCircle CenterX=-126.802 CenterY=-572.942 CenterZ=0 NormalX=0 NormalY=0 NormalZ=1 AngleXU=-1.5708 Radius=10 StartAngle=0.141539 EndAngle=1.5708
    g18: LineSegment StartX=-197 StartY=-620.942 StartZ=0 EndX=-212 EndY=-620.942 EndZ=0
    g19: ArcOfCircle CenterX=-197 CenterY=-580.942 CenterZ=0 NormalX=0 NormalY=0 NormalZ=1 AngleXU=1.5708 Radius=40 StartAngle=3.14159 EndAngle=4.71239
    g20: LineSegment StartX=-157 StartY=-582.842 StartZ=0 EndX=-157 EndY=-580.942 EndZ=0
    g21: ArcOfCircle CenterX=-212 CenterY=-625.942 CenterZ=0 NormalX=0 NormalY=0 NormalZ=1 AngleXU=1.5708 Radius=5 StartAngle=0 EndAngle=1.5708
    g22: LineSegment StartX=-157 StartY=-712.56 StartZ=0 EndX=-157 EndY=-710.66 EndZ=0
    g23: ArcOfCircle CenterX=-197 CenterY=-712.56 CenterZ=0 NormalX=0 NormalY=0 NormalZ=1 AngleXU=-1.5708 Radius=40 StartAngle=1.5708 EndAngle=3.14159
    g24: LineSegment StartX=-212 StartY=-672.56 StartZ=0 EndX=-197 EndY=-672.56 EndZ=0
    g25: ArcOfCircle CenterX=-212 CenterY=-667.56 CenterZ=0 NormalX=0 NormalY=0 NormalZ=1 AngleXU=-1.5708 Radius=5 StartAngle=4.71239 EndAngle=6.28319
    g26: ArcOfCircle CenterX=-126.802 CenterY=-720.56 CenterZ=0 NormalX=0 NormalY=0 NormalZ=1 AngleXU=1.5708 Radius=10 StartAngle=4.71239 EndAngle=6.14165
    g27: LineSegment StartX=-116.802 StartY=-793.56 StartZ=0 EndX=-116.802 EndY=-720.56 EndZ=0
    g28: ArcOfCircle CenterX=-126.802 CenterY=-793.56 CenterZ=0 NormalX=0 NormalY=0 NormalZ=1 AngleXU=1.5708 Radius=10 StartAngle=3.28313 EndAngle=4.71239
    g29: LineSegment StartX=-118.232 StartY=-807.302 StartZ=0 EndX=-4.26e-14 EndY=-777.253 EndZ=0
    g30: ArcOfCircle CenterX=-117 CenterY=-812.148 CenterZ=0 NormalX=0 NormalY=0 NormalZ=1 AngleXU=-1.5708 Radius=5 StartAngle=3.39048 EndAngle=4.71239
    g31: LineSegment StartX=-122 StartY=-816.26 StartZ=0 EndX=-122 EndY=-812.148 EndZ=0
    g32: ArcOfCircle CenterX=-127 CenterY=-816.26 CenterZ=0 NormalX=0 NormalY=0 NormalZ=1 AngleXU=-1.5708 Radius=5 StartAngle=0 EndAngle=1.5708
    g33: LineSegment StartX=-152 StartY=-821.26 StartZ=0 EndX=-127 EndY=-821.26 EndZ=0
    g34: ArcOfCircle CenterX=-152 CenterY=-816.26 CenterZ=0 NormalX=0 NormalY=0 NormalZ=1 AngleXU=-1.5708 Radius=5 StartAngle=4.71239 EndAngle=6.28319
    g35: LineSegment StartX=-157 StartY=-803.46 StartZ=0 EndX=-157 EndY=-816.26 EndZ=0
    g36: LineSegment StartX=-2.84e-14 StartY=-937.872 StartZ=0 EndX=-118.231 EndY=-907.829 EndZ=0
    g37: ArcOfCircle CenterX=-117 CenterY=-902.983 CenterZ=0 NormalX=0 NormalY=0 NormalZ=1 AngleXU=1.5708 Radius=5 StartAngle=1.5708 EndAngle=2.89276
    g38: LineSegment StartX=-122 StartY=-902.983 StartZ=0 EndX=-122 EndY=-898.872 EndZ=0
    g39: ArcOfCircle CenterX=-127 CenterY=-898.872 CenterZ=0 NormalX=0 NormalY=0 NormalZ=1 AngleXU=1.5708 Radius=5 StartAngle=4.71239 EndAngle=6.28319
    g40: LineSegment StartX=-127 StartY=-893.872 StartZ=0 EndX=-152 EndY=-893.872 EndZ=0
    g41: ArcOfCircle CenterX=-152 CenterY=-898.872 CenterZ=0 NormalX=0 NormalY=0 NormalZ=1 AngleXU=1.5708 Radius=5 StartAngle=0 EndAngle=1.5708
    g42: LineSegment StartX=-157 StartY=-898.872 StartZ=0 EndX=-157 EndY=-921.209 EndZ=0
    g43: ArcOfCircle CenterX=-126.802 CenterY=-1004.11 CenterZ=0 NormalX=0 NormalY=0 NormalZ=1 AngleXU=-1.5708 Radius=10 StartAngle=0.141539 EndAngle=1.5708
    g44: LineSegment StartX=-116.802 StartY=-931.109 StartZ=0 EndX=-116.802 EndY=-1004.11 EndZ=0
    g45: ArcOfCircle CenterX=-126.802 CenterY=-931.109 CenterZ=0 NormalX=0 NormalY=0 NormalZ=1 AngleXU=-1.5708 Radius=10 StartAngle=1.5708 EndAngle=3.00005
    g46: LineSegment StartX=-157 StartY=-1012.11 StartZ=0 EndX=-157 EndY=-1014.01 EndZ=0
    g47: ArcOfCircle CenterX=-197 CenterY=-1012.11 CenterZ=0 NormalX=0 NormalY=0 NormalZ=1 AngleXU=1.5708 Radius=40 StartAngle=3.14159 EndAngle=4.71239
    g48: LineSegment StartX=-212 StartY=-1052.11 StartZ=0 EndX=-197 EndY=-1052.11 EndZ=0
    g49: ArcOfCircle CenterX=-212 CenterY=-1057.11 CenterZ=0 NormalX=0 NormalY=0 NormalZ=1 AngleXU=1.5708 Radius=5 StartAngle=-9e-16 EndAngle=1.5708
    g50: LineSegment StartX=-217 StartY=-1080.34 StartZ=0 EndX=-217 EndY=-1057.11 EndZ=0
    g51: LineSegment StartX=-217 StartY=-1080.34 StartZ=0 EndX=-263 EndY=-1080.34 EndZ=0
    g52: ArcOfCircle CenterX=-268 CenterY=-1096.43 CenterZ=0 NormalX=0 NormalY=0 NormalZ=1 AngleXU=-1.5708 Radius=5 StartAngle=1.5459e-12 EndAngle=1.5708
    g53: LineSegment StartX=-268 StartY=-1101.43 StartZ=0 EndX=-719 EndY=-1101.43 EndZ=0
    g54: ArcOfCircle CenterX=-719 CenterY=-1096.43 CenterZ=0 NormalX=0 NormalY=0 NormalZ=1 AngleXU=-1.5708 Radius=5 StartAngle=4.71239 EndAngle=6.28319
    g55: LineSegment StartX=-772 StartY=-1080.34 StartZ=0 EndX=-724 EndY=-1080.34 EndZ=0
    g56: LineSegment StartX=-772 StartY=-1080.34 StartZ=0 EndX=-774 EndY=-1078.34 EndZ=0
    g57: LineSegment StartX=-770 StartY=-923.672 StartZ=0 EndX=-774 EndY=-923.672 EndZ=0
    g58: LineSegment StartX=-770 StartY=-927.747 StartZ=0 EndX=-770 EndY=-923.672 EndZ=0
    g59: ArcOfCircle CenterX=-767.5 CenterY=-927.747 CenterZ=0 NormalX=0 NormalY=0 NormalZ=1 AngleXU=1.5708 Radius=2.5 StartAngle=1.5708 EndAngle=3.14159
    g60: LineSegment StartX=-755 StartY=-930.247 StartZ=0 EndX=-767.5 EndY=-930.247 EndZ=0
    g61: ArcOfCircle CenterX=-755 CenterY=-942.872 CenterZ=0 NormalX=0 NormalY=0 NormalZ=1 AngleXU=1.5708 Radius=12.625 StartAngle=3.14159 EndAngle=6.28319
    g62: LineSegment StartX=-755 StartY=-955.497 StartZ=0 EndX=-767.5 EndY=-955.497 EndZ=0
    g63: ArcOfCircle CenterX=-767.5 CenterY=-957.997 CenterZ=0 NormalX=0 NormalY=0 NormalZ=1 AngleXU=1.5708 Radius=2.5 StartAngle=-9e-16 EndAngle=1.5708
    g64: LineSegment StartX=-770 StartY=-997.747 StartZ=0 EndX=-770 EndY=-957.997 EndZ=0
    g65: ArcOfCircle CenterX=-767.5 CenterY=-997.747 CenterZ=0 NormalX=0 NormalY=0 NormalZ=1 AngleXU=1.5708 Radius=2.5 StartAngle=1.5708 EndAngle=3.14159
    g66: LineSegment StartX=-755 StartY=-1000.25 StartZ=0 EndX=-767.5 EndY=-1000.25 EndZ=0
    g67: ArcOfCircle CenterX=-755 CenterY=-1012.87 CenterZ=0 NormalX=0 NormalY=0 NormalZ=1 AngleXU=1.5708 Radius=12.625 StartAngle=3.14159 EndAngle=6.28319
    g68: LineSegment StartX=-755 StartY=-1025.5 StartZ=0 EndX=-767.5 EndY=-1025.5 EndZ=0
    g69: ArcOfCircle CenterX=-767.5 CenterY=-1028 CenterZ=0 NormalX=0 NormalY=0 NormalZ=1 AngleXU=1.5708 Radius=2.5 StartAngle=-9e-16 EndAngle=1.5708
    g70: LineSegment StartX=-770 StartY=-1032.07 StartZ=0 EndX=-770 EndY=-1028 EndZ=0
    g71: LineSegment StartX=-774 StartY=-1032.07 StartZ=0 EndX=-770 EndY=-1032.07 EndZ=0
    g72: LineSegment StartX=-774 StartY=-1032.07 StartZ=0 EndX=-774 EndY=-1078.34 EndZ=0
    g73: LineSegment StartX=-770 StartY=-800.998 StartZ=0 EndX=-774 EndY=-800.998 EndZ=0
    g74: LineSegment StartX=-770 StartY=-791.923 StartZ=0 EndX=-770 EndY=-800.998 EndZ=0
    g75: ArcOfCircle CenterX=-767.5 CenterY=-791.923 CenterZ=0 NormalX=0 NormalY=0 NormalZ=1 AngleXU=-1.5708 Radius=2.5 StartAngle=3.14159 EndAngle=4.71239
    g76: LineSegment StartX=-767.5 StartY=-789.423 StartZ=0 EndX=-755 EndY=-789.423 EndZ=0
    g77: ArcOfCircle CenterX=-755 CenterY=-776.798 CenterZ=0 NormalX=0 NormalY=0 NormalZ=1 AngleXU=-1.5708 Radius=12.625 StartAngle=4e-16 EndAngle=3.14159
    g78: LineSegment StartX=-767.5 StartY=-764.173 StartZ=0 EndX=-755 EndY=-764.173 EndZ=0
    g79: ArcOfCircle CenterX=-767.5 CenterY=-761.673 CenterZ=0 NormalX=0 NormalY=0 NormalZ=1 AngleXU=-1.5708 Radius=2.5 StartAngle=4.71239 EndAngle=6.28319
    g80: LineSegment StartX=-770 StartY=-731.923 StartZ=0 EndX=-770 EndY=-761.673 EndZ=0
    g81: ArcOfCircle CenterX=-767.5 CenterY=-731.923 CenterZ=0 NormalX=0 NormalY=0 NormalZ=1 AngleXU=-1.5708 Radius=2.5 StartAngle=3.14159 EndAngle=4.71239
    g82: LineSegment StartX=-767.5 StartY=-729.423 StartZ=0 EndX=-755 EndY=-729.423 EndZ=0
    g83: ArcOfCircle CenterX=-755 CenterY=-716.798 CenterZ=0 NormalX=0 NormalY=0 NormalZ=1 AngleXU=-1.5708 Radius=12.625 StartAngle=4e-16 EndAngle=3.14159
    g84: LineSegment StartX=-767.5 StartY=-704.173 StartZ=0 EndX=-755 EndY=-704.173 EndZ=0
    g85: ArcOfCircle CenterX=-767.5 CenterY=-701.673 CenterZ=0 NormalX=0 NormalY=0 NormalZ=1 AngleXU=-1.5708 Radius=2.5 StartAngle=4.71239 EndAngle=6.28319
    g86: LineSegment StartX=-770 StartY=-692.598 StartZ=0 EndX=-770 EndY=-701.673 EndZ=0
    g87: LineSegment StartX=-774 StartY=-692.598 StartZ=0 EndX=-770 EndY=-692.598 EndZ=0
    g88: LineSegment StartX=-770 StartY=-600.904 StartZ=0 EndX=-774 EndY=-600.904 EndZ=0
    g89: LineSegment StartX=-770 StartY=-596.829 StartZ=0 EndX=-770 EndY=-600.904 EndZ=0
    g90: ArcOfCircle CenterX=-767.5 CenterY=-596.829 CenterZ=0 NormalX=0 NormalY=0 NormalZ=1 AngleXU=1.5708 Radius=2.5 StartAngle=2e-16 EndAngle=1.5708
    g91: LineSegment StartX=-767.5 StartY=-594.329 StartZ=0 EndX=-755 EndY=-594.329 EndZ=0
    g92: ArcOfCircle CenterX=-755 CenterY=-581.704 CenterZ=0 NormalX=0 NormalY=0 NormalZ=1 AngleXU=1.5708 Radius=12.625 StartAngle=3.14159 EndAngle=6.28319
    g93: LineSegment StartX=-767.5 StartY=-569.079 StartZ=0 EndX=-755 EndY=-569.079 EndZ=0
    g94: ArcOfCircle CenterX=-767.5 CenterY=-566.579 CenterZ=0 NormalX=0 NormalY=0 NormalZ=1 AngleXU=1.5708 Radius=2.5 StartAngle=1.5708 EndAngle=3.14159
    g95: LineSegment StartX=-770 StartY=-526.829 StartZ=0 EndX=-770 EndY=-566.579 EndZ=0
    g96: ArcOfCircle CenterX=-767.5 CenterY=-526.829 CenterZ=0 NormalX=0 NormalY=0 NormalZ=1 AngleXU=1.5708 Radius=2.5 StartAngle=2e-16 EndAngle=1.5708
    g97: LineSegment StartX=-774 StartY=-492.504 StartZ=0 EndX=-770 EndY=-492.504 EndZ=0
    g98: LineSegment StartX=-770 StartY=-492.504 StartZ=0 EndX=-770 EndY=-496.579 EndZ=0
    g99: ArcOfCircle CenterX=-767.5 CenterY=-496.579 CenterZ=0 NormalX=0 NormalY=0 NormalZ=1 AngleXU=1.5708 Radius=2.5 StartAngle=1.5708 EndAngle=3.14159
    g100: LineSegment StartX=-767.5 StartY=-499.079 StartZ=0 EndX=-755 EndY=-499.079 EndZ=0
    g101: ArcOfCircle CenterX=-755 CenterY=-511.704 CenterZ=0 NormalX=0 NormalY=0 NormalZ=1 AngleXU=1.5708 Radius=12.625 StartAngle=3.14159 EndAngle=6.28319
    g102: LineSegment StartX=-767.5 StartY=-524.329 StartZ=0 EndX=-755 EndY=-524.329 EndZ=0
    g103: LineSegment StartX=-774 StartY=-261.43 StartZ=0 EndX=-770 EndY=-261.43 EndZ=0
    g104: LineSegment StartX=-770 StartY=-261.43 StartZ=0 EndX=-770 EndY=-270.505 EndZ=0
    g105: ArcOfCircle CenterX=-767.5 CenterY=-270.505 CenterZ=0 NormalX=0 NormalY=0 NormalZ=1 AngleXU=-1.5708 Radius=2.5 StartAngle=4.71239 EndAngle=6.28319
    g106: LineSegment StartX=-767.5 StartY=-273.005 StartZ=0 EndX=-755 EndY=-273.005 EndZ=0
    g107: LineSegment StartX=-770 StartY=-369.83 StartZ=0 EndX=-774 EndY=-369.83 EndZ=0
    g108: LineSegment StartX=-770 StartY=-360.755 StartZ=0 EndX=-770 EndY=-369.83 EndZ=0
    g109: ArcOfCircle CenterX=-767.5 CenterY=-360.755 CenterZ=0 NormalX=0 NormalY=0 NormalZ=1 AngleXU=-1.5708 Radius=2.5 StartAngle=3.14159 EndAngle=4.71239
    g110: LineSegment StartX=-767.5 StartY=-358.255 StartZ=0 EndX=-755 EndY=-358.255 EndZ=0
    g111: ArcOfCircle CenterX=-755 CenterY=-345.63 CenterZ=0 NormalX=0 NormalY=0 NormalZ=1 AngleXU=-1.5708 Radius=12.625 StartAngle=0 EndAngle=3.14159
    g112: LineSegment StartX=-767.5 StartY=-333.005 StartZ=0 EndX=-755 EndY=-333.005 EndZ=0
    g113: ArcOfCircle CenterX=-767.5 CenterY=-330.505 CenterZ=0 NormalX=0 NormalY=0 NormalZ=1 AngleXU=-1.5708 Radius=2.5 StartAngle=4.71239 EndAngle=6.28319
    g114: LineSegment StartX=-770 StartY=-300.755 StartZ=0 EndX=-770 EndY=-330.505 EndZ=0
    g115: ArcOfCircle CenterX=-767.5 CenterY=-300.755 CenterZ=0 NormalX=0 NormalY=0 NormalZ=1 AngleXU=-1.5708 Radius=2.5 StartAngle=3.14159 EndAngle=4.71239
    g116: LineSegment StartX=-767.5 StartY=-298.255 StartZ=0 EndX=-755 EndY=-298.255 EndZ=0
    g117: ArcOfCircle CenterX=-755 CenterY=-285.63 CenterZ=0 NormalX=0 NormalY=0 NormalZ=1 AngleXU=-1.5708 Radius=12.625 StartAngle=0 EndAngle=3.14159
    g118: LineSegment StartX=-774 StartY=-61.3371 StartZ=0 EndX=-770 EndY=-61.3371 EndZ=0
    g119: LineSegment StartX=-770 StartY=-61.3371 StartZ=0 EndX=-770 EndY=-65.4121 EndZ=0
    g120: ArcOfCircle CenterX=-767.5 CenterY=-65.4121 CenterZ=0 NormalX=0 NormalY=0 NormalZ=1 AngleXU=1.5708 Radius=2.5 StartAngle=1.5708 EndAngle=3.14159
    g121: LineSegment StartX=-767.5 StartY=-67.9121 StartZ=0 EndX=-755 EndY=-67.9121 EndZ=0
    g122: LineSegment StartX=-770 StartY=-169.737 StartZ=0 EndX=-774 EndY=-169.737 EndZ=0
    g123: LineSegment StartX=-770 StartY=-165.662 StartZ=0 EndX=-770 EndY=-169.737 EndZ=0
    g124: ArcOfCircle CenterX=-767.5 CenterY=-165.662 CenterZ=0 NormalX=0 NormalY=0 NormalZ=1 AngleXU=1.5708 Radius=2.5 StartAngle=4e-16 EndAngle=1.5708
    g125: LineSegment StartX=-767.5 StartY=-163.162 StartZ=0 EndX=-755 EndY=-163.162 EndZ=0
    g126: ArcOfCircle CenterX=-755 CenterY=-150.537 CenterZ=0 NormalX=0 NormalY=0 NormalZ=1 AngleXU=1.5708 Radius=12.625 StartAngle=3.14159 EndAngle=6.28319
    g127: LineSegment StartX=-767.5 StartY=-137.912 StartZ=0 EndX=-755 EndY=-137.912 EndZ=0
    g128: ArcOfCircle CenterX=-767.5 CenterY=-135.412 CenterZ=0 NormalX=0 NormalY=0 NormalZ=1 AngleXU=1.5708 Radius=2.5 StartAngle=1.5708 EndAngle=3.14159
    g129: LineSegment StartX=-770 StartY=-95.6621 StartZ=0 EndX=-770 EndY=-135.412 EndZ=0
    g130: ArcOfCircle CenterX=-767.5 CenterY=-95.6621 CenterZ=0 NormalX=0 NormalY=0 NormalZ=1 AngleXU=1.5708 Radius=2.5 StartAngle=4e-16 EndAngle=1.5708
    g131: LineSegment StartX=-767.5 StartY=-93.1621 StartZ=0 EndX=-755 EndY=-93.1621 EndZ=0
    g132: ArcOfCircle CenterX=-755 CenterY=-80.5371 CenterZ=0 NormalX=0 NormalY=0 NormalZ=1 AngleXU=1.5708 Radius=12.625 StartAngle=3.14159 EndAngle=6.28319
    g133: LineSegment StartX=-770 StartY=61.3371 StartZ=0 EndX=-774 EndY=61.3371 EndZ=0
    g134: LineSegment StartX=-770 StartY=70.4121 StartZ=0 EndX=-770 EndY=61.3371 EndZ=0
    g135: ArcOfCircle CenterX=-767.5 CenterY=70.4121 CenterZ=0 NormalX=0 NormalY=0 NormalZ=1 AngleXU=-1.5708 Radius=2.5 StartAngle=3.14159 EndAngle=4.71239
    g136: LineSegment StartX=-767.5 StartY=72.9121 StartZ=0 EndX=-755 EndY=72.9121 EndZ=0
    g137: ArcOfCircle CenterX=-755 CenterY=85.5371 CenterZ=0 NormalX=0 NormalY=0 NormalZ=1 AngleXU=-1.5708 Radius=12.625 StartAngle=0 EndAngle=3.14159
    g138: LineSegment StartX=-767.5 StartY=98.1621 StartZ=0 EndX=-755 EndY=98.1621 EndZ=0
    g139: ArcOfCircle CenterX=-767.5 CenterY=100.662 CenterZ=0 NormalX=0 NormalY=0 NormalZ=1 AngleXU=-1.5708 Radius=2.5 StartAngle=4.71239 EndAngle=6.28319
    g140: LineSegment StartX=-770 StartY=130.412 StartZ=0 EndX=-770 EndY=100.662 EndZ=0
    g141: ArcOfCircle CenterX=-767.5 CenterY=130.412 CenterZ=0 NormalX=0 NormalY=0 NormalZ=1 AngleXU=-1.5708 Radius=2.5 StartAngle=3.14159 EndAngle=4.71239
    g142: LineSegment StartX=-767.5 StartY=132.912 StartZ=0 EndX=-755 EndY=132.912 EndZ=0
    g143: ArcOfCircle CenterX=-755 CenterY=145.537 CenterZ=0 NormalX=0 NormalY=0 NormalZ=1 AngleXU=-1.5708 Radius=12.625 StartAngle=0 EndAngle=3.14159
    g144: LineSegment StartX=-767.5 StartY=158.162 StartZ=0 EndX=-755 EndY=158.162 EndZ=0
    g145: ArcOfCircle CenterX=-767.5 CenterY=160.662 CenterZ=0 NormalX=0 NormalY=0 NormalZ=1 AngleXU=-1.5708 Radius=2.5 StartAngle=4.71239 EndAngle=6.28319
    g146: LineSegment StartX=-770 StartY=169.737 StartZ=0 EndX=-770 EndY=160.662 EndZ=0
    g147: LineSegment StartX=-157 StartY=149.775 StartZ=0 EndX=-157 EndY=151.675 EndZ=0
    g148: ArcOfCircle CenterX=-197 CenterY=149.775 CenterZ=0 NormalX=0 NormalY=0 NormalZ=1 AngleXU=-1.5708 Radius=40 StartAngle=1.5708 EndAngle=3.14159
    g149: LineSegment StartX=-212 StartY=189.775 StartZ=0 EndX=-197 EndY=189.775 EndZ=0
    g150: ArcOfCircle CenterX=-212 CenterY=194.775 CenterZ=0 NormalX=0 NormalY=0 NormalZ=1 AngleXU=-1.5708 Radius=5 StartAngle=4.71239 EndAngle=6.28319
    g151: LineSegment StartX=-217 StartY=215.352 StartZ=0 EndX=-217 EndY=194.775 EndZ=0
    g152: LineSegment StartX=-217 StartY=215.352 StartZ=0 EndX=-774 EndY=215.352 EndZ=0
    g153: LineSegment StartX=-774 StartY=169.737 StartZ=0 EndX=-774 EndY=215.352 EndZ=0
    g154: LineSegment StartX=-774 StartY=169.737 StartZ=0 EndX=-770 EndY=169.737 EndZ=0
    g155: ArcOfCircle CenterX=-126.802 CenterY=141.775 CenterZ=0 NormalX=0 NormalY=0 NormalZ=1 AngleXU=1.5708 Radius=10 StartAngle=4.71239 EndAngle=6.14165
    g156: LineSegment StartX=-116.802 StartY=68.7747 StartZ=0 EndX=-116.802 EndY=141.775 EndZ=0
    g157: ArcOfCircle CenterX=-126.802 CenterY=68.7747 CenterZ=0 NormalX=0 NormalY=0 NormalZ=1 AngleXU=1.5708 Radius=10 StartAngle=3.28313 EndAngle=4.71239
    g158: LineSegment StartX=-118.231 StartY=45.4947 StartZ=0 EndX=-1.42e-14 EndY=75.5371 EndZ=0
    g159: ArcOfCircle CenterX=-117 CenterY=40.6487 CenterZ=0 NormalX=0 NormalY=0 NormalZ=1 AngleXU=-1.5708 Radius=5 StartAngle=3.39042 EndAngle=4.71239
    g160: LineSegment StartX=-122 StartY=36.5371 StartZ=0 EndX=-122 EndY=40.6487 EndZ=0
    g161: ArcOfCircle CenterX=-127 CenterY=36.5371 CenterZ=0 NormalX=0 NormalY=0 NormalZ=1 AngleXU=-1.5708 Radius=5 StartAngle=0 EndAngle=1.5708
    g162: LineSegment StartX=-152 StartY=31.5371 StartZ=0 EndX=-127 EndY=31.5371 EndZ=0
    g163: ArcOfCircle CenterX=-152 CenterY=36.5371 CenterZ=0 NormalX=0 NormalY=0 NormalZ=1 AngleXU=-1.5708 Radius=5 StartAngle=4.71239 EndAngle=6.28319
    g164: LineSegment StartX=-157 StartY=58.8747 StartZ=0 EndX=-157 EndY=36.5371 EndZ=0
    g165: LineSegment StartX=-157 StartY=-58.8747 StartZ=0 EndX=-157 EndY=-46.0751 EndZ=0
    g166: ArcOfCircle CenterX=-152 CenterY=-46.0751 CenterZ=0 NormalX=0 NormalY=0 NormalZ=1 AngleXU=1.5708 Radius=5 StartAngle=0 EndAngle=1.5708
    g167: LineSegment StartX=-152 StartY=-41.0751 StartZ=0 EndX=-127 EndY=-41.0751 EndZ=0
    g168: ArcOfCircle CenterX=-127 CenterY=-46.0751 CenterZ=0 NormalX=0 NormalY=0 NormalZ=1 AngleXU=1.5708 Radius=5 StartAngle=4.71239 EndAngle=6.28319
    g169: LineSegment StartX=-122 StartY=-46.0751 StartZ=0 EndX=-122 EndY=-50.1869 EndZ=0
    g170: ArcOfCircle CenterX=-117 CenterY=-50.1869 CenterZ=0 NormalX=0 NormalY=0 NormalZ=1 AngleXU=1.5708 Radius=5 StartAngle=1.5708 EndAngle=2.89271
    g171: LineSegment StartX=-118.232 StartY=-55.0329 StartZ=0 EndX=0 EndY=-85.0818 EndZ=0
    g172: ArcOfCircle CenterX=-126.802 CenterY=-68.7747 CenterZ=0 NormalX=0 NormalY=0 NormalZ=1 AngleXU=-1.5708 Radius=10 StartAngle=1.5708 EndAngle=3.00005
    g173: LineSegment StartX=-116.802 StartY=-141.775 StartZ=0 EndX=-116.802 EndY=-68.7747 EndZ=0
    g174: ArcOfCircle CenterX=-126.802 CenterY=-141.775 CenterZ=0 NormalX=0 NormalY=0 NormalZ=1 AngleXU=-1.5708 Radius=10 StartAngle=0.141539 EndAngle=1.5708
    g175: Circle CenterX=-25 CenterY=-862.335 CenterZ=0 NormalX=0 NormalY=0 NormalZ=1 AngleXU=1.5708 Radius=7
    g176: Circle CenterX=-25 CenterY=-431.167 CenterZ=0 NormalX=0 NormalY=0 NormalZ=1 AngleXU=1.5708 Radius=7
    g177: Circle CenterX=-25 CenterY=0 CenterZ=0 NormalX=0 NormalY=0 NormalZ=1 AngleXU=1.5708 Radius=7
    g178: LineSegment StartX=-334.5 StartY=-687.298 StartZ=0 EndX=-334.5 EndY=-674.298 EndZ=0
    g179: LineSegment StartX=-341.5 StartY=-687.298 StartZ=0 EndX=-334.5 EndY=-687.298 EndZ=0
    g180: LineSegment StartX=-334.5 StartY=-674.298 StartZ=0 EndX=-341.5 EndY=-674.298 EndZ=0
    g181: LineSegment StartX=-341.5 StartY=-674.298 StartZ=0 EndX=-341.5 EndY=-687.298 EndZ=0
    g182: LineSegment StartX=-574.5 StartY=-819.298 StartZ=0 EndX=-574.5 EndY=-806.298 EndZ=0
    g183: LineSegment StartX=-581.5 StartY=-819.298 StartZ=0 EndX=-574.5 EndY=-819.298 EndZ=0
    g184: LineSegment StartX=-574.5 StartY=-806.298 StartZ=0 EndX=-581.5 EndY=-806.298 EndZ=0
    g185: LineSegment StartX=-581.5 StartY=-806.298 StartZ=0 EndX=-581.5 EndY=-819.298 EndZ=0
    g186: LineSegment StartX=-574.5 StartY=-905.372 StartZ=0 EndX=-574.5 EndY=-918.372 EndZ=0
    g187: LineSegment StartX=-581.5 StartY=-905.372 StartZ=0 EndX=-574.5 EndY=-905.372 EndZ=0
    g188: LineSegment StartX=-574.5 StartY=-918.372 StartZ=0 EndX=-581.5 EndY=-918.372 EndZ=0
    g189: LineSegment StartX=-581.5 StartY=-918.372 StartZ=0 EndX=-581.5 EndY=-905.372 EndZ=0
    g190: LineSegment StartX=-654.5 StartY=-905.372 StartZ=0 EndX=-654.5 EndY=-918.372 EndZ=0
    g191: LineSegment StartX=-661.5 StartY=-905.372 StartZ=0 EndX=-654.5 EndY=-905.372 EndZ=0
    g192: LineSegment StartX=-654.5 StartY=-918.372 StartZ=0 EndX=-661.5 EndY=-918.372 EndZ=0
    g193: LineSegment StartX=-661.5 StartY=-918.372 StartZ=0 EndX=-661.5 EndY=-905.372 EndZ=0
    g194: LineSegment StartX=-414.5 StartY=-1037.37 StartZ=0 EndX=-414.5 EndY=-1050.37 EndZ=0
    g195: LineSegment StartX=-421.5 StartY=-1037.37 StartZ=0 EndX=-414.5 EndY=-1037.37 EndZ=0
    g196: LineSegment StartX=-414.5 StartY=-1050.37 StartZ=0 EndX=-421.5 EndY=-1050.37 EndZ=0
    g197: LineSegment StartX=-421.5 StartY=-1050.37 StartZ=0 EndX=-421.5 EndY=-1037.37 EndZ=0
    g198: LineSegment StartX=-414.5 StartY=-687.298 StartZ=0 EndX=-414.5 EndY=-674.298 EndZ=0
    g199: LineSegment StartX=-421.5 StartY=-687.298 StartZ=0 EndX=-414.5 EndY=-687.298 EndZ=0
    g200: LineSegment StartX=-414.5 StartY=-674.298 StartZ=0 EndX=-421.5 EndY=-674.298 EndZ=0
    g201: LineSegment StartX=-421.5 StartY=-674.298 StartZ=0 EndX=-421.5 EndY=-687.298 EndZ=0
    g202: LineSegment StartX=-494.5 StartY=-1037.37 StartZ=0 EndX=-494.5 EndY=-1050.37 EndZ=0
    g203: LineSegment StartX=-501.5 StartY=-1037.37 StartZ=0 EndX=-494.5 EndY=-1037.37 EndZ=0
    g204: LineSegment StartX=-494.5 StartY=-1050.37 StartZ=0 EndX=-501.5 EndY=-1050.37 EndZ=0
    g205: LineSegment StartX=-501.5 StartY=-1050.37 StartZ=0 EndX=-501.5 EndY=-1037.37 EndZ=0
    g206: LineSegment StartX=-414.5 StartY=-905.372 StartZ=0 EndX=-414.5 EndY=-918.372 EndZ=0
    g207: LineSegment StartX=-421.5 StartY=-905.372 StartZ=0 EndX=-414.5 EndY=-905.372 EndZ=0
    g208: LineSegment StartX=-414.5 StartY=-918.372 StartZ=0 EndX=-421.5 EndY=-918.372 EndZ=0
    g209: LineSegment StartX=-421.5 StartY=-918.372 StartZ=0 EndX=-421.5 EndY=-905.372 EndZ=0
    g210: LineSegment StartX=-501.5 StartY=-606.204 StartZ=0 EndX=-501.5 EndY=-619.204 EndZ=0
    g211: LineSegment StartX=-494.5 StartY=-606.204 StartZ=0 EndX=-501.5 EndY=-606.204 EndZ=0
    g212: LineSegment StartX=-501.5 StartY=-619.204 StartZ=0 EndX=-494.5 EndY=-619.204 EndZ=0
    g213: LineSegment StartX=-494.5 StartY=-619.204 StartZ=0 EndX=-494.5 EndY=-606.204 EndZ=0
    g214: LineSegment StartX=-421.5 StartY=-606.204 StartZ=0 EndX=-421.5 EndY=-619.204 EndZ=0
    g215: LineSegment StartX=-414.5 StartY=-606.204 StartZ=0 EndX=-421.5 EndY=-606.204 EndZ=0
    g216: LineSegment StartX=-421.5 StartY=-619.204 StartZ=0 EndX=-414.5 EndY=-619.204 EndZ=0
    g217: LineSegment StartX=-414.5 StartY=-619.204 StartZ=0 EndX=-414.5 EndY=-606.204 EndZ=0
    g218: LineSegment StartX=-341.5 StartY=-606.204 StartZ=0 EndX=-341.5 EndY=-619.204 EndZ=0
    g219: LineSegment StartX=-334.5 StartY=-606.204 StartZ=0 EndX=-341.5 EndY=-606.204 EndZ=0
    g220: LineSegment StartX=-341.5 StartY=-619.204 StartZ=0 EndX=-334.5 EndY=-619.204 EndZ=0
    g221: LineSegment StartX=-334.5 StartY=-619.204 StartZ=0 EndX=-334.5 EndY=-606.204 EndZ=0
    g222: LineSegment StartX=-334.5 StartY=-819.298 StartZ=0 EndX=-334.5 EndY=-806.298 EndZ=0
    g223: LineSegment StartX=-341.5 StartY=-819.298 StartZ=0 EndX=-334.5 EndY=-819.298 EndZ=0
    g224: LineSegment StartX=-334.5 StartY=-806.298 StartZ=0 EndX=-341.5 EndY=-806.298 EndZ=0
    g225: LineSegment StartX=-341.5 StartY=-806.298 StartZ=0 EndX=-341.5 EndY=-819.298 EndZ=0
    g226: LineSegment StartX=-494.5 StartY=-819.298 StartZ=0 EndX=-494.5 EndY=-806.298 EndZ=0
    g227: LineSegment StartX=-501.5 StartY=-819.298 StartZ=0 EndX=-494.5 EndY=-819.298 EndZ=0
    g228: LineSegment StartX=-494.5 StartY=-806.298 StartZ=0 EndX=-501.5 EndY=-806.298 EndZ=0
    g229: LineSegment StartX=-501.5 StartY=-806.298 StartZ=0 EndX=-501.5 EndY=-819.298 EndZ=0
    g230: LineSegment StartX=-414.5 StartY=-819.298 StartZ=0 EndX=-414.5 EndY=-806.298 EndZ=0
    g231: LineSegment StartX=-421.5 StartY=-819.298 StartZ=0 EndX=-414.5 EndY=-819.298 EndZ=0
    g232: LineSegment StartX=-414.5 StartY=-806.298 StartZ=0 EndX=-421.5 EndY=-806.298 EndZ=0
    g233: LineSegment StartX=-421.5 StartY=-806.298 StartZ=0 EndX=-421.5 EndY=-819.298 EndZ=0
    g234: LineSegment StartX=-494.5 StartY=-687.298 StartZ=0 EndX=-494.5 EndY=-674.298 EndZ=0
    g235: LineSegment StartX=-501.5 StartY=-687.298 StartZ=0 EndX=-494.5 EndY=-687.298 EndZ=0
    g236: LineSegment StartX=-494.5 StartY=-674.298 StartZ=0 EndX=-501.5 EndY=-674.298 EndZ=0
    g237: LineSegment StartX=-501.5 StartY=-674.298 StartZ=0 EndX=-501.5 EndY=-687.298 EndZ=0
    g238: LineSegment StartX=-334.5 StartY=-905.372 StartZ=0 EndX=-334.5 EndY=-918.372 EndZ=0
    g239: LineSegment StartX=-341.5 StartY=-905.372 StartZ=0 EndX=-334.5 EndY=-905.372 EndZ=0
    g240: LineSegment StartX=-334.5 StartY=-918.372 StartZ=0 EndX=-341.5 EndY=-918.372 EndZ=0
    g241: LineSegment StartX=-341.5 StartY=-918.372 StartZ=0 EndX=-341.5 EndY=-905.372 EndZ=0
    g242: LineSegment StartX=-334.5 StartY=-1037.37 StartZ=0 EndX=-334.5 EndY=-1050.37 EndZ=0
    g243: LineSegment StartX=-341.5 StartY=-1037.37 StartZ=0 EndX=-334.5 EndY=-1037.37 EndZ=0
    g244: LineSegment StartX=-334.5 StartY=-1050.37 StartZ=0 EndX=-341.5 EndY=-1050.37 EndZ=0
    g245: LineSegment StartX=-341.5 StartY=-1050.37 StartZ=0 EndX=-341.5 EndY=-1037.37 EndZ=0
    g246: LineSegment StartX=-654.5 StartY=-819.298 StartZ=0 EndX=-654.5 EndY=-806.298 EndZ=0
    g247: LineSegment StartX=-661.5 StartY=-819.298 StartZ=0 EndX=-654.5 EndY=-819.298 EndZ=0
    g248: LineSegment StartX=-654.5 StartY=-806.298 StartZ=0 EndX=-661.5 EndY=-806.298 EndZ=0
    g249: LineSegment StartX=-661.5 StartY=-806.298 StartZ=0 EndX=-661.5 EndY=-819.298 EndZ=0
    g250: LineSegment StartX=-734.5 StartY=-819.298 StartZ=0 EndX=-734.5 EndY=-806.298 EndZ=0
    g251: LineSegment StartX=-741.5 StartY=-819.298 StartZ=0 EndX=-734.5 EndY=-819.298 EndZ=0
    g252: LineSegment StartX=-734.5 StartY=-806.298 StartZ=0 EndX=-741.5 EndY=-806.298 EndZ=0
    g253: LineSegment StartX=-741.5 StartY=-806.298 StartZ=0 EndX=-741.5 EndY=-819.298 EndZ=0
    g254: LineSegment StartX=-734.5 StartY=-905.372 StartZ=0 EndX=-734.5 EndY=-918.372 EndZ=0
    g255: LineSegment StartX=-741.5 StartY=-905.372 StartZ=0 EndX=-734.5 EndY=-905.372 EndZ=0
    g256: LineSegment StartX=-734.5 StartY=-918.372 StartZ=0 EndX=-741.5 EndY=-918.372 EndZ=0
    g257: LineSegment StartX=-741.5 StartY=-918.372 StartZ=0 EndX=-741.5 EndY=-905.372 EndZ=0
    g258: LineSegment StartX=-581.5 StartY=-43.0371 StartZ=0 EndX=-581.5 EndY=-56.0371 EndZ=0
    g259: LineSegment StartX=-574.5 StartY=-43.0371 StartZ=0 EndX=-581.5 EndY=-43.0371 EndZ=0
    g260: LineSegment StartX=-581.5 StartY=-56.0371 StartZ=0 EndX=-574.5 EndY=-56.0371 EndZ=0
    g261: LineSegment StartX=-574.5 StartY=-56.0371 StartZ=0 EndX=-574.5 EndY=-43.0371 EndZ=0
    g262: LineSegment StartX=-741.5 StartY=-175.037 StartZ=0 EndX=-741.5 EndY=-188.037 EndZ=0
    g263: LineSegment StartX=-734.5 StartY=-175.037 StartZ=0 EndX=-741.5 EndY=-175.037 EndZ=0
    g264: LineSegment StartX=-741.5 StartY=-188.037 StartZ=0 EndX=-734.5 EndY=-188.037 EndZ=0
    g265: LineSegment StartX=-734.5 StartY=-188.037 StartZ=0 EndX=-734.5 EndY=-175.037 EndZ=0
    g266: LineSegment StartX=-581.5 StartY=-175.037 StartZ=0 EndX=-581.5 EndY=-188.037 EndZ=0
    g267: LineSegment StartX=-574.5 StartY=-175.037 StartZ=0 EndX=-581.5 EndY=-175.037 EndZ=0
    g268: LineSegment StartX=-581.5 StartY=-188.037 StartZ=0 EndX=-574.5 EndY=-188.037 EndZ=0
    g269: LineSegment StartX=-574.5 StartY=-188.037 StartZ=0 EndX=-574.5 EndY=-175.037 EndZ=0
    g270: LineSegment StartX=-741.5 StartY=-43.0371 StartZ=0 EndX=-741.5 EndY=-56.0371 EndZ=0
    g271: LineSegment StartX=-734.5 StartY=-43.0371 StartZ=0 EndX=-741.5 EndY=-43.0371 EndZ=0
    g272: LineSegment StartX=-741.5 StartY=-56.0371 StartZ=0 EndX=-734.5 EndY=-56.0371 EndZ=0
    g273: LineSegment StartX=-734.5 StartY=-56.0371 StartZ=0 EndX=-734.5 EndY=-43.0371 EndZ=0
    g274: LineSegment StartX=-661.5 StartY=-43.0371 StartZ=0 EndX=-661.5 EndY=-56.0371 EndZ=0
    g275: LineSegment StartX=-654.5 StartY=-43.0371 StartZ=0 EndX=-661.5 EndY=-43.0371 EndZ=0
    g276: LineSegment StartX=-661.5 StartY=-56.0371 StartZ=0 EndX=-654.5 EndY=-56.0371 EndZ=0
    g277: LineSegment StartX=-654.5 StartY=-56.0371 StartZ=0 EndX=-654.5 EndY=-43.0371 EndZ=0
    g278: LineSegment StartX=-734.5 StartY=175.037 StartZ=0 EndX=-734.5 EndY=188.037 EndZ=0
    g279: LineSegment StartX=-741.5 StartY=175.037 StartZ=0 EndX=-734.5 EndY=175.037 EndZ=0
    g280: LineSegment StartX=-734.5 StartY=188.037 StartZ=0 EndX=-741.5 EndY=188.037 EndZ=0
    g281: LineSegment StartX=-741.5 StartY=188.037 StartZ=0 EndX=-741.5 EndY=175.037 EndZ=0
    g282: LineSegment StartX=-654.5 StartY=175.037 StartZ=0 EndX=-654.5 EndY=188.037 EndZ=0
    g283: LineSegment StartX=-661.5 StartY=175.037 StartZ=0 EndX=-654.5 EndY=175.037 EndZ=0
    g284: LineSegment StartX=-654.5 StartY=188.037 StartZ=0 EndX=-661.5 EndY=188.037 EndZ=0
    g285: LineSegment StartX=-661.5 StartY=188.037 StartZ=0 EndX=-661.5 EndY=175.037 EndZ=0
    g286: LineSegment StartX=-574.5 StartY=175.037 StartZ=0 EndX=-574.5 EndY=188.037 EndZ=0
    g287: LineSegment StartX=-581.5 StartY=175.037 StartZ=0 EndX=-574.5 EndY=175.037 EndZ=0
    g288: LineSegment StartX=-574.5 StartY=188.037 StartZ=0 EndX=-581.5 EndY=188.037 EndZ=0
    g289: LineSegment StartX=-581.5 StartY=188.037 StartZ=0 EndX=-581.5 EndY=175.037 EndZ=0
    g290: LineSegment StartX=-734.5 StartY=-256.13 StartZ=0 EndX=-734.5 EndY=-243.13 EndZ=0
    g291: LineSegment StartX=-741.5 StartY=-256.13 StartZ=0 EndX=-734.5 EndY=-256.13 EndZ=0
    g292: LineSegment StartX=-734.5 StartY=-243.13 StartZ=0 EndX=-741.5 EndY=-243.13 EndZ=0
    g293: LineSegment StartX=-741.5 StartY=-243.13 StartZ=0 EndX=-741.5 EndY=-256.13 EndZ=0
    g294: LineSegment StartX=-341.5 StartY=-474.204 StartZ=0 EndX=-341.5 EndY=-487.204 EndZ=0
    g295: LineSegment StartX=-334.5 StartY=-474.204 StartZ=0 EndX=-341.5 EndY=-474.204 EndZ=0
    g296: LineSegment StartX=-341.5 StartY=-487.204 StartZ=0 EndX=-334.5 EndY=-487.204 EndZ=0
    g297: LineSegment StartX=-334.5 StartY=-487.204 StartZ=0 EndX=-334.5 EndY=-474.204 EndZ=0
    g298: LineSegment StartX=-654.5 StartY=-388.13 StartZ=0 EndX=-654.5 EndY=-375.13 EndZ=0
    g299: LineSegment StartX=-661.5 StartY=-388.13 StartZ=0 EndX=-654.5 EndY=-388.13 EndZ=0
    g300: LineSegment StartX=-654.5 StartY=-375.13 StartZ=0 EndX=-661.5 EndY=-375.13 EndZ=0
    g301: LineSegment StartX=-661.5 StartY=-375.13 StartZ=0 EndX=-661.5 EndY=-388.13 EndZ=0
    g302: LineSegment StartX=-421.5 StartY=-474.204 StartZ=0 EndX=-421.5 EndY=-487.204 EndZ=0
    g303: LineSegment StartX=-414.5 StartY=-474.204 StartZ=0 EndX=-421.5 EndY=-474.204 EndZ=0
    g304: LineSegment StartX=-421.5 StartY=-487.204 StartZ=0 EndX=-414.5 EndY=-487.204 EndZ=0
    g305: LineSegment StartX=-414.5 StartY=-487.204 StartZ=0 EndX=-414.5 EndY=-474.204 EndZ=0
    g306: LineSegment StartX=-581.5 StartY=-474.204 StartZ=0 EndX=-581.5 EndY=-487.204 EndZ=0
    g307: LineSegment StartX=-574.5 StartY=-474.204 StartZ=0 EndX=-581.5 EndY=-474.204 EndZ=0
    g308: LineSegment StartX=-581.5 StartY=-487.204 StartZ=0 EndX=-574.5 EndY=-487.204 EndZ=0
    g309: LineSegment StartX=-574.5 StartY=-487.204 StartZ=0 EndX=-574.5 EndY=-474.204 EndZ=0
    g310: LineSegment StartX=-661.5 StartY=-474.204 StartZ=0 EndX=-661.5 EndY=-487.204 EndZ=0
    g311: LineSegment StartX=-654.5 StartY=-474.204 StartZ=0 EndX=-661.5 EndY=-474.204 EndZ=0
    g312: LineSegment StartX=-661.5 StartY=-487.204 StartZ=0 EndX=-654.5 EndY=-487.204 EndZ=0
    g313: LineSegment StartX=-654.5 StartY=-487.204 StartZ=0 EndX=-654.5 EndY=-474.204 EndZ=0
    g314: LineSegment StartX=-741.5 StartY=-474.204 StartZ=0 EndX=-741.5 EndY=-487.204 EndZ=0
    g315: LineSegment StartX=-734.5 StartY=-474.204 StartZ=0 EndX=-741.5 EndY=-474.204 EndZ=0
    g316: LineSegment StartX=-741.5 StartY=-487.204 StartZ=0 EndX=-734.5 EndY=-487.204 EndZ=0
    g317: LineSegment StartX=-734.5 StartY=-487.204 StartZ=0 EndX=-734.5 EndY=-474.204 EndZ=0
    g318: LineSegment StartX=-734.5 StartY=-1037.37 StartZ=0 EndX=-734.5 EndY=-1050.37 EndZ=0
    g319: LineSegment StartX=-741.5 StartY=-1037.37 StartZ=0 EndX=-734.5 EndY=-1037.37 EndZ=0
    g320: LineSegment StartX=-734.5 StartY=-1050.37 StartZ=0 EndX=-741.5 EndY=-1050.37 EndZ=0
    g321: LineSegment StartX=-741.5 StartY=-1050.37 StartZ=0 EndX=-741.5 EndY=-1037.37 EndZ=0
    g322: LineSegment StartX=-581.5 StartY=-606.204 StartZ=0 EndX=-581.5 EndY=-619.204 EndZ=0
    g323: LineSegment StartX=-574.5 StartY=-606.204 StartZ=0 EndX=-581.5 EndY=-606.204 EndZ=0
    g324: LineSegment StartX=-581.5 StartY=-619.204 StartZ=0 EndX=-574.5 EndY=-619.204 EndZ=0
    g325: LineSegment StartX=-574.5 StartY=-619.204 StartZ=0 EndX=-574.5 EndY=-606.204 EndZ=0
    g326: LineSegment StartX=-654.5 StartY=-1037.37 StartZ=0 EndX=-654.5 EndY=-1050.37 EndZ=0
    g327: LineSegment StartX=-661.5 StartY=-1037.37 StartZ=0 EndX=-654.5 EndY=-1037.37 EndZ=0
    g328: LineSegment StartX=-654.5 StartY=-1050.37 StartZ=0 EndX=-661.5 EndY=-1050.37 EndZ=0
    g329: LineSegment StartX=-661.5 StartY=-1050.37 StartZ=0 EndX=-661.5 EndY=-1037.37 EndZ=0
    g330: LineSegment StartX=-574.5 StartY=-1037.37 StartZ=0 EndX=-574.5 EndY=-1050.37 EndZ=0
    g331: LineSegment StartX=-581.5 StartY=-1037.37 StartZ=0 EndX=-574.5 EndY=-1037.37 EndZ=0
    g332: LineSegment StartX=-574.5 StartY=-1050.37 StartZ=0 EndX=-581.5 EndY=-1050.37 EndZ=0
    g333: LineSegment StartX=-581.5 StartY=-1050.37 StartZ=0 EndX=-581.5 EndY=-1037.37 EndZ=0
    g334: LineSegment StartX=-741.5 StartY=-606.204 StartZ=0 EndX=-741.5 EndY=-619.204 EndZ=0
    g335: LineSegment StartX=-734.5 StartY=-606.204 StartZ=0 EndX=-741.5 EndY=-606.204 EndZ=0
    g336: LineSegment StartX=-741.5 StartY=-619.204 StartZ=0 EndX=-734.5 EndY=-619.204 EndZ=0
    g337: LineSegment StartX=-734.5 StartY=-619.204 StartZ=0 EndX=-734.5 EndY=-606.204 EndZ=0
    g338: LineSegment StartX=-574.5 StartY=-687.298 StartZ=0 EndX=-574.5 EndY=-674.298 EndZ=0
    g339: LineSegment StartX=-581.5 StartY=-687.298 StartZ=0 EndX=-574.5 EndY=-687.298 EndZ=0
    g340: LineSegment StartX=-574.5 StartY=-674.298 StartZ=0 EndX=-581.5 EndY=-674.298 EndZ=0
    g341: LineSegment StartX=-581.5 StartY=-674.298 StartZ=0 EndX=-581.5 EndY=-687.298 EndZ=0
    g342: LineSegment StartX=-654.5 StartY=-687.298 StartZ=0 EndX=-654.5 EndY=-674.298 EndZ=0
    g343: LineSegment StartX=-661.5 StartY=-687.298 StartZ=0 EndX=-654.5 EndY=-687.298 EndZ=0
    g344: LineSegment StartX=-654.5 StartY=-674.298 StartZ=0 EndX=-661.5 EndY=-674.298 EndZ=0
    g345: LineSegment StartX=-661.5 StartY=-674.298 StartZ=0 EndX=-661.5 EndY=-687.298 EndZ=0
    g346: LineSegment StartX=-334.5 StartY=-388.13 StartZ=0 EndX=-334.5 EndY=-375.13 EndZ=0
    g347: LineSegment StartX=-341.5 StartY=-388.13 StartZ=0 EndX=-334.5 EndY=-388.13 EndZ=0
    g348: LineSegment StartX=-334.5 StartY=-375.13 StartZ=0 EndX=-341.5 EndY=-375.13 EndZ=0
    g349: LineSegment StartX=-341.5 StartY=-375.13 StartZ=0 EndX=-341.5 EndY=-388.13 EndZ=0
    g350: LineSegment StartX=-574.5 StartY=43.0371 StartZ=0 EndX=-574.5 EndY=56.0371 EndZ=0
    g351: LineSegment StartX=-581.5 StartY=43.0371 StartZ=0 EndX=-574.5 EndY=43.0371 EndZ=0
    g352: LineSegment StartX=-574.5 StartY=56.0371 StartZ=0 EndX=-581.5 EndY=56.0371 EndZ=0
    g353: LineSegment StartX=-581.5 StartY=56.0371 StartZ=0 EndX=-581.5 EndY=43.0371 EndZ=0
    g354: LineSegment StartX=-654.5 StartY=43.0371 StartZ=0 EndX=-654.5 EndY=56.0371 EndZ=0
    g355: LineSegment StartX=-661.5 StartY=43.0371 StartZ=0 EndX=-654.5 EndY=43.0371 EndZ=0
    g356: LineSegment StartX=-654.5 StartY=56.0371 StartZ=0 EndX=-661.5 EndY=56.0371 EndZ=0
    g357: LineSegment StartX=-661.5 StartY=56.0371 StartZ=0 EndX=-661.5 EndY=43.0371 EndZ=0
    g358: LineSegment StartX=-734.5 StartY=43.0371 StartZ=0 EndX=-734.5 EndY=56.0371 EndZ=0
    g359: LineSegment StartX=-741.5 StartY=43.0371 StartZ=0 EndX=-734.5 EndY=43.0371 EndZ=0
    g360: LineSegment StartX=-734.5 StartY=56.0371 StartZ=0 EndX=-741.5 EndY=56.0371 EndZ=0
    g361: LineSegment StartX=-741.5 StartY=56.0371 StartZ=0 EndX=-741.5 EndY=43.0371 EndZ=0
    g362: LineSegment StartX=-661.5 StartY=-175.037 StartZ=0 EndX=-661.5 EndY=-188.037 EndZ=0
    g363: LineSegment StartX=-654.5 StartY=-175.037 StartZ=0 EndX=-661.5 EndY=-175.037 EndZ=0
    g364: LineSegment StartX=-661.5 StartY=-188.037 StartZ=0 EndX=-654.5 EndY=-188.037 EndZ=0
    g365: LineSegment StartX=-654.5 StartY=-188.037 StartZ=0 EndX=-654.5 EndY=-175.037 EndZ=0
    g366: LineSegment StartX=-501.5 StartY=-175.037 StartZ=0 EndX=-501.5 EndY=-188.037 EndZ=0
    g367: LineSegment StartX=-494.5 StartY=-175.037 StartZ=0 EndX=-501.5 EndY=-175.037 EndZ=0
    g368: LineSegment StartX=-501.5 StartY=-188.037 StartZ=0 EndX=-494.5 EndY=-188.037 EndZ=0
    g369: LineSegment StartX=-494.5 StartY=-188.037 StartZ=0 EndX=-494.5 EndY=-175.037 EndZ=0
    g370: LineSegment StartX=-421.5 StartY=-175.037 StartZ=0 EndX=-421.5 EndY=-188.037 EndZ=0
    g371: LineSegment StartX=-414.5 StartY=-175.037 StartZ=0 EndX=-421.5 EndY=-175.037 EndZ=0
    g372: LineSegment StartX=-421.5 StartY=-188.037 StartZ=0 EndX=-414.5 EndY=-188.037 EndZ=0
    g373: LineSegment StartX=-414.5 StartY=-188.037 StartZ=0 EndX=-414.5 EndY=-175.037 EndZ=0
    g374: LineSegment StartX=-494.5 StartY=-256.13 StartZ=0 EndX=-494.5 EndY=-243.13 EndZ=0
    g375: LineSegment StartX=-501.5 StartY=-256.13 StartZ=0 EndX=-494.5 EndY=-256.13 EndZ=0
    g376: LineSegment StartX=-494.5 StartY=-243.13 StartZ=0 EndX=-501.5 EndY=-243.13 EndZ=0
    g377: LineSegment StartX=-501.5 StartY=-243.13 StartZ=0 EndX=-501.5 EndY=-256.13 EndZ=0
    g378: LineSegment StartX=-414.5 StartY=-256.13 StartZ=0 EndX=-414.5 EndY=-243.13 EndZ=0
    g379: LineSegment StartX=-421.5 StartY=-256.13 StartZ=0 EndX=-414.5 EndY=-256.13 EndZ=0
    g380: LineSegment StartX=-414.5 StartY=-243.13 StartZ=0 EndX=-421.5 EndY=-243.13 EndZ=0
    g381: LineSegment StartX=-421.5 StartY=-243.13 StartZ=0 EndX=-421.5 EndY=-256.13 EndZ=0
    g382: LineSegment StartX=-334.5 StartY=175.037 StartZ=0 EndX=-334.5 EndY=188.037 EndZ=0
    g383: LineSegment StartX=-341.5 StartY=175.037 StartZ=0 EndX=-334.5 EndY=175.037 EndZ=0
    g384: LineSegment StartX=-334.5 StartY=188.037 StartZ=0 EndX=-341.5 EndY=188.037 EndZ=0
    g385: LineSegment StartX=-341.5 StartY=188.037 StartZ=0 EndX=-341.5 EndY=175.037 EndZ=0
    g386: LineSegment StartX=-494.5 StartY=175.037 StartZ=0 EndX=-494.5 EndY=188.037 EndZ=0
    g387: LineSegment StartX=-501.5 StartY=175.037 StartZ=0 EndX=-494.5 EndY=175.037 EndZ=0
    g388: LineSegment StartX=-494.5 StartY=188.037 StartZ=0 EndX=-501.5 EndY=188.037 EndZ=0
    g389: LineSegment StartX=-501.5 StartY=188.037 StartZ=0 EndX=-501.5 EndY=175.037 EndZ=0
    g390: LineSegment StartX=-341.5 StartY=-43.0371 StartZ=0 EndX=-341.5 EndY=-56.0371 EndZ=0
    g391: LineSegment StartX=-334.5 StartY=-43.0371 StartZ=0 EndX=-341.5 EndY=-43.0371 EndZ=0
    g392: LineSegment StartX=-341.5 StartY=-56.0371 StartZ=0 EndX=-334.5 EndY=-56.0371 EndZ=0
    g393: LineSegment StartX=-334.5 StartY=-56.0371 StartZ=0 EndX=-334.5 EndY=-43.0371 EndZ=0
    g394: LineSegment StartX=-341.5 StartY=-175.037 StartZ=0 EndX=-341.5 EndY=-188.037 EndZ=0
    g395: LineSegment StartX=-334.5 StartY=-175.037 StartZ=0 EndX=-341.5 EndY=-175.037 EndZ=0
    g396: LineSegment StartX=-341.5 StartY=-188.037 StartZ=0 EndX=-334.5 EndY=-188.037 EndZ=0
    g397: LineSegment StartX=-334.5 StartY=-188.037 StartZ=0 EndX=-334.5 EndY=-175.037 EndZ=0
    g398: LineSegment StartX=-414.5 StartY=175.037 StartZ=0 EndX=-414.5 EndY=188.037 EndZ=0
    g399: LineSegment StartX=-421.5 StartY=175.037 StartZ=0 EndX=-414.5 EndY=175.037 EndZ=0
    ... +170 more geometry lines
FEATURE [Sketcher::SketchObject] Unfold_Sketch_Outline
  FullyConstrained = true
FEATURE [Sketcher::SketchObject] Unfold_Sketch_bends017
  FullyConstrained = false
  sketch-geometry (15):
    g0: LineSegment StartX=-156.851 StartY=-58.8747 StartZ=0 EndX=-156.851 EndY=-151.675 EndZ=0
    g1: LineSegment StartX=-156.851 StartY=-490.042 StartZ=0 EndX=-156.851 EndY=-582.842 EndZ=0
    g2: LineSegment StartX=-156.851 StartY=-1014.01 StartZ=0 EndX=-156.851 EndY=-921.209 EndZ=0
    g3: LineSegment StartX=-724 StartY=-1081.38 StartZ=0 EndX=-263 EndY=-1081.38 EndZ=0
    g4: LineSegment StartX=-774 StartY=-878.103 StartZ=0 EndX=0 EndY=-878.103 EndZ=0
    g5: LineSegment StartX=-774 StartY=-846.566 StartZ=0 EndX=0 EndY=-846.566 EndZ=0
    g6: LineSegment StartX=-156.851 StartY=-710.66 StartZ=0 EndX=-156.851 EndY=-803.46 EndZ=0
    g7: LineSegment StartX=-774 StartY=-646.751 StartZ=0 EndX=-217 EndY=-646.751 EndZ=0
    g8: LineSegment StartX=-774 StartY=-446.936 StartZ=0 EndX=0 EndY=-446.936 EndZ=0
    g9: LineSegment StartX=-774 StartY=-415.399 StartZ=0 EndX=0 EndY=-415.399 EndZ=0
    g10: LineSegment StartX=-156.851 StartY=-279.493 StartZ=0 EndX=-156.851 EndY=-372.293 EndZ=0
    g11: LineSegment StartX=-774 StartY=-215.584 StartZ=0 EndX=-217 EndY=-215.584 EndZ=0
    g12: LineSegment StartX=-774 StartY=-15.7685 StartZ=0 EndX=0 EndY=-15.7685 EndZ=0
    g13: LineSegment StartX=-156.851 StartY=151.675 StartZ=0 EndX=-156.851 EndY=58.8747 EndZ=0
    g14: LineSegment StartX=-774 StartY=15.7685 StartZ=0 EndX=0 EndY=15.7685 EndZ=0
FEATURE [App::DocumentObjectGroup] Group008  label="Group"
FEATURE [App::DocumentObjectGroup] Group002  label="Unfolds"
  Group = -> [Group003,Group004,Group005,Group006,Group007,Group008]
FEATURE [PartDesign::CoordinateSystem] LCS_0008
  AttacherType = Attacher::AttachEngine3D
  MapMode = 2
  Support = -> [X_Axis044]
FEATURE [Sketcher::SketchObject] Sketch138
  FullyConstrained = true
  MapMode = 5
  Support = -> [XY_Plane045]
  expr: Constraints[16] = Sketch003.Constraints.max_r
  expr: Constraints[17] = <<main>>.end_face_width / 2
  sketch-geometry (6):
    g0: LineSegment StartX=0 StartY=0 StartZ=0 EndX=181.736 EndY=104.925 EndZ=0
    g1: LineSegment StartX=0 StartY=39.9875 StartZ=0 EndX=1 EndY=39.9875 EndZ=0
    g2: LineSegment StartX=0 StartY=209.848 StartZ=0 EndX=1 EndY=209.848 EndZ=0
    g3: ArcOfCircle CenterX=0 CenterY=0 CenterZ=0 NormalX=0 NormalY=0 NormalZ=1 AngleXU=0 Radius=40 StartAngle=0.935116 EndAngle=1.54579
    g4: ArcOfCircle CenterX=0 CenterY=0 CenterZ=0 NormalX=0 NormalY=0 NormalZ=1 AngleXU=0 Radius=209.851 StartAngle=0.599917 EndAngle=1.56603
    g5: LineSegment StartX=23.749 StartY=32.1867 StartZ=0 EndX=173.207 EndY=118.476 EndZ=0
  constraints (19):
    c: Coincident(g0,g-1)
    c: Angle(g-1,g0) = 0.523599
    c: PointOnObject(g1,g-2)
    c: Horizontal(g1)
    c: PointOnObject(g2,g-2)
    c: Horizontal(g2)
    c: Vertical(g2,g1)
    c: DistanceX(g1) = 1
    c: Coincident(g3,g0)
    c: Coincident(g3,g1)
    c: Coincident(g4,g3)
    c: Coincident(g4,g2)
    c: Coincident(g5,g3)
    c: Coincident(g5,g4)
    c: Parallel(g5,g0)
    c: PointOnObject(g0,g4)
    c: DistanceY(g2) = 209.848
    c: Distance(g4,g0) = 16
    c: Diameter(g3) = 80
FEATURE [PartDesign::CoordinateSystem] Local_CS047
  AttacherType = Attacher::AttachEngine3D
  AttachmentOffset = pos=(0,0,0) rot=(-1,0,0;0.087266rad)
  MapMode = 5
  Placement = pos=(0,0,0) rot=(-1,0,0;0.087266rad)
  Support = -> [XY_Plane045]
FEATURE [PartDesign::CoordinateSystem] LCS_0009
  AttacherType = Attacher::AttachEngine3D
  MapMode = 2
  Support = -> [X_Axis045]
FEATURE [App::Part] tech_sector
  Group = -> [LCS_0009,tech_mid,tech_pillar,Body_6,Body001003005003004,Body001003005003014]
  Origin = -> Origin045
FEATURE [PartDesign::CoordinateSystem] Local_CS048
  AttacherType = Attacher::AttachEngine3D
  AttachmentOffset = pos=(0,0,0) rot=(0.043053,-0.160675,0.986068;0.530656rad)
  MapMode = 5
  Placement = pos=(0,0,0) rot=(0.043053,-0.160675,0.986068;0.530656rad)
  Support = -> [XY_Plane045]
FEATURE [PartDesign::Line] DatumLine
  AttacherType = Attacher::AttachEngineLine
  Length = 20
  MapMode = 16
  Placement = pos=(0,0,0) rot=(0.363387,0.629406,0.686876;2.3865rad)
  ResizeMode = 0
  Support = -> [Local_CS048]
FEATURE [PartDesign::CoordinateSystem] Local_CS049
  AttacherType = Attacher::AttachEngine3D
  AttachmentOffset = pos=(0,0,0) rot=(0,0,-1;0.523599rad)
  MapMode = 5
  Placement = pos=(0,0,0) rot=(0.5,-0.866025,0;0.087266rad)
  Support = -> [Local_CS048]
FEATURE [Sketcher::SketchObject] Sketch139
  AttachmentOffset = pos=(0,0,0) rot=(1,0,0;1.48353rad)
  FullyConstrained = true
  MapMode = 5
  Placement = pos=(0,0,0) rot=(0.998509,-0.040244,0.036877;1.52867rad)
  Support = -> [Local_CS049]
  expr: Constraints[3] = 5
  sketch-geometry (2):
    g0: LineSegment StartX=0 StartY=0 StartZ=0 EndX=400 EndY=34.9955 EndZ=0
    g1: LineSegment StartX=0 StartY=0 StartZ=0 EndX=-400 EndY=34.9955 EndZ=0
  constraints (5):
    c: Coincident(g0,g-1)
    c: Coincident(g1,g0)
    c: Symmetric(g0,g1,g-2)
    c: Angle(g-1,g0) = 0.0872665
    c: DistanceX(g0) = 400
FEATURE [PartDesign::FeaturePython] BaseBend010  # WARN: FeaturePython — macro-defined, semantics opaque (R4)
  BendSide = 0
  BendSketch = -> Sketch139
  MidPlane = false
  Reverse = true
  length = 500
  radius = 0.1
  thickness = 0.3
FEATURE [Sketcher::SketchObject] Sketch140
  AttachmentOffset = pos=(0,0,0) rot=(0,1,0;-0.087266rad)
  ExternalGeometry = -> [Sketch138]
  FullyConstrained = false
  MapMode = 5
  Placement = pos=(0,0,0) rot=(-0.258803,0.965864,0.0113;6.1146rad)
  Support = -> [Local_CS049]
  sketch-geometry (14):
    g0: LineSegment StartX=23.2598 StartY=32.117 StartZ=0 EndX=170.272 EndY=118.078 EndZ=0
    g1: ArcOfEllipse CenterX=1 CenterY=7.19572 CenterZ=0 NormalX=0 NormalY=0 NormalZ=1 MajorRadius=202.441 MinorRadius=202.319 AngleXU=-1.5708 StartAngle=2.15044 EndAngle=3.14159
    g2: LineSegment StartX=1 StartY=-195.245 StartZ=0 EndX=1 EndY=209.636 EndZ=0
    g3: LineSegment StartX=203.319 StartY=7.19572 StartZ=0 EndX=-201.319 EndY=7.19572 EndZ=0
    g4: GeomPoint X=1 Y=0.187598 Z=0
    g5: GeomPoint X=1 Y=14.2038 Z=0
    g6: LineSegment StartX=0 StartY=209.636 StartZ=0 EndX=1 EndY=209.636 EndZ=0
    g7: LineSegment StartX=0 StartY=39.0768 StartZ=0 EndX=1 EndY=39.0768 EndZ=0
    g8: ArcOfCircle CenterX=1 CenterY=0 CenterZ=0 NormalX=0 NormalY=0 NormalZ=1 AngleXU=0 Radius=39.0768 StartAngle=0.964726 EndAngle=1.5708
    g9: LineSegment StartX=0 StartY=-278.705 StartZ=0 EndX=616.451 EndY=-278.705 EndZ=0
    g10: LineSegment StartX=616.451 StartY=-278.705 StartZ=0 EndX=616.451 EndY=663.316 EndZ=0
    g11: LineSegment StartX=616.451 StartY=663.316 StartZ=0 EndX=0 EndY=663.316 EndZ=0
    g12: LineSegment StartX=0 StartY=663.316 StartZ=0 EndX=0 EndY=209.636 EndZ=0
    g13: LineSegment StartX=0 StartY=39.0768 StartZ=0 EndX=0 EndY=-278.705 EndZ=0
  constraints (27):
    c: Coincident(g0,g-3)
    c: Coincident(g0,g-3)
    c: InternalAlignment(g2-g5 -> g1) x4
    c: Horizontal(g3)
    c: Coincident(g1,g0)
    c: PointOnObject(g6,g-2)
    c: Horizontal(g6)
    c: Tangent(g1,g6) = 1.5708
    c: PointOnObject(g7,g-2)
    c: Horizontal(g7)
    c: Coincident(g8,g0)
    c: Tangent(g7,g8) = 1.5708
    c: Vertical(g7,g1)
    c: DistanceX(g1) = 1
    c: PointOnObject(g1,g-4)
    c: Horizontal(g8,g-4)
    c: Coincident(g9,g10)
    c: Coincident(g10,g11)
    c: Coincident(g11,g12)
    c: Coincident(g13,g9)
    c: Horizontal(g9)
    c: Horizontal(g11)
    c: Vertical(g10)
    c: Vertical(g12)
    c: PointOnObject(g9,g-2)
    c: Coincident(g13,g7)
    c: Coincident(g12,g6)
FEATURE [Sketcher::SketchObject] Sketch141
  AttachmentOffset = pos=(0,0,0) rot=(1,0,0;-0.087266rad)
  ExternalGeometry = -> [Sketch140]
  FullyConstrained = false
  MapMode = 5
  Placement = pos=(0,0,0) rot=(1,0,0;6.19592rad)
  Support = -> [XY_Plane045]
  sketch-geometry (10):
    g0: LineSegment StartX=-0.5 StartY=38.7427 StartZ=0 EndX=-0.5 EndY=0 EndZ=0
    g1: LineSegment StartX=-0.5 StartY=0 StartZ=0 EndX=0.5 EndY=0 EndZ=0
    g2: LineSegment StartX=0.5 StartY=0 StartZ=0 EndX=0.5 EndY=38.7427 EndZ=0
    g3: LineSegment StartX=0.5 StartY=38.7427 StartZ=0 EndX=-0.5 EndY=38.7427 EndZ=0
    g4: GeomPoint X=0 Y=19.3713 Z=0
    g5: LineSegment StartX=-0.5 StartY=207.844 StartZ=0 EndX=-0.5 EndY=768.027 EndZ=0
    g6: LineSegment StartX=-0.5 StartY=768.027 StartZ=0 EndX=0.5 EndY=768.027 EndZ=0
    g7: LineSegment StartX=0.5 StartY=768.027 StartZ=0 EndX=0.5 EndY=207.844 EndZ=0
    g8: LineSegment StartX=0.5 StartY=207.844 StartZ=0 EndX=-0.5 EndY=207.844 EndZ=0
    g9: GeomPoint X=0 Y=487.936 Z=0
  constraints (25):
    c: Coincident(g0,g1)
    c: Coincident(g1,g2)
    c: Coincident(g2,g3)
    c: Coincident(g3,g0)
    c: Horizontal(g1)
    c: Horizontal(g3)
    c: Vertical(g0)
    c: Vertical(g2)
    c: Symmetric(g1,g0,g4)
    c: PointOnObject(g4,g-2)
    c: PointOnObject(g1,g-1)
    c: Coincident(g5,g6)
    c: Coincident(g6,g7)
    c: Coincident(g7,g8)
    c: Coincident(g8,g5)
    c: Horizontal(g6)
    c: Horizontal(g8)
    c: Vertical(g5)
    c: Vertical(g7)
    c: Symmetric(g6,g5,g9)
    c: PointOnObject(g9,g-2)
    c: DistanceX(g6,g6) = 1
    c: DistanceX(g3,g3) = 1
    c: PointOnObject(g-4,g8)
    c: PointOnObject(g-3,g3)
FEATURE [PartDesign::Pocket] Pocket096
  BaseFeature = -> BaseBend010
  Direction = (0,-0.0871557,-0.996195)
  Length = 5
  Length2 = 5
  Midplane = true
  Profile = -> Sketch141
  ReferenceAxis = -> Sketch141 [N_Axis]
  Refine = true
  Type = 1
FEATURE [PartDesign::Pocket] Pocket095
  BaseFeature = -> Pocket096
  Direction = (0.162099,0.0432684,-0.985825)
  Length = 5
  Length2 = 5
  Midplane = true
  Profile = -> Sketch140
  ReferenceAxis = -> Sketch140 [N_Axis]
  Type = 1
FEATURE [PartDesign::Mirrored] Mirrored041
  BaseFeature = -> Pocket095
  MirrorPlane = -> YZ_Plane044
  Originals = -> [Pocket095]
  Refine = true
FEATURE [PartDesign::Body] cover_bender  label="cover_bended_material_0.30ansi"
  Group = -> [LCS_0008,Sketch138,Sketch139,BaseBend010,Local_CS047,Pocket096,Sketch140,Pocket095,Mirrored041,Sketch141,Local_CS048,DatumLine,Local_CS049]
  Origin = -> Origin044
  Tip = -> BaseBend010
FEATURE [App::DocumentObjectGroup] Parts
  Group = -> [Body001003005003015,Body001003,Body001003005,Body001003005003,Body001003005003003,Body001003005003011,Body001003005003012,Body001003005003013,Part__Feature,Body_2,Body_3,Body_4,Body001,Body_7,Body001003005003015002,Body,cover_bender,tech_sector]
FEATURE [App::Link] cover_bended_material_0_30ansi  label="cover_bended_material_0.30ansi001"
  AssemblyType = Part::Link
  AttachedBy = #LCS_0008
  AttachedTo = Body001001#Local_CS025
  AttachmentOffset = pos=(0,0,-13) rot=(0,0,1;-1.0472rad)
  LinkPlacement = pos=(0,0,144) rot=(0,0,1;5.23599rad)
  LinkedObject = -> cover_bender
  Placement = pos=(0,0,144) rot=(0,0,1;5.23599rad)
  SolverId = Asm4EE
  expr: Placement = Body001001.Placement * Local_CS025.Placement * AttachmentOffset * LCS_0008.Placement ^ -1
FEATURE [App::Part] Model
  AssemblyType = Part::Link
  Group = -> [LCS_Origin,Constraints,Variables,Configurations,Body001001,Body001003001,Body001003005002,Body001003005003002,gutter001,Body001003005003004001,Body001003005003015001,Circular_Body001003005002,Linear_Body001003001,Body_007,Circular_Body001003005003015001,cover_bended_material_0_30ansi]
  Origin = -> Origin012
  Type = Assembly
note: 5 file-system paths scrubbed to <path> (originals preserved in the JSON sidecar)
